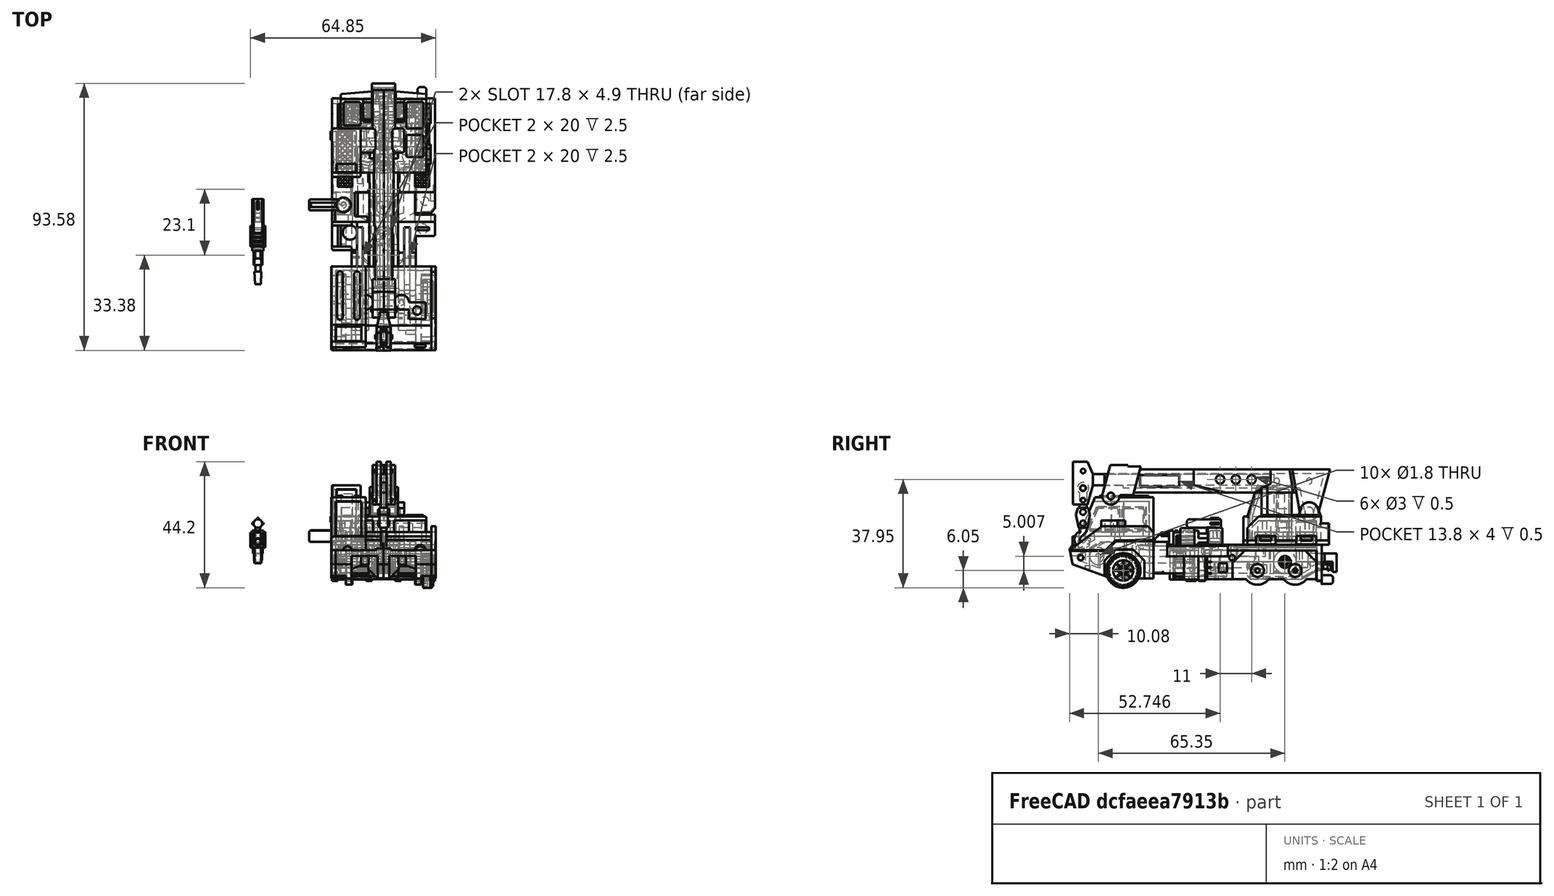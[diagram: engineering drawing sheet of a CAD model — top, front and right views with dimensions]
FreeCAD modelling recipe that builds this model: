
FCSTD DOCUMENT  (FreeCAD 1.0R39109 (Git))
Label: Hook
License: All rights reserved
LicenseURL: https://en.wikipedia.org/wiki/All_rights_reserved
objects: Sketcher::SketchObject×355, PartDesign::Pad×256, PartDesign::Pocket×171, PartDesign::Body×24, PartDesign::SubShapeBinder×17, PartDesign::Fillet×13, PartDesign::Chamfer×6, App::Link×5, Part::Mirroring×4, PartDesign::LinearPattern×2, App::Part×1, Part::Feature×1
note: 2098 computed .brp shape members not serialized (recipe doc carries the construction recipe); baked Part::Feature solids carry a one-line shape summary decoded from their .brp

FEATURE [Sketcher::SketchObject] Sketch
  ArcFitTolerance = 1e-06
  AttachmentSupport = -> [XY_Plane]
  FullyConstrained = true
  MakeInternals = false
  MapMode = 5
  sketch-geometry (4):
    g0: LineSegment StartX=0 StartY=0 StartZ=0 EndX=36 EndY=0 EndZ=0
    g1: LineSegment StartX=36 StartY=0 StartZ=0 EndX=36 EndY=43.2 EndZ=0
    g2: LineSegment StartX=36 StartY=43.2 StartZ=0 EndX=0 EndY=43.2 EndZ=0
    g3: LineSegment StartX=0 StartY=43.2 StartZ=0 EndX=0 EndY=0 EndZ=0
  constraints (11):
    c: Coincident(g0,g1)
    c: Coincident(g1,g2)
    c: Coincident(g2,g3)
    c: Coincident(g3,g0)
    c: Horizontal(g0)
    c: Horizontal(g2)
    c: Vertical(g1)
    c: Vertical(g3)
    c: Coincident(g0,g-1)
    c: DistanceY(g1,g1) = 43.2
    c: DistanceX(g2,g2) = 36
FEATURE [PartDesign::Pad] Pad
  Direction = (0,0,1)
  Length = 2
  Length2 = 10
  Profile = -> Sketch
  ReferenceAxis = -> Sketch [N_Axis]
  Refine = true
  Suppressed = false
  Type = 0
FEATURE [Sketcher::SketchObject] Sketch001
  ArcFitTolerance = 1e-06
  AttachmentSupport = -> [Pad]
  ExternalGeometry = -> [Pad]
  FullyConstrained = true
  MakeInternals = false
  MapMode = 5
  Placement = pos=(0,0,2) rot=(0,0,1;0rad)
  sketch-geometry (18):
    g0: LineSegment StartX=13.9 StartY=43.2 StartZ=0 EndX=13.9 EndY=41.4 EndZ=0
    g1: LineSegment StartX=13.9 StartY=41.4 StartZ=0 EndX=22.1 EndY=41.4 EndZ=0
    g2: LineSegment StartX=22.1 StartY=41.4 StartZ=0 EndX=22.1 EndY=43.2 EndZ=0
    g3: LineSegment StartX=22.1 StartY=43.2 StartZ=0 EndX=13.9 EndY=43.2 EndZ=0
    g4: LineSegment StartX=36 StartY=10.3 StartZ=0 EndX=23.6 EndY=10.3 EndZ=0
    g5: LineSegment StartX=23.6 StartY=10.3 StartZ=0 EndX=23.6 EndY=11.3 EndZ=0
    g6: ArcOfCircle CenterX=23.6 CenterY=12.55 CenterZ=0 NormalX=0 NormalY=0 NormalZ=1 AngleXU=0 Radius=1.25 StartAngle=1.5708 EndAngle=4.71239
    g7: LineSegment StartX=23.6 StartY=13.8 StartZ=0 EndX=23.6 EndY=18 EndZ=0
    g8: ArcOfCircle CenterX=18.1 CenterY=18 CenterZ=0 NormalX=0 NormalY=0 NormalZ=1 AngleXU=0 Radius=5.5 StartAngle=2e-16 EndAngle=3.14159
    g9: LineSegment StartX=12.6 StartY=18 StartZ=0 EndX=12.6 EndY=13.8 EndZ=0
    g10: ArcOfCircle CenterX=12.6 CenterY=12.55 CenterZ=0 NormalX=0 NormalY=0 NormalZ=1 AngleXU=0 Radius=1.25 StartAngle=4.71239 EndAngle=7.85398
    g11: LineSegment StartX=12.6 StartY=11.3 StartZ=0 EndX=12.6 EndY=10.3 EndZ=0
    g12: LineSegment StartX=12.6 StartY=10.3 StartZ=0 EndX=8 EndY=10.3 EndZ=0
    g13: LineSegment StartX=8 StartY=10.3 StartZ=0 EndX=8 EndY=1.8 EndZ=0
    g14: LineSegment StartX=8 StartY=1.8 StartZ=0 EndX=12.4 EndY=1.8 EndZ=0
    g15: LineSegment StartX=12.4 StartY=0 StartZ=0 EndX=36 EndY=0 EndZ=0
    g16: LineSegment StartX=36 StartY=0 StartZ=0 EndX=36 EndY=10.3 EndZ=0
    g17: LineSegment StartX=12.4 StartY=1.8 StartZ=0 EndX=12.4 EndY=0 EndZ=0
  constraints (58):
    c: Coincident(g0,g1)
    c: Coincident(g1,g2)
    c: Coincident(g2,g3)
    c: Coincident(g3,g0)
    c: Vertical(g0)
    c: Vertical(g2)
    c: Horizontal(g1)
    c: Horizontal(g3)
    c: PointOnObject(g0,g-3)
    c: DistanceX(g-3,g-3) = 36
    c: DistanceX(g-3,g0) = 13.9
    c: DistanceX(g2,g-3) = 13.9
    c: DistanceX(g0,g2) = 8.2
    c: DistanceY(g0,g0) = 1.8
    c: PointOnObject(g4,g-4)
    c: Horizontal(g4)
    c: DistanceY(g4,g-4) = 32.9
    c: DistanceX(g4,g4) = 12.4
    c: Coincident(g5,g4)
    c: Vertical(g5)
    c: Coincident(g6,g5)
    c: Coincident(g7,g6)
    c: Vertical(g7)
    c: Coincident(g8,g7)
    c: Coincident(g9,g8)
    c: Vertical(g9)
    c: Coincident(g10,g9)
    c: Coincident(g11,g10)
    c: Vertical(g11)
    c: Coincident(g12,g11)
    c: Horizontal(g12)
    c: Coincident(g13,g12)
    c: Vertical(g13)
    c: Coincident(g14,g13)
    c: Horizontal(g14)
    c: PointOnObject(g15,g-5)
    c: Coincident(g15,g-5)
    c: Coincident(g16,g15)
    c: Coincident(g16,g4)
    c: Diameter(g6) = 2.5
    c: Diameter(g10) = 2.5
    c: Diameter(g8) = 11
    c: DistanceX(g11,g4) = 11
    c: DistanceX(g6,g6) = 0
    c: DistanceX(g5,g6) = 0
    c: DistanceX(g10,g9) = 0
    c: DistanceX(g10,g10) = 0
    c: DistanceX(g-1,g13) = 8
    c: DistanceX(g13,g14) = 4.4
    c: Coincident(g17,g14)
    c: Coincident(g17,g15)
    c: Vertical(g17)
    c: DistanceY(g17,g17) = 1.8
    c: DistanceY(g15,g8) = 18
    c: DistanceY(g5,g5) = 1
    c: DistanceY(g11,g11) = 1
    c: DistanceY(g8,g7) = 0
    c: DistanceY(g12,g-6) = 32.9
FEATURE [PartDesign::Pocket] Pocket
  BaseFeature = -> Pad
  Direction = (0,0,-1)
  Length = 5
  Length2 = 5
  Profile = -> Sketch001
  ReferenceAxis = -> Sketch001 [N_Axis]
  Refine = true
  Suppressed = false
  Type = 0
FEATURE [Sketcher::SketchObject] Sketch002
  ArcFitTolerance = 1e-06
  AttachmentSupport = -> [Pocket]
  ExternalGeometry = -> [Pocket]
  FullyConstrained = true
  MakeInternals = false
  MapMode = 5
  Placement = pos=(0,0,2) rot=(0,0,1;0rad)
  sketch-geometry (8):
    g0: LineSegment StartX=2 StartY=41.2 StartZ=0 EndX=2 EndY=12.3 EndZ=0
    g1: LineSegment StartX=2 StartY=12.3 StartZ=0 EndX=7 EndY=12.3 EndZ=0
    g2: LineSegment StartX=7 StartY=12.3 StartZ=0 EndX=7 EndY=41.2 EndZ=0
    g3: LineSegment StartX=7 StartY=41.2 StartZ=0 EndX=2 EndY=41.2 EndZ=0
    g4: LineSegment StartX=29 StartY=41.2 StartZ=0 EndX=29 EndY=12.3 EndZ=0
    g5: LineSegment StartX=29 StartY=12.3 StartZ=0 EndX=34 EndY=12.3 EndZ=0
    g6: LineSegment StartX=34 StartY=12.3 StartZ=0 EndX=34 EndY=41.2 EndZ=0
    g7: LineSegment StartX=34 StartY=41.2 StartZ=0 EndX=29 EndY=41.2 EndZ=0
  constraints (25):
    c: Coincident(g0,g1)
    c: Coincident(g1,g2)
    c: Coincident(g2,g3)
    c: Coincident(g3,g0)
    c: Vertical(g0)
    c: Vertical(g2)
    c: Horizontal(g1)
    c: Horizontal(g3)
    c: Coincident(g4,g5)
    c: Coincident(g5,g6)
    c: Coincident(g6,g7)
    c: Coincident(g7,g4)
    c: Vertical(g4)
    c: Vertical(g6)
    c: Horizontal(g5)
    c: Horizontal(g7)
    c: DistanceX(g3,g3) = 5
    c: DistanceX(g7,g7) = 5
    c: DistanceX(g-6,g0) = 2
    c: DistanceX(g6,g-4) = 2
    c: DistanceY(g6,g-4) = 2
    c: DistanceY(g0,g-6) = 2
    c: DistanceY(g-3,g5) = 2
    c: DistanceY(g-7,g1) = 2
    c: DistanceY(g0,g0) = 28.9
FEATURE [PartDesign::Pocket] Pocket001
  BaseFeature = -> Pocket
  Direction = (0,0,-1)
  Length = 0.5
  Length2 = 5
  Profile = -> Sketch002
  ReferenceAxis = -> Sketch002 [N_Axis]
  Refine = true
  Suppressed = false
  Type = 0
FEATURE [Sketcher::SketchObject] Sketch003
  ArcFitTolerance = 1e-06
  AttachmentSupport = -> [Pocket001]
  ExternalGeometry = -> [Pocket001]
  FullyConstrained = true
  MakeInternals = false
  MapMode = 5
  Placement = pos=(0,0,1.5) rot=(0,0,1;0rad)
  sketch-geometry (36):
    g0: LineSegment StartX=30.625 StartY=41.2 StartZ=0 EndX=29.875 EndY=40.45 EndZ=0
    g1: LineSegment StartX=29.875 StartY=40.45 StartZ=0 EndX=30.625 EndY=39.7 EndZ=0
    g2: LineSegment StartX=30.625 StartY=39.7 StartZ=0 EndX=31.375 EndY=40.45 EndZ=0
    g3: LineSegment StartX=31.375 StartY=40.45 StartZ=0 EndX=30.625 EndY=41.2 EndZ=0
    g4: LineSegment [constr] StartX=29.875 StartY=40.45 StartZ=0 EndX=31.375 EndY=40.45 EndZ=0
    g5: LineSegment [constr] StartX=30.625 StartY=41.2 StartZ=0 EndX=30.625 EndY=39.7 EndZ=0
    g6: LineSegment StartX=31.625 StartY=40.45 StartZ=0 EndX=32.375 EndY=41.2 EndZ=0
    g7: LineSegment StartX=32.375 StartY=41.2 StartZ=0 EndX=33.125 EndY=40.45 EndZ=0
    g8: LineSegment StartX=33.125 StartY=40.45 StartZ=0 EndX=32.375 EndY=39.7 EndZ=0
    g9: LineSegment StartX=32.375 StartY=39.7 StartZ=0 EndX=31.625 EndY=40.45 EndZ=0
    g10: LineSegment [constr] StartX=32.375 StartY=41.2 StartZ=0 EndX=32.375 EndY=39.7 EndZ=0
    g11: LineSegment [constr] StartX=31.625 StartY=40.45 StartZ=0 EndX=33.125 EndY=40.45 EndZ=0
    g12: LineSegment StartX=29.625 StartY=40.45 StartZ=0 EndX=29 EndY=41.075 EndZ=0
    g13: LineSegment StartX=29 StartY=41.075 StartZ=0 EndX=29 EndY=39.825 EndZ=0
    g14: LineSegment StartX=29 StartY=39.825 StartZ=0 EndX=29.625 EndY=40.45 EndZ=0
    g15: LineSegment StartX=33.375 StartY=40.45 StartZ=0 EndX=34 EndY=41.075 EndZ=0
    g16: LineSegment StartX=34 StartY=41.075 StartZ=0 EndX=34 EndY=39.825 EndZ=0
    g17: LineSegment StartX=34 StartY=39.825 StartZ=0 EndX=33.375 EndY=40.45 EndZ=0
    g18: LineSegment StartX=3.625 StartY=41.2 StartZ=0 EndX=2.875 EndY=40.45 EndZ=0
    g19: LineSegment StartX=2.875 StartY=40.45 StartZ=0 EndX=3.625 EndY=39.7 EndZ=0
    g20: LineSegment StartX=3.625 StartY=39.7 StartZ=0 EndX=4.375 EndY=40.45 EndZ=0
    g21: LineSegment StartX=4.375 StartY=40.45 StartZ=0 EndX=3.625 EndY=41.2 EndZ=0
    g22: LineSegment [constr] StartX=2.875 StartY=40.45 StartZ=0 EndX=4.375 EndY=40.45 EndZ=0
    g23: LineSegment [constr] StartX=3.625 StartY=41.2 StartZ=0 EndX=3.625 EndY=39.7 EndZ=0
    g24: LineSegment StartX=4.625 StartY=40.45 StartZ=0 EndX=5.375 EndY=41.2 EndZ=0
    g25: LineSegment StartX=5.375 StartY=41.2 StartZ=0 EndX=6.125 EndY=40.45 EndZ=0
    g26: LineSegment StartX=6.125 StartY=40.45 StartZ=0 EndX=5.375 EndY=39.7 EndZ=0
    g27: LineSegment StartX=5.375 StartY=39.7 StartZ=0 EndX=4.625 EndY=40.45 EndZ=0
    g28: LineSegment [constr] StartX=5.375 StartY=41.2 StartZ=0 EndX=5.375 EndY=39.7 EndZ=0
    g29: LineSegment [constr] StartX=4.625 StartY=40.45 StartZ=0 EndX=6.125 EndY=40.45 EndZ=0
    g30: LineSegment StartX=2.625 StartY=40.45 StartZ=0 EndX=2 EndY=41.075 EndZ=0
    g31: LineSegment StartX=2 StartY=41.075 StartZ=0 EndX=2 EndY=39.825 EndZ=0
    g32: LineSegment StartX=2 StartY=39.825 StartZ=0 EndX=2.625 EndY=40.45 EndZ=0
    g33: LineSegment StartX=6.375 StartY=40.45 StartZ=0 EndX=7 EndY=41.075 EndZ=0
    g34: LineSegment StartX=7 StartY=41.075 StartZ=0 EndX=7 EndY=39.825 EndZ=0
    g35: LineSegment StartX=7 StartY=39.825 StartZ=0 EndX=6.375 EndY=40.45 EndZ=0
  constraints (101):
    c: DistanceX(g-3,g-3) = 5
    c: Coincident(g2,g1)
    c: Coincident(g3,g2)
    c: Coincident(g3,g0)
    c: Coincident(g4,g0)
    c: Coincident(g4,g2)
    c: Coincident(g5,g0)
    c: Coincident(g5,g1)
    c: Horizontal(g4)
    c: Vertical(g5)
    c: DistanceX(g4,g4) = 1.5
    c: Angle(g3,g2) = 1.5708
    c: Angle(g0,g3) = 1.5708
    c: Angle(g2,g1) = 1.5708
    c: Coincident(g1,g0)
    c: Coincident(g7,g6)
    c: Coincident(g8,g7)
    c: Coincident(g9,g8)
    c: Coincident(g9,g6)
    c: Coincident(g10,g6)
    c: Coincident(g10,g8)
    c: Coincident(g11,g6)
    c: Coincident(g11,g7)
    c: Horizontal(g11)
    c: Vertical(g10)
    c: DistanceX(g11,g11) = 1.5
    c: Angle(g7,g8) = 1.5708
    c: Angle(g6,g7) = 1.5708
    c: Angle(g8,g9) = 1.5708
    c: DistanceX(g2,g6) = 0.25
    c: DistanceY(g2,g6) = 0
    c: Coincident(g13,g12)
    c: Vertical(g13)
    c: Coincident(g14,g13)
    c: Coincident(g14,g12)
    c: DistanceX(g12,g0) = 0.25
    c: DistanceY(g12,g0) = 0
    c: Angle(g12,g14) = 1.5708
    c: Coincident(g16,g15)
    c: Vertical(g16)
    c: Coincident(g17,g16)
    c: Coincident(g17,g15)
    c: DistanceX(g7,g15) = 0.25
    c: DistanceY(g15,g7) = 0
    c: Angle(g17,g15) = 1.5708
    c: Angle(g13,g12) = 0.785398
    c: Angle(g15,g16) = 0.785398
    c: DistanceX(g15,g15) = 0.625
    c: DistanceX(g12,g12) = 0.625
    c: Coincident(g20,g19)
    c: Coincident(g21,g20)
    c: Coincident(g21,g18)
    c: Coincident(g22,g18)
    c: Coincident(g22,g20)
    c: Coincident(g23,g18)
    c: Coincident(g23,g19)
    c: Horizontal(g22)
    c: Vertical(g23)
    c: DistanceX(g22,g22) = 1.5
    c: Angle(g21,g20) = 1.5708
    c: Angle(g18,g21) = 1.5708
    c: Angle(g20,g19) = 1.5708
    c: Coincident(g19,g18)
    c: Coincident(g25,g24)
    c: Coincident(g26,g25)
    c: Coincident(g27,g26)
    c: Coincident(g27,g24)
    c: Coincident(g28,g24)
    c: Coincident(g28,g26)
    c: Coincident(g29,g24)
    c: Coincident(g29,g25)
    c: Horizontal(g29)
    c: Vertical(g28)
    c: DistanceX(g29,g29) = 1.5
    c: Angle(g25,g26) = 1.5708
    c: Angle(g24,g25) = 1.5708
    c: Angle(g26,g27) = 1.5708
    c: DistanceX(g20,g24) = 0.25
    c: DistanceY(g20,g24) = 0
    c: Coincident(g31,g30)
    c: Vertical(g31)
    c: Coincident(g32,g31)
    c: Coincident(g32,g30)
    c: DistanceX(g30,g18) = 0.25
    c: DistanceY(g30,g18) = 0
    c: Angle(g30,g32) = 1.5708
    c: Coincident(g34,g33)
    c: Vertical(g34)
    c: Coincident(g35,g34)
    c: Coincident(g35,g33)
    c: DistanceX(g25,g33) = 0.25
    c: DistanceY(g33,g25) = 0
    c: Angle(g35,g33) = 1.5708
    c: Angle(g31,g30) = 0.785398
    c: Angle(g33,g34) = 0.785398
    c: DistanceX(g33,g33) = 0.625
    c: DistanceX(g30,g30) = 0.625
    c: PointOnObject(g0,g-5)
    c: PointOnObject(g12,g-6)
    c: PointOnObject(g18,g-3)
    c: PointOnObject(g30,g-4)
FEATURE [PartDesign::Pocket] Pocket002
  BaseFeature = -> Pocket001
  Direction = (0,0,-1)
  Length = 0.5
  Length2 = 5
  Profile = -> Sketch003
  ReferenceAxis = -> Sketch003 [N_Axis]
  Refine = true
  Suppressed = false
  Type = 0
FEATURE [PartDesign::LinearPattern] LinearPattern
  BaseFeature = -> Pocket002
  Direction = -> Sketch003 [V_Axis]
  Length = 27.398
  Mode = 1
  Occurrences = 15
  Offset = 1.957
  Originals = -> [Pocket002]
  Refine = true
  Reversed = true
  Suppressed = false
  TransformMode = 0
FEATURE [Sketcher::SketchObject] Sketch004
  ArcFitTolerance = 1e-06
  AttachmentSupport = -> [LinearPattern]
  ExternalGeometry = -> [LinearPattern]
  FullyConstrained = true
  MakeInternals = false
  MapMode = 5
  Placement = pos=(0,0,1.5) rot=(0,0,1;0rad)
  sketch-geometry (36):
    g0: LineSegment StartX=2.125 StartY=41.2 StartZ=0 EndX=3.375 EndY=41.2 EndZ=0
    g1: LineSegment StartX=3.375 StartY=41.2 StartZ=0 EndX=2.75 EndY=40.575 EndZ=0
    g2: LineSegment StartX=2.75 StartY=40.575 StartZ=0 EndX=2.125 EndY=41.2 EndZ=0
    g3: LineSegment StartX=3.875 StartY=41.2 StartZ=0 EndX=5.125 EndY=41.2 EndZ=0
    g4: LineSegment StartX=5.125 StartY=41.2 StartZ=0 EndX=4.5 EndY=40.575 EndZ=0
    g5: LineSegment StartX=4.5 StartY=40.575 StartZ=0 EndX=3.875 EndY=41.2 EndZ=0
    g6: LineSegment StartX=5.625 StartY=41.2 StartZ=0 EndX=6.875 EndY=41.2 EndZ=0
    g7: LineSegment StartX=6.875 StartY=41.2 StartZ=0 EndX=6.25 EndY=40.575 EndZ=0
    g8: LineSegment StartX=6.25 StartY=40.575 StartZ=0 EndX=5.625 EndY=41.2 EndZ=0
    g9: LineSegment StartX=6.877 StartY=12.3 StartZ=0 EndX=5.623 EndY=12.3 EndZ=0
    g10: LineSegment StartX=5.623 StartY=12.3 StartZ=0 EndX=6.25 EndY=12.927 EndZ=0
    g11: LineSegment StartX=6.25 StartY=12.927 StartZ=0 EndX=6.877 EndY=12.3 EndZ=0
    g12: LineSegment StartX=3.873 StartY=12.3 StartZ=0 EndX=5.127 EndY=12.3 EndZ=0
    g13: LineSegment StartX=5.127 StartY=12.3 StartZ=0 EndX=4.5 EndY=12.927 EndZ=0
    g14: LineSegment StartX=4.5 StartY=12.927 StartZ=0 EndX=3.873 EndY=12.3 EndZ=0
    g15: LineSegment StartX=3.377 StartY=12.3 StartZ=0 EndX=2.123 EndY=12.3 EndZ=0
    g16: LineSegment StartX=2.123 StartY=12.3 StartZ=0 EndX=2.75 EndY=12.927 EndZ=0
    g17: LineSegment StartX=2.75 StartY=12.927 StartZ=0 EndX=3.377 EndY=12.3 EndZ=0
    g18: LineSegment StartX=29.125 StartY=41.2 StartZ=0 EndX=30.375 EndY=41.2 EndZ=0
    g19: LineSegment StartX=30.375 StartY=41.2 StartZ=0 EndX=29.75 EndY=40.575 EndZ=0
    g20: LineSegment StartX=29.75 StartY=40.575 StartZ=0 EndX=29.125 EndY=41.2 EndZ=0
    g21: LineSegment StartX=30.875 StartY=41.2 StartZ=0 EndX=32.125 EndY=41.2 EndZ=0
    g22: LineSegment StartX=32.125 StartY=41.2 StartZ=0 EndX=31.5 EndY=40.575 EndZ=0
    g23: LineSegment StartX=31.5 StartY=40.575 StartZ=0 EndX=30.875 EndY=41.2 EndZ=0
    g24: LineSegment StartX=32.625 StartY=41.2 StartZ=0 EndX=33.875 EndY=41.2 EndZ=0
    g25: LineSegment StartX=33.875 StartY=41.2 StartZ=0 EndX=33.25 EndY=40.575 EndZ=0
    g26: LineSegment StartX=33.25 StartY=40.575 StartZ=0 EndX=32.625 EndY=41.2 EndZ=0
    g27: LineSegment StartX=29.123 StartY=12.3 StartZ=0 EndX=30.377 EndY=12.3 EndZ=0
    g28: LineSegment StartX=30.377 StartY=12.3 StartZ=0 EndX=29.75 EndY=12.927 EndZ=0
    g29: LineSegment StartX=29.75 StartY=12.927 StartZ=0 EndX=29.123 EndY=12.3 EndZ=0
    g30: LineSegment StartX=30.873 StartY=12.3 StartZ=0 EndX=32.127 EndY=12.3 EndZ=0
    g31: LineSegment StartX=32.127 StartY=12.3 StartZ=0 EndX=31.5 EndY=12.927 EndZ=0
    g32: LineSegment StartX=31.5 StartY=12.927 StartZ=0 EndX=30.873 EndY=12.3 EndZ=0
    g33: LineSegment StartX=32.623 StartY=12.3 StartZ=0 EndX=33.877 EndY=12.3 EndZ=0
    g34: LineSegment StartX=33.877 StartY=12.3 StartZ=0 EndX=33.25 EndY=12.927 EndZ=0
    g35: LineSegment StartX=33.25 StartY=12.927 StartZ=0 EndX=32.623 EndY=12.3 EndZ=0
  constraints (109):
    c: PointOnObject(g0,g-5)
    c: PointOnObject(g0,g-5)
    c: Coincident(g1,g0)
    c: Coincident(g2,g1)
    c: Coincident(g2,g0)
    c: DistanceX(g-4,g-3) = 0.25
    c: DistanceX(g-4,g1) = 0.125
    c: DistanceY(g-4,g1) = 0.125
    c: Parallel(g1,g-3)
    c: Parallel(g2,g-4)
    c: PointOnObject(g3,g-6)
    c: PointOnObject(g3,g-6)
    c: Coincident(g4,g3)
    c: Coincident(g5,g4)
    c: Coincident(g5,g3)
    c: PointOnObject(g6,g-9)
    c: PointOnObject(g6,g-9)
    c: Coincident(g7,g6)
    c: Coincident(g8,g7)
    c: Coincident(g8,g6)
    c: DistanceX(g-7,g4) = 0.125
    c: DistanceX(g-10,g7) = 0.125
    c: Parallel(g-7,g5)
    c: Parallel(g4,g-8)
    c: Parallel(g-10,g8)
    c: Parallel(g7,g-11)
    c: DistanceY(g-7,g4) = 0.125
    c: DistanceY(g-10,g7) = 0.125
    c: PointOnObject(g9,g-14)
    c: PointOnObject(g9,g-14)
    c: Coincident(g10,g9)
    c: Coincident(g11,g10)
    c: Coincident(g11,g9)
    c: PointOnObject(g12,g-14)
    c: PointOnObject(g12,g-14)
    c: Coincident(g13,g12)
    c: Coincident(g14,g13)
    c: Coincident(g14,g12)
    c: PointOnObject(g15,g-14)
    c: PointOnObject(g15,g-14)
    c: Coincident(g16,g15)
    c: Coincident(g17,g16)
    c: Coincident(g17,g15)
    c: Parallel(g-13,g16)
    c: Parallel(g17,g-12)
    c: Parallel(g-16,g14)
    c: Parallel(g13,g-15)
    c: Parallel(g-17,g10)
    c: Parallel(g11,g-18)
    c: DistanceX(g-17,g10) = 0.125
    c: DistanceX(g-16,g13) = 0.125
    c: DistanceX(g16,g-12) = 0.125
    c: DistanceY(g16,g-13) = 0.125
    c: DistanceY(g13,g-16) = 0.125
    c: DistanceY(g10,g-17) = 0.125
    c: PointOnObject(g18,g-19)
    c: PointOnObject(g18,g-19)
    c: Coincident(g19,g18)
    c: Coincident(g20,g19)
    c: Coincident(g20,g18)
    c: PointOnObject(g21,g-22)
    c: PointOnObject(g21,g-22)
    c: Coincident(g22,g21)
    c: Coincident(g23,g22)
    c: Coincident(g23,g21)
    c: PointOnObject(g24,g-25)
    c: PointOnObject(g24,g-25)
    c: Coincident(g25,g24)
    c: Coincident(g26,g25)
    c: Coincident(g26,g24)
    c: Parallel(g-26,g26)
    c: Parallel(g25,g-27)
    c: Parallel(g22,g-24)
    c: Parallel(g23,g-23)
    c: Parallel(g-21,g19)
    c: Parallel(g20,g-20)
    c: DistanceX(g-20,g19) = 0.125
    c: DistanceX(g-23,g22) = 0.125
    c: DistanceX(g-26,g25) = 0.125
    c: DistanceY(g-26,g25) = 0.125
    c: DistanceY(g-23,g22) = 0.125
    c: DistanceY(g-20,g19) = 0.125
    c: PointOnObject(g27,g-30)
    c: PointOnObject(g27,g-30)
    c: Coincident(g28,g27)
    c: Coincident(g29,g28)
    c: Coincident(g29,g27)
    c: PointOnObject(g30,g-30)
    c: PointOnObject(g30,g-30)
    c: Coincident(g31,g30)
    c: Coincident(g32,g31)
    c: Coincident(g32,g30)
    c: PointOnObject(g33,g-30)
    c: PointOnObject(g33,g-30)
    c: Coincident(g34,g33)
    c: Coincident(g35,g34)
    c: Coincident(g35,g33)
    c: Parallel(g29,g-28)
    c: Parallel(g28,g-29)
    c: Parallel(g32,g-31)
    c: Parallel(g31,g-32)
    c: Parallel(g35,g-33)
    c: Parallel(g34,g-34)
    c: DistanceX(g-28,g28) = 0.125
    c: DistanceX(g-31,g31) = 0.125
    c: DistanceX(g-33,g34) = 0.125
    c: DistanceY(g28,g-28) = 0.125
    c: DistanceY(g31,g-31) = 0.125
    c: DistanceY(g34,g-33) = 0.125
FEATURE [PartDesign::Pocket] Pocket003
  BaseFeature = -> LinearPattern
  Direction = (0,0,-1)
  Length = 0.5
  Length2 = 5
  Profile = -> Sketch004
  ReferenceAxis = -> Sketch004 [N_Axis]
  Refine = true
  Suppressed = false
  Type = 0
FEATURE [Sketcher::SketchObject] Sketch005
  ArcFitTolerance = 1e-06
  AttachmentSupport = -> [Pocket003]
  ExternalGeometry = -> [Pocket003]
  FullyConstrained = true
  MakeInternals = false
  MapMode = 5
  Placement = pos=(0,0,1.5) rot=(0,0,1;0rad)
  sketch-geometry (36):
    g0: LineSegment StartX=2.75 StartY=40.22 StartZ=0 EndX=2 EndY=39.47 EndZ=0
    g1: LineSegment StartX=2 StartY=39.47 StartZ=0 EndX=2.75 EndY=38.72 EndZ=0
    g2: LineSegment StartX=2.75 StartY=38.72 StartZ=0 EndX=3.5 EndY=39.47 EndZ=0
    g3: LineSegment StartX=3.5 StartY=39.47 StartZ=0 EndX=2.75 EndY=40.22 EndZ=0
    g4: LineSegment StartX=4.5 StartY=40.22 StartZ=0 EndX=3.75 EndY=39.47 EndZ=0
    g5: LineSegment StartX=3.75 StartY=39.47 StartZ=0 EndX=4.5 EndY=38.72 EndZ=0
    g6: LineSegment StartX=4.5 StartY=38.72 StartZ=0 EndX=5.25 EndY=39.47 EndZ=0
    g7: LineSegment StartX=5.25 StartY=39.47 StartZ=0 EndX=4.5 EndY=40.22 EndZ=0
    g8: LineSegment StartX=6.25 StartY=40.22 StartZ=0 EndX=5.5 EndY=39.47 EndZ=0
    g9: LineSegment StartX=5.5 StartY=39.47 StartZ=0 EndX=6.25 EndY=38.72 EndZ=0
    g10: LineSegment StartX=6.25 StartY=38.72 StartZ=0 EndX=7 EndY=39.47 EndZ=0
    g11: LineSegment StartX=7 StartY=39.47 StartZ=0 EndX=6.25 EndY=40.22 EndZ=0
    g12: LineSegment [constr] StartX=6.25 StartY=40.22 StartZ=0 EndX=6.25 EndY=38.72 EndZ=0
    g13: LineSegment [constr] StartX=4.5 StartY=40.22 StartZ=0 EndX=4.5 EndY=38.72 EndZ=0
    g14: LineSegment [constr] StartX=2.75 StartY=40.22 StartZ=0 EndX=2.75 EndY=38.72 EndZ=0
    g15: LineSegment [constr] StartX=3.5 StartY=39.47 StartZ=0 EndX=2 EndY=39.47 EndZ=0
    g16: LineSegment [constr] StartX=5.25 StartY=39.47 StartZ=0 EndX=3.75 EndY=39.47 EndZ=0
    g17: LineSegment [constr] StartX=7 StartY=39.47 StartZ=0 EndX=5.5 EndY=39.47 EndZ=0
    g18: LineSegment StartX=29.75 StartY=40.22 StartZ=0 EndX=29 EndY=39.47 EndZ=0
    g19: LineSegment StartX=29 StartY=39.47 StartZ=0 EndX=29.75 EndY=38.72 EndZ=0
    g20: LineSegment StartX=29.75 StartY=38.72 StartZ=0 EndX=30.5 EndY=39.47 EndZ=0
    g21: LineSegment StartX=30.5 StartY=39.47 StartZ=0 EndX=29.75 EndY=40.22 EndZ=0
    g22: LineSegment StartX=31.5 StartY=40.22 StartZ=0 EndX=30.75 EndY=39.47 EndZ=0
    g23: LineSegment StartX=30.75 StartY=39.47 StartZ=0 EndX=31.5 EndY=38.72 EndZ=0
    g24: LineSegment StartX=31.5 StartY=38.72 StartZ=0 EndX=32.25 EndY=39.47 EndZ=0
    g25: LineSegment StartX=32.25 StartY=39.47 StartZ=0 EndX=31.5 EndY=40.22 EndZ=0
    g26: LineSegment StartX=33.25 StartY=40.22 StartZ=0 EndX=32.5 EndY=39.47 EndZ=0
    g27: LineSegment StartX=32.5 StartY=39.47 StartZ=0 EndX=33.25 EndY=38.72 EndZ=0
    g28: LineSegment StartX=33.25 StartY=38.72 StartZ=0 EndX=34 EndY=39.47 EndZ=0
    g29: LineSegment StartX=34 StartY=39.47 StartZ=0 EndX=33.25 EndY=40.22 EndZ=0
    g30: LineSegment [constr] StartX=30.5 StartY=39.47 StartZ=0 EndX=29 EndY=39.47 EndZ=0
    g31: LineSegment [constr] StartX=29.75 StartY=40.22 StartZ=0 EndX=29.75 EndY=38.72 EndZ=0
    g32: LineSegment [constr] StartX=31.5 StartY=40.22 StartZ=0 EndX=31.5 EndY=38.72 EndZ=0
    g33: LineSegment [constr] StartX=32.25 StartY=39.47 StartZ=0 EndX=30.75 EndY=39.47 EndZ=0
    g34: LineSegment [constr] StartX=33.25 StartY=40.22 StartZ=0 EndX=33.25 EndY=38.72 EndZ=0
    g35: LineSegment [constr] StartX=34 StartY=39.47 StartZ=0 EndX=32.5 EndY=39.47 EndZ=0
  constraints (97):
    c: Coincident(g1,g0)
    c: Coincident(g2,g1)
    c: Coincident(g3,g2)
    c: Coincident(g3,g0)
    c: Coincident(g5,g4)
    c: Coincident(g6,g5)
    c: Coincident(g7,g6)
    c: Coincident(g7,g4)
    c: Coincident(g9,g8)
    c: Coincident(g10,g9)
    c: Coincident(g11,g10)
    c: Coincident(g11,g8)
    c: Coincident(g12,g8)
    c: Coincident(g12,g9)
    c: Vertical(g12)
    c: Coincident(g13,g4)
    c: Coincident(g13,g5)
    c: Vertical(g13)
    c: Coincident(g14,g0)
    c: Coincident(g14,g1)
    c: Coincident(g15,g2)
    c: Coincident(g15,g0)
    c: Horizontal(g15)
    c: Coincident(g16,g6)
    c: Coincident(g16,g4)
    c: Horizontal(g16)
    c: Coincident(g17,g10)
    c: Coincident(g17,g8)
    c: Horizontal(g17)
    c: Vertical(g14)
    c: DistanceX(g15,g15) = 1.5
    c: DistanceX(g16,g16) = 1.5
    c: DistanceX(g17,g17) = 1.5
    c: Angle(g3,g2) = 1.5708
    c: Angle(g0,g3) = 1.5708
    c: Angle(g2,g1) = 1.5708
    c: Angle(g7,g6) = 1.5708
    c: Angle(g4,g7) = 1.5708
    c: Angle(g6,g5) = 1.5708
    c: Angle(g11,g10) = 1.5708
    c: Angle(g8,g11) = 1.5708
    c: Angle(g10,g9) = 1.5708
    c: PointOnObject(g10,g-15)
    c: PointOnObject(g0,g-16)
    c: DistanceY(g0,g-3) = 0.23
    c: DistanceY(g4,g-8) = 0.23
    c: DistanceY(g8,g-12) = 0.23
    c: DistanceX(g4,g-18) = 0
    c: DistanceY(g-6,g1) = 0.227
    c: Coincident(g19,g18)
    c: Coincident(g20,g19)
    c: Coincident(g21,g20)
    c: Coincident(g21,g18)
    c: Coincident(g23,g22)
    c: Coincident(g24,g23)
    c: Coincident(g25,g24)
    c: Coincident(g25,g22)
    c: Coincident(g27,g26)
    c: Coincident(g28,g27)
    c: Coincident(g29,g28)
    c: Coincident(g29,g26)
    c: Coincident(g30,g20)
    c: Coincident(g30,g18)
    c: Horizontal(g30)
    c: Coincident(g31,g18)
    c: Coincident(g31,g19)
    c: Coincident(g32,g22)
    c: Coincident(g32,g23)
    c: Vertical(g32)
    c: Coincident(g33,g24)
    c: Coincident(g33,g22)
    c: Horizontal(g33)
    c: Coincident(g34,g26)
    c: Coincident(g34,g27)
    c: Vertical(g34)
    c: Coincident(g35,g28)
    c: Coincident(g35,g26)
    c: Horizontal(g35)
    c: Vertical(g31)
    c: DistanceX(g30,g30) = 1.5
    c: DistanceX(g33,g33) = 1.5
    c: DistanceX(g35,g35) = 1.5
    c: Angle(g29,g28) = 1.5708
    c: Angle(g25,g24) = 1.5708
    c: Angle(g21,g20) = 1.5708
    c: Angle(g18,g21) = 1.5708
    c: Angle(g20,g19) = 1.5708
    c: Angle(g22,g25) = 1.5708
    c: Angle(g24,g23) = 1.5708
    c: Angle(g26,g29) = 1.5708
    c: Angle(g28,g27) = 1.5708
    c: PointOnObject(g18,g-32)
    c: PointOnObject(g28,g-33)
    c: DistanceX(g22,g-35) = 0
    c: DistanceY(g18,g-20) = 0.23
    c: DistanceY(g22,g-25) = 0.23
    c: DistanceY(g26,g-29) = 0.23
FEATURE [PartDesign::Pocket] Pocket004
  BaseFeature = -> Pocket003
  Direction = (0,0,-1)
  Length = 0.5
  Length2 = 5
  Profile = -> Sketch005
  ReferenceAxis = -> Sketch005 [N_Axis]
  Refine = true
  Suppressed = false
  Type = 0
FEATURE [PartDesign::LinearPattern] LinearPattern001
  BaseFeature = -> Pocket004
  Direction = -> Sketch005 [V_Axis]
  Length = 25.441
  Mode = 1
  Occurrences = 14
  Offset = 1.957
  Originals = -> [Pocket004]
  Refine = true
  Reversed = true
  Suppressed = false
  TransformMode = 0
FEATURE [Sketcher::SketchObject] Sketch006
  ArcFitTolerance = 1e-06
  AttachmentSupport = -> [LinearPattern001]
  ExternalGeometry = -> [LinearPattern001]
  FullyConstrained = true
  MakeInternals = false
  MapMode = 5
  Placement = pos=(0,0,2) rot=(0,0,1;0rad)
  sketch-geometry (1):
    g0: Circle CenterX=18.1 CenterY=30.5 CenterZ=0 NormalX=0 NormalY=0 NormalZ=1 AngleXU=0 Radius=5.5
  constraints (3):
    c: DistanceX(g0,g-3) = 0
    c: Diameter(g0) = 11
    c: DistanceY(g0,g-4) = 12.7
FEATURE [PartDesign::Pad] Pad001
  BaseFeature = -> LinearPattern001
  Direction = (0,0,1)
  Length = 3
  Length2 = 10
  Profile = -> Sketch006
  ReferenceAxis = -> Sketch006 [N_Axis]
  Refine = true
  Suppressed = false
  Type = 0
FEATURE [Sketcher::SketchObject] Sketch007
  ArcFitTolerance = 1e-06
  AttachmentSupport = -> [Pad001]
  ExternalGeometry = -> [Pad001]
  FullyConstrained = true
  MakeInternals = false
  MapMode = 5
  Placement = pos=(0,0,5) rot=(0,0,1;0rad)
  sketch-geometry (1):
    g0: Circle CenterX=18.1 CenterY=30.5 CenterZ=0 NormalX=0 NormalY=0 NormalZ=1 AngleXU=0 Radius=2.5
  constraints (2):
    c: Coincident(g0,g-3)
    c: Diameter(g0) = 5
FEATURE [PartDesign::Pocket] Pocket005
  BaseFeature = -> Pad001
  Direction = (0,0,-1)
  Length = 5
  Length2 = 5
  Profile = -> Sketch007
  ReferenceAxis = -> Sketch007 [N_Axis]
  Refine = true
  Suppressed = false
  Type = 0
FEATURE [Sketcher::SketchObject] Sketch008
  ArcFitTolerance = 1e-06
  AttachmentSupport = -> [Pocket005]
  ExternalGeometry = -> [Pocket005]
  FullyConstrained = true
  MakeInternals = false
  MapMode = 5
  Placement = pos=(0,0,0) rot=(1,0,0;3.14159rad)
  sketch-geometry (1):
    g0: Circle CenterX=18.1 CenterY=-30.5 CenterZ=0 NormalX=0 NormalY=0 NormalZ=1 AngleXU=0 Radius=3.45
  constraints (2):
    c: Coincident(g0,g-3)
    c: Diameter(g0) = 6.9
FEATURE [PartDesign::Pocket] Pocket006
  BaseFeature = -> Pocket005
  Direction = (0,0,1)
  Length = 3.1
  Length2 = 5
  Profile = -> Sketch008
  ReferenceAxis = -> Sketch008 [N_Axis]
  Refine = true
  Suppressed = false
  Type = 0
FEATURE [Sketcher::SketchObject] Sketch009
  ArcFitTolerance = 1e-06
  AttachmentSupport = -> [Pocket006]
  ExternalGeometry = -> [Pocket006]
  FullyConstrained = true
  MakeInternals = false
  MapMode = 5
  Placement = pos=(0,0,0) rot=(1,0,0;3.14159rad)
  sketch-geometry (8):
    g0: LineSegment StartX=0 StartY=-43.2 StartZ=0 EndX=13.9 EndY=-43.2 EndZ=0
    g1: LineSegment StartX=13.9 StartY=-43.2 StartZ=0 EndX=13.9 EndY=-41.4 EndZ=0
    g2: LineSegment StartX=13.9 StartY=-41.4 StartZ=0 EndX=0 EndY=-41.4 EndZ=0
    g3: LineSegment StartX=0 StartY=-41.4 StartZ=0 EndX=0 EndY=-43.2 EndZ=0
    g4: LineSegment StartX=36 StartY=-43.2 StartZ=0 EndX=36 EndY=-41.4 EndZ=0
    g5: LineSegment StartX=36 StartY=-41.4 StartZ=0 EndX=22.1 EndY=-41.4 EndZ=0
    g6: LineSegment StartX=22.1 StartY=-41.4 StartZ=0 EndX=22.1 EndY=-43.2 EndZ=0
    g7: LineSegment StartX=22.1 StartY=-43.2 StartZ=0 EndX=36 EndY=-43.2 EndZ=0
  constraints (20):
    c: Coincident(g0,g1)
    c: Coincident(g1,g2)
    c: Coincident(g2,g3)
    c: Coincident(g3,g0)
    c: Horizontal(g0)
    c: Horizontal(g2)
    c: Vertical(g1)
    c: Vertical(g3)
    c: Coincident(g0,g-8)
    c: Coincident(g1,g-6)
    c: Coincident(g4,g5)
    c: Coincident(g5,g6)
    c: Coincident(g6,g7)
    c: Coincident(g7,g4)
    c: Vertical(g4)
    c: Vertical(g6)
    c: Horizontal(g5)
    c: Horizontal(g7)
    c: Coincident(g4,g-4)
    c: Coincident(g5,g-5)
FEATURE [PartDesign::Pad] Pad002
  BaseFeature = -> Pocket006
  Direction = (0,0,-1)
  Length = 10.7
  Length2 = 10
  Profile = -> Sketch009
  ReferenceAxis = -> Sketch009 [N_Axis]
  Refine = true
  Suppressed = false
  Type = 0
FEATURE [Sketcher::SketchObject] Sketch010
  ArcFitTolerance = 1e-06
  AttachmentSupport = -> [Pad002]
  ExternalGeometry = -> [Pad002]
  FullyConstrained = true
  MakeInternals = false
  MapMode = 5
  Placement = pos=(0,0,-10.7) rot=(1,0,0;3.14159rad)
  sketch-geometry (8):
    g0: LineSegment StartX=2 StartY=-41.4 StartZ=0 EndX=2 EndY=-43.2 EndZ=0
    g1: LineSegment StartX=2 StartY=-43.2 StartZ=0 EndX=11.9 EndY=-43.2 EndZ=0
    g2: LineSegment StartX=11.9 StartY=-43.2 StartZ=0 EndX=11.9 EndY=-41.4 EndZ=0
    g3: LineSegment StartX=11.9 StartY=-41.4 StartZ=0 EndX=2 EndY=-41.4 EndZ=0
    g4: LineSegment StartX=24.1 StartY=-41.4 StartZ=0 EndX=24.1 EndY=-43.2 EndZ=0
    g5: LineSegment StartX=24.1 StartY=-43.2 StartZ=0 EndX=34 EndY=-43.2 EndZ=0
    g6: LineSegment StartX=34 StartY=-43.2 StartZ=0 EndX=34 EndY=-41.4 EndZ=0
    g7: LineSegment StartX=34 StartY=-41.4 StartZ=0 EndX=24.1 EndY=-41.4 EndZ=0
  constraints (24):
    c: Coincident(g0,g1)
    c: Coincident(g1,g2)
    c: Coincident(g2,g3)
    c: Coincident(g3,g0)
    c: Vertical(g0)
    c: Vertical(g2)
    c: Horizontal(g1)
    c: Horizontal(g3)
    c: PointOnObject(g0,g-8)
    c: PointOnObject(g1,g-9)
    c: Coincident(g4,g5)
    c: Coincident(g5,g6)
    c: Coincident(g6,g7)
    c: Coincident(g7,g4)
    c: Vertical(g4)
    c: Vertical(g6)
    c: Horizontal(g5)
    c: Horizontal(g7)
    c: PointOnObject(g4,g-3)
    c: PointOnObject(g5,g-5)
    c: DistanceX(g-6,g4) = 2
    c: DistanceX(g6,g-4) = 2
    c: DistanceX(g2,g-8) = 2
    c: DistanceX(g-10,g0) = 2
FEATURE [PartDesign::Pocket] Pocket007
  BaseFeature = -> Pad002
  Direction = (0,0,1)
  Length = 0.5
  Length2 = 5
  Profile = -> Sketch010
  ReferenceAxis = -> Sketch010 [N_Axis]
  Refine = true
  Suppressed = false
  Type = 0
FEATURE [Sketcher::SketchObject] Sketch011
  ArcFitTolerance = 1e-06
  AttachmentSupport = -> [Pocket007]
  ExternalGeometry = -> [Pocket007]
  FullyConstrained = true
  MakeInternals = false
  MapMode = 5
  Placement = pos=(0,43.2,0) rot=(0,0.707107,0.707107;3.14159rad)
  sketch-geometry (1):
    g0: Circle CenterX=-31.45 CenterY=-10.2 CenterZ=0 NormalX=0 NormalY=0 NormalZ=1 AngleXU=0 Radius=1.55
  constraints (3):
    c: PointOnObject(g0,g-3)
    c: Diameter(g0) = 3.1
    c: DistanceX(g-4,g0) = 4.55
FEATURE [PartDesign::Pad] Pad003
  BaseFeature = -> Pocket007
  Direction = (0,1,-2e-16)
  Length = 4
  Length2 = 10
  Profile = -> Sketch011
  ReferenceAxis = -> Sketch011 [N_Axis]
  Refine = true
  Suppressed = false
  Type = 0
FEATURE [PartDesign::Fillet] Fillet
  Base = -> Pad003 [Edge479]
  BaseFeature = -> Pad003
  Radius = 1
  Refine = true
  SupportTransform = false
  Suppressed = false
  UseAllEdges = false
FEATURE [Sketcher::SketchObject] Sketch012
  ArcFitTolerance = 1e-06
  AttachmentSupport = -> [Fillet]
  ExternalGeometry = -> [Fillet]
  FullyConstrained = true
  MakeInternals = false
  MapMode = 5
  Placement = pos=(0,0,0) rot=(1,0,0;3.14159rad)
  sketch-geometry (4):
    g0: LineSegment StartX=11.9 StartY=-41.4 StartZ=0 EndX=24.1 EndY=-41.4 EndZ=0
    g1: LineSegment StartX=24.1 StartY=-41.4 StartZ=0 EndX=24.1 EndY=-39.4 EndZ=0
    g2: LineSegment StartX=24.1 StartY=-39.4 StartZ=0 EndX=11.9 EndY=-39.4 EndZ=0
    g3: LineSegment StartX=11.9 StartY=-39.4 StartZ=0 EndX=11.9 EndY=-41.4 EndZ=0
  constraints (10):
    c: Coincident(g0,g1)
    c: Coincident(g1,g2)
    c: Coincident(g2,g3)
    c: Coincident(g3,g0)
    c: Horizontal(g2)
    c: Vertical(g1)
    c: Vertical(g3)
    c: DistanceY(g1,g1) = 2
    c: Coincident(g0,g-7)
    c: Coincident(g0,g-6)
FEATURE [PartDesign::Pad] Pad004
  BaseFeature = -> Fillet
  Direction = (0,0,-1)
  Length = 1
  Length2 = 10
  Profile = -> Sketch012
  ReferenceAxis = -> Sketch012 [N_Axis]
  Refine = true
  Suppressed = false
  Type = 0
FEATURE [Sketcher::SketchObject] Sketch013
  ArcFitTolerance = 1e-06
  AttachmentSupport = -> [Pad004]
  ExternalGeometry = -> [Pad004]
  FullyConstrained = true
  MakeInternals = false
  MapMode = 5
  Placement = pos=(0,0,0) rot=(1,0,0;3.14159rad)
  sketch-geometry (16):
    g0: LineSegment StartX=9 StartY=-41.4 StartZ=0 EndX=9 EndY=-38.4 EndZ=0
    g1: LineSegment StartX=9 StartY=-38.4 StartZ=0 EndX=13.75 EndY=-38.4 EndZ=0
    g2: ArcOfCircle CenterX=13.75 CenterY=-37.4 CenterZ=0 NormalX=0 NormalY=0 NormalZ=1 AngleXU=0 Radius=1 StartAngle=4.71239 EndAngle=7.85398
    g3: LineSegment StartX=13.75 StartY=-36.4 StartZ=0 EndX=9 EndY=-36.4 EndZ=0
    g4: LineSegment StartX=9 StartY=-36.4 StartZ=0 EndX=9 EndY=-34.4 EndZ=0
    g5: LineSegment StartX=9 StartY=-34.4 StartZ=0 EndX=7 EndY=-34.4 EndZ=0
    g6: LineSegment StartX=7 StartY=-34.4 StartZ=0 EndX=7 EndY=-41.4 EndZ=0
    g7: LineSegment StartX=7 StartY=-41.4 StartZ=0 EndX=9 EndY=-41.4 EndZ=0
    g8: LineSegment StartX=27 StartY=-41.4 StartZ=0 EndX=29 EndY=-41.4 EndZ=0
    g9: LineSegment StartX=29 StartY=-41.4 StartZ=0 EndX=29 EndY=-34.4 EndZ=0
    g10: LineSegment StartX=29 StartY=-34.4 StartZ=0 EndX=27 EndY=-34.4 EndZ=0
    g11: LineSegment StartX=27 StartY=-34.4 StartZ=0 EndX=27 EndY=-36.4 EndZ=0
    g12: LineSegment StartX=27 StartY=-36.4 StartZ=0 EndX=22.25 EndY=-36.4 EndZ=0
    g13: LineSegment StartX=27 StartY=-41.4 StartZ=0 EndX=27 EndY=-38.4 EndZ=0
    g14: LineSegment StartX=27 StartY=-38.4 StartZ=0 EndX=22.25 EndY=-38.4 EndZ=0
    g15: ArcOfCircle CenterX=22.25 CenterY=-37.4 CenterZ=0 NormalX=0 NormalY=0 NormalZ=1 AngleXU=0 Radius=1 StartAngle=1.5708 EndAngle=4.71239
  constraints (51):
    c: PointOnObject(g0,g-4)
    c: Vertical(g0)
    c: Coincident(g1,g0)
    c: Horizontal(g1)
    c: Coincident(g2,g1)
    c: Coincident(g3,g2)
    c: Horizontal(g3)
    c: Coincident(g4,g3)
    c: Vertical(g4)
    c: Coincident(g5,g4)
    c: Horizontal(g5)
    c: Coincident(g6,g5)
    c: PointOnObject(g6,g-4)
    c: Coincident(g7,g6)
    c: Coincident(g7,g0)
    c: Vertical(g6)
    c: PointOnObject(g8,g-3)
    c: Coincident(g9,g8)
    c: Vertical(g9)
    c: Coincident(g10,g9)
    c: Horizontal(g10)
    c: Coincident(g11,g10)
    c: Coincident(g12,g11)
    c: Horizontal(g12)
    c: Coincident(g13,g8)
    c: Vertical(g13)
    c: Coincident(g14,g13)
    c: Horizontal(g14)
    c: Coincident(g15,g14)
    c: Coincident(g15,g12)
    c: Vertical(g11)
    c: DistanceX(g10,g10) = 2
    c: DistanceX(g8,g8) = 2
    c: DistanceX(g5,g5) = 2
    c: DistanceX(g7,g7) = 2
    c: DistanceY(g0,g3) = 2
    c: DistanceY(g13,g11) = 2
    c: DistanceY(g6,g6) = 7
    c: DistanceY(g9,g9) = 7
    c: DistanceX(g-5,g6) = 7
    c: DistanceX(g8,g-6) = 7
    c: DistanceX(g2,g15) = 8.5
    c: DistanceX(g15,g12) = 0
    c: DistanceX(g15,g14) = 0
    c: DistanceX(g2,g2) = 0
    c: DistanceX(g-7,g15) = 0.15
    c: DistanceY(g-9,g0) = 1
    c: DistanceY(g-9,g13) = 1
    c: DistanceX(g2,g1) = 0
    c: DistanceX(g2,g-8) = 0.15
    c: PointOnObject(g8,g-3)
FEATURE [PartDesign::Pad] Pad005
  BaseFeature = -> Pad004
  Direction = (0,0,-1)
  Length = 4
  Length2 = 10
  Profile = -> Sketch013
  ReferenceAxis = -> Sketch013 [N_Axis]
  Refine = true
  Suppressed = false
  Type = 0
FEATURE [Sketcher::SketchObject] Sketch014
  ArcFitTolerance = 1e-06
  AttachmentSupport = -> [Pad005]
  ExternalGeometry = -> [Pad005]
  FullyConstrained = true
  MakeInternals = false
  MapMode = 5
  Placement = pos=(0,0,-4) rot=(1,0,0;3.14159rad)
  sketch-geometry (2):
    g0: Circle CenterX=13.75 CenterY=-37.4 CenterZ=0 NormalX=0 NormalY=0 NormalZ=1 AngleXU=0 Radius=1
    g1: Circle CenterX=22.25 CenterY=-37.4 CenterZ=0 NormalX=0 NormalY=0 NormalZ=1 AngleXU=0 Radius=1
  constraints (4):
    c: Coincident(g0,g-4)
    c: Equal(g0,g-4)
    c: Coincident(g1,g-3)
    c: Equal(g1,g-3)
FEATURE [PartDesign::Pad] Pad006
  BaseFeature = -> Pad005
  Direction = (0,0,-1)
  Length = 2
  Length2 = 10
  Profile = -> Sketch014
  ReferenceAxis = -> Sketch014 [N_Axis]
  Refine = true
  Suppressed = false
  Type = 0
FEATURE [Sketcher::SketchObject] Sketch015
  ArcFitTolerance = 1e-06
  AttachmentSupport = -> [Pad006]
  ExternalGeometry = -> [Pad006]
  FullyConstrained = true
  MakeInternals = false
  MapMode = 5
  Placement = pos=(0,0,0) rot=(1,0,0;3.14159rad)
  sketch-geometry (14):
    g0: LineSegment StartX=29 StartY=-10.3 StartZ=0 EndX=29 EndY=-26.3 EndZ=0
    g1: LineSegment StartX=29 StartY=-26.3 StartZ=0 EndX=27 EndY=-26.3 EndZ=0
    g2: LineSegment StartX=27 StartY=-26.3 StartZ=0 EndX=27 EndY=-13.3 EndZ=0
    g3: LineSegment StartX=27 StartY=-13.3 StartZ=0 EndX=25.5 EndY=-13.3 EndZ=0
    g4: LineSegment StartX=25.5 StartY=-13.3 StartZ=0 EndX=25.5 EndY=-20.0303 EndZ=0
    g5: LineSegment StartX=25.5 StartY=-20.0303 StartZ=0 EndX=24 EndY=-24.8 EndZ=0
    g6: LineSegment StartX=24 StartY=-24.8 StartZ=0 EndX=12 EndY=-24.8 EndZ=0
    g7: LineSegment StartX=12 StartY=-24.8 StartZ=0 EndX=10.5 EndY=-20.0303 EndZ=0
    g8: LineSegment StartX=10.5 StartY=-20.0303 StartZ=0 EndX=10.5 EndY=-13.3 EndZ=0
    g9: LineSegment StartX=10.5 StartY=-13.3 StartZ=0 EndX=9 EndY=-13.3 EndZ=0
    g10: LineSegment StartX=9 StartY=-13.3 StartZ=0 EndX=9 EndY=-26.3 EndZ=0
    g11: LineSegment StartX=9 StartY=-26.3 StartZ=0 EndX=7 EndY=-26.3 EndZ=0
    g12: LineSegment StartX=7 StartY=-26.3 StartZ=0 EndX=7 EndY=-10.3 EndZ=0
    g13: LineSegment StartX=7 StartY=-10.3 StartZ=0 EndX=29 EndY=-10.3 EndZ=0
  constraints (43):
    c: PointOnObject(g0,g-4)
    c: Vertical(g0)
    c: Coincident(g1,g0)
    c: Horizontal(g1)
    c: Coincident(g2,g1)
    c: Vertical(g2)
    c: Coincident(g3,g2)
    c: Horizontal(g3)
    c: Coincident(g4,g3)
    c: Vertical(g4)
    c: Coincident(g5,g4)
    c: Coincident(g6,g5)
    c: Horizontal(g6)
    c: Coincident(g7,g6)
    c: Coincident(g8,g7)
    c: Vertical(g8)
    c: Coincident(g9,g8)
    c: Horizontal(g9)
    c: Coincident(g10,g9)
    c: Vertical(g10)
    c: Coincident(g11,g10)
    c: Horizontal(g11)
    c: Coincident(g12,g11)
    c: Vertical(g12)
    c: Coincident(g13,g12)
    c: Coincident(g13,g0)
    c: Horizontal(g13)
    c: DistanceX(g-8,g0) = 0
    c: DistanceX(g11,g-7) = 0
    c: DistanceX(g11,g11) = 2
    c: DistanceX(g1,g1) = 2
    c: DistanceX(g9,g9) = 1.5
    c: DistanceX(g3,g3) = 1.5
    c: DistanceY(g-7,g11) = 8.1
    c: DistanceY(g-8,g0) = 8.1
    c: DistanceX(g6,g6) = 12
    c: DistanceY(g10,g6) = 1.5
    c: DistanceY(g9,g12) = 3
    c: DistanceY(g2,g0) = 3
    c: DistanceX(g10,g1) = 18
    c: DistanceX(g10,g6) = 3
    c: Distance(g7) = 5
    c: Distance(g5) = 5
FEATURE [PartDesign::Pad] Pad007
  BaseFeature = -> Pad006
  Direction = (0,0,-1)
  Length = 4
  Length2 = 10
  Profile = -> Sketch015
  ReferenceAxis = -> Sketch015 [N_Axis]
  Refine = true
  Suppressed = false
  Type = 0
FEATURE [Sketcher::SketchObject] Sketch016
  ArcFitTolerance = 1e-06
  AttachmentSupport = -> [Pad007]
  ExternalGeometry = -> [Pad007]
  FullyConstrained = true
  MakeInternals = false
  MapMode = 5
  Placement = pos=(0,0,-4) rot=(1,0,0;3.14159rad)
  sketch-geometry (1):
    g0: Circle CenterX=18 CenterY=-20.4 CenterZ=0 NormalX=0 NormalY=0 NormalZ=1 AngleXU=0 Radius=2.4
  constraints (5):
    c: Diameter(g0) = 4.8
    c: DistanceY(g-4,g0) = 4.4
    c: DistanceX(g-4,g-4) = 12
    c: DistanceX(g-4,g-4) = 12
    c: DistanceX(g-4,g0) = 6
FEATURE [PartDesign::Pad] Pad008
  BaseFeature = -> Pad007
  Direction = (0,0,-1)
  Length = 2.5
  Length2 = 10
  Profile = -> Sketch016
  ReferenceAxis = -> Sketch016 [N_Axis]
  Refine = true
  Suppressed = false
  Type = 0
FEATURE [Sketcher::SketchObject] Sketch017
  ArcFitTolerance = 1e-06
  AttachmentSupport = -> [Pad008]
  ExternalGeometry = -> [Pad008]
  FullyConstrained = true
  MakeInternals = false
  MapMode = 5
  Placement = pos=(0,0,-6.5) rot=(1,0,0;3.14159rad)
  sketch-geometry (1):
    g0: Circle CenterX=18 CenterY=-20.4 CenterZ=0 NormalX=0 NormalY=0 NormalZ=1 AngleXU=0 Radius=0.75
  constraints (2):
    c: Coincident(g0,g-3)
    c: Diameter(g0) = 1.5
FEATURE [PartDesign::Pocket] Pocket008
  BaseFeature = -> Pad008
  Direction = (0,0,1)
  Length = 7
  Length2 = 5
  Profile = -> Sketch017
  ReferenceAxis = -> Sketch017 [N_Axis]
  Refine = true
  Suppressed = false
  Type = 0
FEATURE [Sketcher::SketchObject] Sketch018
  ArcFitTolerance = 1e-06
  AttachmentSupport = -> [Pocket008]
  ExternalGeometry = -> [Pocket008]
  FullyConstrained = true
  MakeInternals = false
  MapMode = 5
  Placement = pos=(0,0,0) rot=(1,0,0;3.14159rad)
  sketch-geometry (4):
    g0: LineSegment StartX=0 StartY=0 StartZ=0 EndX=0 EndY=-10.3 EndZ=0
    g1: LineSegment StartX=0 StartY=-10.3 StartZ=0 EndX=9 EndY=-10.3 EndZ=0
    g2: LineSegment StartX=9 StartY=-10.3 StartZ=0 EndX=9 EndY=0 EndZ=0
    g3: LineSegment StartX=9 StartY=0 StartZ=0 EndX=0 EndY=0 EndZ=0
  constraints (11):
    c: Coincident(g0,g1)
    c: Coincident(g1,g2)
    c: Coincident(g2,g3)
    c: Coincident(g3,g0)
    c: Vertical(g0)
    c: Vertical(g2)
    c: Horizontal(g1)
    c: Horizontal(g3)
    c: Coincident(g0,g-1)
    c: PointOnObject(g1,g-4)
    c: DistanceX(g-5,g1) = 1
FEATURE [PartDesign::Pad] Pad009
  BaseFeature = -> Pocket008
  Direction = (0,0,-1)
  Length = 2
  Length2 = 10
  Profile = -> Sketch018
  ReferenceAxis = -> Sketch018 [N_Axis]
  Refine = true
  Suppressed = false
  Type = 0
FEATURE [Sketcher::SketchObject] Sketch019
  ArcFitTolerance = 1e-06
  AttachmentSupport = -> [Pad009]
  ExternalGeometry = -> [Pad009]
  FullyConstrained = true
  MakeInternals = false
  MapMode = 5
  Placement = pos=(0,0,-4) rot=(1,0,0;3.14159rad)
  sketch-geometry (4):
    g0: LineSegment StartX=7 StartY=-10.3 StartZ=0 EndX=29 EndY=-10.3 EndZ=0
    g1: LineSegment StartX=29 StartY=-10.3 StartZ=0 EndX=29 EndY=0 EndZ=0
    g2: LineSegment StartX=29 StartY=0 StartZ=0 EndX=7 EndY=0 EndZ=0
    g3: LineSegment StartX=7 StartY=0 StartZ=0 EndX=7 EndY=-10.3 EndZ=0
  constraints (10):
    c: Coincident(g0,g1)
    c: Coincident(g1,g2)
    c: Coincident(g2,g3)
    c: Coincident(g3,g0)
    c: Horizontal(g2)
    c: Vertical(g1)
    c: Vertical(g3)
    c: Coincident(g0,g-3)
    c: PointOnObject(g1,g-1)
    c: Coincident(g0,g-3)
FEATURE [PartDesign::Pad] Pad010
  BaseFeature = -> Pad009
  Direction = (0,0,-1)
  Length = 2
  Length2 = 10
  Profile = -> Sketch019
  ReferenceAxis = -> Sketch019 [N_Axis]
  Refine = true
  Reversed = true
  Suppressed = false
  Type = 0
FEATURE [PartDesign::Pad] Pad011
  BaseFeature = -> Pad010
  Direction = (0,0,-1)
  Length = 2
  Length2 = 10
  Profile = -> Pad010 [Face53]
  Refine = true
  Suppressed = false
  Type = 0
FEATURE [Sketcher::SketchObject] Sketch020
  ArcFitTolerance = 1e-06
  AttachmentSupport = -> [Pad011]
  ExternalGeometry = -> [Pad011]
  FullyConstrained = true
  MakeInternals = false
  MapMode = 5
  Placement = pos=(0,0,-2) rot=(1,0,0;3.14159rad)
  sketch-geometry (4):
    g0: LineSegment StartX=0 StartY=0 StartZ=0 EndX=0 EndY=-2.5 EndZ=0
    g1: LineSegment StartX=0 StartY=-2.5 StartZ=0 EndX=7 EndY=-2.5 EndZ=0
    g2: LineSegment StartX=7 StartY=-2.5 StartZ=0 EndX=7 EndY=0 EndZ=0
    g3: LineSegment StartX=7 StartY=0 StartZ=0 EndX=0 EndY=0 EndZ=0
  constraints (11):
    c: Coincident(g0,g1)
    c: Coincident(g1,g2)
    c: Coincident(g2,g3)
    c: Coincident(g3,g0)
    c: Vertical(g0)
    c: Vertical(g2)
    c: Horizontal(g1)
    c: Horizontal(g3)
    c: Coincident(g0,g-1)
    c: PointOnObject(g1,g-3)
    c: DistanceY(g0,g0) = 2.5
FEATURE [PartDesign::Pad] Pad012
  BaseFeature = -> Pad011
  Direction = (0,0,-1)
  Length = 8.7
  Length2 = 10
  Profile = -> Sketch020
  ReferenceAxis = -> Sketch020 [N_Axis]
  Refine = true
  Suppressed = false
  Type = 0
FEATURE [Sketcher::SketchObject] Sketch021
  ArcFitTolerance = 1e-06
  AttachmentSupport = -> [Pad012]
  ExternalGeometry = -> [Pad012]
  FullyConstrained = true
  MakeInternals = false
  MapMode = 5
  Placement = pos=(0,0,-10.7) rot=(1,0,0;3.14159rad)
  sketch-geometry (4):
    g0: LineSegment StartX=1.5 StartY=0 StartZ=0 EndX=1.5 EndY=-2.5 EndZ=0
    g1: LineSegment StartX=1.5 StartY=-2.5 StartZ=0 EndX=5.5 EndY=-2.5 EndZ=0
    g2: LineSegment StartX=5.5 StartY=-2.5 StartZ=0 EndX=5.5 EndY=0 EndZ=0
    g3: LineSegment StartX=5.5 StartY=0 StartZ=0 EndX=1.5 EndY=0 EndZ=0
  constraints (12):
    c: Coincident(g0,g1)
    c: Coincident(g1,g2)
    c: Coincident(g2,g3)
    c: Coincident(g3,g0)
    c: Vertical(g0)
    c: Vertical(g2)
    c: Horizontal(g1)
    c: Horizontal(g3)
    c: PointOnObject(g0,g-3)
    c: PointOnObject(g1,g-5)
    c: DistanceX(g2,g-4) = 1.5
    c: DistanceX(g-1,g0) = 1.5
FEATURE [PartDesign::Pocket] Pocket009
  BaseFeature = -> Pad012
  Direction = (0,0,1)
  Length = 0.5
  Length2 = 5
  Profile = -> Sketch021
  ReferenceAxis = -> Sketch021 [N_Axis]
  Refine = true
  Suppressed = false
  Type = 0
FEATURE [Sketcher::SketchObject] Sketch022
  ArcFitTolerance = 1e-06
  AttachmentSupport = -> [Pocket009]
  ExternalGeometry = -> [Pocket009]
  FullyConstrained = true
  MakeInternals = false
  MapMode = 5
  Placement = pos=(0,0,-2) rot=(0,0,1;0rad)
  sketch-geometry (4):
    g0: LineSegment StartX=29 StartY=0 StartZ=0 EndX=36 EndY=0 EndZ=0
    g1: LineSegment StartX=36 StartY=0 StartZ=0 EndX=36 EndY=2.5 EndZ=0
    g2: LineSegment StartX=36 StartY=2.5 StartZ=0 EndX=29 EndY=2.5 EndZ=0
    g3: LineSegment StartX=29 StartY=2.5 StartZ=0 EndX=29 EndY=0 EndZ=0
  constraints (11):
    c: Coincident(g0,g1)
    c: Coincident(g1,g2)
    c: Coincident(g2,g3)
    c: Coincident(g3,g0)
    c: Horizontal(g0)
    c: Horizontal(g2)
    c: Vertical(g1)
    c: Vertical(g3)
    c: DistanceX(g0,g0) = 7
    c: Coincident(g0,g-4)
    c: DistanceY(g1,g1) = 2.5
FEATURE [PartDesign::Pad] Pad013
  BaseFeature = -> Pocket009
  Direction = (0,0,1)
  Length = 8.7
  Length2 = 10
  Profile = -> Sketch022
  ReferenceAxis = -> Sketch022 [N_Axis]
  Refine = true
  Reversed = true
  Suppressed = false
  Type = 0
FEATURE [Sketcher::SketchObject] Sketch023
  ArcFitTolerance = 1e-06
  AttachmentSupport = -> [Pad013]
  ExternalGeometry = -> [Pad013]
  FullyConstrained = true
  MakeInternals = false
  MapMode = 5
  Placement = pos=(0,0,-10.7) rot=(1,0,0;3.14159rad)
  sketch-geometry (4):
    g0: LineSegment StartX=30.5 StartY=0 StartZ=0 EndX=30.5 EndY=-2.5 EndZ=0
    g1: LineSegment StartX=30.5 StartY=-2.5 StartZ=0 EndX=34.5 EndY=-2.5 EndZ=0
    g2: LineSegment StartX=34.5 StartY=-2.5 StartZ=0 EndX=34.5 EndY=0 EndZ=0
    g3: LineSegment StartX=34.5 StartY=0 StartZ=0 EndX=30.5 EndY=0 EndZ=0
  constraints (12):
    c: Coincident(g0,g1)
    c: Coincident(g1,g2)
    c: Coincident(g2,g3)
    c: Coincident(g3,g0)
    c: Vertical(g0)
    c: Vertical(g2)
    c: Horizontal(g1)
    c: Horizontal(g3)
    c: PointOnObject(g0,g-3)
    c: PointOnObject(g1,g-5)
    c: DistanceX(g2,g-4) = 1.5
    c: DistanceX(g-6,g0) = 1.5
FEATURE [PartDesign::Pocket] Pocket010
  BaseFeature = -> Pad013
  Direction = (0,0,1)
  Length = 0.5
  Length2 = 5
  Profile = -> Sketch023
  ReferenceAxis = -> Sketch023 [N_Axis]
  Refine = true
  Suppressed = false
  Type = 0
FEATURE [Sketcher::SketchObject] Sketch024
  ArcFitTolerance = 1e-06
  AttachmentSupport = -> [Pocket010]
  ExternalGeometry = -> [Pocket010]
  FullyConstrained = true
  MakeInternals = false
  MapMode = 5
  Placement = pos=(0,0,-2) rot=(0,0,1;0rad)
  sketch-geometry (1):
    g0: Circle CenterX=18 CenterY=4.95 CenterZ=0 NormalX=0 NormalY=0 NormalZ=1 AngleXU=0 Radius=2.45
  constraints (3):
    c: DistanceX(g0,g-3) = 0
    c: Diameter(g0) = 4.9
    c: DistanceY(g-4,g0) = 4.95
FEATURE [PartDesign::Pocket] Pocket011
  BaseFeature = -> Pocket010
  Direction = (0,0,-1)
  Length = 5
  Length2 = 5
  Profile = -> Sketch024
  ReferenceAxis = -> Sketch024 [N_Axis]
  Refine = true
  Suppressed = false
  Type = 0
FEATURE [Sketcher::SketchObject] Sketch025
  ArcFitTolerance = 1e-06
  AttachmentSupport = -> [Pocket011]
  ExternalGeometry = -> [Pocket011]
  FullyConstrained = true
  MakeInternals = false
  MapMode = 5
  Placement = pos=(0,0,2) rot=(0,0,1;0rad)
  sketch-geometry (4):
    g0: LineSegment StartX=0 StartY=0 StartZ=0 EndX=1 EndY=0 EndZ=0
    g1: LineSegment StartX=1 StartY=0 StartZ=0 EndX=1 EndY=7.9 EndZ=0
    g2: LineSegment StartX=1 StartY=7.9 StartZ=0 EndX=0 EndY=7.9 EndZ=0
    g3: LineSegment StartX=0 StartY=7.9 StartZ=0 EndX=0 EndY=0 EndZ=0
  constraints (11):
    c: Coincident(g0,g1)
    c: Coincident(g1,g2)
    c: Coincident(g2,g3)
    c: Coincident(g3,g0)
    c: Horizontal(g0)
    c: Horizontal(g2)
    c: Vertical(g1)
    c: Vertical(g3)
    c: Coincident(g0,g-1)
    c: DistanceX(g0,g0) = 1
    c: DistanceY(g1,g1) = 7.9
FEATURE [PartDesign::Pad] Pad014
  BaseFeature = -> Pocket011
  Direction = (0,0,1)
  Length = 0.8
  Length2 = 10
  Profile = -> Sketch025
  ReferenceAxis = -> Sketch025 [N_Axis]
  Refine = true
  Suppressed = false
  Type = 0
FEATURE [Sketcher::SketchObject] Sketch026
  ArcFitTolerance = 1e-06
  AttachmentSupport = -> [Pad014]
  ExternalGeometry = -> [Pad014]
  FullyConstrained = true
  MakeInternals = false
  MapMode = 5
  Placement = pos=(0,0,-2) rot=(1,0,0;3.14159rad)
  sketch-geometry (1):
    g0: Circle CenterX=4 CenterY=-5.9 CenterZ=0 NormalX=0 NormalY=0 NormalZ=1 AngleXU=0 Radius=2
  constraints (3):
    c: Diameter(g0) = 4
    c: DistanceY(g-5,g0) = 4.4
    c: DistanceX(g-5,g0) = 4
FEATURE [PartDesign::Pocket] Pocket012
  BaseFeature = -> Pad014
  Direction = (0,0,1)
  Length = 2
  Length2 = 5
  Profile = -> Sketch026
  ReferenceAxis = -> Sketch026 [N_Axis]
  Refine = true
  Suppressed = false
  Type = 0
FEATURE [Sketcher::SketchObject] Sketch027
  ArcFitTolerance = 1e-06
  AttachmentSupport = -> [Pocket012]
  ExternalGeometry = -> [Pocket012]
  FullyConstrained = true
  MakeInternals = false
  MapMode = 5
  Placement = pos=(0,0,0) rot=(1,0,0;3.14159rad)
  sketch-geometry (1):
    g0: Circle CenterX=4 CenterY=-5.9 CenterZ=0 NormalX=0 NormalY=0 NormalZ=1 AngleXU=0 Radius=1
  constraints (2):
    c: Coincident(g0,g-3)
    c: Diameter(g0) = 2
FEATURE [PartDesign::Pocket] Pocket013
  BaseFeature = -> Pocket012
  Direction = (0,0,1)
  Length = 5
  Length2 = 5
  Profile = -> Sketch027
  ReferenceAxis = -> Sketch027 [N_Axis]
  Refine = true
  Suppressed = false
  Type = 0
FEATURE [Sketcher::SketchObject] Sketch028
  ArcFitTolerance = 1e-06
  AttachmentSupport = -> [XY_Plane001]
  FullyConstrained = true
  MakeInternals = false
  MapMode = 5
  sketch-geometry (4):
    g0: LineSegment StartX=0 StartY=0 StartZ=0 EndX=63.3 EndY=0 EndZ=0
    g1: LineSegment StartX=63.3 StartY=0 StartZ=0 EndX=63.3 EndY=4 EndZ=0
    g2: LineSegment StartX=63.3 StartY=4 StartZ=0 EndX=0 EndY=4 EndZ=0
    g3: LineSegment StartX=0 StartY=4 StartZ=0 EndX=0 EndY=0 EndZ=0
  constraints (11):
    c: Coincident(g0,g1)
    c: Coincident(g1,g2)
    c: Coincident(g2,g3)
    c: Coincident(g3,g0)
    c: Horizontal(g0)
    c: Horizontal(g2)
    c: Vertical(g1)
    c: Vertical(g3)
    c: Coincident(g0,g-1)
    c: DistanceX(g2,g2) = 63.3
    c: DistanceY(g1,g1) = 4
FEATURE [PartDesign::Pad] Pad015
  Direction = (0,0,1)
  Length = 2.75
  Length2 = 10
  Profile = -> Sketch028
  ReferenceAxis = -> Sketch028 [N_Axis]
  Refine = true
  Suppressed = false
  Type = 0
FEATURE [Sketcher::SketchObject] Sketch029
  ArcFitTolerance = 1e-06
  AttachmentSupport = -> [Pad015]
  ExternalGeometry = -> [Pad015]
  FullyConstrained = true
  MakeInternals = false
  MapMode = 5
  Placement = pos=(0,0,2.75) rot=(0,0,1;0rad)
  sketch-geometry (4):
    g0: LineSegment StartX=63.3 StartY=4 StartZ=0 EndX=63.3 EndY=5 EndZ=0
    g1: LineSegment StartX=63.3 StartY=5 StartZ=0 EndX=58.3 EndY=5 EndZ=0
    g2: LineSegment StartX=58.3 StartY=5 StartZ=0 EndX=58.3 EndY=4 EndZ=0
    g3: LineSegment StartX=58.3 StartY=4 StartZ=0 EndX=63.3 EndY=4 EndZ=0
  constraints (11):
    c: Coincident(g0,g1)
    c: Coincident(g1,g2)
    c: Coincident(g2,g3)
    c: Coincident(g3,g0)
    c: Vertical(g0)
    c: Vertical(g2)
    c: Horizontal(g1)
    c: Horizontal(g3)
    c: Coincident(g0,g-3)
    c: DistanceX(g1,g1) = 5
    c: DistanceY(g2,g2) = 1
FEATURE [PartDesign::Pad] Pad016
  BaseFeature = -> Pad015
  Direction = (0,0,1)
  Length = 2.75
  Length2 = 10
  Profile = -> Sketch029
  ReferenceAxis = -> Sketch029 [N_Axis]
  Refine = true
  Reversed = true
  Suppressed = false
  Type = 0
FEATURE [Sketcher::SketchObject] Sketch030
  ArcFitTolerance = 1e-06
  AttachmentOffset = pos=(0,0,1.125) rot=(0,0,1;0rad)
  AttachmentSupport = -> [Pad016]
  ExternalGeometry = -> [Pad016]
  FullyConstrained = true
  MakeInternals = false
  MapMode = 5
  Placement = pos=(0,0,3.875) rot=(0,0,1;0rad)
  sketch-geometry (6):
    g0: LineSegment StartX=0 StartY=4 StartZ=0 EndX=-2 EndY=10.7 EndZ=0
    g1: LineSegment StartX=-2 StartY=10.7 StartZ=0 EndX=-7 EndY=10.7 EndZ=0
    g2: LineSegment StartX=-7 StartY=10.7 StartZ=0 EndX=-7 EndY=-4.3 EndZ=0
    g3: LineSegment StartX=-7 StartY=-4.3 StartZ=0 EndX=-2 EndY=-4.3 EndZ=0
    g4: LineSegment StartX=-2 StartY=-4.3 StartZ=0 EndX=0 EndY=0 EndZ=0
    g5: LineSegment StartX=0 StartY=4 StartZ=0 EndX=0 EndY=0 EndZ=0
  constraints (16):
    c: Coincident(g1,g0)
    c: Horizontal(g1)
    c: Coincident(g2,g1)
    c: Vertical(g2)
    c: Coincident(g3,g2)
    c: Horizontal(g3)
    c: Coincident(g4,g3)
    c: Coincident(g4,g-1)
    c: Coincident(g5,g0)
    c: Coincident(g5,g4)
    c: DistanceX(g2,g4) = 7
    c: DistanceY(g2,g2) = 15
    c: DistanceX(g1,g1) = 5
    c: DistanceX(g3,g3) = 5
    c: DistanceY(g3,g4) = 4.3
    c: Coincident(g0,g-3)
FEATURE [PartDesign::Pad] Pad017
  BaseFeature = -> Pad016
  Direction = (0,0,1)
  Length = 5
  Length2 = 10
  Profile = -> Sketch030
  ReferenceAxis = -> Sketch030 [N_Axis]
  Refine = true
  Reversed = true
  Suppressed = false
  Type = 0
FEATURE [Sketcher::SketchObject] Sketch031
  ArcFitTolerance = 1e-06
  AttachmentSupport = -> [Pad017]
  ExternalGeometry = -> [Pad017]
  FullyConstrained = true
  MakeInternals = false
  MapMode = 5
  Placement = pos=(0,0,0) rot=(1,0,0;1.5708rad)
  sketch-geometry (6):
    g0: LineSegment StartX=0 StartY=3.875 StartZ=0 EndX=0 EndY=2.75 EndZ=0
    g1: LineSegment StartX=0 StartY=2.75 StartZ=0 EndX=4 EndY=2.75 EndZ=0
    g2: LineSegment StartX=4 StartY=2.75 StartZ=0 EndX=0 EndY=3.875 EndZ=0
    g3: LineSegment StartX=0 StartY=0 StartZ=0 EndX=0 EndY=-1.125 EndZ=0
    g4: LineSegment StartX=0 StartY=-1.125 StartZ=0 EndX=4 EndY=0 EndZ=0
    g5: LineSegment StartX=4 StartY=0 StartZ=0 EndX=0 EndY=0 EndZ=0
  constraints (14):
    c: Coincident(g0,g-4)
    c: Coincident(g0,g-4)
    c: Coincident(g1,g0)
    c: PointOnObject(g1,g-3)
    c: Coincident(g2,g1)
    c: Coincident(g2,g0)
    c: Coincident(g3,g-1)
    c: Coincident(g3,g-6)
    c: Coincident(g4,g3)
    c: PointOnObject(g4,g-5)
    c: Coincident(g5,g4)
    c: Coincident(g5,g3)
    c: DistanceX(g1,g1) = 4
    c: DistanceX(g5,g5) = 4
FEATURE [PartDesign::Pad] Pad018
  BaseFeature = -> Pad017
  Direction = (0,-1,2e-16)
  Length = 4
  Length2 = 10
  Profile = -> Sketch031
  ReferenceAxis = -> Sketch031 [N_Axis]
  Refine = true
  Reversed = true
  Suppressed = false
  Type = 0
FEATURE [Sketcher::SketchObject] Sketch032
  ArcFitTolerance = 1e-06
  AttachmentSupport = -> [Pad018]
  ExternalGeometry = -> [Pad018]
  FullyConstrained = true
  MakeInternals = false
  MapMode = 5
  Placement = pos=(0,-4.3,0) rot=(1,0,0;1.5708rad)
  sketch-geometry (4):
    g0: LineSegment StartX=-7 StartY=2.375 StartZ=0 EndX=-7 EndY=0.375 EndZ=0
    g1: LineSegment StartX=-7 StartY=0.375 StartZ=0 EndX=0 EndY=0.375 EndZ=0
    g2: LineSegment StartX=0 StartY=0.375 StartZ=0 EndX=0 EndY=2.375 EndZ=0
    g3: LineSegment StartX=0 StartY=2.375 StartZ=0 EndX=-7 EndY=2.375 EndZ=0
  constraints (12):
    c: Coincident(g0,g1)
    c: Coincident(g1,g2)
    c: Coincident(g2,g3)
    c: Coincident(g3,g0)
    c: Vertical(g0)
    c: Vertical(g2)
    c: Horizontal(g1)
    c: Horizontal(g3)
    c: PointOnObject(g0,g-3)
    c: DistanceY(g0,g0) = 2
    c: DistanceY(g0,g-3) = 1.5
    c: PointOnObject(g2,g-2)
FEATURE [PartDesign::Pocket] Pocket014
  BaseFeature = -> Pad018
  Direction = (0,1,-2e-16)
  Length = 15
  Length2 = 5
  Profile = -> Sketch032
  ReferenceAxis = -> Sketch032 [N_Axis]
  Refine = true
  Suppressed = false
  Type = 0
FEATURE [Sketcher::SketchObject] Sketch033
  ArcFitTolerance = 1e-06
  AttachmentSupport = -> [Pocket014]
  ExternalGeometry = -> [Pocket014]
  FullyConstrained = true
  MakeInternals = false
  MapMode = 5
  Placement = pos=(0,0,3.875) rot=(0,0,1;0rad)
  sketch-geometry (2):
    g0: Circle CenterX=-3.5 CenterY=-1 CenterZ=0 NormalX=0 NormalY=0 NormalZ=1 AngleXU=0 Radius=0.8
    g1: Circle CenterX=-3.5 CenterY=9.2 CenterZ=0 NormalX=0 NormalY=0 NormalZ=1 AngleXU=0 Radius=0.8
  constraints (6):
    c: Diameter(g0) = 1.6
    c: Diameter(g1) = 1.6
    c: DistanceX(g1,g0) = 0
    c: DistanceY(g1,g-3) = 1.5
    c: DistanceX(g1,g-3) = 1.5
    c: DistanceY(g0,g-1) = 1
FEATURE [PartDesign::Pad] Pad019
  BaseFeature = -> Pocket014
  Direction = (0,0,1)
  Length = 0.5
  Length2 = 10
  Profile = -> Sketch033
  ReferenceAxis = -> Sketch033 [N_Axis]
  Refine = true
  Suppressed = false
  Type = 0
FEATURE [Sketcher::SketchObject] Sketch034
  ArcFitTolerance = 1e-06
  AttachmentSupport = -> [Pad019]
  ExternalGeometry = -> [Pad019]
  FullyConstrained = true
  MakeInternals = false
  MapMode = 5
  Placement = pos=(0,0,3.875) rot=(0,0,1;0rad)
  sketch-geometry (1):
    g0: Circle CenterX=-3.5 CenterY=5 CenterZ=0 NormalX=0 NormalY=0 NormalZ=1 AngleXU=0 Radius=1
  constraints (4):
    c: Diameter(g0) = 2
    c: DistanceY(g-3,g0) = 1
    c: DistanceX(g-4,g-3) = 7
    c: DistanceX(g0,g-3) = 3.5
FEATURE [PartDesign::Pocket] Pocket015
  BaseFeature = -> Pad019
  Direction = (0,0,-1)
  Length = 5
  Length2 = 5
  Profile = -> Sketch034
  ReferenceAxis = -> Sketch034 [N_Axis]
  Refine = true
  Suppressed = false
  Type = 0
FEATURE [Sketcher::SketchObject] Sketch035
  ArcFitTolerance = 1e-06
  AttachmentSupport = -> [Pocket015]
  ExternalGeometry = -> [Pocket015]
  FullyConstrained = true
  MakeInternals = false
  MapMode = 5
  Placement = pos=(0,0,-1.125) rot=(1,0,0;3.14159rad)
  sketch-geometry (2):
    g0: Circle CenterX=-3.5 CenterY=1 CenterZ=0 NormalX=0 NormalY=0 NormalZ=1 AngleXU=0 Radius=0.8
    g1: Circle CenterX=-3.5 CenterY=-9.2 CenterZ=0 NormalX=0 NormalY=0 NormalZ=1 AngleXU=0 Radius=0.8
  constraints (6):
    c: Diameter(g0) = 1.6
    c: Diameter(g1) = 1.6
    c: DistanceX(g0,g1) = 0
    c: DistanceY(g-1,g0) = 1
    c: DistanceX(g1,g-3) = 1.5
    c: DistanceY(g-3,g1) = 1.5
FEATURE [PartDesign::Pad] Pad020
  BaseFeature = -> Pocket015
  Direction = (0,0,-1)
  Length = 0.5
  Length2 = 10
  Profile = -> Sketch035
  ReferenceAxis = -> Sketch035 [N_Axis]
  Refine = true
  Suppressed = false
  Type = 0
FEATURE [PartDesign::SubShapeBinder] Binder
  BindCopyOnChange = 0
  BindMode = 2
  ClaimChildren = false
  Context = -> Body002 [Binder.]
  Fuse = false
  MakeFace = true
  OffsetFill = false
  OffsetIntersection = false
  OffsetJoinType = 0
  OffsetOpenResult = false
  PartialLoad = false
  Refine = true
  Relative = true
  _Version = 2
FEATURE [Sketcher::SketchObject] Sketch036
  ArcFitTolerance = 1e-06
  AttachmentSupport = -> [Binder]
  ExternalGeometry = -> [Binder]
  FullyConstrained = true
  MakeInternals = false
  MapMode = 5
  Placement = pos=(0,0,2.75) rot=(0,0,1;0rad)
  sketch-geometry (18):
    g0: LineSegment StartX=16.4156 StartY=-2.05 StartZ=0 EndX=83.023 EndY=-2.05 EndZ=0
    g1: LineSegment StartX=83.023 StartY=-2.05 StartZ=0 EndX=78.7784 EndY=13.7912 EndZ=0
    g2: ArcOfCircle CenterX=75.717 CenterY=12.7 CenterZ=0 NormalX=0 NormalY=0 NormalZ=1 AngleXU=0 Radius=3.25 StartAngle=0.3424 EndAngle=2.94413
    g3: LineSegment StartX=72.5302 StartY=13.3376 StartZ=0 EndX=71.2452 EndY=6.05 EndZ=0
    g4: LineSegment StartX=71.2452 StartY=6.05 StartZ=0 EndX=14.2452 EndY=6.05 EndZ=0
    g5: LineSegment StartX=14.2452 StartY=6.05 StartZ=0 EndX=14.004 EndY=6.95 EndZ=0
    g6: LineSegment StartX=14.004 StartY=6.95 StartZ=0 EndX=9.42121 EndY=6.95 EndZ=0
    g7: LineSegment StartX=9.42121 StartY=6.95 StartZ=0 EndX=9.13277 EndY=8.02646 EndZ=0
    g8: ArcOfCircle CenterX=6.23499 CenterY=7.25 CenterZ=0 NormalX=0 NormalY=0 NormalZ=1 AngleXU=0 Radius=3 StartAngle=0.261799 EndAngle=3.40339
    g9: LineSegment StartX=3.33722 StartY=6.47354 StartZ=0 EndX=6.02302 EndY=-3.55 EndZ=0
    g10: LineSegment StartX=16.6835 StartY=-3.05 StartZ=0 EndX=16.4156 EndY=-2.05 EndZ=0
    g11: LineSegment StartX=6.02302 StartY=-3.55 StartZ=0 EndX=12.2347 EndY=-3.55 EndZ=0
    g12: LineSegment StartX=12.2347 StartY=-3.55 StartZ=0 EndX=12.1007 EndY=-3.05 EndZ=0
    g13: LineSegment StartX=12.1007 StartY=-3.05 StartZ=0 EndX=16.6835 EndY=-3.05 EndZ=0
    g14: LineSegment [constr] StartX=14.2452 StartY=6.05 StartZ=0 EndX=16.4156 EndY=-2.05 EndZ=0
    g15: LineSegment [constr] StartX=9.42121 StartY=6.95 StartZ=0 EndX=12.1007 EndY=-3.05 EndZ=0
    g16: LineSegment [constr] StartX=6.23499 StartY=7.25 StartZ=0 EndX=3.33722 EndY=6.47354 EndZ=0
    g17: LineSegment [constr] StartX=6.23499 StartY=7.25 StartZ=0 EndX=9.13277 EndY=8.02646 EndZ=0
  constraints (53):
    c: Horizontal(g0)
    c: Coincident(g1,g0)
    c: Coincident(g2,g1)
    c: Coincident(g3,g2)
    c: Coincident(g4,g3)
    c: Horizontal(g4)
    c: Coincident(g5,g4)
    c: Coincident(g6,g5)
    c: Horizontal(g6)
    c: Coincident(g7,g6)
    c: Coincident(g8,g7)
    c: Coincident(g9,g8)
    c: Coincident(g10,g0)
    c: Coincident(g11,g9)
    c: Horizontal(g11)
    c: Coincident(g12,g11)
    c: Coincident(g13,g12)
    c: Coincident(g13,g10)
    c: Horizontal(g13)
    c: DistanceX(g9,g0) = 77
    c: DistanceY(g0,g4) = 8.1
    c: Diameter(g2) = 6.5
    c: Diameter(g8) = 6
    c: DistanceX(g4,g4) = 57
    c: DistanceY(g0,g2) = 14.75
    c: Angle(g1,g0) = 1.309
    c: Angle(g3,g1) = 0.436332
    c: Distance(g1) = 16.4
    c: Distance(g3) = 7.4
    c: Coincident(g14,g4)
    c: Coincident(g14,g0)
    c: Coincident(g15,g6)
    c: Coincident(g15,g12)
    c: Parallel(g7,g15)
    c: Parallel(g5,g14)
    c: Parallel(g10,g14)
    c: Parallel(g12,g15)
    c: Parallel(g15,g14)
    c: Parallel(g15,g9)
    c: Parallel(g1,g14)
    c: DistanceY(g-3,g-3) = 4
    c: DistanceY(g-3,g4) = 2.05
    c: DistanceY(g12,g5) = 10
    c: DistanceY(g10,g0) = 1
    c: DistanceY(g11,g12) = 0.5
    c: Coincident(g16,g8)
    c: Coincident(g16,g8)
    c: Coincident(g17,g8)
    c: Coincident(g17,g7)
    c: Angle(g16,g17) = 3.14159
    c: Angle(g17,g7) = 1.5708
    c: PointOnObject(g-3,g9)
    c: DistanceY(g9,g8) = 10.8
FEATURE [PartDesign::Pad] Pad021
  Direction = (0,0,1)
  Length = 1.5
  Length2 = 10
  Profile = -> Sketch036
  ReferenceAxis = -> Sketch036 [N_Axis]
  Refine = true
  Suppressed = false
  Type = 0
FEATURE [Sketcher::SketchObject] Sketch037
  ArcFitTolerance = 1e-06
  AttachmentSupport = -> [Pad021]
  ExternalGeometry = -> [Pad021]
  FullyConstrained = true
  MakeInternals = false
  MapMode = 5
  Placement = pos=(0,0,4.25) rot=(0,0,1;0rad)
  sketch-geometry (12):
    g0: LineSegment StartX=14.004 StartY=6.95 StartZ=0 EndX=16.6835 EndY=-3.05 EndZ=0
    g1: LineSegment StartX=16.6835 StartY=-3.05 StartZ=0 EndX=12.1007 EndY=-3.05 EndZ=0
    g2: LineSegment StartX=12.1007 StartY=-3.05 StartZ=0 EndX=12.2347 EndY=-3.55 EndZ=0
    g3: LineSegment StartX=12.2347 StartY=-3.55 StartZ=0 EndX=6.02302 EndY=-3.55 EndZ=0
    g4: LineSegment StartX=6.02302 StartY=-3.55 StartZ=0 EndX=3.33722 EndY=6.47354 EndZ=0
    g5: LineSegment StartX=14.004 StartY=6.95 StartZ=0 EndX=9.42121 EndY=6.95 EndZ=0
    g6: LineSegment StartX=9.42121 StartY=6.95 StartZ=0 EndX=9.13277 EndY=8.02646 EndZ=0
    g7: ArcOfCircle CenterX=6.23499 CenterY=7.25 CenterZ=0 NormalX=0 NormalY=0 NormalZ=1 AngleXU=0 Radius=3 StartAngle=0.261799 EndAngle=3.40339
    g8: LineSegment StartX=72.5302 StartY=13.3376 StartZ=0 EndX=69.8169 EndY=-2.05 EndZ=0
    g9: LineSegment StartX=78.7784 StartY=13.7912 StartZ=0 EndX=83.023 EndY=-2.05 EndZ=0
    g10: LineSegment StartX=83.023 StartY=-2.05 StartZ=0 EndX=69.8169 EndY=-2.05 EndZ=0
    g11: ArcOfCircle CenterX=75.717 CenterY=12.7 CenterZ=0 NormalX=0 NormalY=0 NormalZ=1 AngleXU=0 Radius=3.25 StartAngle=0.342399 EndAngle=2.94414
  constraints (27):
    c: Coincident(g0,g-7)
    c: Coincident(g0,g-10)
    c: Coincident(g1,g0)
    c: Coincident(g1,g-11)
    c: Coincident(g2,g1)
    c: Coincident(g2,g-11)
    c: Coincident(g3,g2)
    c: Coincident(g3,g-5)
    c: Coincident(g4,g3)
    c: Coincident(g4,g-4)
    c: Coincident(g5,g0)
    c: Coincident(g5,g-8)
    c: Coincident(g6,g5)
    c: Coincident(g6,g-8)
    c: Coincident(g7,g4)
    c: Coincident(g7,g6)
    c: Tangent(g7,g-3)
    c: Coincident(g8,g-14)
    c: PointOnObject(g8,g-15)
    c: Coincident(g9,g-14)
    c: Coincident(g9,g-15)
    c: Coincident(g10,g9)
    c: Coincident(g10,g8)
    c: PointOnObject(g-13,g8)
    c: Coincident(g11,g8)
    c: Coincident(g11,g9)
    c: Tangent(g11,g-14)
FEATURE [PartDesign::Pad] Pad022
  BaseFeature = -> Pad021
  Direction = (0,0,1)
  Length = 1
  Length2 = 10
  Profile = -> Sketch037
  ReferenceAxis = -> Sketch037 [N_Axis]
  Refine = true
  Suppressed = false
  Type = 0
FEATURE [PartDesign::Pad] Pad023
  BaseFeature = -> Pad022
  Direction = (0,0,1)
  Length = 1
  Length2 = 10
  Profile = -> Sketch037
  ReferenceAxis = -> Sketch037 [N_Axis]
  Refine = true
  Suppressed = false
  Type = 0
FEATURE [Sketcher::SketchObject] Sketch038
  ArcFitTolerance = 1e-06
  AttachmentSupport = -> [Pad023]
  ExternalGeometry = -> [Pad023]
  FullyConstrained = true
  MakeInternals = false
  MapMode = 5
  Placement = pos=(0,0,4.25) rot=(0,0,1;0rad)
  sketch-geometry (4):
    g0: LineSegment StartX=70.2452 StartY=6.05 StartZ=0 EndX=68.8169 EndY=-2.05 EndZ=0
    g1: LineSegment StartX=69.8169 StartY=-2.05 StartZ=0 EndX=68.8169 EndY=-2.05 EndZ=0
    g2: LineSegment StartX=69.8169 StartY=-2.05 StartZ=0 EndX=71.2452 EndY=6.05 EndZ=0
    g3: LineSegment StartX=70.2452 StartY=6.05 StartZ=0 EndX=71.2452 EndY=6.05 EndZ=0
  constraints (10):
    c: PointOnObject(g0,g-4)
    c: PointOnObject(g0,g-5)
    c: Coincident(g1,g-5)
    c: Coincident(g1,g0)
    c: Coincident(g2,g1)
    c: Coincident(g2,g-4)
    c: Coincident(g3,g0)
    c: Coincident(g3,g2)
    c: DistanceX(g3,g3) = 1
    c: DistanceX(g1,g1) = 1
FEATURE [PartDesign::Pad] Pad024
  BaseFeature = -> Pad023
  Direction = (0,0,1)
  Length = 1
  Length2 = 10
  Profile = -> Sketch038
  ReferenceAxis = -> Sketch038 [N_Axis]
  Refine = true
  Suppressed = false
  Type = 0
FEATURE [PartDesign::Chamfer] Chamfer
  Angle = 45
  Base = -> Pad024 [Edge52]
  BaseFeature = -> Pad024
  ChamferType = 0
  FlipDirection = false
  Refine = true
  Size = 0.99
  Size2 = 1
  SupportTransform = false
  Suppressed = false
  UseAllEdges = false
FEATURE [Sketcher::SketchObject] Sketch039
  ArcFitTolerance = 1e-06
  AttachmentSupport = -> [Chamfer]
  ExternalGeometry = -> [Chamfer,Binder]
  FullyConstrained = true
  MakeInternals = false
  MapMode = 5
  Placement = pos=(0,0,2.75) rot=(1,0,0;3.14159rad)
  sketch-geometry (28):
    g0: LineSegment StartX=71.2452 StartY=-6.05 StartZ=0 EndX=14.2452 EndY=-6.05 EndZ=0
    g1: LineSegment StartX=14.2452 StartY=-6.05 StartZ=0 EndX=14.004 EndY=-6.95 EndZ=0
    g2: LineSegment StartX=14.004 StartY=-6.95 StartZ=0 EndX=9.42121 EndY=-6.95 EndZ=0
    g3: LineSegment StartX=9.42121 StartY=-6.95 StartZ=0 EndX=9.13277 EndY=-8.02646 EndZ=0
    g4: LineSegment StartX=72.5038 StartY=-4.55 StartZ=0 EndX=10.6206 EndY=-4.55 EndZ=0
    g5: LineSegment StartX=81.0134 StartY=0.55 StartZ=0 EndX=5.21917 EndY=0.55 EndZ=0
    g6: LineSegment StartX=72.5038 StartY=-4.55 StartZ=0 EndX=74.0014 EndY=-13.0432 EndZ=0
    g7: ArcOfCircle CenterX=75.717 CenterY=-12.7 CenterZ=0 NormalX=0 NormalY=0 NormalZ=1 AngleXU=0 Radius=1.74961 StartAngle=3.33905 EndAngle=5.75206
    g8: LineSegment StartX=77.2256 StartY=-13.5862 StartZ=0 EndX=81.0134 EndY=0.55 EndZ=0
    g9: LineSegment [constr] StartX=79.9781 StartY=-3.3137 StartZ=0 EndX=81.4781 EndY=-3.71563 EndZ=0
    g10: LineSegment StartX=5.21917 StartY=0.55 StartZ=0 EndX=6.02302 EndY=3.55 EndZ=0
    g11: LineSegment StartX=83.023 StartY=2.05 StartZ=0 EndX=16.4156 EndY=2.05 EndZ=0
    g12: LineSegment StartX=16.4156 StartY=2.05 StartZ=0 EndX=16.6835 EndY=3.05 EndZ=0
    g13: LineSegment StartX=16.6835 StartY=3.05 StartZ=0 EndX=12.1007 EndY=3.05 EndZ=0
    g14: LineSegment StartX=12.1007 StartY=3.05 StartZ=0 EndX=12.2347 EndY=3.55 EndZ=0
    g15: LineSegment StartX=12.2347 StartY=3.55 StartZ=0 EndX=6.02302 EndY=3.55 EndZ=0
    g16: LineSegment StartX=6.02302 StartY=3.55 StartZ=0 EndX=5.21917 EndY=0.55 EndZ=0
    g17: LineSegment [constr] StartX=73.1565 StartY=-8.25155 StartZ=0 EndX=71.6793 EndY=-8.51202 EndZ=0
    g18: LineSegment [constr] StartX=72.5302 StartY=-13.3376 StartZ=0 EndX=74.0014 EndY=-13.0432 EndZ=0
    g19: LineSegment [constr] StartX=74.0014 StartY=-13.0432 StartZ=0 EndX=75.717 EndY=-12.7 EndZ=0
    g20: LineSegment StartX=10.6206 StartY=-4.55 StartZ=0 EndX=10.6206 EndY=-3.55 EndZ=0
    g21: LineSegment StartX=10.6206 StartY=-3.55 StartZ=0 EndX=4.12058 EndY=-3.55 EndZ=0
    g22: LineSegment StartX=4.12058 StartY=-3.55 StartZ=0 EndX=3.33722 EndY=-6.47354 EndZ=0
    g23: ArcOfCircle CenterX=6.23499 CenterY=-7.25 CenterZ=0 NormalX=0 NormalY=0 NormalZ=1 AngleXU=0 Radius=3 StartAngle=2.87979 EndAngle=6.02139
    g24: LineSegment StartX=71.2452 StartY=-6.05 StartZ=0 EndX=72.5302 EndY=-13.3376 EndZ=0
    g25: LineSegment StartX=83.023 StartY=2.05 StartZ=0 EndX=78.7784 EndY=-13.7912 EndZ=0
    g26: ArcOfCircle CenterX=75.717 CenterY=-12.7 CenterZ=0 NormalX=0 NormalY=0 NormalZ=1 AngleXU=0 Radius=3.25 StartAngle=3.33905 EndAngle=5.94078
    g27: LineSegment StartX=6.02302 StartY=3.55 StartZ=0 EndX=5.21917 EndY=0.55 EndZ=0
  constraints (72):
    c: Coincident(g0,g-10)
    c: Coincident(g0,g-9)
    c: Coincident(g1,g0)
    c: Coincident(g1,g-8)
    c: Coincident(g2,g1)
    c: Coincident(g2,g-8)
    c: Coincident(g3,g2)
    c: Coincident(g3,g-7)
    c: Horizontal(g4)
    c: Horizontal(g5)
    c: DistanceY(g5,g-11) = 1.5
    c: DistanceY(g0,g4) = 1.5
    c: Coincident(g6,g4)
    c: Coincident(g7,g6)
    c: Coincident(g8,g7)
    c: Coincident(g5,g8)
    c: Parallel(g-11,g8)
    c: PointOnObject(g9,g8)
    c: PointOnObject(g9,g-11)
    c: Distance(g5,g9) = 4
    c: Angle(g8,g9) = 1.5708
    c: DistanceX(g9,g9) = 1.5
    c: Coincident(g7,g-12)
    c: Parallel(g6,g-10)
    c: PointOnObject(g5,g-6)
    c: Coincident(g10,g5)
    c: Coincident(g10,g-6)
    c: Coincident(g11,g-11)
    c: Coincident(g11,g-3)
    c: Coincident(g12,g11)
    c: Coincident(g12,g-4)
    c: Coincident(g13,g12)
    c: Coincident(g13,g-4)
    c: Coincident(g14,g13)
    c: Coincident(g14,g-5)
    c: Coincident(g15,g14)
    c: Coincident(g15,g10)
    c: Coincident(g16,g10)
    c: Coincident(g16,g5)
    c: Radius(g-12) = 3.25
    c: PointOnObject(g17,g6)
    c: PointOnObject(g17,g-10)
    c: Angle(g17,g6) = 1.5708
    c: Distance(g17,g0) = 2.5
    c: Distance(g17) = 1.5
    c: Coincident(g18,g-12)
    c: Coincident(g18,g6)
    c: Coincident(g19,g6)
    c: Coincident(g19,g7)
    c: Angle(g19,g18) = 3.14159
    c: Coincident(g20,g4)
    c: Vertical(g20)
    c: Coincident(g21,g20)
    c: PointOnObject(g21,g-6)
    c: Horizontal(g21)
    c: Coincident(g22,g21)
    c: Coincident(g22,g-7)
    c: DistanceX(g21,g21) = 6.5
    c: DistanceY(g-13,g-13) = 1
    c: DistanceY(g20,g20) = 1
    c: Coincident(g23,g22)
    c: Coincident(g23,g3)
    c: Tangent(g23,g-7)
    c: Coincident(g24,g0)
    c: Coincident(g24,g18)
    c: Coincident(g25,g11)
    c: Coincident(g25,g-12)
    c: Coincident(g26,g25)
    c: Coincident(g26,g18)
    c: Tangent(g26,g-12)
    c: Coincident(g27,g10)
    c: Coincident(g27,g5)
FEATURE [PartDesign::Pad] Pad025
  BaseFeature = -> Chamfer
  Direction = (0,0,-1)
  Length = 1.425
  Length2 = 10
  Profile = -> Sketch039
  ReferenceAxis = -> Sketch039 [N_Axis]
  Refine = true
  Suppressed = false
  Type = 0
FEATURE [Sketcher::SketchObject] Sketch040
  ArcFitTolerance = 1e-06
  AttachmentSupport = -> [Pad025]
  ExternalGeometry = -> [Pad025]
  FullyConstrained = true
  MakeInternals = false
  MapMode = 5
  Placement = pos=(0,0,5.25) rot=(0,0,1;0rad)
  sketch-geometry (1):
    g0: Circle CenterX=75.717 CenterY=12.7 CenterZ=0 NormalX=0 NormalY=0 NormalZ=1 AngleXU=0 Radius=3.25
  constraints (2):
    c: Coincident(g0,g-3)
    c: Equal(g0,g-3)
FEATURE [PartDesign::Pad] Pad026
  BaseFeature = -> Pad025
  Direction = (0,0,1)
  Length = 0.25
  Length2 = 10
  Profile = -> Sketch040
  ReferenceAxis = -> Sketch040 [N_Axis]
  Refine = true
  Suppressed = false
  Type = 0
FEATURE [Sketcher::SketchObject] Sketch041
  ArcFitTolerance = 1e-06
  AttachmentSupport = -> [Pad026]
  ExternalGeometry = -> [Pad026]
  FullyConstrained = true
  MakeInternals = false
  MapMode = 5
  Placement = pos=(0,0,4.25) rot=(0,0,1;0rad)
  sketch-geometry (5):
    g0: LineSegment StartX=16.4156 StartY=4 StartZ=0 EndX=16.4156 EndY=9e-16 EndZ=0
    g1: LineSegment StartX=16.4156 StartY=9e-16 StartZ=0 EndX=30.2156 EndY=9e-16 EndZ=0
    g2: LineSegment StartX=30.2156 StartY=9e-16 StartZ=0 EndX=30.2156 EndY=4 EndZ=0
    g3: LineSegment StartX=30.2156 StartY=4 StartZ=0 EndX=16.4156 EndY=4 EndZ=0
    g4: LineSegment [constr] StartX=34.4156 StartY=6.05 StartZ=0 EndX=34.4156 EndY=-2.05 EndZ=0
  constraints (17):
    c: Coincident(g0,g1)
    c: Coincident(g1,g2)
    c: Coincident(g2,g3)
    c: Coincident(g3,g0)
    c: Vertical(g0)
    c: Vertical(g2)
    c: Horizontal(g1)
    c: Horizontal(g3)
    c: DistanceX(g3,g3) = 13.8
    c: DistanceY(g0,g0) = 4
    c: PointOnObject(g4,g-3)
    c: PointOnObject(g4,g-4)
    c: Vertical(g4)
    c: DistanceY(g4,g4) = 8.1
    c: DistanceX(g-4,g4) = 18
    c: DistanceY(g2,g4) = 2.05
    c: DistanceX(g-4,g0) = 0
FEATURE [PartDesign::Pocket] Pocket016
  BaseFeature = -> Pad026
  Direction = (0,0,-1)
  Length = 0.5
  Length2 = 5
  Profile = -> Sketch041
  ReferenceAxis = -> Sketch041 [N_Axis]
  Refine = true
  Suppressed = false
  Type = 0
FEATURE [Sketcher::SketchObject] Sketch042
  ArcFitTolerance = 1e-06
  AttachmentSupport = -> [Pocket016]
  ExternalGeometry = -> [Pocket016]
  FullyConstrained = true
  MakeInternals = false
  MapMode = 5
  Placement = pos=(0,0,4.25) rot=(0,0,1;0rad)
  sketch-geometry (6):
    g0: LineSegment StartX=35.2156 StartY=-2.05 StartZ=0 EndX=62.2156 EndY=-2.05 EndZ=0
    g1: LineSegment StartX=62.2156 StartY=-2.05 StartZ=0 EndX=62.2156 EndY=2.95 EndZ=0
    g2: LineSegment StartX=62.2156 StartY=2.95 StartZ=0 EndX=56.7156 EndY=6.05 EndZ=0
    g3: LineSegment StartX=56.7156 StartY=6.05 StartZ=0 EndX=46.7156 EndY=6.05 EndZ=0
    g4: LineSegment StartX=35.2156 StartY=-2.05 StartZ=0 EndX=35.2156 EndY=3.45 EndZ=0
    g5: LineSegment StartX=35.2156 StartY=3.45 StartZ=0 EndX=46.7156 EndY=6.05 EndZ=0
  constraints (18):
    c: PointOnObject(g0,g-4)
    c: PointOnObject(g0,g-4)
    c: Coincident(g1,g0)
    c: Vertical(g1)
    c: Coincident(g2,g1)
    c: PointOnObject(g2,g-3)
    c: Coincident(g3,g2)
    c: Coincident(g4,g0)
    c: Vertical(g4)
    c: Coincident(g5,g4)
    c: Coincident(g5,g3)
    c: DistanceX(g0,g0) = 27
    c: DistanceX(g3,g3) = 10
    c: DistanceY(g4,g4) = 5.5
    c: DistanceY(g1,g1) = 5
    c: DistanceX(g2,g1) = 5.5
    c: PointOnObject(g3,g-3)
    c: DistanceX(g-5,g0) = 5
FEATURE [PartDesign::Pad] Pad027
  BaseFeature = -> Pocket016
  Direction = (0,0,1)
  Length = 0.5
  Length2 = 10
  Profile = -> Sketch042
  ReferenceAxis = -> Sketch042 [N_Axis]
  Refine = true
  Suppressed = false
  Type = 0
FEATURE [Sketcher::SketchObject] Sketch043
  ArcFitTolerance = 1e-06
  AttachmentSupport = -> [Pad027]
  ExternalGeometry = -> [Pad027]
  FullyConstrained = true
  MakeInternals = false
  MapMode = 5
  Placement = pos=(0,0,4.75) rot=(0,0,1;0rad)
  sketch-geometry (3):
    g0: Circle CenterX=55.5156 CenterY=1.45 CenterZ=0 NormalX=0 NormalY=0 NormalZ=1 AngleXU=0 Radius=1.5
    g1: Circle CenterX=50.0156 CenterY=1.45 CenterZ=0 NormalX=0 NormalY=0 NormalZ=1 AngleXU=0 Radius=1.5
    g2: Circle CenterX=44.5156 CenterY=1.45 CenterZ=0 NormalX=0 NormalY=0 NormalZ=1 AngleXU=0 Radius=1.5
  constraints (9):
    c: Diameter(g2) = 3
    c: Diameter(g1) = 3
    c: Diameter(g0) = 3
    c: DistanceX(g1,g0) = 5.5
    c: DistanceX(g2,g1) = 5.5
    c: DistanceY(g0,g1) = 0
    c: DistanceY(g2,g1) = 0
    c: DistanceY(g0,g-3) = 1.5
    c: DistanceX(g0,g-3) = 6.7
FEATURE [PartDesign::Pocket] Pocket017
  BaseFeature = -> Pad027
  Direction = (0,0,-1)
  Length = 0.5
  Length2 = 5
  Profile = -> Sketch043
  ReferenceAxis = -> Sketch043 [N_Axis]
  Refine = true
  Suppressed = false
  Type = 0
FEATURE [Sketcher::SketchObject] Sketch044
  ArcFitTolerance = 1e-06
  AttachmentSupport = -> [Pocket017]
  ExternalGeometry = -> [Pocket017]
  FullyConstrained = true
  MakeInternals = false
  MapMode = 5
  Placement = pos=(0,0,5.25) rot=(0,0,1;0rad)
  sketch-geometry (1):
    g0: Circle CenterX=6.23499 CenterY=7.25 CenterZ=0 NormalX=0 NormalY=0 NormalZ=1 AngleXU=0 Radius=1
  constraints (2):
    c: Coincident(g0,g-3)
    c: Diameter(g0) = 2
FEATURE [PartDesign::Pad] Pad028
  BaseFeature = -> Pocket017
  Direction = (0,0,1)
  Length = 0.5
  Length2 = 10
  Profile = -> Sketch044
  ReferenceAxis = -> Sketch044 [N_Axis]
  Refine = true
  Suppressed = false
  Type = 0
FEATURE [Sketcher::SketchObject] Sketch045
  ArcFitTolerance = 1e-06
  AttachmentSupport = -> [Pad028]
  ExternalGeometry = -> [Pad028]
  FullyConstrained = true
  MakeInternals = false
  MapMode = 5
  Placement = pos=(0,0,5.5) rot=(0,0,1;0rad)
  sketch-geometry (1):
    g0: Circle CenterX=75.717 CenterY=12.7 CenterZ=0 NormalX=0 NormalY=0 NormalZ=1 AngleXU=0 Radius=1.5
  constraints (2):
    c: Coincident(g0,g-3)
    c: Diameter(g0) = 3
FEATURE [PartDesign::Pad] Pad029
  BaseFeature = -> Pad028
  Direction = (0,0,1)
  Length = 1.1
  Length2 = 10
  Profile = -> Sketch045
  ReferenceAxis = -> Sketch045 [N_Axis]
  Refine = true
  Suppressed = false
  Type = 0
FEATURE [Sketcher::SketchObject] Sketch046
  ArcFitTolerance = 1e-06
  AttachmentSupport = -> [Pad029]
  ExternalGeometry = -> [Pad029]
  FullyConstrained = true
  MakeInternals = false
  MapMode = 5
  Placement = pos=(0,0,2.75) rot=(1,0,0;3.14159rad)
  sketch-geometry (2):
    g0: Circle CenterX=64.3134 CenterY=-2 CenterZ=0 NormalX=0 NormalY=0 NormalZ=1 AngleXU=0 Radius=1
    g1: Circle CenterX=75.717 CenterY=-2 CenterZ=0 NormalX=0 NormalY=0 NormalZ=1 AngleXU=0 Radius=1
  constraints (7):
    c: Diameter(g0) = 2
    c: Diameter(g1) = 2
    c: DistanceY(g-4,g-3) = 5.1
    c: DistanceY(g0,g-3) = 2.55
    c: DistanceY(g0,g1) = 0
    c: DistanceX(g1,g-5) = 0
    c: DistanceX(g0,g-3) = 16.7
FEATURE [PartDesign::Pad] Pad030
  BaseFeature = -> Pad029
  Direction = (0,0,-1)
  Length = 2.7
  Length2 = 10
  Profile = -> Sketch046
  ReferenceAxis = -> Sketch046 [N_Axis]
  Refine = true
  Suppressed = false
  Type = 0
FEATURE [Sketcher::SketchObject] Sketch047
  ArcFitTolerance = 1e-06
  AttachmentSupport = -> [Pad030]
  ExternalGeometry = -> [Pad030]
  FullyConstrained = true
  MakeInternals = false
  MapMode = 5
  Placement = pos=(0,0,2.75) rot=(1,0,0;3.14159rad)
  sketch-geometry (1):
    g0: Circle CenterX=75.717 CenterY=-12.7 CenterZ=0 NormalX=0 NormalY=0 NormalZ=1 AngleXU=0 Radius=1.5
  constraints (2):
    c: Coincident(g0,g-3)
    c: Diameter(g0) = 3
FEATURE [PartDesign::Pad] Pad031
  BaseFeature = -> Pad030
  Direction = (0,0,-1)
  Length = 6.5
  Length2 = 10
  Profile = -> Sketch047
  ReferenceAxis = -> Sketch047 [N_Axis]
  Refine = true
  Suppressed = false
  Type = 0
FEATURE [Sketcher::SketchObject] Sketch048
  ArcFitTolerance = 1e-06
  AttachmentSupport = -> [Pad031]
  ExternalGeometry = -> [Pad031]
  FullyConstrained = true
  MakeInternals = false
  MapMode = 5
  Placement = pos=(0,0,2.75) rot=(1,0,0;3.14159rad)
  sketch-geometry (4):
    g0: LineSegment StartX=74.0014 StartY=-13.0432 StartZ=0 EndX=75.717 EndY=-12.7 EndZ=0
    g1: LineSegment StartX=75.717 StartY=-12.7 StartZ=0 EndX=77.4631 EndY=-12.7 EndZ=0
    g2: LineSegment StartX=77.4631 StartY=-12.7 StartZ=0 EndX=77.2256 EndY=-13.5862 EndZ=0
    g3: ArcOfCircle CenterX=75.717 CenterY=-12.7 CenterZ=0 NormalX=0 NormalY=0 NormalZ=1 AngleXU=0 Radius=1.7496 StartAngle=3.33905 EndAngle=5.75207
  constraints (10):
    c: Coincident(g0,g-4)
    c: Coincident(g0,g-4)
    c: Coincident(g1,g0)
    c: PointOnObject(g1,g-5)
    c: Horizontal(g1)
    c: Coincident(g2,g1)
    c: Coincident(g2,g-5)
    c: Coincident(g3,g0)
    c: Coincident(g3,g2)
    c: Tangent(g3,g-4)
FEATURE [PartDesign::Pad] Pad032
  BaseFeature = -> Pad031
  Direction = (0,0,-1)
  Length = 1.425
  Length2 = 10
  Profile = -> Sketch048
  ReferenceAxis = -> Sketch048 [N_Axis]
  Refine = true
  Suppressed = false
  Type = 0
FEATURE [Sketcher::SketchObject] Sketch049
  ArcFitTolerance = 1e-06
  AttachmentSupport = -> [Pad032]
  ExternalGeometry = -> [Pad032]
  FullyConstrained = true
  MakeInternals = false
  MapMode = 5
  Placement = pos=(0,0,1.325) rot=(1,0,0;3.14159rad)
  sketch-geometry (1):
    g0: Circle CenterX=6.23499 CenterY=-7.25 CenterZ=0 NormalX=0 NormalY=0 NormalZ=1 AngleXU=0 Radius=1.15
  constraints (2):
    c: Coincident(g0,g-3)
    c: Diameter(g0) = 2.3
FEATURE [PartDesign::Pad] Pad033
  BaseFeature = -> Pad032
  Direction = (0,0,-1)
  Length = 4.5
  Length2 = 10
  Profile = -> Sketch049
  ReferenceAxis = -> Sketch049 [N_Axis]
  Refine = true
  Suppressed = false
  Type = 0
FEATURE [PartDesign::SubShapeBinder] Binder001
  BindCopyOnChange = 0
  BindMode = 2
  ClaimChildren = false
  Context = -> Body003 [Binder001.]
  Fuse = false
  MakeFace = true
  OffsetFill = false
  OffsetIntersection = false
  OffsetJoinType = 0
  OffsetOpenResult = false
  PartialLoad = false
  Refine = true
  Relative = true
  _Version = 2
FEATURE [Sketcher::SketchObject] Sketch050
  ArcFitTolerance = 1e-06
  AttachmentSupport = -> [Binder001]
  ExternalGeometry = -> [Binder001]
  FullyConstrained = true
  MakeInternals = false
  MapMode = 5
  Placement = pos=(0,0,2.75) rot=(0,0,1;0rad)
  sketch-geometry (18):
    g0: LineSegment StartX=16.4156 StartY=-2.05 StartZ=0 EndX=83.023 EndY=-2.05 EndZ=0
    g1: LineSegment StartX=83.023 StartY=-2.05 StartZ=0 EndX=78.7784 EndY=13.7912 EndZ=0
    g2: ArcOfCircle CenterX=75.717 CenterY=12.7 CenterZ=0 NormalX=0 NormalY=0 NormalZ=1 AngleXU=0 Radius=3.25 StartAngle=0.3424 EndAngle=2.94413
    g3: LineSegment StartX=72.5302 StartY=13.3376 StartZ=0 EndX=71.2452 EndY=6.05 EndZ=0
    g4: LineSegment StartX=71.2452 StartY=6.05 StartZ=0 EndX=14.2452 EndY=6.05 EndZ=0
    g5: LineSegment StartX=14.2452 StartY=6.05 StartZ=0 EndX=14.004 EndY=6.95 EndZ=0
    g6: LineSegment StartX=14.004 StartY=6.95 StartZ=0 EndX=9.42121 EndY=6.95 EndZ=0
    g7: LineSegment StartX=9.42121 StartY=6.95 StartZ=0 EndX=9.13277 EndY=8.02646 EndZ=0
    g8: ArcOfCircle CenterX=6.23499 CenterY=7.25 CenterZ=0 NormalX=0 NormalY=0 NormalZ=1 AngleXU=0 Radius=3 StartAngle=0.261799 EndAngle=3.40339
    g9: LineSegment StartX=3.33722 StartY=6.47354 StartZ=0 EndX=6.02302 EndY=-3.55 EndZ=0
    g10: LineSegment StartX=16.6835 StartY=-3.05 StartZ=0 EndX=16.4156 EndY=-2.05 EndZ=0
    g11: LineSegment StartX=6.02302 StartY=-3.55 StartZ=0 EndX=12.2347 EndY=-3.55 EndZ=0
    g12: LineSegment StartX=12.2347 StartY=-3.55 StartZ=0 EndX=12.1007 EndY=-3.05 EndZ=0
    g13: LineSegment StartX=12.1007 StartY=-3.05 StartZ=0 EndX=16.6835 EndY=-3.05 EndZ=0
    g14: LineSegment [constr] StartX=14.2452 StartY=6.05 StartZ=0 EndX=16.4156 EndY=-2.05 EndZ=0
    g15: LineSegment [constr] StartX=9.42121 StartY=6.95 StartZ=0 EndX=12.1007 EndY=-3.05 EndZ=0
    g16: LineSegment [constr] StartX=6.23499 StartY=7.25 StartZ=0 EndX=3.33722 EndY=6.47354 EndZ=0
    g17: LineSegment [constr] StartX=6.23499 StartY=7.25 StartZ=0 EndX=9.13277 EndY=8.02646 EndZ=0
  constraints (53):
    c: Horizontal(g0)
    c: Coincident(g1,g0)
    c: Coincident(g2,g1)
    c: Coincident(g3,g2)
    c: Coincident(g4,g3)
    c: Horizontal(g4)
    c: Coincident(g5,g4)
    c: Coincident(g6,g5)
    c: Horizontal(g6)
    c: Coincident(g7,g6)
    c: Coincident(g8,g7)
    c: Coincident(g9,g8)
    c: Coincident(g10,g0)
    c: Coincident(g11,g9)
    c: Horizontal(g11)
    c: Coincident(g12,g11)
    c: Coincident(g13,g12)
    c: Coincident(g13,g10)
    c: Horizontal(g13)
    c: DistanceX(g9,g0) = 77
    c: DistanceY(g0,g4) = 8.1
    c: Diameter(g2) = 6.5
    c: Diameter(g8) = 6
    c: DistanceX(g4,g4) = 57
    c: DistanceY(g0,g2) = 14.75
    c: Angle(g1,g0) = 1.309
    c: Angle(g3,g1) = 0.436332
    c: Distance(g1) = 16.4
    c: Distance(g3) = 7.4
    c: Coincident(g14,g4)
    c: Coincident(g14,g0)
    c: Coincident(g15,g6)
    c: Coincident(g15,g12)
    c: Parallel(g7,g15)
    c: Parallel(g5,g14)
    c: Parallel(g10,g14)
    c: Parallel(g12,g15)
    c: Parallel(g15,g14)
    c: Parallel(g15,g9)
    c: Parallel(g1,g14)
    c: DistanceY(g-3,g-3) = 4
    c: DistanceY(g-3,g4) = 2.05
    c: DistanceY(g12,g5) = 10
    c: DistanceY(g10,g0) = 1
    c: DistanceY(g11,g12) = 0.5
    c: Coincident(g16,g8)
    c: Coincident(g16,g8)
    c: Coincident(g17,g8)
    c: Coincident(g17,g7)
    c: Angle(g16,g17) = 3.14159
    c: Angle(g17,g7) = 1.5708
    c: PointOnObject(g-3,g9)
    c: DistanceY(g9,g8) = 10.8
FEATURE [PartDesign::Pad] Pad034
  Direction = (0,0,1)
  Length = 1.5
  Length2 = 10
  Profile = -> Sketch050
  ReferenceAxis = -> Sketch050 [N_Axis]
  Refine = true
  Suppressed = false
  Type = 0
FEATURE [Sketcher::SketchObject] Sketch051
  ArcFitTolerance = 1e-06
  AttachmentSupport = -> [Pad034]
  ExternalGeometry = -> [Pad034]
  FullyConstrained = true
  MakeInternals = false
  MapMode = 5
  Placement = pos=(0,0,4.25) rot=(0,0,1;0rad)
  sketch-geometry (12):
    g0: LineSegment StartX=14.004 StartY=6.95 StartZ=0 EndX=16.6835 EndY=-3.05 EndZ=0
    g1: LineSegment StartX=16.6835 StartY=-3.05 StartZ=0 EndX=12.1007 EndY=-3.05 EndZ=0
    g2: LineSegment StartX=12.1007 StartY=-3.05 StartZ=0 EndX=12.2347 EndY=-3.55 EndZ=0
    g3: LineSegment StartX=12.2347 StartY=-3.55 StartZ=0 EndX=6.02302 EndY=-3.55 EndZ=0
    g4: LineSegment StartX=6.02302 StartY=-3.55 StartZ=0 EndX=3.33722 EndY=6.47354 EndZ=0
    g5: LineSegment StartX=14.004 StartY=6.95 StartZ=0 EndX=9.42121 EndY=6.95 EndZ=0
    g6: LineSegment StartX=9.42121 StartY=6.95 StartZ=0 EndX=9.13277 EndY=8.02646 EndZ=0
    g7: ArcOfCircle CenterX=6.23499 CenterY=7.25 CenterZ=0 NormalX=0 NormalY=0 NormalZ=1 AngleXU=0 Radius=3 StartAngle=0.261799 EndAngle=3.40339
    g8: LineSegment StartX=72.5302 StartY=13.3376 StartZ=0 EndX=69.8169 EndY=-2.05 EndZ=0
    g9: LineSegment StartX=78.7784 StartY=13.7912 StartZ=0 EndX=83.023 EndY=-2.05 EndZ=0
    g10: LineSegment StartX=83.023 StartY=-2.05 StartZ=0 EndX=69.8169 EndY=-2.05 EndZ=0
    g11: ArcOfCircle CenterX=75.717 CenterY=12.7 CenterZ=0 NormalX=0 NormalY=0 NormalZ=1 AngleXU=0 Radius=3.25 StartAngle=0.342399 EndAngle=2.94414
  constraints (27):
    c: Coincident(g0,g-7)
    c: Coincident(g0,g-10)
    c: Coincident(g1,g0)
    c: Coincident(g1,g-11)
    c: Coincident(g2,g1)
    c: Coincident(g2,g-11)
    c: Coincident(g3,g2)
    c: Coincident(g3,g-5)
    c: Coincident(g4,g3)
    c: Coincident(g4,g-4)
    c: Coincident(g5,g0)
    c: Coincident(g5,g-8)
    c: Coincident(g6,g5)
    c: Coincident(g6,g-8)
    c: Coincident(g7,g4)
    c: Coincident(g7,g6)
    c: Tangent(g7,g-3)
    c: Coincident(g8,g-14)
    c: PointOnObject(g8,g-15)
    c: Coincident(g9,g-14)
    c: Coincident(g9,g-15)
    c: Coincident(g10,g9)
    c: Coincident(g10,g8)
    c: PointOnObject(g-13,g8)
    c: Coincident(g11,g8)
    c: Coincident(g11,g9)
    c: Tangent(g11,g-14)
FEATURE [PartDesign::Pad] Pad035
  BaseFeature = -> Pad034
  Direction = (0,0,1)
  Length = 1
  Length2 = 10
  Profile = -> Sketch051
  ReferenceAxis = -> Sketch051 [N_Axis]
  Refine = true
  Suppressed = false
  Type = 0
FEATURE [PartDesign::Pad] Pad036
  BaseFeature = -> Pad035
  Direction = (0,0,1)
  Length = 1
  Length2 = 10
  Profile = -> Sketch051
  ReferenceAxis = -> Sketch051 [N_Axis]
  Refine = true
  Suppressed = false
  Type = 0
FEATURE [Sketcher::SketchObject] Sketch052
  ArcFitTolerance = 1e-06
  AttachmentSupport = -> [Pad036]
  ExternalGeometry = -> [Pad036]
  FullyConstrained = true
  MakeInternals = false
  MapMode = 5
  Placement = pos=(0,0,4.25) rot=(0,0,1;0rad)
  sketch-geometry (4):
    g0: LineSegment StartX=70.2452 StartY=6.05 StartZ=0 EndX=68.8169 EndY=-2.05 EndZ=0
    g1: LineSegment StartX=69.8169 StartY=-2.05 StartZ=0 EndX=68.8169 EndY=-2.05 EndZ=0
    g2: LineSegment StartX=69.8169 StartY=-2.05 StartZ=0 EndX=71.2452 EndY=6.05 EndZ=0
    g3: LineSegment StartX=70.2452 StartY=6.05 StartZ=0 EndX=71.2452 EndY=6.05 EndZ=0
  constraints (10):
    c: PointOnObject(g0,g-4)
    c: PointOnObject(g0,g-5)
    c: Coincident(g1,g-5)
    c: Coincident(g1,g0)
    c: Coincident(g2,g1)
    c: Coincident(g2,g-4)
    c: Coincident(g3,g0)
    c: Coincident(g3,g2)
    c: DistanceX(g3,g3) = 1
    c: DistanceX(g1,g1) = 1
FEATURE [PartDesign::Pad] Pad037
  BaseFeature = -> Pad036
  Direction = (0,0,1)
  Length = 1
  Length2 = 10
  Profile = -> Sketch052
  ReferenceAxis = -> Sketch052 [N_Axis]
  Refine = true
  Suppressed = false
  Type = 0
FEATURE [PartDesign::Chamfer] Chamfer001
  Angle = 45
  Base = -> Pad037 [Edge52]
  BaseFeature = -> Pad037
  ChamferType = 0
  FlipDirection = false
  Refine = true
  Size = 0.99
  Size2 = 1
  SupportTransform = false
  Suppressed = false
  UseAllEdges = false
FEATURE [Sketcher::SketchObject] Sketch053
  ArcFitTolerance = 1e-06
  AttachmentSupport = -> [Chamfer001]
  ExternalGeometry = -> [Chamfer001,Binder001]
  FullyConstrained = true
  MakeInternals = false
  MapMode = 5
  Placement = pos=(0,0,2.75) rot=(1,0,0;3.14159rad)
  sketch-geometry (28):
    g0: LineSegment StartX=71.2452 StartY=-6.05 StartZ=0 EndX=14.2452 EndY=-6.05 EndZ=0
    g1: LineSegment StartX=14.2452 StartY=-6.05 StartZ=0 EndX=14.004 EndY=-6.95 EndZ=0
    g2: LineSegment StartX=14.004 StartY=-6.95 StartZ=0 EndX=9.42121 EndY=-6.95 EndZ=0
    g3: LineSegment StartX=9.42121 StartY=-6.95 StartZ=0 EndX=9.13277 EndY=-8.02646 EndZ=0
    g4: LineSegment StartX=72.5038 StartY=-4.55 StartZ=0 EndX=10.6206 EndY=-4.55 EndZ=0
    g5: LineSegment StartX=81.0134 StartY=0.55 StartZ=0 EndX=5.21917 EndY=0.55 EndZ=0
    g6: LineSegment StartX=72.5038 StartY=-4.55 StartZ=0 EndX=74.0014 EndY=-13.0432 EndZ=0
    g7: ArcOfCircle CenterX=75.717 CenterY=-12.7 CenterZ=0 NormalX=0 NormalY=0 NormalZ=1 AngleXU=0 Radius=1.74961 StartAngle=3.33905 EndAngle=5.75206
    g8: LineSegment StartX=77.2256 StartY=-13.5862 StartZ=0 EndX=81.0134 EndY=0.55 EndZ=0
    g9: LineSegment [constr] StartX=79.9781 StartY=-3.3137 StartZ=0 EndX=81.4781 EndY=-3.71563 EndZ=0
    g10: LineSegment StartX=5.21917 StartY=0.55 StartZ=0 EndX=6.02302 EndY=3.55 EndZ=0
    g11: LineSegment StartX=83.023 StartY=2.05 StartZ=0 EndX=16.4156 EndY=2.05 EndZ=0
    g12: LineSegment StartX=16.4156 StartY=2.05 StartZ=0 EndX=16.6835 EndY=3.05 EndZ=0
    g13: LineSegment StartX=16.6835 StartY=3.05 StartZ=0 EndX=12.1007 EndY=3.05 EndZ=0
    g14: LineSegment StartX=12.1007 StartY=3.05 StartZ=0 EndX=12.2347 EndY=3.55 EndZ=0
    g15: LineSegment StartX=12.2347 StartY=3.55 StartZ=0 EndX=6.02302 EndY=3.55 EndZ=0
    g16: LineSegment StartX=6.02302 StartY=3.55 StartZ=0 EndX=5.21917 EndY=0.55 EndZ=0
    g17: LineSegment [constr] StartX=73.1565 StartY=-8.25155 StartZ=0 EndX=71.6793 EndY=-8.51202 EndZ=0
    g18: LineSegment [constr] StartX=72.5302 StartY=-13.3376 StartZ=0 EndX=74.0014 EndY=-13.0432 EndZ=0
    g19: LineSegment [constr] StartX=74.0014 StartY=-13.0432 StartZ=0 EndX=75.717 EndY=-12.7 EndZ=0
    g20: LineSegment StartX=10.6206 StartY=-4.55 StartZ=0 EndX=10.6206 EndY=-3.55 EndZ=0
    g21: LineSegment StartX=10.6206 StartY=-3.55 StartZ=0 EndX=4.12058 EndY=-3.55 EndZ=0
    g22: LineSegment StartX=4.12058 StartY=-3.55 StartZ=0 EndX=3.33722 EndY=-6.47354 EndZ=0
    g23: ArcOfCircle CenterX=6.23499 CenterY=-7.25 CenterZ=0 NormalX=0 NormalY=0 NormalZ=1 AngleXU=0 Radius=3 StartAngle=2.87979 EndAngle=6.02139
    g24: LineSegment StartX=71.2452 StartY=-6.05 StartZ=0 EndX=72.5302 EndY=-13.3376 EndZ=0
    g25: LineSegment StartX=83.023 StartY=2.05 StartZ=0 EndX=78.7784 EndY=-13.7912 EndZ=0
    g26: ArcOfCircle CenterX=75.717 CenterY=-12.7 CenterZ=0 NormalX=0 NormalY=0 NormalZ=1 AngleXU=0 Radius=3.25 StartAngle=3.33905 EndAngle=5.94078
    g27: LineSegment StartX=6.02302 StartY=3.55 StartZ=0 EndX=5.21917 EndY=0.55 EndZ=0
  constraints (72):
    c: Coincident(g0,g-10)
    c: Coincident(g0,g-9)
    c: Coincident(g1,g0)
    c: Coincident(g1,g-8)
    c: Coincident(g2,g1)
    c: Coincident(g2,g-8)
    c: Coincident(g3,g2)
    c: Coincident(g3,g-7)
    c: Horizontal(g4)
    c: Horizontal(g5)
    c: DistanceY(g5,g-11) = 1.5
    c: DistanceY(g0,g4) = 1.5
    c: Coincident(g6,g4)
    c: Coincident(g7,g6)
    c: Coincident(g8,g7)
    c: Coincident(g5,g8)
    c: Parallel(g-11,g8)
    c: PointOnObject(g9,g8)
    c: PointOnObject(g9,g-11)
    c: Distance(g5,g9) = 4
    c: Angle(g8,g9) = 1.5708
    c: DistanceX(g9,g9) = 1.5
    c: Coincident(g7,g-12)
    c: Parallel(g6,g-10)
    c: PointOnObject(g5,g-6)
    c: Coincident(g10,g5)
    c: Coincident(g10,g-6)
    c: Coincident(g11,g-11)
    c: Coincident(g11,g-3)
    c: Coincident(g12,g11)
    c: Coincident(g12,g-4)
    c: Coincident(g13,g12)
    c: Coincident(g13,g-4)
    c: Coincident(g14,g13)
    c: Coincident(g14,g-5)
    c: Coincident(g15,g14)
    c: Coincident(g15,g10)
    c: Coincident(g16,g10)
    c: Coincident(g16,g5)
    c: Radius(g-12) = 3.25
    c: PointOnObject(g17,g6)
    c: PointOnObject(g17,g-10)
    c: Angle(g17,g6) = 1.5708
    c: Distance(g17,g0) = 2.5
    c: Distance(g17) = 1.5
    c: Coincident(g18,g-12)
    c: Coincident(g18,g6)
    c: Coincident(g19,g6)
    c: Coincident(g19,g7)
    c: Angle(g19,g18) = 3.14159
    c: Coincident(g20,g4)
    c: Vertical(g20)
    c: Coincident(g21,g20)
    c: PointOnObject(g21,g-6)
    c: Horizontal(g21)
    c: Coincident(g22,g21)
    c: Coincident(g22,g-7)
    c: DistanceX(g21,g21) = 6.5
    c: DistanceY(g-13,g-13) = 1
    c: DistanceY(g20,g20) = 1
    c: Coincident(g23,g22)
    c: Coincident(g23,g3)
    c: Tangent(g23,g-7)
    c: Coincident(g24,g0)
    c: Coincident(g24,g18)
    c: Coincident(g25,g11)
    c: Coincident(g25,g-12)
    c: Coincident(g26,g25)
    c: Coincident(g26,g18)
    c: Tangent(g26,g-12)
    c: Coincident(g27,g10)
    c: Coincident(g27,g5)
FEATURE [PartDesign::Pad] Pad038
  BaseFeature = -> Chamfer001
  Direction = (0,0,-1)
  Length = 1.425
  Length2 = 10
  Profile = -> Sketch053
  ReferenceAxis = -> Sketch053 [N_Axis]
  Refine = true
  Suppressed = false
  Type = 0
FEATURE [Sketcher::SketchObject] Sketch054
  ArcFitTolerance = 1e-06
  AttachmentSupport = -> [Pad038]
  ExternalGeometry = -> [Pad038]
  FullyConstrained = true
  MakeInternals = false
  MapMode = 5
  Placement = pos=(0,0,5.25) rot=(0,0,1;0rad)
  sketch-geometry (1):
    g0: Circle CenterX=75.717 CenterY=12.7 CenterZ=0 NormalX=0 NormalY=0 NormalZ=1 AngleXU=0 Radius=3.25
  constraints (2):
    c: Coincident(g0,g-3)
    c: Equal(g0,g-3)
FEATURE [PartDesign::Pad] Pad039
  BaseFeature = -> Pad038
  Direction = (0,0,1)
  Length = 0.25
  Length2 = 10
  Profile = -> Sketch054
  ReferenceAxis = -> Sketch054 [N_Axis]
  Refine = true
  Suppressed = false
  Type = 0
FEATURE [Sketcher::SketchObject] Sketch055
  ArcFitTolerance = 1e-06
  AttachmentSupport = -> [Pad039]
  ExternalGeometry = -> [Pad039]
  FullyConstrained = true
  MakeInternals = false
  MapMode = 5
  Placement = pos=(0,0,4.25) rot=(0,0,1;0rad)
  sketch-geometry (5):
    g0: LineSegment StartX=16.4156 StartY=4 StartZ=0 EndX=16.4156 EndY=9e-16 EndZ=0
    g1: LineSegment StartX=16.4156 StartY=9e-16 StartZ=0 EndX=30.2156 EndY=9e-16 EndZ=0
    g2: LineSegment StartX=30.2156 StartY=9e-16 StartZ=0 EndX=30.2156 EndY=4 EndZ=0
    g3: LineSegment StartX=30.2156 StartY=4 StartZ=0 EndX=16.4156 EndY=4 EndZ=0
    g4: LineSegment [constr] StartX=34.4156 StartY=6.05 StartZ=0 EndX=34.4156 EndY=-2.05 EndZ=0
  constraints (17):
    c: Coincident(g0,g1)
    c: Coincident(g1,g2)
    c: Coincident(g2,g3)
    c: Coincident(g3,g0)
    c: Vertical(g0)
    c: Vertical(g2)
    c: Horizontal(g1)
    c: Horizontal(g3)
    c: DistanceX(g3,g3) = 13.8
    c: DistanceY(g0,g0) = 4
    c: PointOnObject(g4,g-3)
    c: PointOnObject(g4,g-4)
    c: Vertical(g4)
    c: DistanceY(g4,g4) = 8.1
    c: DistanceX(g-4,g4) = 18
    c: DistanceY(g2,g4) = 2.05
    c: DistanceX(g-4,g0) = 0
FEATURE [PartDesign::Pocket] Pocket018
  BaseFeature = -> Pad039
  Direction = (0,0,-1)
  Length = 0.5
  Length2 = 5
  Profile = -> Sketch055
  ReferenceAxis = -> Sketch055 [N_Axis]
  Refine = true
  Suppressed = false
  Type = 0
FEATURE [Sketcher::SketchObject] Sketch056
  ArcFitTolerance = 1e-06
  AttachmentSupport = -> [Pocket018]
  ExternalGeometry = -> [Pocket018]
  FullyConstrained = true
  MakeInternals = false
  MapMode = 5
  Placement = pos=(0,0,4.25) rot=(0,0,1;0rad)
  sketch-geometry (6):
    g0: LineSegment StartX=35.2156 StartY=-2.05 StartZ=0 EndX=62.2156 EndY=-2.05 EndZ=0
    g1: LineSegment StartX=62.2156 StartY=-2.05 StartZ=0 EndX=62.2156 EndY=2.95 EndZ=0
    g2: LineSegment StartX=62.2156 StartY=2.95 StartZ=0 EndX=56.7156 EndY=6.05 EndZ=0
    g3: LineSegment StartX=56.7156 StartY=6.05 StartZ=0 EndX=46.7156 EndY=6.05 EndZ=0
    g4: LineSegment StartX=35.2156 StartY=-2.05 StartZ=0 EndX=35.2156 EndY=3.45 EndZ=0
    g5: LineSegment StartX=35.2156 StartY=3.45 StartZ=0 EndX=46.7156 EndY=6.05 EndZ=0
  constraints (18):
    c: PointOnObject(g0,g-4)
    c: PointOnObject(g0,g-4)
    c: Coincident(g1,g0)
    c: Vertical(g1)
    c: Coincident(g2,g1)
    c: PointOnObject(g2,g-3)
    c: Coincident(g3,g2)
    c: Coincident(g4,g0)
    c: Vertical(g4)
    c: Coincident(g5,g4)
    c: Coincident(g5,g3)
    c: DistanceX(g0,g0) = 27
    c: DistanceX(g3,g3) = 10
    c: DistanceY(g4,g4) = 5.5
    c: DistanceY(g1,g1) = 5
    c: DistanceX(g2,g1) = 5.5
    c: PointOnObject(g3,g-3)
    c: DistanceX(g-5,g0) = 5
FEATURE [PartDesign::Pad] Pad040
  BaseFeature = -> Pocket018
  Direction = (0,0,1)
  Length = 0.5
  Length2 = 10
  Profile = -> Sketch056
  ReferenceAxis = -> Sketch056 [N_Axis]
  Refine = true
  Suppressed = false
  Type = 0
FEATURE [Sketcher::SketchObject] Sketch057
  ArcFitTolerance = 1e-06
  AttachmentSupport = -> [Pad040]
  ExternalGeometry = -> [Pad040]
  FullyConstrained = true
  MakeInternals = false
  MapMode = 5
  Placement = pos=(0,0,4.75) rot=(0,0,1;0rad)
  sketch-geometry (3):
    g0: Circle CenterX=55.5156 CenterY=1.45 CenterZ=0 NormalX=0 NormalY=0 NormalZ=1 AngleXU=0 Radius=1.5
    g1: Circle CenterX=50.0156 CenterY=1.45 CenterZ=0 NormalX=0 NormalY=0 NormalZ=1 AngleXU=0 Radius=1.5
    g2: Circle CenterX=44.5156 CenterY=1.45 CenterZ=0 NormalX=0 NormalY=0 NormalZ=1 AngleXU=0 Radius=1.5
  constraints (9):
    c: Diameter(g2) = 3
    c: Diameter(g1) = 3
    c: Diameter(g0) = 3
    c: DistanceX(g1,g0) = 5.5
    c: DistanceX(g2,g1) = 5.5
    c: DistanceY(g0,g1) = 0
    c: DistanceY(g2,g1) = 0
    c: DistanceY(g0,g-3) = 1.5
    c: DistanceX(g0,g-3) = 6.7
FEATURE [PartDesign::Pocket] Pocket019
  BaseFeature = -> Pad040
  Direction = (0,0,-1)
  Length = 0.5
  Length2 = 5
  Profile = -> Sketch057
  ReferenceAxis = -> Sketch057 [N_Axis]
  Refine = true
  Suppressed = false
  Type = 0
FEATURE [Sketcher::SketchObject] Sketch058
  ArcFitTolerance = 1e-06
  AttachmentSupport = -> [Pocket019]
  ExternalGeometry = -> [Pocket019]
  FullyConstrained = true
  MakeInternals = false
  MapMode = 5
  Placement = pos=(0,0,5.25) rot=(0,0,1;0rad)
  sketch-geometry (1):
    g0: Circle CenterX=6.23499 CenterY=7.25 CenterZ=0 NormalX=0 NormalY=0 NormalZ=1 AngleXU=0 Radius=1
  constraints (2):
    c: Coincident(g0,g-3)
    c: Diameter(g0) = 2
FEATURE [PartDesign::Pad] Pad041
  BaseFeature = -> Pocket019
  Direction = (0,0,1)
  Length = 0.5
  Length2 = 10
  Profile = -> Sketch058
  ReferenceAxis = -> Sketch058 [N_Axis]
  Refine = true
  Suppressed = false
  Type = 0
FEATURE [Sketcher::SketchObject] Sketch059
  ArcFitTolerance = 1e-06
  AttachmentSupport = -> [Pad041]
  ExternalGeometry = -> [Pad041]
  FullyConstrained = true
  MakeInternals = false
  MapMode = 5
  Placement = pos=(0,0,5.5) rot=(0,0,1;0rad)
  sketch-geometry (1):
    g0: Circle CenterX=75.717 CenterY=12.7 CenterZ=0 NormalX=0 NormalY=0 NormalZ=1 AngleXU=0 Radius=1.5
  constraints (2):
    c: Coincident(g0,g-3)
    c: Diameter(g0) = 3
FEATURE [PartDesign::Pad] Pad042
  BaseFeature = -> Pad041
  Direction = (0,0,1)
  Length = 1.1
  Length2 = 10
  Profile = -> Sketch059
  ReferenceAxis = -> Sketch059 [N_Axis]
  Refine = true
  Suppressed = false
  Type = 0
FEATURE [Sketcher::SketchObject] Sketch060
  ArcFitTolerance = 1e-06
  AttachmentSupport = -> [Pad042]
  ExternalGeometry = -> [Pad042]
  FullyConstrained = true
  MakeInternals = false
  MapMode = 5
  Placement = pos=(0,0,2.75) rot=(1,0,0;3.14159rad)
  sketch-geometry (2):
    g0: Circle CenterX=64.3134 CenterY=-2 CenterZ=0 NormalX=0 NormalY=0 NormalZ=1 AngleXU=0 Radius=1
    g1: Circle CenterX=75.717 CenterY=-2 CenterZ=0 NormalX=0 NormalY=0 NormalZ=1 AngleXU=0 Radius=1
  constraints (7):
    c: Diameter(g0) = 2
    c: Diameter(g1) = 2
    c: DistanceY(g-4,g-3) = 5.1
    c: DistanceY(g0,g-3) = 2.55
    c: DistanceY(g0,g1) = 0
    c: DistanceX(g1,g-5) = 0
    c: DistanceX(g0,g-3) = 16.7
FEATURE [PartDesign::Pad] Pad043
  BaseFeature = -> Pad042
  Direction = (0,0,-1)
  Length = 2.7
  Length2 = 10
  Profile = -> Sketch060
  ReferenceAxis = -> Sketch060 [N_Axis]
  Refine = true
  Suppressed = false
  Type = 0
FEATURE [Sketcher::SketchObject] Sketch061
  ArcFitTolerance = 1e-06
  AttachmentSupport = -> [Pad043]
  ExternalGeometry = -> [Pad043]
  FullyConstrained = true
  MakeInternals = false
  MapMode = 5
  Placement = pos=(0,0,2.75) rot=(1,0,0;3.14159rad)
  sketch-geometry (1):
    g0: Circle CenterX=75.717 CenterY=-12.7 CenterZ=0 NormalX=0 NormalY=0 NormalZ=1 AngleXU=0 Radius=1.5
  constraints (2):
    c: Coincident(g0,g-3)
    c: Diameter(g0) = 3
FEATURE [PartDesign::Pad] Pad044
  BaseFeature = -> Pad043
  Direction = (0,0,-1)
  Length = 5.93
  Length2 = 10
  Profile = -> Sketch061
  ReferenceAxis = -> Sketch061 [N_Axis]
  Refine = true
  Suppressed = false
  Type = 0
FEATURE [Sketcher::SketchObject] Sketch062
  ArcFitTolerance = 1e-06
  AttachmentSupport = -> [Pad044]
  ExternalGeometry = -> [Pad044]
  FullyConstrained = true
  MakeInternals = false
  MapMode = 5
  Placement = pos=(0,0,2.75) rot=(1,0,0;3.14159rad)
  sketch-geometry (4):
    g0: LineSegment StartX=74.0014 StartY=-13.0432 StartZ=0 EndX=75.717 EndY=-12.7 EndZ=0
    g1: LineSegment StartX=75.717 StartY=-12.7 StartZ=0 EndX=77.4631 EndY=-12.7 EndZ=0
    g2: LineSegment StartX=77.4631 StartY=-12.7 StartZ=0 EndX=77.2256 EndY=-13.5862 EndZ=0
    g3: ArcOfCircle CenterX=75.717 CenterY=-12.7 CenterZ=0 NormalX=0 NormalY=0 NormalZ=1 AngleXU=0 Radius=1.7496 StartAngle=3.33905 EndAngle=5.75207
  constraints (10):
    c: Coincident(g0,g-4)
    c: Coincident(g0,g-4)
    c: Coincident(g1,g0)
    c: PointOnObject(g1,g-5)
    c: Horizontal(g1)
    c: Coincident(g2,g1)
    c: Coincident(g2,g-5)
    c: Coincident(g3,g0)
    c: Coincident(g3,g2)
    c: Tangent(g3,g-4)
FEATURE [PartDesign::Pad] Pad045
  BaseFeature = -> Pad044
  Direction = (0,0,-1)
  Length = 1.425
  Length2 = 10
  Profile = -> Sketch062
  ReferenceAxis = -> Sketch062 [N_Axis]
  Refine = true
  Suppressed = false
  Type = 0
FEATURE [Sketcher::SketchObject] Sketch063
  ArcFitTolerance = 1e-06
  AttachmentSupport = -> [Pad045]
  ExternalGeometry = -> [Pad045]
  FullyConstrained = true
  MakeInternals = false
  MapMode = 5
  Placement = pos=(0,0,1.325) rot=(1,0,0;3.14159rad)
  sketch-geometry (1):
    g0: Circle CenterX=6.23499 CenterY=-7.25 CenterZ=0 NormalX=0 NormalY=0 NormalZ=1 AngleXU=0 Radius=1.15
  constraints (2):
    c: Coincident(g0,g-3)
    c: Diameter(g0) = 2.3
FEATURE [PartDesign::Pad] Pad046
  BaseFeature = -> Pad045
  Direction = (0,0,-1)
  Length = 4.5
  Length2 = 10
  Profile = -> Sketch063
  ReferenceAxis = -> Sketch063 [N_Axis]
  Refine = true
  Suppressed = false
  Type = 0
FEATURE [PartDesign::Pocket] Pocket020
  BaseFeature = -> Pad046
  Direction = (0,0,1)
  Length = 10
  Length2 = 5
  Profile = -> Pad046 [Face28,Face47]
  Refine = true
  Suppressed = false
  Type = 0
FEATURE [PartDesign::Pocket] Pocket021
  BaseFeature = -> Pocket020
  Direction = (0,0,1)
  Length = 2.7
  Length2 = 5
  Profile = -> Pocket020 [Face33,Face32]
  Refine = true
  Suppressed = false
  Type = 0
FEATURE [Sketcher::SketchObject] Sketch064
  ArcFitTolerance = 1e-06
  AttachmentSupport = -> [Pocket021]
  ExternalGeometry = -> [Pocket021]
  FullyConstrained = true
  MakeInternals = false
  MapMode = 5
  Placement = pos=(0,0,1.325) rot=(1,0,0;3.14159rad)
  sketch-geometry (2):
    g0: Circle CenterX=75.717 CenterY=-12.7 CenterZ=0 NormalX=0 NormalY=0 NormalZ=1 AngleXU=0 Radius=1.55
    g1: Circle CenterX=6.23499 CenterY=-7.25 CenterZ=0 NormalX=0 NormalY=0 NormalZ=1 AngleXU=0 Radius=1.2
  constraints (6):
    c: Diameter(g-3) = 3
    c: Coincident(g0,g-3)
    c: Diameter(g0) = 3.1
    c: Coincident(g1,g-4)
    c: Diameter(g-4) = 2.3
    c: Diameter(g1) = 2.4
FEATURE [PartDesign::Pocket] Pocket022
  BaseFeature = -> Pocket021
  Direction = (0,0,1)
  Length = 10
  Length2 = 5
  Profile = -> Sketch064
  ReferenceAxis = -> Sketch064 [N_Axis]
  Refine = true
  Suppressed = false
  Type = 0
FEATURE [Sketcher::SketchObject] Sketch065
  ArcFitTolerance = 1e-06
  AttachmentSupport = -> [XY_Plane004]
  FullyConstrained = true
  MakeInternals = false
  MapMode = 5
  sketch-geometry (4):
    g0: ArcOfCircle CenterX=0 CenterY=0 CenterZ=0 NormalX=0 NormalY=0 NormalZ=1 AngleXU=0 Radius=2 StartAngle=5.38752 EndAngle=10.3204
    g1: LineSegment StartX=-1.25 StartY=-1.56125 StartZ=0 EndX=-1.25 EndY=-6.86125 EndZ=0
    g2: LineSegment StartX=-1.25 StartY=-6.86125 StartZ=0 EndX=1.25 EndY=-6.86125 EndZ=0
    g3: LineSegment StartX=1.25 StartY=-1.56125 StartZ=0 EndX=1.25 EndY=-6.86125 EndZ=0
  constraints (12):
    c: Coincident(g1,g0)
    c: Vertical(g1)
    c: Coincident(g2,g1)
    c: Horizontal(g2)
    c: Coincident(g3,g0)
    c: Coincident(g3,g2)
    c: Vertical(g3)
    c: Coincident(g0,g-1)
    c: Diameter(g0) = 4
    c: DistanceX(g2,g2) = 2.5
    c: DistanceY(g0,g0) = 0
    c: DistanceY(g3,g3) = 5.3
FEATURE [PartDesign::Pad] Pad047
  Direction = (0,0,1)
  Length = 2
  Length2 = 10
  Profile = -> Sketch065
  ReferenceAxis = -> Sketch065 [N_Axis]
  Refine = true
  Suppressed = false
  Type = 0
FEATURE [Sketcher::SketchObject] Sketch066
  ArcFitTolerance = 1e-06
  AttachmentSupport = -> [Pad047]
  FullyConstrained = true
  MakeInternals = false
  MapMode = 5
  Placement = pos=(0,0,2) rot=(0,0,1;0rad)
  sketch-geometry (1):
    g0: Circle CenterX=0 CenterY=0 CenterZ=0 NormalX=0 NormalY=0 NormalZ=1 AngleXU=0 Radius=0.95
  constraints (2):
    c: Coincident(g0,g-1)
    c: Diameter(g0) = 1.9
FEATURE [PartDesign::Pad] Pad048
  BaseFeature = -> Pad047
  Direction = (0,0,1)
  Length = 0.3
  Length2 = 10
  Profile = -> Sketch066
  ReferenceAxis = -> Sketch066 [N_Axis]
  Refine = true
  Suppressed = false
  Type = 0
FEATURE [Sketcher::SketchObject] Sketch067
  ArcFitTolerance = 1e-06
  AttachmentSupport = -> [Pad048]
  FullyConstrained = true
  MakeInternals = false
  MapMode = 5
  Placement = pos=(0,0,0) rot=(1,0,0;3.14159rad)
  sketch-geometry (1):
    g0: Circle CenterX=0 CenterY=0 CenterZ=0 NormalX=0 NormalY=0 NormalZ=1 AngleXU=0 Radius=0.95
  constraints (2):
    c: Coincident(g0,g-1)
    c: Diameter(g0) = 1.9
FEATURE [PartDesign::Pad] Pad049
  BaseFeature = -> Pad048
  Direction = (0,0,-1)
  Length = 0.3
  Length2 = 10
  Profile = -> Sketch067
  ReferenceAxis = -> Sketch067 [N_Axis]
  Refine = true
  Suppressed = false
  Type = 0
FEATURE [Sketcher::SketchObject] Sketch068
  ArcFitTolerance = 1e-06
  AttachmentOffset = pos=(0,0,0.5) rot=(0,0,1;0rad)
  AttachmentSupport = -> [Pad049]
  ExternalGeometry = -> [Pad049]
  FullyConstrained = true
  MakeInternals = false
  MapMode = 5
  Placement = pos=(0,0,-0.5) rot=(1,0,0;3.14159rad)
  sketch-geometry (6):
    g0: LineSegment StartX=-1.75 StartY=6.86125 StartZ=0 EndX=1.75 EndY=6.86125 EndZ=0
    g1: LineSegment StartX=1.75 StartY=6.86125 StartZ=0 EndX=2.5 EndY=9.2461 EndZ=0
    g2: LineSegment StartX=2.5 StartY=9.2461 StartZ=0 EndX=1.5 EndY=13.8612 EndZ=0
    g3: LineSegment StartX=-1.75 StartY=6.86125 StartZ=0 EndX=-2.5 EndY=9.2461 EndZ=0
    g4: LineSegment StartX=-2.5 StartY=9.2461 StartZ=0 EndX=-1.5 EndY=13.8612 EndZ=0
    g5: LineSegment StartX=-1.5 StartY=13.8612 StartZ=0 EndX=1.5 EndY=13.8612 EndZ=0
  constraints (19):
    c: Coincident(g1,g0)
    c: Coincident(g2,g1)
    c: Coincident(g3,g0)
    c: Coincident(g4,g3)
    c: Coincident(g5,g4)
    c: Coincident(g5,g2)
    c: Horizontal(g5)
    c: PointOnObject(g-3,g0)
    c: Horizontal(g0)
    c: DistanceX(g3,g1) = 5
    c: DistanceY(g3,g1) = 0
    c: DistanceX(g0,g-3) = 0.5
    c: DistanceX(g-3,g0) = 0.5
    c: DistanceX(g5,g5) = 3
    c: DistanceX(g-3,g-3) = 2.5
    c: DistanceX(g3,g-3) = 1.25
    c: DistanceY(g0,g4) = 7
    c: DistanceX(g-3,g2) = 0.25
    c: Distance(g1) = 2.5
FEATURE [PartDesign::Pad] Pad050
  BaseFeature = -> Pad049
  Direction = (0,0,-1)
  Length = 3
  Length2 = 10
  Profile = -> Sketch068
  ReferenceAxis = -> Sketch068 [N_Axis]
  Refine = true
  Reversed = true
  Suppressed = false
  Type = 0
FEATURE [Sketcher::SketchObject] Sketch069
  ArcFitTolerance = 1e-06
  AttachmentSupport = -> [Pad050]
  ExternalGeometry = -> [Pad050]
  FullyConstrained = true
  MakeInternals = false
  MapMode = 5
  Placement = pos=(0,0,-0.5) rot=(1,0,0;3.14159rad)
  sketch-geometry (2):
    g0: Circle CenterX=0 CenterY=8.36125 CenterZ=0 NormalX=0 NormalY=0 NormalZ=1 AngleXU=0 Radius=1
    g1: Circle CenterX=0 CenterY=12.3612 CenterZ=0 NormalX=0 NormalY=0 NormalZ=1 AngleXU=0 Radius=1
  constraints (6):
    c: PointOnObject(g0,g-2)
    c: PointOnObject(g1,g-2)
    c: Diameter(g1) = 2
    c: Diameter(g0) = 2
    c: DistanceY(g1,g-3) = 1.5
    c: DistanceY(g-5,g0) = 1.5
FEATURE [PartDesign::Pad] Pad051
  BaseFeature = -> Pad050
  Direction = (0,0,-1)
  Length = 0.5
  Length2 = 10
  Profile = -> Sketch069
  ReferenceAxis = -> Sketch069 [N_Axis]
  Refine = true
  Suppressed = false
  Type = 0
FEATURE [Sketcher::SketchObject] Sketch070
  ArcFitTolerance = 1e-06
  AttachmentSupport = -> [Pad051]
  ExternalGeometry = -> [Pad051]
  FullyConstrained = true
  MakeInternals = false
  MapMode = 5
  Placement = pos=(0,0,2.5) rot=(0,0,1;0rad)
  sketch-geometry (2):
    g0: Circle CenterX=0 CenterY=-12.3612 CenterZ=0 NormalX=0 NormalY=0 NormalZ=1 AngleXU=0 Radius=1
    g1: Circle CenterX=0 CenterY=-8.36125 CenterZ=0 NormalX=0 NormalY=0 NormalZ=1 AngleXU=0 Radius=1
  constraints (6):
    c: PointOnObject(g0,g-2)
    c: PointOnObject(g1,g-2)
    c: Diameter(g1) = 2
    c: Diameter(g0) = 2
    c: DistanceY(g-4,g0) = 1.5
    c: DistanceY(g1,g-3) = 1.5
FEATURE [PartDesign::Pad] Pad052
  BaseFeature = -> Pad051
  Direction = (0,0,1)
  Length = 0.5
  Length2 = 10
  Profile = -> Sketch070
  ReferenceAxis = -> Sketch070 [N_Axis]
  Refine = true
  Suppressed = false
  Type = 0
FEATURE [Sketcher::SketchObject] Sketch071
  ArcFitTolerance = 1e-06
  AttachmentOffset = pos=(0,0,-0.5) rot=(0,0,1;0rad)
  AttachmentSupport = -> [Pad052]
  ExternalGeometry = -> [Pad052]
  FullyConstrained = true
  MakeInternals = false
  MapMode = 5
  Placement = pos=(0,0,0) rot=(1,0,0;3.14159rad)
  sketch-geometry (18):
    g0: LineSegment StartX=-1.25 StartY=13.8612 StartZ=0 EndX=1.25 EndY=13.8612 EndZ=0
    g1: LineSegment StartX=1.25 StartY=13.8612 StartZ=0 EndX=1.25 EndY=15.1612 EndZ=0
    g2: LineSegment StartX=-1.25 StartY=13.8612 StartZ=0 EndX=-1.25 EndY=15.1612 EndZ=0
    g3: LineSegment StartX=-0.775 StartY=18.7362 StartZ=0 EndX=-1.83566 EndY=17.6756 EndZ=0
    g4: ArcOfCircle CenterX=-2.18921 CenterY=18.0291 CenterZ=0 NormalX=0 NormalY=0 NormalZ=1 AngleXU=0 Radius=0.5 StartAngle=2.35619 EndAngle=5.49779
    g5: LineSegment StartX=1.25 StartY=15.1612 StartZ=0 EndX=1.39304 EndY=15.3043 EndZ=0
    g6: LineSegment StartX=-1.25 StartY=15.1612 StartZ=0 EndX=0.775 EndY=17.1862 EndZ=0
    g7: ArcOfCircle CenterX=0 CenterY=17.9612 CenterZ=0 NormalX=0 NormalY=0 NormalZ=1 AngleXU=0 Radius=1.09602 StartAngle=5.49779 EndAngle=8.63938
    g8: ArcOfCircle CenterX=0 CenterY=17.9612 CenterZ=0 NormalX=0 NormalY=0 NormalZ=1 AngleXU=0 Radius=3 StartAngle=5.19529 EndAngle=8.75521
    g9: LineSegment [constr] StartX=0 StartY=20.9612 StartZ=0 EndX=4 EndY=20.9612 EndZ=0
    g10: LineSegment [constr] StartX=4 StartY=20.9612 StartZ=0 EndX=4 EndY=13.8612 EndZ=0
    g11: LineSegment [constr] StartX=1.5 StartY=13.8612 StartZ=0 EndX=4 EndY=13.8612 EndZ=0
    g12: LineSegment [constr] StartX=0.775 StartY=17.1862 StartZ=0 EndX=0 EndY=17.9612 EndZ=0
    g13: LineSegment [constr] StartX=0 StartY=17.9612 StartZ=0 EndX=-0.775 EndY=18.7362 EndZ=0
    g14: LineSegment StartX=-2.35226 StartY=18.5732 StartZ=0 EndX=-2.54277 EndY=18.3827 EndZ=0
    g15: LineSegment [constr] StartX=-1.83566 StartY=17.6756 StartZ=0 EndX=-2.18921 EndY=18.0291 EndZ=0
    g16: LineSegment [constr] StartX=-2.18921 StartY=18.0291 StartZ=0 EndX=-2.54277 EndY=18.3827 EndZ=0
    g17: LineSegment StartX=-2.35226 StartY=19.8232 StartZ=0 EndX=-2.35226 EndY=18.5732 EndZ=0
  constraints (52):
    c: PointOnObject(g0,g-3)
    c: PointOnObject(g0,g-3)
    c: Coincident(g1,g0)
    c: Vertical(g1)
    c: Coincident(g2,g0)
    c: Coincident(g4,g3)
    c: Coincident(g5,g1)
    c: Coincident(g6,g2)
    c: Coincident(g7,g3)
    c: Coincident(g7,g6)
    c: Coincident(g8,g5)
    c: DistanceX(g0,g0) = 2.5
    c: DistanceX(g-3,g0) = 0.25
    c: Vertical(g2)
    c: Parallel(g5,g6)
    c: Angle(g1,g5) = 2.35619
    c: DistanceY(g2,g1) = 0
    c: PointOnObject(g8,g-2)
    c: Coincident(g7,g8)
    c: PointOnObject(g9,g8)
    c: Horizontal(g9)
    c: Coincident(g10,g9)
    c: Vertical(g10)
    c: Coincident(g11,g-3)
    c: Coincident(g11,g10)
    c: DistanceY(g10,g10) = 7.1
    c: Horizontal(g11)
    c: DistanceX(g9,g9) = 4
    c: PointOnObject(g9,g-2)
    c: Radius(g8) = 3
    c: Diameter(g4) = 1
    c: DistanceY(g1,g1) = 1.3
    c: Coincident(g12,g6)
    c: Coincident(g12,g7)
    c: Coincident(g13,g7)
    c: Coincident(g13,g3)
    c: Angle(g13,g12) = 3.14159
    c: Angle(g12,g6) = 1.5708
    c: Coincident(g14,g4)
    c: Parallel(g3,g14)
    c: Angle(g3,g13) = 1.5708
    c: Coincident(g15,g3)
    c: Coincident(g15,g4)
    c: Coincident(g16,g4)
    c: Coincident(g16,g4)
    c: Angle(g16,g15) = 3.14159
    c: Angle(g3,g15) = 1.5708
    c: Vertical(g17)
    c: Coincident(g14,g17)
    c: Coincident(g8,g17)
    c: DistanceY(g17,g17) = 1.25
    c: Distance(g3) = 1.5
FEATURE [PartDesign::Pad] Pad053
  BaseFeature = -> Pad052
  Direction = (0,0,-1)
  Length = 2
  Length2 = 10
  Profile = -> Sketch071
  ReferenceAxis = -> Sketch071 [N_Axis]
  Refine = true
  Reversed = true
  Suppressed = false
  Type = 0
FEATURE [PartDesign::Fillet] Fillet001
  Base = -> Pad053 [Edge66,Edge69,Edge57,Edge59,Edge68,Edge58,Edge54,Edge55,Edge67,Edge56,Edge74,Edge64,Edge70,Edge60]
  BaseFeature = -> Pad053
  Radius = 0.5
  Refine = true
  SupportTransform = false
  Suppressed = false
  UseAllEdges = false
FEATURE [PartDesign::Body] Body004  label="Hook"
  AllowCompound = false
  Group = -> [Sketch065,Pad047,Sketch066,Pad048,Sketch067,Pad049,Sketch068,Pad050,Sketch069,Pad051,Sketch070,Pad052,Sketch071,Pad053,Fillet001]
  Origin = -> Origin004
  Placement = pos=(19.06,-40.35,21.85) rot=(0.57735,-0.57735,-0.57735;2.0944rad)
  Tip = -> Fillet001
FEATURE [PartDesign::Pocket] Pocket023
  BaseFeature = -> Pad020
  Direction = (0,-1,0)
  Length = 0.1
  Length2 = 5
  Profile = -> Pad020 [Face25]
  Refine = true
  Suppressed = false
  Type = 0
FEATURE [PartDesign::Pocket] Pocket024
  BaseFeature = -> Pad033
  Direction = (0,0,1)
  Length = 0.05
  Length2 = 5
  Profile = -> Pad033 [Face2]
  Refine = true
  Suppressed = false
  Type = 0
FEATURE [PartDesign::Pocket] Pocket025
  BaseFeature = -> Pocket024
  Direction = (0,1,0)
  Length = 0.1
  Length2 = 5
  Profile = -> Pocket024 [Face58]
  Refine = true
  Suppressed = false
  Type = 0
FEATURE [PartDesign::Pocket] Pocket026
  BaseFeature = -> Pocket022
  Direction = (0,0,1)
  Length = 0.05
  Length2 = 5
  Profile = -> Pocket022 [Face2]
  Refine = true
  Suppressed = false
  Type = 0
FEATURE [PartDesign::Pocket] Pocket027
  BaseFeature = -> Pocket026
  Direction = (0,1,0)
  Length = 0.1
  Length2 = 5
  Profile = -> Pocket026 [Face50]
  Refine = true
  Suppressed = false
  Type = 0
FEATURE [Sketcher::SketchObject] Sketch072
  ArcFitTolerance = 1e-06
  AttachmentSupport = -> [XY_Plane005]
  FullyConstrained = true
  MakeInternals = false
  MapMode = 5
  sketch-geometry (1):
    g0: Circle CenterX=0 CenterY=0 CenterZ=0 NormalX=0 NormalY=0 NormalZ=1 AngleXU=0 Radius=2.55
  constraints (2):
    c: Coincident(g0,g-1)
    c: Diameter(g0) = 5.1
FEATURE [PartDesign::Pad] Pad054
  Direction = (0,0,1)
  Length = 6
  Length2 = 10
  Profile = -> Sketch072
  ReferenceAxis = -> Sketch072 [N_Axis]
  Refine = true
  Suppressed = false
  Type = 0
FEATURE [Sketcher::SketchObject] Sketch073
  ArcFitTolerance = 1e-06
  AttachmentOffset = pos=(0,0,-1.05) rot=(0,0,1;0rad)
  AttachmentSupport = -> [Pad054]
  ExternalGeometry = -> [Pad054]
  FullyConstrained = false
  MakeInternals = false
  MapMode = 5
  Placement = pos=(0,0,1.05) rot=(1,0,0;3.14159rad)
  sketch-geometry (5):
    g0: LineSegment StartX=1.64317 StartY=1.95 StartZ=0 EndX=12.041 EndY=1.95 EndZ=0
    g1: LineSegment StartX=12.041 StartY=1.95 StartZ=0 EndX=12.041 EndY=-1.95 EndZ=0
    g2: LineSegment StartX=12.041 StartY=-1.95 StartZ=0 EndX=1.64317 EndY=-1.95 EndZ=0
    g3: ArcOfCircle CenterX=-0.0255644 CenterY=0 CenterZ=0 NormalX=0 NormalY=0 NormalZ=1 AngleXU=0 Radius=2.56655 StartAngle=5.42022 EndAngle=7.14615
    g4: LineSegment [constr] StartX=2.54098 StartY=0 StartZ=0 EndX=12.041 EndY=0 EndZ=0
  constraints (15):
    c: PointOnObject(g0,g-3)
    c: Horizontal(g0)
    c: Coincident(g1,g0)
    c: Vertical(g1)
    c: Coincident(g2,g1)
    c: PointOnObject(g2,g-3)
    c: Horizontal(g2)
    c: Coincident(g3,g0)
    c: Coincident(g3,g2)
    c: DistanceY(g3,g0) = 1.95
    c: DistanceY(g1,g1) = 3.9
    c: PointOnObject(g4,g3)
    c: Symmetric(g1,g1,g4)
    c: Horizontal(g4)
    c: DistanceX(g4,g4) = 9.5
FEATURE [PartDesign::Pad] Pad055
  BaseFeature = -> Pad054
  Direction = (0,0,-1)
  Length = 3.9
  Length2 = 10
  Profile = -> Sketch073
  ReferenceAxis = -> Sketch073 [N_Axis]
  Refine = true
  Reversed = true
  Suppressed = false
  Type = 0
FEATURE [PartDesign::Fillet] Fillet002
  Base = -> Pad055 [Edge16,Edge18,Edge12,Edge14,Edge17,Edge11,Edge15,Edge13,Edge7]
  BaseFeature = -> Pad055
  Radius = 0.5
  Refine = true
  SupportTransform = false
  Suppressed = false
  UseAllEdges = false
FEATURE [Sketcher::SketchObject] Sketch074
  ArcFitTolerance = 1e-06
  AttachmentSupport = -> [Fillet002]
  FullyConstrained = true
  MakeInternals = false
  MapMode = 5
  Placement = pos=(0,0,0) rot=(1,0,0;3.14159rad)
  sketch-geometry (1):
    g0: Circle CenterX=0 CenterY=0 CenterZ=0 NormalX=0 NormalY=0 NormalZ=1 AngleXU=0 Radius=0.75
  constraints (2):
    c: Coincident(g0,g-1)
    c: Diameter(g0) = 1.5
FEATURE [PartDesign::Pocket] Pocket028
  BaseFeature = -> Fillet002
  Direction = (0,0,1)
  Length = 5
  Length2 = 5
  Profile = -> Sketch074
  ReferenceAxis = -> Sketch074 [N_Axis]
  Refine = true
  Suppressed = false
  Type = 0
FEATURE [Sketcher::SketchObject] Sketch075
  ArcFitTolerance = 1e-06
  AttachmentSupport = -> [Pocket028]
  ExternalGeometry = -> [Pocket028]
  FullyConstrained = true
  MakeInternals = false
  MapMode = 5
  Placement = pos=(0,0,4.95) rot=(0,0,1;0rad)
  sketch-geometry (4):
    g0: LineSegment StartX=11.541 StartY=0.75 StartZ=0 EndX=3.04098 EndY=0.75 EndZ=0
    g1: LineSegment StartX=3.04098 StartY=0.75 StartZ=0 EndX=3.04098 EndY=-0.75 EndZ=0
    g2: LineSegment StartX=3.04098 StartY=-0.75 StartZ=0 EndX=11.541 EndY=-0.75 EndZ=0
    g3: LineSegment StartX=11.541 StartY=-0.75 StartZ=0 EndX=11.541 EndY=0.75 EndZ=0
  constraints (12):
    c: Coincident(g0,g1)
    c: Coincident(g1,g2)
    c: Coincident(g2,g3)
    c: Coincident(g3,g0)
    c: Horizontal(g0)
    c: Horizontal(g2)
    c: Vertical(g1)
    c: Vertical(g3)
    c: PointOnObject(g0,g-3)
    c: DistanceX(g0,g0) = 8.5
    c: DistanceY(g1,g1) = 1.5
    c: DistanceY(g-4,g0) = 0.75
FEATURE [PartDesign::Pad] Pad056
  BaseFeature = -> Pocket028
  Direction = (0,0,1)
  Length = 0.1
  Length2 = 10
  Profile = -> Sketch075
  ReferenceAxis = -> Sketch075 [N_Axis]
  Refine = true
  Suppressed = false
  Type = 0
FEATURE [Sketcher::SketchObject] Sketch076
  ArcFitTolerance = 1e-06
  AttachmentSupport = -> [Pad056]
  ExternalGeometry = -> [Pad056]
  FullyConstrained = true
  MakeInternals = false
  MapMode = 5
  Placement = pos=(0,-0.75,0) rot=(1,0,0;1.5708rad)
  sketch-geometry (3):
    g0: LineSegment StartX=11.541 StartY=5.05 StartZ=0 EndX=11.541 EndY=4.95 EndZ=0
    g1: LineSegment StartX=11.541 StartY=5.05 StartZ=0 EndX=11.441 EndY=5.05 EndZ=0
    g2: LineSegment StartX=11.541 StartY=4.95 StartZ=0 EndX=11.441 EndY=5.05 EndZ=0
  constraints (7):
    c: Coincident(g0,g-4)
    c: Coincident(g0,g-3)
    c: Coincident(g1,g0)
    c: PointOnObject(g1,g-4)
    c: Coincident(g2,g0)
    c: Coincident(g2,g1)
    c: Angle(g0,g2) = 0.785398
FEATURE [PartDesign::Pocket] Pocket029
  BaseFeature = -> Pad056
  Direction = (0,1,-2e-16)
  Length = 5
  Length2 = 5
  Profile = -> Sketch076
  ReferenceAxis = -> Sketch076 [N_Axis]
  Refine = true
  Suppressed = false
  Type = 0
FEATURE [PartDesign::Body] Body005  label="Arm_Link"
  AllowCompound = false
  Group = -> [Sketch072,Pad054,Sketch073,Pad055,Fillet002,Sketch074,Pocket028,Sketch075,Pad056,Sketch076,Pocket029]
  Origin = -> Origin005
  Placement = pos=(4,5.9,2) rot=(0,0,1;3.14159rad)
  Tip = -> Pocket029
FEATURE [Sketcher::SketchObject] Sketch077
  ArcFitTolerance = 1e-06
  AttachmentSupport = -> [XY_Plane006]
  FullyConstrained = true
  MakeInternals = false
  MapMode = 5
  sketch-geometry (4):
    g0: ArcOfCircle CenterX=0 CenterY=0 CenterZ=0 NormalX=0 NormalY=0 NormalZ=1 AngleXU=0 Radius=5 StartAngle=1.5708 EndAngle=4.71239
    g1: ArcOfCircle CenterX=36 CenterY=2.24e-14 CenterZ=0 NormalX=0 NormalY=0 NormalZ=1 AngleXU=0 Radius=5 StartAngle=4.71239 EndAngle=7.85398
    g2: LineSegment StartX=-2.872e-13 StartY=5 StartZ=0 EndX=36 EndY=5 EndZ=0
    g3: LineSegment StartX=-9e-16 StartY=-5 StartZ=0 EndX=36 EndY=-5 EndZ=0
  constraints (9):
    c: Tangent(g0,g2) = 1.5708
    c: Tangent(g0,g3) = -1.5708
    c: Tangent(g1,g2) = 1.5708
    c: Tangent(g1,g3) = -1.5708
    c: Equal(g0,g1)
    c: Horizontal(g3)
    c: Coincident(g0,g-1)
    c: Diameter(g0) = 10
    c: DistanceX(g0,g1) = 36
FEATURE [PartDesign::Pad] Pad057
  Direction = (0,0,1)
  Length = 3.7
  Length2 = 10
  Profile = -> Sketch077
  ReferenceAxis = -> Sketch077 [N_Axis]
  Refine = true
  Suppressed = false
  Type = 0
FEATURE [Sketcher::SketchObject] Sketch078
  ArcFitTolerance = 1e-06
  AttachmentSupport = -> [Pad057]
  ExternalGeometry = -> [Pad057]
  FullyConstrained = true
  MakeInternals = false
  MapMode = 5
  Placement = pos=(0,0,3.7) rot=(0,0,1;0rad)
  sketch-geometry (8):
    g0: ArcOfCircle CenterX=0 CenterY=0 CenterZ=0 NormalX=0 NormalY=0 NormalZ=1 AngleXU=0 Radius=3.45 StartAngle=1.5708 EndAngle=4.71239
    g1: ArcOfCircle CenterX=12.9 CenterY=0 CenterZ=0 NormalX=0 NormalY=0 NormalZ=1 AngleXU=0 Radius=3.45 StartAngle=4.71239 EndAngle=7.85398
    g2: LineSegment StartX=-6e-16 StartY=3.45 StartZ=0 EndX=12.9 EndY=3.45 EndZ=0
    g3: LineSegment StartX=-6e-16 StartY=-3.45 StartZ=0 EndX=12.9 EndY=-3.45 EndZ=0
    g4: ArcOfCircle CenterX=36 CenterY=2.24e-14 CenterZ=0 NormalX=0 NormalY=0 NormalZ=1 AngleXU=0 Radius=3.45 StartAngle=4.71239 EndAngle=7.85398
    g5: ArcOfCircle CenterX=23.1 CenterY=2.28e-14 CenterZ=0 NormalX=0 NormalY=0 NormalZ=1 AngleXU=0 Radius=3.45 StartAngle=1.5708 EndAngle=4.71239
    g6: LineSegment StartX=36 StartY=-3.45 StartZ=0 EndX=23.1 EndY=-3.45 EndZ=0
    g7: LineSegment StartX=36 StartY=3.45 StartZ=0 EndX=23.1 EndY=3.45 EndZ=0
  constraints (18):
    c: Tangent(g0,g2) = 1.5708
    c: Tangent(g0,g3) = -1.5708
    c: Tangent(g1,g2) = 1.5708
    c: Tangent(g1,g3) = -1.5708
    c: Equal(g0,g1)
    c: Horizontal(g3)
    c: Coincident(g0,g-1)
    c: Tangent(g4,g6) = 1.5708
    c: Tangent(g4,g7) = -1.5708
    c: Tangent(g5,g6) = 1.5708
    c: Tangent(g5,g7) = -1.5708
    c: Equal(g4,g5)
    c: Horizontal(g7)
    c: Diameter(g0) = 6.9
    c: Diameter(g5) = 6.9
    c: DistanceX(g0,g1) = 12.9
    c: DistanceX(g5,g4) = 12.9
    c: Coincident(g4,g-3)
FEATURE [PartDesign::Pocket] Pocket030
  BaseFeature = -> Pad057
  Direction = (0,0,-1)
  Length = 1.5
  Length2 = 5
  Profile = -> Sketch078
  ReferenceAxis = -> Sketch078 [N_Axis]
  Refine = true
  Suppressed = false
  Type = 0
FEATURE [Sketcher::SketchObject] Sketch079
  ArcFitTolerance = 1e-06
  AttachmentSupport = -> [Pocket030]
  ExternalGeometry = -> [Pocket030]
  FullyConstrained = true
  MakeInternals = false
  MapMode = 5
  Placement = pos=(0,0,2.2) rot=(0,0,1;0rad)
  sketch-geometry (8):
    g0: ArcOfCircle CenterX=0 CenterY=0 CenterZ=0 NormalX=0 NormalY=0 NormalZ=1 AngleXU=0 Radius=2.45 StartAngle=1.5708 EndAngle=4.71239
    g1: ArcOfCircle CenterX=12.9 CenterY=0 CenterZ=0 NormalX=0 NormalY=0 NormalZ=1 AngleXU=0 Radius=2.45 StartAngle=4.71239 EndAngle=7.85398
    g2: LineSegment StartX=-2.16e-14 StartY=2.45 StartZ=0 EndX=12.9 EndY=2.45 EndZ=0
    g3: LineSegment StartX=-2.22e-14 StartY=-2.45 StartZ=0 EndX=12.9 EndY=-2.45 EndZ=0
    g4: ArcOfCircle CenterX=36 CenterY=2.24e-14 CenterZ=0 NormalX=0 NormalY=0 NormalZ=1 AngleXU=0 Radius=2.45 StartAngle=4.71239 EndAngle=7.85398
    g5: ArcOfCircle CenterX=23.1 CenterY=2.28e-14 CenterZ=0 NormalX=0 NormalY=0 NormalZ=1 AngleXU=0 Radius=2.45 StartAngle=1.5708 EndAngle=4.71239
    g6: LineSegment StartX=36 StartY=-2.45 StartZ=0 EndX=23.1 EndY=-2.45 EndZ=0
    g7: LineSegment StartX=36 StartY=2.45 StartZ=0 EndX=23.1 EndY=2.45 EndZ=0
  constraints (16):
    c: Tangent(g0,g2) = 1.5708
    c: Tangent(g0,g3) = -1.5708
    c: Tangent(g1,g2) = 1.5708
    c: Tangent(g1,g3) = -1.5708
    c: Equal(g0,g1)
    c: Coincident(g0,g-1)
    c: Tangent(g4,g6) = 1.5708
    c: Tangent(g4,g7) = -1.5708
    c: Tangent(g5,g6) = 1.5708
    c: Tangent(g5,g7) = -1.5708
    c: Equal(g4,g5)
    c: Coincident(g4,g-3)
    c: Diameter(g1) = 4.9
    c: Diameter(g5) = 4.9
    c: Coincident(g1,g-4)
    c: Coincident(g5,g-5)
FEATURE [PartDesign::Pocket] Pocket031
  BaseFeature = -> Pocket030
  Direction = (0,0,-1)
  Length = 5
  Length2 = 5
  Profile = -> Sketch079
  ReferenceAxis = -> Sketch079 [N_Axis]
  Refine = true
  Suppressed = false
  Type = 0
FEATURE [PartDesign::Body] Body006  label="Waist_Link"
  AllowCompound = false
  Group = -> [Sketch077,Pad057,Sketch078,Pocket030,Sketch079,Pocket031]
  Origin = -> Origin006
  Placement = pos=(18,-18.15,-2) rot=(0,0,-1;4.71239rad)
  Tip = -> Pocket031
FEATURE [PartDesign::SubShapeBinder] Binder002
  BindCopyOnChange = 0
  BindMode = 2
  ClaimChildren = false
  Context = -> Body007 [Binder002.]
  Fuse = false
  MakeFace = true
  OffsetFill = false
  OffsetIntersection = false
  OffsetJoinType = 0
  OffsetOpenResult = false
  PartialLoad = false
  Refine = true
  Relative = true
  _Version = 2
FEATURE [Sketcher::SketchObject] Sketch080
  ArcFitTolerance = 1e-06
  AttachmentSupport = -> [Binder002]
  ExternalGeometry = -> [Binder002]
  FullyConstrained = true
  MakeInternals = false
  MapMode = 5
  Placement = pos=(0,0,5) rot=(0,0,1;0rad)
  sketch-geometry (2):
    g0: Circle CenterX=18.1 CenterY=30.5 CenterZ=0 NormalX=0 NormalY=0 NormalZ=1 AngleXU=0 Radius=5.55
    g1: Circle CenterX=18.1 CenterY=30.5 CenterZ=0 NormalX=0 NormalY=0 NormalZ=1 AngleXU=0 Radius=7
  constraints (6):
    c: Coincident(g0,g-4)
    c: Diameter(g-3) = 11
    c: Diameter(g-4) = 5
    c: Diameter(g0) = 11.1
    c: Coincident(g1,g0)
    c: Diameter(g1) = 14
FEATURE [PartDesign::Pad] Pad058
  Direction = (0,0,1)
  Length = 3
  Length2 = 10
  Profile = -> Sketch080
  ReferenceAxis = -> Sketch080 [N_Axis]
  Refine = true
  Reversed = true
  Suppressed = false
  Type = 0
FEATURE [Sketcher::SketchObject] Sketch081
  ArcFitTolerance = 1e-06
  AttachmentSupport = -> [Pad058]
  ExternalGeometry = -> [Pad058]
  FullyConstrained = true
  MakeInternals = false
  MapMode = 5
  Placement = pos=(0,0,5) rot=(0,0,1;0rad)
  sketch-geometry (1):
    g0: Circle CenterX=18.1 CenterY=30.5 CenterZ=0 NormalX=0 NormalY=0 NormalZ=1 AngleXU=0 Radius=7
  constraints (2):
    c: Coincident(g0,g-3)
    c: Equal(g0,g-3)
FEATURE [PartDesign::Pad] Pad059
  BaseFeature = -> Pad058
  Direction = (0,0,1)
  Length = 1.5
  Length2 = 10
  Profile = -> Sketch081
  ReferenceAxis = -> Sketch081 [N_Axis]
  Refine = true
  Suppressed = false
  Type = 0
FEATURE [Sketcher::SketchObject] Sketch082
  ArcFitTolerance = 1e-06
  AttachmentSupport = -> [Pad059]
  ExternalGeometry = -> [Pad059]
  FullyConstrained = true
  MakeInternals = false
  MapMode = 5
  Placement = pos=(0,0,6.5) rot=(0,0,1;0rad)
  sketch-geometry (1):
    g0: Circle CenterX=18.1 CenterY=30.5 CenterZ=0 NormalX=0 NormalY=0 NormalZ=1 AngleXU=0 Radius=2.25
  constraints (2):
    c: Coincident(g0,g-3)
    c: Diameter(g0) = 4.5
FEATURE [PartDesign::Pad] Pad060
  BaseFeature = -> Pad059
  Direction = (0,0,1)
  Length = 1.5
  Length2 = 10
  Profile = -> Sketch082
  ReferenceAxis = -> Sketch082 [N_Axis]
  Refine = true
  Suppressed = false
  Type = 0
FEATURE [Sketcher::SketchObject] Sketch083
  ArcFitTolerance = 1e-06
  AttachmentSupport = -> [Pad060]
  ExternalGeometry = -> [Pad060]
  FullyConstrained = true
  MakeInternals = false
  MapMode = 5
  Placement = pos=(0,0,8) rot=(0,0,1;0rad)
  sketch-geometry (1):
    g0: Circle CenterX=18.1 CenterY=30.5 CenterZ=0 NormalX=0 NormalY=0 NormalZ=1 AngleXU=0 Radius=0.75
  constraints (2):
    c: Coincident(g0,g-3)
    c: Diameter(g0) = 1.5
FEATURE [PartDesign::Pocket] Pocket032
  BaseFeature = -> Pad060
  Direction = (0,0,-1)
  Length = 5
  Length2 = 5
  Profile = -> Sketch083
  ReferenceAxis = -> Sketch083 [N_Axis]
  Refine = true
  Suppressed = false
  Type = 0
FEATURE [Sketcher::SketchObject] Sketch084
  ArcFitTolerance = 1e-06
  AttachmentSupport = -> [Pocket032]
  ExternalGeometry = -> [Pocket032]
  FullyConstrained = true
  MakeInternals = false
  MapMode = 5
  Placement = pos=(0,0,5) rot=(1,0,0;3.14159rad)
  sketch-geometry (1):
    g0: Circle CenterX=18.1 CenterY=-30.5 CenterZ=0 NormalX=0 NormalY=0 NormalZ=1 AngleXU=0 Radius=2.35
  constraints (2):
    c: Coincident(g0,g-4)
    c: Diameter(g0) = 4.7
FEATURE [PartDesign::Pad] Pad061
  BaseFeature = -> Pocket032
  Direction = (0,0,-1)
  Length = 3
  Length2 = 10
  Profile = -> Sketch084
  ReferenceAxis = -> Sketch084 [N_Axis]
  Refine = true
  Suppressed = false
  Type = 0
FEATURE [Sketcher::SketchObject] Sketch085
  ArcFitTolerance = 1e-06
  AttachmentSupport = -> [Pad061]
  ExternalGeometry = -> [Pad061]
  FullyConstrained = true
  MakeInternals = false
  MapMode = 5
  Placement = pos=(0,0,2) rot=(1,0,0;3.14159rad)
  sketch-geometry (1):
    g0: Circle CenterX=18.1 CenterY=-30.5 CenterZ=0 NormalX=0 NormalY=0 NormalZ=1 AngleXU=0 Radius=0.75
  constraints (2):
    c: Coincident(g0,g-3)
    c: Diameter(g0) = 1.5
FEATURE [PartDesign::Pocket] Pocket033
  BaseFeature = -> Pad061
  Direction = (0,0,1)
  Length = 5
  Length2 = 5
  Profile = -> Sketch085
  ReferenceAxis = -> Sketch085 [N_Axis]
  Refine = true
  Suppressed = false
  Type = 0
FEATURE [Sketcher::SketchObject] Sketch086
  ArcFitTolerance = 1e-06
  AttachmentSupport = -> [Pocket033]
  ExternalGeometry = -> [Pocket033]
  FullyConstrained = true
  MakeInternals = false
  MapMode = 5
  Placement = pos=(0,0,2) rot=(1,0,0;3.14159rad)
  sketch-geometry (9):
    g0: LineSegment StartX=33 StartY=-17.25 StartZ=0 EndX=10 EndY=-17.25 EndZ=0
    g1: LineSegment StartX=10 StartY=-17.25 StartZ=0 EndX=10 EndY=-15.75 EndZ=0
    g2: LineSegment StartX=10 StartY=-15.75 StartZ=0 EndX=0 EndY=-15.75 EndZ=0
    g3: LineSegment StartX=0 StartY=-15.75 StartZ=0 EndX=0 EndY=-32.75 EndZ=0
    g4: LineSegment StartX=0 StartY=-32.75 StartZ=0 EndX=3 EndY=-32.75 EndZ=0
    g5: LineSegment StartX=3 StartY=-32.75 StartZ=0 EndX=3 EndY=-45.75 EndZ=0
    g6: LineSegment StartX=3 StartY=-45.75 StartZ=0 EndX=33 EndY=-45.75 EndZ=0
    g7: LineSegment StartX=33 StartY=-45.75 StartZ=0 EndX=33 EndY=-17.25 EndZ=0
    g8: LineSegment [constr] StartX=18.1 StartY=-30.5 StartZ=0 EndX=18.1 EndY=-23.5 EndZ=0
  constraints (27):
    c: Horizontal(g0)
    c: Coincident(g1,g0)
    c: Vertical(g1)
    c: PointOnObject(g2,g-2)
    c: Horizontal(g2)
    c: Coincident(g3,g2)
    c: PointOnObject(g3,g-2)
    c: Coincident(g4,g3)
    c: Horizontal(g4)
    c: Coincident(g5,g4)
    c: Vertical(g5)
    c: Coincident(g6,g5)
    c: Horizontal(g6)
    c: Coincident(g7,g6)
    c: Coincident(g7,g0)
    c: Vertical(g7)
    c: DistanceX(g2,g2) = 10
    c: DistanceY(g3,g3) = 17
    c: Coincident(g2,g1)
    c: DistanceY(g1,g1) = 1.5
    c: DistanceY(g5,g5) = 13
    c: DistanceX(g4,g4) = 3
    c: DistanceX(g6,g6) = 30
    c: Coincident(g8,g-3)
    c: PointOnObject(g8,g-3)
    c: Vertical(g8)
    c: DistanceY(g8,g0) = 6.25
FEATURE [PartDesign::Pad] Pad062
  BaseFeature = -> Pocket033
  Direction = (0,0,-1)
  Length = 1.5
  Length2 = 10
  Profile = -> Sketch086
  ReferenceAxis = -> Sketch086 [N_Axis]
  Refine = true
  Reversed = true
  Suppressed = false
  Type = 0
FEATURE [Sketcher::SketchObject] Sketch087
  ArcFitTolerance = 1e-06
  AttachmentSupport = -> [Pad062]
  ExternalGeometry = -> [Pad062]
  FullyConstrained = true
  MakeInternals = false
  MapMode = 5
  Placement = pos=(0,0,3.5) rot=(0,0,1;0rad)
  sketch-geometry (4):
    g0: LineSegment StartX=14.6 StartY=45.75 StartZ=0 EndX=14.6 EndY=42.95 EndZ=0
    g1: LineSegment StartX=14.6 StartY=42.95 StartZ=0 EndX=21.6 EndY=42.95 EndZ=0
    g2: LineSegment StartX=21.6 StartY=42.95 StartZ=0 EndX=21.6 EndY=45.75 EndZ=0
    g3: LineSegment StartX=21.6 StartY=45.75 StartZ=0 EndX=14.6 EndY=45.75 EndZ=0
  constraints (12):
    c: Coincident(g0,g1)
    c: Coincident(g1,g2)
    c: Coincident(g2,g3)
    c: Coincident(g3,g0)
    c: Vertical(g0)
    c: Vertical(g2)
    c: Horizontal(g1)
    c: Horizontal(g3)
    c: PointOnObject(g0,g-3)
    c: DistanceX(g3,g3) = 7
    c: DistanceY(g2,g2) = 2.8
    c: DistanceX(g0,g-4) = 3.5
FEATURE [PartDesign::Pad] Pad063
  BaseFeature = -> Pad062
  Direction = (0,0,1)
  Length = 6
  Length2 = 10
  Profile = -> Sketch087
  ReferenceAxis = -> Sketch087 [N_Axis]
  Refine = true
  Suppressed = false
  Type = 0
FEATURE [Sketcher::SketchObject] Sketch088
  ArcFitTolerance = 1e-06
  AttachmentSupport = -> [Pad063]
  ExternalGeometry = -> [Pad063]
  FullyConstrained = true
  MakeInternals = false
  MapMode = 5
  Placement = pos=(0,0,3.5) rot=(0,0,1;0rad)
  sketch-geometry (2):
    g0: Circle CenterX=18.1 CenterY=38.9 CenterZ=0 NormalX=0 NormalY=0 NormalZ=1 AngleXU=0 Radius=1.55
    g1: Circle CenterX=4.95 CenterY=29.4 CenterZ=0 NormalX=0 NormalY=0 NormalZ=1 AngleXU=0 Radius=1.55
  constraints (6):
    c: Diameter(g0) = 3.1
    c: Diameter(g1) = 3.1
    c: DistanceX(g0,g-4) = 0
    c: DistanceY(g0,g-5) = 4.05
    c: DistanceX(g-6,g1) = 4.95
    c: DistanceY(g-7,g1) = 13.65
FEATURE [PartDesign::Pad] Pad064
  BaseFeature = -> Pad063
  Direction = (0,0,1)
  Length = 6.9
  Length2 = 10
  Profile = -> Sketch088
  ReferenceAxis = -> Sketch088 [N_Axis]
  Refine = true
  Suppressed = false
  Type = 0
FEATURE [Sketcher::SketchObject] Sketch089
  ArcFitTolerance = 1e-06
  AttachmentSupport = -> [Pad064]
  ExternalGeometry = -> [Pad064]
  FullyConstrained = true
  MakeInternals = false
  MapMode = 5
  Placement = pos=(0,0,3.5) rot=(0,0,1;0rad)
  sketch-geometry (8):
    g0: LineSegment StartX=31.5 StartY=39.75 StartZ=0 EndX=31.5 EndY=35.95 EndZ=0
    g1: LineSegment StartX=31.5 StartY=35.95 StartZ=0 EndX=34.5 EndY=35.95 EndZ=0
    g2: LineSegment StartX=34.5 StartY=35.95 StartZ=0 EndX=34.5 EndY=39.75 EndZ=0
    g3: LineSegment StartX=34.5 StartY=39.75 StartZ=0 EndX=31.5 EndY=39.75 EndZ=0
    g4: LineSegment StartX=31.5 StartY=25.55 StartZ=0 EndX=31.5 EndY=21.75 EndZ=0
    g5: LineSegment StartX=31.5 StartY=21.75 StartZ=0 EndX=34.5 EndY=21.75 EndZ=0
    g6: LineSegment StartX=34.5 StartY=21.75 StartZ=0 EndX=34.5 EndY=25.55 EndZ=0
    g7: LineSegment StartX=34.5 StartY=25.55 StartZ=0 EndX=31.5 EndY=25.55 EndZ=0
  constraints (25):
    c: Coincident(g0,g1)
    c: Coincident(g1,g2)
    c: Coincident(g2,g3)
    c: Coincident(g3,g0)
    c: Vertical(g0)
    c: Vertical(g2)
    c: Horizontal(g1)
    c: Horizontal(g3)
    c: Coincident(g4,g5)
    c: Coincident(g5,g6)
    c: Coincident(g6,g7)
    c: Coincident(g7,g4)
    c: Vertical(g4)
    c: Vertical(g6)
    c: Horizontal(g5)
    c: Horizontal(g7)
    c: DistanceY(g6,g6) = 3.8
    c: DistanceY(g2,g2) = 3.8
    c: DistanceX(g3,g3) = 3
    c: DistanceX(g7,g7) = 3
    c: DistanceX(g-5,g6) = 1.5
    c: DistanceX(g-4,g2) = 1.5
    c: DistanceY(g2,g-4) = 6
    c: DistanceY(g4,g0) = 10.4
    c: DistanceY(g-5,g5) = 4.5
FEATURE [PartDesign::Pad] Pad065
  BaseFeature = -> Pad064
  Direction = (0,0,1)
  Length = 1.5
  Length2 = 10
  Profile = -> Sketch089
  ReferenceAxis = -> Sketch089 [N_Axis]
  Refine = true
  Suppressed = false
  Type = 0
FEATURE [PartDesign::Pocket] Pocket034
  BaseFeature = -> Pad065
  Direction = (0,0,-1)
  Length = 8
  Length2 = 5
  Profile = -> Pad065 [Edge86]
  Refine = true
  Suppressed = false
  Type = 0
FEATURE [Sketcher::SketchObject] Sketch090
  ArcFitTolerance = 1e-06
  AttachmentSupport = -> [Pocket034]
  ExternalGeometry = -> [Pocket034]
  FullyConstrained = true
  MakeInternals = false
  MapMode = 5
  Placement = pos=(0,0,2) rot=(1,0,0;3.14159rad)
  sketch-geometry (1):
    g0: Circle CenterX=18.1 CenterY=-30.5 CenterZ=0 NormalX=0 NormalY=0 NormalZ=1 AngleXU=0 Radius=5.55
  constraints (2):
    c: Coincident(g0,g-3)
    c: Diameter(g0) = 11.1
FEATURE [PartDesign::Pocket] Pocket035
  BaseFeature = -> Pocket034
  Direction = (0,0,1)
  Length = 1.5
  Length2 = 5
  Profile = -> Sketch090
  ReferenceAxis = -> Sketch090 [N_Axis]
  Refine = true
  Suppressed = false
  Type = 0
FEATURE [PartDesign::Pad] Pad066
  BaseFeature = -> Pocket035
  Direction = (0,0,-1)
  Length = 1
  Length2 = 10
  Profile = -> Pocket035 [Face3]
  Refine = true
  Suppressed = false
  Type = 0
FEATURE [Sketcher::SketchObject] Sketch091
  ArcFitTolerance = 1e-06
  AttachmentSupport = -> [Pad066]
  ExternalGeometry = -> [Pad066]
  FullyConstrained = true
  MakeInternals = false
  MapMode = 5
  Placement = pos=(0,0,3.5) rot=(0,0,1;0rad)
  sketch-geometry (2):
    g0: Circle CenterX=12.5 CenterY=23.2 CenterZ=0 NormalX=0 NormalY=0 NormalZ=1 AngleXU=0 Radius=3.45
    g1: Circle CenterX=8.65 CenterY=38 CenterZ=0 NormalX=0 NormalY=0 NormalZ=1 AngleXU=0 Radius=3.45
  constraints (6):
    c: Diameter(g1) = 6.9
    c: Diameter(g0) = 6.9
    c: DistanceY(g1,g-4) = 7.75
    c: DistanceX(g-4,g1) = 5.65
    c: DistanceY(g-7,g0) = 7.45
    c: DistanceX(g-7,g0) = 12.5
FEATURE [PartDesign::Pad] Pad067
  BaseFeature = -> Pad066
  Direction = (0,0,1)
  Length = 3
  Length2 = 10
  Profile = -> Sketch091
  ReferenceAxis = -> Sketch091 [N_Axis]
  Refine = true
  Suppressed = false
  Type = 0
FEATURE [Sketcher::SketchObject] Sketch092
  ArcFitTolerance = 1e-06
  AttachmentSupport = -> [Pad067]
  ExternalGeometry = -> [Pad067]
  FullyConstrained = true
  MakeInternals = false
  MapMode = 5
  Placement = pos=(0,0,6.5) rot=(0,0,1;0rad)
  sketch-geometry (2):
    g0: Circle CenterX=8.65 CenterY=38 CenterZ=0 NormalX=0 NormalY=0 NormalZ=1 AngleXU=0 Radius=0.75
    g1: Circle CenterX=12.5 CenterY=23.2 CenterZ=0 NormalX=0 NormalY=0 NormalZ=1 AngleXU=0 Radius=0.75
  constraints (4):
    c: Coincident(g0,g-3)
    c: Coincident(g1,g-4)
    c: Radius(g0) = 0.75
    c: Radius(g1) = 0.75
FEATURE [PartDesign::Pocket] Pocket036
  BaseFeature = -> Pad067
  Direction = (0,0,-1)
  Length = 5
  Length2 = 5
  Profile = -> Sketch092
  ReferenceAxis = -> Sketch092 [N_Axis]
  Refine = true
  Suppressed = false
  Type = 0
FEATURE [Sketcher::SketchObject] Sketch093
  ArcFitTolerance = 1e-06
  AttachmentSupport = -> [Pocket036]
  ExternalGeometry = -> [Pocket036]
  FullyConstrained = true
  MakeInternals = false
  MapMode = 5
  Placement = pos=(0,0,6.5) rot=(0,0,1;0rad)
  sketch-geometry (2):
    g0: Circle CenterX=8.65 CenterY=38 CenterZ=0 NormalX=0 NormalY=0 NormalZ=1 AngleXU=0 Radius=2.4
    g1: Circle CenterX=12.5 CenterY=23.2 CenterZ=0 NormalX=0 NormalY=0 NormalZ=1 AngleXU=0 Radius=2.4
  constraints (4):
    c: Coincident(g0,g-3)
    c: Coincident(g1,g-4)
    c: Diameter(g0) = 4.8
    c: Diameter(g1) = 4.8
FEATURE [PartDesign::Pocket] Pocket037
  BaseFeature = -> Pocket036
  Direction = (0,0,-1)
  Length = 1
  Length2 = 5
  Profile = -> Sketch093
  ReferenceAxis = -> Sketch093 [N_Axis]
  Refine = true
  Suppressed = false
  Type = 0
FEATURE [Sketcher::SketchObject] Sketch094
  ArcFitTolerance = 1e-06
  AttachmentSupport = -> [Pocket037]
  ExternalGeometry = -> [Pocket037]
  FullyConstrained = false
  MakeInternals = false
  MapMode = 5
  Placement = pos=(0,0,2) rot=(1,0,0;3.14159rad)
  sketch-geometry (2):
    g0: Circle CenterX=12.5 CenterY=-23.2 CenterZ=0 NormalX=0 NormalY=0 NormalZ=1 AngleXU=0 Radius=2.15
    g1: Circle CenterX=8.65 CenterY=-38 CenterZ=0 NormalX=0 NormalY=0 NormalZ=1 AngleXU=0 Radius=2.15
  constraints (3):
    c: Diameter(g1) = 4.3
    c: Diameter(g0) = 4.3
    c: Coincident(g0,g-4)
FEATURE [PartDesign::Pocket] Pocket038
  BaseFeature = -> Pocket037
  Direction = (0,0,1)
  Length = 2
  Length2 = 5
  Profile = -> Sketch094
  ReferenceAxis = -> Sketch094 [N_Axis]
  Refine = true
  Suppressed = false
  Type = 0
FEATURE [Sketcher::SketchObject] Sketch095
  ArcFitTolerance = 1e-06
  AttachmentSupport = -> [Pocket013]
  ExternalGeometry = -> [Pocket013]
  FullyConstrained = true
  MakeInternals = false
  MapMode = 5
  Placement = pos=(0,0,2) rot=(0,0,1;0rad)
  sketch-geometry (4):
    g0: LineSegment StartX=13.15 StartY=13.8 StartZ=0 EndX=13.15 EndY=11.3 EndZ=0
    g1: LineSegment StartX=13.15 StartY=11.3 StartZ=0 EndX=23.05 EndY=11.3 EndZ=0
    g2: LineSegment StartX=23.05 StartY=11.3 StartZ=0 EndX=23.05 EndY=13.8 EndZ=0
    g3: LineSegment StartX=23.05 StartY=13.8 StartZ=0 EndX=13.15 EndY=13.8 EndZ=0
  constraints (13):
    c: Coincident(g0,g1)
    c: Coincident(g1,g2)
    c: Coincident(g2,g3)
    c: Coincident(g3,g0)
    c: Vertical(g0)
    c: Vertical(g2)
    c: Horizontal(g1)
    c: Horizontal(g3)
    c: DistanceY(g1,g-6) = 0
    c: DistanceY(g-6,g2) = 0
    c: DistanceX(g3,g3) = 9.9
    c: DistanceX(g-5,g0) = 0.55
    c: DistanceX(g2,g-6) = 0.55
FEATURE [PartDesign::Pocket] Pocket039
  BaseFeature = -> Pocket013
  Direction = (0,0,-1)
  Length = 2
  Length2 = 5
  Profile = -> Sketch095
  ReferenceAxis = -> Sketch095 [N_Axis]
  Refine = true
  Suppressed = false
  Type = 0
FEATURE [PartDesign::Pocket] Pocket040
  BaseFeature = -> Pocket039
  Direction = (0,0,-1)
  Length = 2
  Length2 = 5
  Profile = -> Pocket039 [Face1059]
  Refine = true
  Suppressed = false
  Type = 0
FEATURE [PartDesign::Body] Body  label="Rear_Torso"
  AllowCompound = false
  Group = -> [Sketch,Pad,Sketch001,Pocket,Sketch002,Pocket001,Sketch003,Pocket002,LinearPattern,Sketch004,Pocket003,Sketch005,Pocket004,LinearPattern001,Sketch006,Pad001,Sketch007,Pocket005,Sketch008,Pocket006,Sketch009,Pad002,Sketch010,Pocket007,Sketch011,Pad003,Fillet,Sketch012,Pad004,Sketch013,Pad005,Sketch014,Pad006,Sketch015,Pad007,Sketch016,Pad008,Sketch017,Pocket008,Sketch018,Pad009,Sketch019,Pad010,+20 more]
  Origin = -> Origin
  Tip = -> Pocket040
FEATURE [Sketcher::SketchObject] Sketch096
  ArcFitTolerance = 1e-06
  AttachmentSupport = -> [Pocket038]
  ExternalGeometry = -> [Pocket038]
  FullyConstrained = true
  MakeInternals = false
  MapMode = 5
  Placement = pos=(0,0,3.5) rot=(0,0,1;0rad)
  sketch-geometry (6):
    g0: LineSegment StartX=14.6 StartY=45.75 StartZ=0 EndX=3 EndY=45.75 EndZ=0
    g1: LineSegment StartX=3 StartY=45.75 StartZ=0 EndX=3 EndY=44.75 EndZ=0
    g2: LineSegment StartX=3 StartY=44.75 StartZ=0 EndX=14.6 EndY=45.75 EndZ=0
    g3: LineSegment StartX=21.6 StartY=45.75 StartZ=0 EndX=33 EndY=45.75 EndZ=0
    g4: LineSegment StartX=33 StartY=45.75 StartZ=0 EndX=33 EndY=44.75 EndZ=0
    g5: LineSegment StartX=33 StartY=44.75 StartZ=0 EndX=21.6 EndY=45.75 EndZ=0
  constraints (14):
    c: Coincident(g0,g-3)
    c: Coincident(g0,g-4)
    c: Coincident(g1,g0)
    c: PointOnObject(g1,g-4)
    c: Coincident(g2,g1)
    c: Coincident(g2,g0)
    c: Coincident(g3,g-5)
    c: Coincident(g3,g-6)
    c: Coincident(g4,g3)
    c: PointOnObject(g4,g-6)
    c: Coincident(g5,g4)
    c: Coincident(g5,g3)
    c: DistanceY(g4,g4) = 1
    c: DistanceY(g1,g1) = 1
FEATURE [PartDesign::Pocket] Pocket041
  BaseFeature = -> Pocket038
  Direction = (0,0,-1)
  Length = 5
  Length2 = 5
  Profile = -> Sketch096
  ReferenceAxis = -> Sketch096 [N_Axis]
  Refine = true
  Suppressed = false
  Type = 0
FEATURE [PartDesign::SubShapeBinder] Binder003
  BindCopyOnChange = 0
  BindMode = 2
  ClaimChildren = false
  Context = -> Body008 [Binder003.]
  Fuse = false
  MakeFace = true
  OffsetFill = false
  OffsetIntersection = false
  OffsetJoinType = 0
  OffsetOpenResult = false
  PartialLoad = false
  Refine = true
  Relative = true
  _Version = 2
FEATURE [Sketcher::SketchObject] Sketch097
  ArcFitTolerance = 1e-06
  AttachmentSupport = -> [Binder003]
  ExternalGeometry = -> [Binder003]
  FullyConstrained = true
  MakeInternals = false
  MapMode = 5
  Placement = pos=(0,0,3.5) rot=(0,0,1;0rad)
  sketch-geometry (4):
    g0: LineSegment StartX=33 StartY=17.25 StartZ=0 EndX=10 EndY=17.25 EndZ=0
    g1: LineSegment StartX=33 StartY=18.75 StartZ=0 EndX=10 EndY=18.75 EndZ=0
    g2: LineSegment StartX=10 StartY=17.25 StartZ=0 EndX=10 EndY=18.75 EndZ=0
    g3: LineSegment StartX=33 StartY=17.25 StartZ=0 EndX=33 EndY=18.75 EndZ=0
  constraints (10):
    c: Horizontal(g1)
    c: DistanceY(g-16,g1) = 1.5
    c: Coincident(g2,g0)
    c: Coincident(g2,g1)
    c: Vertical(g2)
    c: Coincident(g3,g0)
    c: PointOnObject(g3,g-15)
    c: Coincident(g1,g3)
    c: Coincident(g0,g-16)
    c: Coincident(g0,g-17)
FEATURE [PartDesign::Pad] Pad068
  Direction = (0,0,1)
  Length = 4.5
  Length2 = 10
  Profile = -> Sketch097
  ReferenceAxis = -> Sketch097 [N_Axis]
  Refine = true
  Suppressed = false
  Type = 0
FEATURE [PartDesign::Pad] Pad069
  BaseFeature = -> Pad068
  Direction = (0,0,1)
  Length = 4.5
  Length2 = 10
  Profile = -> Sketch097
  ReferenceAxis = -> Sketch097 [N_Axis]
  Refine = true
  Suppressed = false
  Type = 0
FEATURE [Sketcher::SketchObject] Sketch098
  ArcFitTolerance = 1e-06
  AttachmentSupport = -> [Pad069]
  ExternalGeometry = -> [Pad069]
  FullyConstrained = true
  MakeInternals = false
  MapMode = 5
  Placement = pos=(33,0,0) rot=(0.57735,0.57735,0.57735;2.0944rad)
  sketch-geometry (4):
    g0: LineSegment StartX=17.25 StartY=8 StartZ=0 EndX=21.15 EndY=11.9 EndZ=0
    g1: LineSegment StartX=18.75 StartY=8 StartZ=0 EndX=22.65 EndY=11.9 EndZ=0
    g2: LineSegment StartX=22.65 StartY=11.9 StartZ=0 EndX=21.15 EndY=11.9 EndZ=0
    g3: LineSegment StartX=18.75 StartY=8 StartZ=0 EndX=17.25 EndY=8 EndZ=0
  constraints (10):
    c: Coincident(g0,g-3)
    c: Coincident(g1,g-3)
    c: Coincident(g2,g1)
    c: Coincident(g2,g0)
    c: Horizontal(g2)
    c: Angle(g-4,g1) = 2.35619
    c: Parallel(g0,g1)
    c: DistanceY(g-4,g1) = 8.4
    c: Coincident(g3,g1)
    c: Coincident(g3,g0)
FEATURE [PartDesign::Pad] Pad070
  BaseFeature = -> Pad069
  Direction = (1,0,0)
  Length = 23
  Length2 = 10
  Profile = -> Sketch098
  ReferenceAxis = -> Sketch098 [N_Axis]
  Refine = true
  Reversed = true
  Suppressed = false
  Type = 0
FEATURE [Sketcher::SketchObject] Sketch099
  ArcFitTolerance = 1e-06
  AttachmentSupport = -> [Pad070]
  ExternalGeometry = -> [Pad070,Binder003]
  FullyConstrained = true
  MakeInternals = false
  MapMode = 5
  Placement = pos=(0,0,11.9) rot=(0,0,1;0rad)
  sketch-geometry (10):
    g0: LineSegment StartX=33 StartY=21.15 StartZ=0 EndX=33 EndY=42.95 EndZ=0
    g1: LineSegment StartX=33 StartY=42.95 StartZ=0 EndX=22.28 EndY=42.95 EndZ=0
    g2: LineSegment StartX=22.28 StartY=42.95 StartZ=0 EndX=22.28 EndY=35.05 EndZ=0
    g3: LineSegment StartX=22.28 StartY=35.05 StartZ=0 EndX=13.93 EndY=35.05 EndZ=0
    g4: LineSegment StartX=13.93 StartY=35.05 StartZ=0 EndX=13.93 EndY=42.95 EndZ=0
    g5: LineSegment StartX=13.93 StartY=42.95 StartZ=0 EndX=3 EndY=42.95 EndZ=0
    g6: LineSegment StartX=3 StartY=42.95 StartZ=0 EndX=3 EndY=32.75 EndZ=0
    g7: LineSegment StartX=3 StartY=32.75 StartZ=0 EndX=10 EndY=32.75 EndZ=0
    g8: LineSegment StartX=10 StartY=32.75 StartZ=0 EndX=10 EndY=21.15 EndZ=0
    g9: LineSegment StartX=10 StartY=21.15 StartZ=0 EndX=33 EndY=21.15 EndZ=0
  constraints (27):
    c: Coincident(g0,g-3)
    c: Vertical(g0)
    c: Coincident(g1,g0)
    c: Horizontal(g1)
    c: Coincident(g2,g1)
    c: Vertical(g2)
    c: Coincident(g3,g2)
    c: Horizontal(g3)
    c: Coincident(g4,g3)
    c: Coincident(g5,g4)
    c: Horizontal(g5)
    c: PointOnObject(g5,g-4)
    c: Coincident(g6,g5)
    c: Coincident(g6,g-4)
    c: Coincident(g7,g6)
    c: Horizontal(g7)
    c: Coincident(g8,g7)
    c: Coincident(g8,g-3)
    c: Vertical(g8)
    c: Coincident(g9,g8)
    c: Coincident(g9,g0)
    c: Vertical(g4)
    c: DistanceY(g4,g-8) = 0
    c: DistanceY(g1,g-8) = 0
    c: DistanceY(g4,g4) = 7.9
    c: DistanceX(g5,g5) = 10.93
    c: DistanceX(g1,g1) = 10.72
FEATURE [PartDesign::Pad] Pad071
  BaseFeature = -> Pad070
  Direction = (0,0,1)
  Length = 1.5
  Length2 = 10
  Profile = -> Sketch099
  ReferenceAxis = -> Sketch099 [N_Axis]
  Refine = true
  Reversed = true
  Suppressed = false
  Type = 0
FEATURE [Sketcher::SketchObject] Sketch100
  ArcFitTolerance = 1e-06
  AttachmentSupport = -> [Pad071]
  ExternalGeometry = -> [Pad071]
  FullyConstrained = true
  MakeInternals = false
  MapMode = 5
  Placement = pos=(33,0,0) rot=(0.57735,0.57735,0.57735;2.0944rad)
  sketch-geometry (4):
    g0: LineSegment StartX=43.05 StartY=10.4 StartZ=0 EndX=41.45 EndY=10.4 EndZ=0
    g1: LineSegment StartX=41.45 StartY=10.4 StartZ=0 EndX=41.45 EndY=8 EndZ=0
    g2: LineSegment StartX=41.45 StartY=8 StartZ=0 EndX=43.05 EndY=8 EndZ=0
    g3: LineSegment StartX=43.05 StartY=8 StartZ=0 EndX=43.05 EndY=10.4 EndZ=0
  constraints (12):
    c: Coincident(g0,g1)
    c: Coincident(g1,g2)
    c: Coincident(g2,g3)
    c: Coincident(g3,g0)
    c: Horizontal(g0)
    c: Horizontal(g2)
    c: Vertical(g1)
    c: Vertical(g3)
    c: DistanceY(g1,g1) = 2.4
    c: DistanceX(g2,g2) = 1.6
    c: PointOnObject(g-3,g0)
    c: DistanceX(g-3,g0) = 0.1
FEATURE [PartDesign::Pad] Pad072
  BaseFeature = -> Pad071
  Direction = (1,0,0)
  Length = 10.72
  Length2 = 10
  Profile = -> Sketch100
  ReferenceAxis = -> Sketch100 [N_Axis]
  Refine = true
  Reversed = true
  Suppressed = false
  Type = 0
FEATURE [Sketcher::SketchObject] Sketch101
  ArcFitTolerance = 1e-06
  AttachmentSupport = -> [Pad072]
  ExternalGeometry = -> [Pad072]
  FullyConstrained = true
  MakeInternals = false
  MapMode = 5
  Placement = pos=(3,0,0) rot=(0.57735,-0.57735,-0.57735;2.0944rad)
  sketch-geometry (4):
    g0: LineSegment StartX=-43.05 StartY=10.4 StartZ=0 EndX=-43.05 EndY=8 EndZ=0
    g1: LineSegment StartX=-43.05 StartY=8 StartZ=0 EndX=-41.45 EndY=8 EndZ=0
    g2: LineSegment StartX=-41.45 StartY=8 StartZ=0 EndX=-41.45 EndY=10.4 EndZ=0
    g3: LineSegment StartX=-41.45 StartY=10.4 StartZ=0 EndX=-43.05 EndY=10.4 EndZ=0
  constraints (10):
    c: Coincident(g0,g1)
    c: Coincident(g1,g2)
    c: Coincident(g2,g3)
    c: Coincident(g3,g0)
    c: Vertical(g0)
    c: Vertical(g2)
    c: Horizontal(g1)
    c: Horizontal(g3)
    c: Coincident(g0,g-3)
    c: Coincident(g1,g-5)
FEATURE [PartDesign::Pad] Pad073
  BaseFeature = -> Pad072
  Direction = (-1,0,0)
  Length = 10.93
  Length2 = 10
  Profile = -> Sketch101
  ReferenceAxis = -> Sketch101 [N_Axis]
  Refine = true
  Reversed = true
  Suppressed = false
  Type = 0
FEATURE [Sketcher::SketchObject] Sketch102
  ArcFitTolerance = 1e-06
  AttachmentSupport = -> [Pad073]
  ExternalGeometry = -> [Pad073]
  FullyConstrained = true
  MakeInternals = false
  MapMode = 5
  Placement = pos=(0,0,10.4) rot=(0,0,1;0rad)
  sketch-geometry (8):
    g0: LineSegment StartX=13.93 StartY=43.05 StartZ=0 EndX=13.93 EndY=45.692 EndZ=0
    g1: LineSegment StartX=3 StartY=43.05 StartZ=0 EndX=3 EndY=44.75 EndZ=0
    g2: LineSegment StartX=3 StartY=44.75 StartZ=0 EndX=13.93 EndY=45.692 EndZ=0
    g3: LineSegment StartX=22.28 StartY=43.05 StartZ=0 EndX=22.28 EndY=45.691 EndZ=0
    g4: LineSegment StartX=22.28 StartY=45.691 StartZ=0 EndX=33 EndY=44.75 EndZ=0
    g5: LineSegment StartX=33 StartY=43.05 StartZ=0 EndX=33 EndY=44.75 EndZ=0
    g6: LineSegment StartX=3 StartY=43.05 StartZ=0 EndX=13.93 EndY=43.05 EndZ=0
    g7: LineSegment StartX=22.28 StartY=43.05 StartZ=0 EndX=33 EndY=43.05 EndZ=0
  constraints (20):
    c: Coincident(g0,g-3)
    c: Vertical(g0)
    c: Coincident(g1,g-3)
    c: Vertical(g1)
    c: Coincident(g2,g1)
    c: Coincident(g2,g0)
    c: Coincident(g3,g-4)
    c: Vertical(g3)
    c: Coincident(g4,g3)
    c: Coincident(g5,g-4)
    c: Coincident(g5,g4)
    c: Vertical(g5)
    c: DistanceY(g1,g1) = 1.7
    c: DistanceY(g0,g0) = 2.642
    c: Coincident(g6,g1)
    c: Coincident(g6,g0)
    c: Coincident(g7,g3)
    c: Coincident(g7,g5)
    c: DistanceY(g5,g5) = 1.7
    c: DistanceY(g3,g3) = 2.641
FEATURE [PartDesign::Pad] Pad074
  BaseFeature = -> Pad073
  Direction = (0,0,1)
  Length = 6.9
  Length2 = 10
  Profile = -> Sketch102
  ReferenceAxis = -> Sketch102 [N_Axis]
  Refine = true
  Reversed = true
  Suppressed = false
  Type = 0
FEATURE [PartDesign::Pocket] Pocket042
  BaseFeature = -> Pad074
  Direction = (0,0,-1)
  Length = 0.9
  Length2 = 5
  Profile = -> Pad074 [Face25,Face24]
  Refine = true
  Suppressed = false
  Type = 0
FEATURE [Sketcher::SketchObject] Sketch103
  ArcFitTolerance = 1e-06
  AttachmentSupport = -> [Pocket042]
  ExternalGeometry = -> [Pocket042]
  FullyConstrained = true
  MakeInternals = false
  MapMode = 5
  Placement = pos=(33,0,0) rot=(0.57735,0.57735,0.57735;2.0944rad)
  sketch-geometry (15):
    g0: LineSegment StartX=18.75 StartY=3.5 StartZ=0 EndX=18.75 EndY=8 EndZ=0
    g1: LineSegment StartX=18.75 StartY=8 StartZ=0 EndX=21.15 EndY=10.4 EndZ=0
    g2: LineSegment StartX=21.15 StartY=10.4 StartZ=0 EndX=41.45 EndY=10.4 EndZ=0
    g3: LineSegment StartX=41.45 StartY=10.4 StartZ=0 EndX=41.45 EndY=8 EndZ=0
    g4: LineSegment StartX=41.45 StartY=8 StartZ=0 EndX=43.05 EndY=8 EndZ=0
    g5: LineSegment StartX=43.05 StartY=8 StartZ=0 EndX=43.05 EndY=3.5 EndZ=0
    g6: LineSegment StartX=43.05 StartY=3.5 StartZ=0 EndX=39.8 EndY=3.5 EndZ=0
    g7: LineSegment StartX=39.8 StartY=3.5 StartZ=0 EndX=39.8 EndY=5.1 EndZ=0
    g8: LineSegment StartX=39.8 StartY=5.1 StartZ=0 EndX=35.9 EndY=5.1 EndZ=0
    g9: LineSegment StartX=35.9 StartY=5.1 StartZ=0 EndX=35.9 EndY=3.5 EndZ=0
    g10: LineSegment StartX=35.9 StartY=3.5 StartZ=0 EndX=25.6 EndY=3.5 EndZ=0
    g11: LineSegment StartX=25.6 StartY=3.5 StartZ=0 EndX=25.6 EndY=5.1 EndZ=0
    g12: LineSegment StartX=25.6 StartY=5.1 StartZ=0 EndX=21.7 EndY=5.1 EndZ=0
    g13: LineSegment StartX=21.7 StartY=5.1 StartZ=0 EndX=21.7 EndY=3.5 EndZ=0
    g14: LineSegment StartX=21.7 StartY=3.5 StartZ=0 EndX=18.75 EndY=3.5 EndZ=0
  constraints (38):
    c: Coincident(g0,g-3)
    c: Coincident(g0,g-4)
    c: Coincident(g1,g0)
    c: Coincident(g1,g-5)
    c: Coincident(g2,g1)
    c: Coincident(g2,g-6)
    c: Coincident(g3,g2)
    c: Coincident(g3,g-7)
    c: Coincident(g4,g3)
    c: Coincident(g4,g-8)
    c: Coincident(g5,g4)
    c: Coincident(g5,g-8)
    c: Coincident(g6,g5)
    c: Horizontal(g6)
    c: Coincident(g7,g6)
    c: Vertical(g7)
    c: Coincident(g8,g7)
    c: Horizontal(g8)
    c: Coincident(g9,g8)
    c: Vertical(g9)
    c: Coincident(g10,g9)
    c: Horizontal(g10)
    c: Coincident(g11,g10)
    c: Vertical(g11)
    c: Coincident(g12,g11)
    c: Horizontal(g12)
    c: Coincident(g13,g12)
    c: Vertical(g13)
    c: Coincident(g14,g13)
    c: Coincident(g14,g0)
    c: Horizontal(g14)
    c: DistanceX(g6,g6) = 3.25
    c: DistanceX(g8,g8) = 3.9
    c: DistanceX(g12,g12) = 3.9
    c: DistanceY(g9,g9) = 1.6
    c: DistanceY(g11,g11) = 1.6
    c: DistanceX(g14,g14) = 2.95
    c: DistanceY(g13,g13) = 1.6
FEATURE [PartDesign::Pad] Pad075
  BaseFeature = -> Pocket042
  Direction = (1,0,0)
  Length = 1.5
  Length2 = 10
  Profile = -> Sketch103
  ReferenceAxis = -> Sketch103 [N_Axis]
  Refine = true
  Reversed = true
  Suppressed = false
  Type = 0
FEATURE [Sketcher::SketchObject] Sketch104
  ArcFitTolerance = 1e-06
  AttachmentSupport = -> [Pocket041]
  ExternalGeometry = -> [Pocket041]
  FullyConstrained = true
  MakeInternals = false
  MapMode = 5
  Placement = pos=(0,0,5.5) rot=(0,0,1;0rad)
  sketch-geometry (2):
    g0: Circle CenterX=8.65 CenterY=38 CenterZ=0 NormalX=0 NormalY=0 NormalZ=1 AngleXU=0 Radius=1
    g1: Circle CenterX=12.5 CenterY=23.2 CenterZ=0 NormalX=0 NormalY=0 NormalZ=1 AngleXU=0 Radius=1
  constraints (4):
    c: Coincident(g0,g-3)
    c: Coincident(g1,g-4)
    c: Radius(g1) = 1
    c: Radius(g0) = 1
FEATURE [PartDesign::Pocket] Pocket043
  BaseFeature = -> Pocket041
  Direction = (0,0,-1)
  Length = 5
  Length2 = 5
  Profile = -> Sketch104
  ReferenceAxis = -> Sketch104 [N_Axis]
  Refine = true
  Suppressed = false
  Type = 0
FEATURE [Sketcher::SketchObject] Sketch105
  ArcFitTolerance = 1e-06
  AttachmentSupport = -> [Pocket043]
  ExternalGeometry = -> [Pocket043]
  FullyConstrained = true
  MakeInternals = false
  MapMode = 5
  Placement = pos=(0,0,3.5) rot=(0,0,1;0rad)
  sketch-geometry (8):
    g0: LineSegment StartX=14.6 StartY=45.75 StartZ=0 EndX=14.6 EndY=42.95 EndZ=0
    g1: LineSegment StartX=14.6 StartY=42.95 StartZ=0 EndX=14.1 EndY=42.95 EndZ=0
    g2: LineSegment StartX=14.1 StartY=42.95 StartZ=0 EndX=14.1 EndY=45.7069 EndZ=0
    g3: LineSegment StartX=14.1 StartY=45.7069 StartZ=0 EndX=14.6 EndY=45.75 EndZ=0
    g4: LineSegment StartX=21.6 StartY=45.75 StartZ=0 EndX=22.1 EndY=45.7061 EndZ=0
    g5: LineSegment StartX=22.1 StartY=45.7061 StartZ=0 EndX=22.1 EndY=42.95 EndZ=0
    g6: LineSegment StartX=22.1 StartY=42.95 StartZ=0 EndX=21.6 EndY=42.95 EndZ=0
    g7: LineSegment StartX=21.6 StartY=45.75 StartZ=0 EndX=21.6 EndY=42.95 EndZ=0
  constraints (20):
    c: Coincident(g0,g-6)
    c: Coincident(g0,g-6)
    c: Coincident(g1,g0)
    c: Horizontal(g1)
    c: Coincident(g2,g1)
    c: PointOnObject(g2,g-5)
    c: Vertical(g2)
    c: Coincident(g3,g2)
    c: Coincident(g3,g0)
    c: Coincident(g4,g-4)
    c: PointOnObject(g4,g-3)
    c: Coincident(g5,g4)
    c: Vertical(g5)
    c: Coincident(g6,g5)
    c: Coincident(g6,g-4)
    c: Horizontal(g6)
    c: DistanceX(g1,g1) = 0.5
    c: DistanceX(g6,g6) = 0.5
    c: Coincident(g7,g4)
    c: Coincident(g7,g6)
FEATURE [PartDesign::Pad] Pad076
  BaseFeature = -> Pocket043
  Direction = (0,0,1)
  Length = 6
  Length2 = 10
  Profile = -> Sketch105
  ReferenceAxis = -> Sketch105 [N_Axis]
  Refine = true
  Suppressed = false
  Type = 0
FEATURE [Sketcher::SketchObject] Sketch106
  ArcFitTolerance = 1e-06
  AttachmentSupport = -> [Pad075]
  ExternalGeometry = -> [Pad075]
  FullyConstrained = true
  MakeInternals = false
  MapMode = 5
  Placement = pos=(0,0,10.4) rot=(1,0,0;3.14159rad)
  sketch-geometry (2):
    g0: Circle CenterX=12.5 CenterY=-23.2 CenterZ=0 NormalX=0 NormalY=0 NormalZ=1 AngleXU=0 Radius=2.3
    g1: Circle CenterX=8.65 CenterY=-38 CenterZ=0 NormalX=0 NormalY=0 NormalZ=1 AngleXU=0 Radius=2.3
  constraints (6):
    c: Radius(g0) = 2.3
    c: Radius(g1) = 2.3
    c: DistanceX(g-4,g0) = 2.5
    c: DistanceY(g0,g-4) = 2.05
    c: DistanceX(g-3,g1) = 5.65
    c: DistanceY(g1,g-3) = 5.25
FEATURE [PartDesign::Pad] Pad077
  BaseFeature = -> Pad075
  Direction = (0,0,-1)
  Length = 4.9
  Length2 = 10
  Profile = -> Sketch106
  ReferenceAxis = -> Sketch106 [N_Axis]
  Refine = true
  Suppressed = false
  Type = 0
FEATURE [Sketcher::SketchObject] Sketch107
  ArcFitTolerance = 1e-06
  AttachmentSupport = -> [Pad077]
  ExternalGeometry = -> [Pad077]
  FullyConstrained = true
  MakeInternals = false
  MapMode = 5
  Placement = pos=(0,0,5.5) rot=(1,0,0;3.14159rad)
  sketch-geometry (2):
    g0: Circle CenterX=8.65 CenterY=-38 CenterZ=0 NormalX=0 NormalY=0 NormalZ=1 AngleXU=0 Radius=0.75
    g1: Circle CenterX=12.5 CenterY=-23.2 CenterZ=0 NormalX=0 NormalY=0 NormalZ=1 AngleXU=0 Radius=0.75
  constraints (4):
    c: Coincident(g0,g-4)
    c: Coincident(g1,g-3)
    c: Radius(g1) = 0.75
    c: Radius(g0) = 0.75
FEATURE [PartDesign::Pocket] Pocket044
  BaseFeature = -> Pad077
  Direction = (0,0,1)
  Length = 4.9
  Length2 = 5
  Profile = -> Sketch107
  ReferenceAxis = -> Sketch107 [N_Axis]
  Refine = true
  Suppressed = false
  Type = 0
FEATURE [Sketcher::SketchObject] Sketch108
  ArcFitTolerance = 1e-06
  AttachmentSupport = -> [Pocket044]
  ExternalGeometry = -> [Pocket044]
  FullyConstrained = true
  MakeInternals = false
  MapMode = 5
  Placement = pos=(33,0,-2.28e-14) rot=(0.57735,0.57735,0.57735;2.0944rad)
  sketch-geometry (16):
    g0: LineSegment StartX=21.7 StartY=5.1 StartZ=0 EndX=21.7 EndY=3.4 EndZ=0
    g1: LineSegment StartX=21.7 StartY=3.4 StartZ=0 EndX=25.6 EndY=3.4 EndZ=0
    g2: LineSegment StartX=25.6 StartY=3.4 StartZ=0 EndX=25.6 EndY=5.1 EndZ=0
    g3: LineSegment StartX=25.6 StartY=5.1 StartZ=0 EndX=27.1 EndY=5.1 EndZ=0
    g4: LineSegment StartX=27.1 StartY=5.1 StartZ=0 EndX=27.1 EndY=2.1 EndZ=0
    g5: LineSegment StartX=27.1 StartY=2.1 StartZ=0 EndX=20.2 EndY=2.1 EndZ=0
    g6: LineSegment StartX=20.2 StartY=2.1 StartZ=0 EndX=20.2 EndY=5.1 EndZ=0
    g7: LineSegment StartX=21.7 StartY=5.1 StartZ=0 EndX=20.2 EndY=5.1 EndZ=0
    g8: LineSegment StartX=35.9 StartY=5.1 StartZ=0 EndX=35.9 EndY=3.4 EndZ=0
    g9: LineSegment StartX=35.9 StartY=3.4 StartZ=0 EndX=39.8 EndY=3.4 EndZ=0
    g10: LineSegment StartX=39.8 StartY=3.4 StartZ=0 EndX=39.8 EndY=5.1 EndZ=0
    g11: LineSegment StartX=39.8 StartY=5.1 StartZ=0 EndX=41.3 EndY=5.1 EndZ=0
    g12: LineSegment StartX=41.3 StartY=5.1 StartZ=0 EndX=41.3 EndY=2.1 EndZ=0
    g13: LineSegment StartX=41.3 StartY=2.1 StartZ=0 EndX=34.4 EndY=2.1 EndZ=0
    g14: LineSegment StartX=34.4 StartY=2.1 StartZ=0 EndX=34.4 EndY=5.1 EndZ=0
    g15: LineSegment StartX=35.9 StartY=5.1 StartZ=0 EndX=34.4 EndY=5.1 EndZ=0
  constraints (44):
    c: Coincident(g0,g-8)
    c: Vertical(g0)
    c: Coincident(g1,g0)
    c: Horizontal(g1)
    c: Coincident(g2,g1)
    c: Coincident(g2,g-7)
    c: Vertical(g2)
    c: Coincident(g3,g2)
    c: Horizontal(g3)
    c: Coincident(g4,g3)
    c: Vertical(g4)
    c: Coincident(g5,g4)
    c: Horizontal(g5)
    c: Coincident(g6,g5)
    c: Vertical(g6)
    c: Coincident(g7,g0)
    c: Coincident(g7,g6)
    c: Horizontal(g7)
    c: DistanceX(g7,g7) = 1.5
    c: DistanceX(g3,g3) = 1.5
    c: DistanceY(g0,g0) = 1.7
    c: DistanceY(g6,g6) = 3
    c: Coincident(g8,g-5)
    c: Vertical(g8)
    c: Coincident(g9,g8)
    c: Horizontal(g9)
    c: Coincident(g10,g9)
    c: Coincident(g10,g-4)
    c: Vertical(g10)
    c: Coincident(g11,g10)
    c: Horizontal(g11)
    c: Coincident(g12,g11)
    c: Vertical(g12)
    c: Coincident(g13,g12)
    c: Horizontal(g13)
    c: Coincident(g14,g13)
    c: Vertical(g14)
    c: Coincident(g15,g8)
    c: Coincident(g15,g14)
    c: Horizontal(g15)
    c: DistanceX(g15,g15) = 1.5
    c: DistanceX(g11,g11) = 1.5
    c: DistanceY(g14,g14) = 3
    c: DistanceY(g8,g8) = 1.7
FEATURE [PartDesign::Pad] Pad078
  BaseFeature = -> Pocket044
  Direction = (1,0,0)
  Length = 1.5
  Length2 = 10
  Profile = -> Sketch108
  ReferenceAxis = -> Sketch108 [N_Axis]
  Refine = true
  Suppressed = false
  Type = 0
FEATURE [Sketcher::SketchObject] Sketch109
  ArcFitTolerance = 1e-06
  AttachmentSupport = -> [Pad078]
  ExternalGeometry = -> [Pad078]
  FullyConstrained = true
  MakeInternals = false
  MapMode = 5
  Placement = pos=(3,0,0) rot=(0.57735,-0.57735,-0.57735;2.0944rad)
  sketch-geometry (6):
    g0: LineSegment StartX=-43.05 StartY=3.5 StartZ=0 EndX=-43.05 EndY=8 EndZ=0
    g1: LineSegment StartX=-43.05 StartY=8 StartZ=0 EndX=-41.45 EndY=8 EndZ=0
    g2: LineSegment StartX=-41.45 StartY=8 StartZ=0 EndX=-41.45 EndY=10.4 EndZ=0
    g3: LineSegment StartX=-41.45 StartY=10.4 StartZ=0 EndX=-32.75 EndY=10.4 EndZ=0
    g4: LineSegment StartX=-32.75 StartY=10.4 StartZ=0 EndX=-32.75 EndY=3.5 EndZ=0
    g5: LineSegment StartX=-43.05 StartY=3.5 StartZ=0 EndX=-32.75 EndY=3.5 EndZ=0
  constraints (13):
    c: Coincident(g0,g-6)
    c: Coincident(g0,g-6)
    c: Coincident(g1,g0)
    c: Coincident(g1,g-5)
    c: Coincident(g2,g1)
    c: Coincident(g2,g-4)
    c: Coincident(g3,g2)
    c: Coincident(g3,g-3)
    c: Coincident(g4,g3)
    c: Vertical(g4)
    c: Coincident(g5,g0)
    c: Coincident(g5,g4)
    c: Horizontal(g5)
FEATURE [PartDesign::Pad] Pad079
  BaseFeature = -> Pad078
  Direction = (-1,0,0)
  Length = 1.5
  Length2 = 10
  Profile = -> Sketch109
  ReferenceAxis = -> Sketch109 [N_Axis]
  Refine = true
  Reversed = true
  Suppressed = false
  Type = 0
FEATURE [PartDesign::Fillet] Fillet003
  Base = -> Pad076 [Edge47,Edge45,Edge42,Edge38,Edge32,Edge49]
  BaseFeature = -> Pad076
  Radius = 0.5
  Refine = true
  SupportTransform = false
  Suppressed = false
  UseAllEdges = false
FEATURE [PartDesign::Pocket] Pocket045
  BaseFeature = -> Fillet003
  Direction = (0,0,1)
  Length = 0.6
  Length2 = 5
  Profile = -> Fillet003 [Face54]
  Refine = true
  Suppressed = false
  Type = 0
FEATURE [Sketcher::SketchObject] Sketch110
  ArcFitTolerance = 1e-06
  AttachmentOffset = pos=(0,0,-8.4) rot=(0,0,1;0rad)
  AttachmentSupport = -> [Pad079]
  ExternalGeometry = -> [Pad079]
  FullyConstrained = true
  MakeInternals = false
  MapMode = 5
  Placement = pos=(0,0,3.5) rot=(0,0,1;0rad)
  sketch-geometry (10):
    g0: LineSegment StartX=4.5 StartY=32.75 StartZ=0 EndX=4.5 EndY=31.25 EndZ=0
    g1: LineSegment StartX=4.5 StartY=31.25 StartZ=0 EndX=1.5 EndY=31.25 EndZ=0
    g2: LineSegment StartX=1.5 StartY=31.25 StartZ=0 EndX=1.5 EndY=17.25 EndZ=0
    g3: LineSegment StartX=1.5 StartY=17.25 StartZ=0 EndX=8.5 EndY=17.25 EndZ=0
    g4: LineSegment StartX=8.5 StartY=17.25 StartZ=0 EndX=8.5 EndY=18.75 EndZ=0
    g5: LineSegment StartX=8.5 StartY=18.75 StartZ=0 EndX=10 EndY=18.75 EndZ=0
    g6: LineSegment StartX=10 StartY=18.75 StartZ=0 EndX=10 EndY=15.75 EndZ=0
    g7: LineSegment StartX=10 StartY=15.75 StartZ=0 EndX=0 EndY=15.75 EndZ=0
    g8: LineSegment StartX=0 StartY=15.75 StartZ=0 EndX=0 EndY=32.75 EndZ=0
    g9: LineSegment StartX=0 StartY=32.75 StartZ=0 EndX=4.5 EndY=32.75 EndZ=0
  constraints (29):
    c: PointOnObject(g0,g-3)
    c: Vertical(g0)
    c: Coincident(g1,g0)
    c: Horizontal(g1)
    c: Coincident(g2,g1)
    c: Vertical(g2)
    c: Coincident(g3,g2)
    c: Horizontal(g3)
    c: Coincident(g4,g3)
    c: Vertical(g4)
    c: Coincident(g5,g4)
    c: Horizontal(g5)
    c: Coincident(g6,g5)
    c: Vertical(g6)
    c: Coincident(g7,g6)
    c: PointOnObject(g7,g-2)
    c: Horizontal(g7)
    c: Coincident(g8,g7)
    c: PointOnObject(g8,g-2)
    c: Coincident(g9,g8)
    c: Coincident(g9,g0)
    c: Horizontal(g9)
    c: DistanceX(g-3,g0) = 1.5
    c: DistanceY(g1,g8) = 1.5
    c: DistanceX(g8,g1) = 1.5
    c: DistanceX(g3,g6) = 1.5
    c: Coincident(g5,g-5)
    c: DistanceY(g7,g2) = 1.5
    c: DistanceY(g6,g-4) = 1.5
FEATURE [PartDesign::Pad] Pad080
  BaseFeature = -> Pad079
  Direction = (0,0,1)
  Length = 8.4
  Length2 = 10
  Profile = -> Sketch110
  ReferenceAxis = -> Sketch110 [N_Axis]
  Refine = true
  Suppressed = false
  Type = 0
FEATURE [PartDesign::Pad] Pad081
  BaseFeature = -> Pad080
  Direction = (-1,0,0)
  Length = 1.5
  Length2 = 10
  Profile = -> Pad080 [Face24]
  Refine = true
  Suppressed = false
  Type = 0
FEATURE [Sketcher::SketchObject] Sketch111
  ArcFitTolerance = 1e-06
  AttachmentSupport = -> [Pad081]
  ExternalGeometry = -> [Pad081]
  FullyConstrained = true
  MakeInternals = false
  MapMode = 5
  Placement = pos=(10,0,0) rot=(0.57735,0.57735,0.57735;2.0944rad)
  sketch-geometry (3):
    g0: LineSegment StartX=18.75 StartY=11.9 StartZ=0 EndX=18.75 EndY=9.5 EndZ=0
    g1: LineSegment StartX=18.75 StartY=9.5 StartZ=0 EndX=21.15 EndY=11.9 EndZ=0
    g2: LineSegment StartX=21.15 StartY=11.9 StartZ=0 EndX=18.75 EndY=11.9 EndZ=0
  constraints (6):
    c: Coincident(g0,g-3)
    c: Coincident(g0,g-4)
    c: Coincident(g1,g0)
    c: Coincident(g1,g-4)
    c: Coincident(g2,g1)
    c: Coincident(g2,g0)
FEATURE [PartDesign::Pad] Pad082
  BaseFeature = -> Pad081
  Direction = (1,0,0)
  Length = 1.5
  Length2 = 10
  Profile = -> Sketch111
  ReferenceAxis = -> Sketch111 [N_Axis]
  Refine = true
  Reversed = true
  Suppressed = false
  Type = 0
FEATURE [PartDesign::Pad] Pad083
  BaseFeature = -> Pad082
  Direction = (0,-1,0)
  Length = 1.5
  Length2 = 10
  Profile = -> Pad082 [Face38]
  Refine = true
  Suppressed = false
  Type = 0
FEATURE [Sketcher::SketchObject] Sketch112
  ArcFitTolerance = 1e-06
  AttachmentSupport = -> [Pad083]
  ExternalGeometry = -> [Pad083]
  FullyConstrained = true
  MakeInternals = false
  MapMode = 5
  Placement = pos=(10,0,0) rot=(0.57735,0.57735,0.57735;2.0944rad)
  sketch-geometry (4):
    g0: LineSegment StartX=17.25 StartY=11.9 StartZ=0 EndX=20.75 EndY=22.9 EndZ=0
    g1: LineSegment StartX=20.75 StartY=22.9 StartZ=0 EndX=32.75 EndY=22.9 EndZ=0
    g2: LineSegment StartX=17.25 StartY=11.9 StartZ=0 EndX=32.75 EndY=11.9 EndZ=0
    g3: LineSegment StartX=32.75 StartY=11.9 StartZ=0 EndX=32.75 EndY=22.9 EndZ=0
  constraints (11):
    c: PointOnObject(g0,g-3)
    c: Coincident(g1,g0)
    c: Horizontal(g1)
    c: DistanceY(g-5,g1) = 11
    c: DistanceX(g-4,g0) = 1.5
    c: DistanceX(g1,g1) = 12
    c: Coincident(g2,g0)
    c: Coincident(g2,g-6)
    c: Coincident(g3,g2)
    c: Coincident(g3,g1)
    c: Vertical(g3)
FEATURE [PartDesign::Pad] Pad084
  BaseFeature = -> Pad083
  Direction = (1,0,0)
  Length = 1.5
  Length2 = 10
  Profile = -> Sketch112
  ReferenceAxis = -> Sketch112 [N_Axis]
  Refine = true
  Reversed = true
  Suppressed = false
  Type = 0
FEATURE [Sketcher::SketchObject] Sketch113
  ArcFitTolerance = 1e-06
  AttachmentSupport = -> [Pad084]
  ExternalGeometry = -> [Pad084]
  FullyConstrained = true
  MakeInternals = false
  MapMode = 5
  Placement = pos=(8.5,0,0) rot=(0.57735,-0.57735,-0.57735;2.0944rad)
  sketch-geometry (4):
    g0: LineSegment StartX=-32.75 StartY=22.9 StartZ=0 EndX=-32.75 EndY=11.9 EndZ=0
    g1: LineSegment StartX=-32.75 StartY=11.9 StartZ=0 EndX=-31.25 EndY=11.9 EndZ=0
    g2: LineSegment StartX=-31.25 StartY=11.9 StartZ=0 EndX=-31.25 EndY=22.9 EndZ=0
    g3: LineSegment StartX=-31.25 StartY=22.9 StartZ=0 EndX=-32.75 EndY=22.9 EndZ=0
  constraints (10):
    c: Coincident(g0,g1)
    c: Coincident(g1,g2)
    c: Coincident(g2,g3)
    c: Coincident(g3,g0)
    c: Vertical(g2)
    c: Horizontal(g1)
    c: Horizontal(g3)
    c: Coincident(g0,g-4)
    c: DistanceX(g1,g1) = 1.5
    c: Coincident(g0,g-4)
FEATURE [PartDesign::Pad] Pad085
  BaseFeature = -> Pad084
  Direction = (-1,0,0)
  Length = 8.5
  Length2 = 10
  Profile = -> Sketch113
  ReferenceAxis = -> Sketch113 [N_Axis]
  Refine = true
  Suppressed = false
  Type = 0
FEATURE [Sketcher::SketchObject] Sketch114
  ArcFitTolerance = 1e-06
  AttachmentSupport = -> [Pad085]
  ExternalGeometry = -> [Pad085]
  FullyConstrained = true
  MakeInternals = false
  MapMode = 5
  Placement = pos=(8.5,0,0) rot=(0.57735,-0.57735,-0.57735;2.0944rad)
  sketch-geometry (4):
    g0: LineSegment StartX=-31.25 StartY=22.9 StartZ=0 EndX=-20.75 EndY=22.9 EndZ=0
    g1: LineSegment StartX=-20.75 StartY=22.9 StartZ=0 EndX=-20.2727 EndY=21.4 EndZ=0
    g2: LineSegment StartX=-20.2727 StartY=21.4 StartZ=0 EndX=-31.25 EndY=21.4 EndZ=0
    g3: LineSegment StartX=-31.25 StartY=21.4 StartZ=0 EndX=-31.25 EndY=22.9 EndZ=0
  constraints (10):
    c: Coincident(g0,g-4)
    c: Coincident(g1,g0)
    c: PointOnObject(g1,g-4)
    c: Coincident(g2,g1)
    c: PointOnObject(g2,g-5)
    c: Horizontal(g2)
    c: Coincident(g3,g2)
    c: Coincident(g3,g0)
    c: Coincident(g0,g-5)
    c: DistanceY(g3,g3) = 1.5
FEATURE [PartDesign::Pad] Pad086
  BaseFeature = -> Pad085
  Direction = (-1,0,0)
  Length = 8.5
  Length2 = 10
  Profile = -> Sketch114
  ReferenceAxis = -> Sketch114 [N_Axis]
  Refine = true
  Suppressed = false
  Type = 0
FEATURE [Sketcher::SketchObject] Sketch115
  ArcFitTolerance = 1e-06
  AttachmentSupport = -> [Pad086]
  ExternalGeometry = -> [Pad086]
  FullyConstrained = true
  MakeInternals = false
  MapMode = 5
  Placement = pos=(1.3e-15,0,0) rot=(0.57735,-0.57735,-0.57735;2.0944rad)
  sketch-geometry (4):
    g0: LineSegment StartX=-20.2727 StartY=21.4 StartZ=0 EndX=-17.25 EndY=11.9 EndZ=0
    g1: LineSegment StartX=-17.25 StartY=11.9 StartZ=0 EndX=-31.25 EndY=11.9 EndZ=0
    g2: LineSegment StartX=-20.2727 StartY=21.4 StartZ=0 EndX=-31.25 EndY=21.4 EndZ=0
    g3: LineSegment StartX=-31.25 StartY=21.4 StartZ=0 EndX=-31.25 EndY=11.9 EndZ=0
  constraints (8):
    c: Coincident(g0,g-6)
    c: Coincident(g0,g-6)
    c: Coincident(g1,g0)
    c: Coincident(g1,g-5)
    c: Coincident(g2,g0)
    c: Coincident(g2,g-4)
    c: Coincident(g3,g2)
    c: Coincident(g3,g1)
FEATURE [PartDesign::Pad] Pad087
  BaseFeature = -> Pad086
  Direction = (-1,0,0)
  Length = 1.5
  Length2 = 10
  Profile = -> Sketch115
  ReferenceAxis = -> Sketch115 [N_Axis]
  Refine = true
  Reversed = true
  Suppressed = false
  Type = 0
FEATURE [Sketcher::SketchObject] Sketch116
  ArcFitTolerance = 1e-06
  AttachmentSupport = -> [Pad087]
  ExternalGeometry = -> [Pad087]
  FullyConstrained = true
  MakeInternals = false
  MapMode = 5
  Placement = pos=(9e-16,0,0) rot=(0.57735,-0.57735,-0.57735;2.0944rad)
  sketch-geometry (9):
    g0: LineSegment StartX=-31.25 StartY=21.4 StartZ=0 EndX=-31.25 EndY=14.7 EndZ=0
    g1: LineSegment StartX=-31.25 StartY=14.7 StartZ=0 EndX=-28.05 EndY=14.7 EndZ=0
    g2: LineSegment StartX=-28.05 StartY=14.7 StartZ=0 EndX=-28.05 EndY=21.4 EndZ=0
    g3: LineSegment StartX=-28.05 StartY=21.4 StartZ=0 EndX=-31.25 EndY=21.4 EndZ=0
    g4: LineSegment StartX=-26.55 StartY=21.4 StartZ=0 EndX=-26.55 EndY=11.9 EndZ=0
    g5: LineSegment StartX=-26.55 StartY=11.9 StartZ=0 EndX=-18.8241 EndY=11.9 EndZ=0
    g6: LineSegment StartX=-18.8241 StartY=11.9 StartZ=0 EndX=-21.8468 EndY=21.4 EndZ=0
    g7: LineSegment StartX=-21.8468 StartY=21.4 StartZ=0 EndX=-26.55 EndY=21.4 EndZ=0
    g8: LineSegment [constr] StartX=-19.5372 StartY=19.0883 StartZ=0 EndX=-20.9666 EndY=18.6335 EndZ=0
  constraints (28):
    c: Coincident(g0,g1)
    c: Coincident(g1,g2)
    c: Coincident(g2,g3)
    c: Coincident(g3,g0)
    c: Vertical(g0)
    c: Vertical(g2)
    c: Horizontal(g1)
    c: Horizontal(g3)
    c: Vertical(g4)
    c: Coincident(g5,g4)
    c: Horizontal(g5)
    c: Coincident(g6,g5)
    c: Coincident(g7,g6)
    c: Coincident(g7,g4)
    c: Horizontal(g7)
    c: DistanceY(g6,g-4) = 1.5
    c: DistanceY(g0,g-5) = 1.5
    c: Parallel(g6,g-4)
    c: DistanceY(g-6,g5) = 0
    c: DistanceX(g-5,g0) = 1.5
    c: DistanceX(g2,g4) = 1.5
    c: PointOnObject(g8,g-4)
    c: PointOnObject(g8,g6)
    c: Angle(g8,g-4) = 1.5708
    c: Distance(g8) = 1.5
    c: Distance(g-4,g8) = 4
    c: DistanceX(g3,g3) = 3.2
    c: DistanceY(g2,g2) = 6.7
FEATURE [PartDesign::Pocket] Pocket046
  BaseFeature = -> Pad087
  Direction = (1,0,0)
  Length = 2
  Length2 = 5
  Profile = -> Sketch116
  ReferenceAxis = -> Sketch116 [N_Axis]
  Refine = true
  Suppressed = false
  Type = 0
FEATURE [Sketcher::SketchObject] Sketch117
  ArcFitTolerance = 1e-06
  AttachmentSupport = -> [Pocket046]
  ExternalGeometry = -> [Pocket046]
  FullyConstrained = true
  MakeInternals = false
  MapMode = 5
  Placement = pos=(22.28,0,0) rot=(0.57735,-0.57735,-0.57735;2.0944rad)
  sketch-geometry (6):
    g0: ArcOfCircle CenterX=-38.86 CenterY=13.65 CenterZ=0 NormalX=0 NormalY=0 NormalZ=1 AngleXU=0 Radius=3.25 StartAngle=0.394791 EndAngle=2.7468
    g1: LineSegment [constr] StartX=-38.86 StartY=16.9 StartZ=0 EndX=-42.95 EndY=16.9 EndZ=0
    g2: LineSegment [constr] StartX=-42.95 StartY=16.9 StartZ=0 EndX=-42.95 EndY=11.9 EndZ=0
    g3: LineSegment StartX=-41.86 StartY=14.9 StartZ=0 EndX=-42.95 EndY=11.9 EndZ=0
    g4: LineSegment StartX=-35.86 StartY=14.9 StartZ=0 EndX=-35.05 EndY=11.9 EndZ=0
    g5: LineSegment StartX=-35.05 StartY=11.9 StartZ=0 EndX=-42.95 EndY=11.9 EndZ=0
  constraints (17):
    c: Tangent(g1,g0) = -1.5708
    c: Horizontal(g1)
    c: Coincident(g2,g1)
    c: Vertical(g2)
    c: Coincident(g3,g0)
    c: Coincident(g3,g-3)
    c: Coincident(g4,g0)
    c: Coincident(g4,g-3)
    c: Coincident(g2,g3)
    c: Radius(g0) = 3.25
    c: Coincident(g5,g4)
    c: Coincident(g5,g2)
    c: DistanceY(g2,g2) = 5
    c: DistanceX(g2,g4) = 7.9
    c: DistanceX(g1,g1) = 4.09
    c: DistanceY(g0,g0) = 0
    c: DistanceY(g4,g0) = 3
FEATURE [PartDesign::Pad] Pad088
  BaseFeature = -> Pocket046
  Direction = (-1,0,0)
  Length = 3
  Length2 = 10
  Profile = -> Sketch117
  ReferenceAxis = -> Sketch117 [N_Axis]
  Refine = true
  Reversed = true
  Suppressed = false
  Type = 0
FEATURE [PartDesign::Pad] Pad089
  BaseFeature = -> Pad088
  Direction = (-1,0,0)
  Length = 11.35
  Length2 = 10
  Profile = -> Sketch117
  ReferenceAxis = -> Sketch117 [N_Axis]
  Refine = true
  Suppressed = false
  Type = 0
FEATURE [Sketcher::SketchObject] Sketch118
  ArcFitTolerance = 1e-06
  AttachmentSupport = -> [Pad089]
  ExternalGeometry = -> [Pad089]
  FullyConstrained = true
  MakeInternals = false
  MapMode = 5
  Placement = pos=(0,42.95,0) rot=(0,0.707107,0.707107;3.14159rad)
  sketch-geometry (4):
    g0: LineSegment StartX=-22.28 StartY=11.9 StartZ=0 EndX=-13.93 EndY=11.9 EndZ=0
    g1: LineSegment StartX=-13.93 StartY=11.9 StartZ=0 EndX=-13.93 EndY=16.9 EndZ=0
    g2: LineSegment StartX=-13.93 StartY=16.9 StartZ=0 EndX=-22.28 EndY=16.9 EndZ=0
    g3: LineSegment StartX=-22.28 StartY=16.9 StartZ=0 EndX=-22.28 EndY=11.9 EndZ=0
  constraints (10):
    c: Coincident(g0,g1)
    c: Coincident(g1,g2)
    c: Coincident(g2,g3)
    c: Coincident(g3,g0)
    c: Horizontal(g2)
    c: Vertical(g1)
    c: Vertical(g3)
    c: Coincident(g0,g-3)
    c: Coincident(g0,g-4)
    c: DistanceY(g3,g3) = 5
FEATURE [PartDesign::Pocket] Pocket047
  BaseFeature = -> Pad089
  Direction = (0,-1,2e-16)
  Length = 9
  Length2 = 5
  Profile = -> Sketch118
  ReferenceAxis = -> Sketch118 [N_Axis]
  Refine = true
  Suppressed = false
  Type = 0
FEATURE [Sketcher::SketchObject] Sketch119
  ArcFitTolerance = 1e-06
  AttachmentSupport = -> [Pocket047]
  ExternalGeometry = -> [Pocket047]
  FullyConstrained = false
  MakeInternals = false
  MapMode = 5
  Placement = pos=(22.28,0,0) rot=(0.57735,-0.57735,-0.57735;2.0944rad)
  sketch-geometry (4):
    g0: ArcOfCircle CenterX=-38.86 CenterY=13.65 CenterZ=0 NormalX=0 NormalY=0 NormalZ=1 AngleXU=0 Radius=1.6 StartAngle=0.0596113 EndAngle=3.16938
    g1: LineSegment StartX=-40.4594 StartY=13.6056 StartZ=0 EndX=-40.4594 EndY=10.4 EndZ=0
    g2: LineSegment StartX=-40.4594 StartY=10.4 StartZ=0 EndX=-37.2628 EndY=10.4 EndZ=0
    g3: LineSegment StartX=-37.2628 StartY=10.4 StartZ=0 EndX=-37.2628 EndY=13.7453 EndZ=0
  constraints (10):
    c: Coincident(g0,g-4)
    c: Coincident(g1,g0)
    c: PointOnObject(g1,g-6)
    c: Coincident(g2,g1)
    c: PointOnObject(g2,g-6)
    c: Coincident(g3,g2)
    c: Coincident(g3,g0)
    c: Vertical(g3)
    c: Vertical(g1)
    c: Radius(g0) = 1.6
FEATURE [PartDesign::Pocket] Pocket048
  BaseFeature = -> Pocket047
  Direction = (1,0,0)
  Length = 1.5
  Length2 = 5
  Profile = -> Sketch119
  ReferenceAxis = -> Sketch119 [N_Axis]
  Refine = true
  Suppressed = false
  Type = 0
FEATURE [PartDesign::Pocket] Pocket049
  BaseFeature = -> Pocket048
  Direction = (1,0,0)
  Length = 9.85
  Length2 = 5
  Profile = -> Sketch119
  ReferenceAxis = -> Sketch119 [N_Axis]
  Refine = true
  Reversed = true
  Suppressed = false
  Type = 0
FEATURE [Sketcher::SketchObject] Sketch120
  ArcFitTolerance = 1e-06
  AttachmentSupport = -> [Pocket049]
  ExternalGeometry = -> [Pocket049]
  FullyConstrained = true
  MakeInternals = false
  MapMode = 5
  Placement = pos=(13.93,0,0) rot=(0.57735,0.57735,0.57735;2.0944rad)
  sketch-geometry (12):
    g0: ArcOfCircle CenterX=38.86 CenterY=13.65 CenterZ=0 NormalX=0 NormalY=0 NormalZ=1 AngleXU=0 Radius=3.25 StartAngle=0.394791 EndAngle=2.7468
    g1: LineSegment StartX=35.05 StartY=11.9 StartZ=0 EndX=35.05 EndY=10.4 EndZ=0
    g2: LineSegment StartX=35.05 StartY=10.4 StartZ=0 EndX=37.2628 EndY=10.4 EndZ=0
    g3: LineSegment StartX=37.2628 StartY=10.4 StartZ=0 EndX=37.2628 EndY=13.7453 EndZ=0
    g4: LineSegment StartX=40.4594 StartY=13.6056 StartZ=0 EndX=40.4594 EndY=10.4 EndZ=0
    g5: LineSegment StartX=40.4594 StartY=10.4 StartZ=0 EndX=41.45 EndY=10.4 EndZ=0
    g6: LineSegment StartX=41.45 StartY=10.4 StartZ=0 EndX=41.45 EndY=8 EndZ=0
    g7: ArcOfCircle CenterX=38.86 CenterY=13.65 CenterZ=0 NormalX=0 NormalY=0 NormalZ=1 AngleXU=0 Radius=1.6 StartAngle=6.2554 EndAngle=9.36517
    g8: LineSegment StartX=35.05 StartY=11.9 StartZ=0 EndX=35.86 EndY=14.9 EndZ=0
    g9: LineSegment StartX=41.86 StartY=14.9 StartZ=0 EndX=42.95 EndY=11.9 EndZ=0
    g10: LineSegment StartX=42.95 StartY=11.9 StartZ=0 EndX=42.95 EndY=8 EndZ=0
    g11: LineSegment StartX=42.95 StartY=8 StartZ=0 EndX=41.45 EndY=8 EndZ=0
  constraints (26):
    c: Coincident(g1,g-12)
    c: Coincident(g2,g1)
    c: Coincident(g2,g-12)
    c: Coincident(g3,g2)
    c: Coincident(g4,g-3)
    c: Coincident(g4,g-8)
    c: Coincident(g5,g4)
    c: Coincident(g5,g-9)
    c: Coincident(g6,g5)
    c: Coincident(g6,g-9)
    c: Coincident(g3,g-11)
    c: Coincident(g7,g3)
    c: Coincident(g7,g4)
    c: Coincident(g7,g0)
    c: Coincident(g8,g1)
    c: Coincident(g8,g0)
    c: Coincident(g1,g-7)
    c: Coincident(g0,g-7)
    c: Coincident(g9,g-10)
    c: Coincident(g0,g-5)
    c: Coincident(g9,g0)
    c: Coincident(g10,g9)
    c: PointOnObject(g10,g-13)
    c: Vertical(g10)
    c: Coincident(g11,g10)
    c: Coincident(g11,g6)
FEATURE [PartDesign::Pad] Pad090
  BaseFeature = -> Pocket049
  Direction = (1,0,0)
  Length = 0.05
  Length2 = 10
  Profile = -> Sketch120
  ReferenceAxis = -> Sketch120 [N_Axis]
  Refine = true
  Suppressed = false
  Type = 0
FEATURE [Sketcher::SketchObject] Sketch121
  ArcFitTolerance = 1e-06
  AttachmentSupport = -> [Pad090]
  ExternalGeometry = -> [Pad090]
  FullyConstrained = true
  MakeInternals = false
  MapMode = 5
  Placement = pos=(22.28,0,0) rot=(0.57735,-0.57735,-0.57735;2.0944rad)
  sketch-geometry (12):
    g0: ArcOfCircle CenterX=-38.86 CenterY=13.65 CenterZ=0 NormalX=0 NormalY=0 NormalZ=1 AngleXU=0 Radius=1.6 StartAngle=0.0596113 EndAngle=3.16938
    g1: ArcOfCircle CenterX=-38.86 CenterY=13.65 CenterZ=0 NormalX=0 NormalY=0 NormalZ=1 AngleXU=0 Radius=3.25 StartAngle=0.394791 EndAngle=2.7468
    g2: LineSegment StartX=-41.86 StartY=14.9 StartZ=0 EndX=-42.95 EndY=11.9 EndZ=0
    g3: LineSegment StartX=-42.95 StartY=11.9 StartZ=0 EndX=-42.95 EndY=8 EndZ=0
    g4: LineSegment StartX=-42.95 StartY=8 StartZ=0 EndX=-41.45 EndY=8 EndZ=0
    g5: LineSegment StartX=-41.45 StartY=8 StartZ=0 EndX=-41.45 EndY=10.4 EndZ=0
    g6: LineSegment StartX=-41.45 StartY=10.4 StartZ=0 EndX=-40.4594 EndY=10.4 EndZ=0
    g7: LineSegment StartX=-40.4594 StartY=10.4 StartZ=0 EndX=-40.4594 EndY=13.6056 EndZ=0
    g8: LineSegment StartX=-37.2628 StartY=13.7453 StartZ=0 EndX=-37.2628 EndY=10.4 EndZ=0
    g9: LineSegment StartX=-37.2628 StartY=10.4 StartZ=0 EndX=-35.05 EndY=10.4 EndZ=0
    g10: LineSegment StartX=-35.05 StartY=10.4 StartZ=0 EndX=-35.05 EndY=11.9 EndZ=0
    g11: LineSegment StartX=-35.05 StartY=11.9 StartZ=0 EndX=-35.86 EndY=14.9 EndZ=0
  constraints (24):
    c: Tangent(g0,g-5) = -1.5708
    c: Coincident(g0,g-6)
    c: Tangent(g1,g-4) = -1.5708
    c: Coincident(g1,g-8)
    c: Coincident(g2,g-8)
    c: Coincident(g2,g-9)
    c: Coincident(g3,g2)
    c: Coincident(g3,g-10)
    c: Coincident(g4,g3)
    c: Coincident(g4,g-10)
    c: Coincident(g5,g4)
    c: Coincident(g5,g-12)
    c: Coincident(g6,g5)
    c: Coincident(g6,g-12)
    c: Coincident(g7,g6)
    c: Coincident(g7,g0)
    c: Coincident(g8,g0)
    c: Coincident(g8,g-7)
    c: Coincident(g9,g8)
    c: Coincident(g9,g-7)
    c: Coincident(g10,g9)
    c: Coincident(g10,g-3)
    c: Coincident(g11,g10)
    c: Coincident(g11,g1)
FEATURE [PartDesign::Pad] Pad091
  BaseFeature = -> Pad090
  Direction = (-1,0,0)
  Length = 0.05
  Length2 = 10
  Profile = -> Sketch121
  ReferenceAxis = -> Sketch121 [N_Axis]
  Refine = true
  Suppressed = false
  Type = 0
FEATURE [Sketcher::SketchObject] Sketch122
  ArcFitTolerance = 1e-06
  AttachmentSupport = -> [Pad091]
  ExternalGeometry = -> [Pad091]
  FullyConstrained = true
  MakeInternals = false
  MapMode = 5
  Placement = pos=(0,0,11.9) rot=(0,0,1;0rad)
  sketch-geometry (4):
    g0: LineSegment StartX=13.13 StartY=24.15 StartZ=0 EndX=13.13 EndY=22.15 EndZ=0
    g1: LineSegment StartX=13.13 StartY=22.15 StartZ=0 EndX=23.08 EndY=22.15 EndZ=0
    g2: LineSegment StartX=23.08 StartY=22.15 StartZ=0 EndX=23.08 EndY=24.15 EndZ=0
    g3: LineSegment StartX=23.08 StartY=24.15 StartZ=0 EndX=13.13 EndY=24.15 EndZ=0
  constraints (13):
    c: Coincident(g0,g1)
    c: Coincident(g1,g2)
    c: Coincident(g2,g3)
    c: Coincident(g3,g0)
    c: Vertical(g0)
    c: Vertical(g2)
    c: Horizontal(g1)
    c: Horizontal(g3)
    c: DistanceY(g-3,g1) = 1
    c: DistanceY(g2,g2) = 2
    c: DistanceX(g0,g2) = 9.95
    c: DistanceX(g-5,g0) = 2.2
    c: DistanceX(g2,g-4) = 2.2
FEATURE [PartDesign::Pad] Pad092
  BaseFeature = -> Pad091
  Direction = (0,0,1)
  Length = 8.3
  Length2 = 10
  Profile = -> Sketch122
  ReferenceAxis = -> Sketch122 [N_Axis]
  Refine = true
  Suppressed = false
  Type = 0
FEATURE [Sketcher::SketchObject] Sketch123
  ArcFitTolerance = 1e-06
  AttachmentSupport = -> [Pad092]
  ExternalGeometry = -> [Pad092]
  FullyConstrained = true
  MakeInternals = false
  MapMode = 5
  Placement = pos=(0,0,20.2) rot=(0,0,1;0rad)
  sketch-geometry (8):
    g0: LineSegment StartX=13.13 StartY=24.15 StartZ=0 EndX=13.13 EndY=22.15 EndZ=0
    g1: LineSegment StartX=13.13 StartY=22.15 StartZ=0 EndX=14.63 EndY=22.15 EndZ=0
    g2: LineSegment StartX=14.63 StartY=22.15 StartZ=0 EndX=14.63 EndY=24.15 EndZ=0
    g3: LineSegment StartX=14.63 StartY=24.15 StartZ=0 EndX=13.13 EndY=24.15 EndZ=0
    g4: LineSegment StartX=23.08 StartY=24.15 StartZ=0 EndX=21.58 EndY=24.15 EndZ=0
    g5: LineSegment StartX=21.58 StartY=24.15 StartZ=0 EndX=21.58 EndY=22.15 EndZ=0
    g6: LineSegment StartX=21.58 StartY=22.15 StartZ=0 EndX=23.08 EndY=22.15 EndZ=0
    g7: LineSegment StartX=23.08 StartY=22.15 StartZ=0 EndX=23.08 EndY=24.15 EndZ=0
  constraints (22):
    c: Coincident(g0,g1)
    c: Coincident(g1,g2)
    c: Coincident(g2,g3)
    c: Coincident(g3,g0)
    c: Vertical(g0)
    c: Vertical(g2)
    c: Horizontal(g1)
    c: Horizontal(g3)
    c: Coincident(g0,g-6)
    c: PointOnObject(g1,g-5)
    c: Coincident(g4,g5)
    c: Coincident(g5,g6)
    c: Coincident(g6,g7)
    c: Coincident(g7,g4)
    c: Horizontal(g4)
    c: Horizontal(g6)
    c: Vertical(g5)
    c: Vertical(g7)
    c: Coincident(g4,g-4)
    c: PointOnObject(g5,g-5)
    c: DistanceX(g4,g4) = 1.5
    c: DistanceX(g3,g3) = 1.5
FEATURE [PartDesign::Pad] Pad093
  BaseFeature = -> Pad092
  Direction = (0,0,1)
  Length = 2
  Length2 = 10
  Profile = -> Sketch123
  ReferenceAxis = -> Sketch123 [N_Axis]
  Refine = true
  Suppressed = false
  Type = 0
FEATURE [Sketcher::SketchObject] Sketch124
  ArcFitTolerance = 1e-06
  AttachmentSupport = -> [Pad093]
  ExternalGeometry = -> [Pad093]
  FullyConstrained = true
  MakeInternals = false
  MapMode = 5
  Placement = pos=(9e-16,0,0) rot=(0.57735,-0.57735,-0.57735;2.0944rad)
  sketch-geometry (11):
    g0: LineSegment StartX=-27.35 StartY=22.2 StartZ=0 EndX=-21.3014 EndY=22.2 EndZ=0
    g1: LineSegment StartX=-21.3014 StartY=22.2 StartZ=0 EndX=-18.0241 EndY=11.9 EndZ=0
    g2: LineSegment StartX=-18.0241 StartY=11.9 StartZ=0 EndX=-18.0241 EndY=4.5 EndZ=0
    g3: LineSegment StartX=-18.0241 StartY=4.5 StartZ=0 EndX=-27.35 EndY=4.5 EndZ=0
    g4: LineSegment StartX=-27.35 StartY=4.5 StartZ=0 EndX=-27.35 EndY=22.2 EndZ=0
    g5: LineSegment StartX=-21.1551 StartY=22.4 StartZ=0 EndX=-27.55 EndY=22.4 EndZ=0
    g6: LineSegment StartX=-27.55 StartY=22.4 StartZ=0 EndX=-27.55 EndY=4.3 EndZ=0
    g7: LineSegment StartX=-27.55 StartY=4.3 StartZ=0 EndX=-17.8241 EndY=4.3 EndZ=0
    g8: LineSegment StartX=-17.8241 StartY=4.3 StartZ=0 EndX=-17.8241 EndY=11.9311 EndZ=0
    g9: LineSegment StartX=-17.8241 StartY=11.9311 StartZ=0 EndX=-21.1551 EndY=22.4 EndZ=0
    g10: LineSegment [constr] StartX=-20.3918 StartY=19.3412 StartZ=0 EndX=-20.2012 EndY=19.4019 EndZ=0
  constraints (34):
    c: Horizontal(g0)
    c: Coincident(g1,g0)
    c: Coincident(g2,g1)
    c: Vertical(g2)
    c: Coincident(g3,g2)
    c: Horizontal(g3)
    c: Coincident(g4,g3)
    c: Coincident(g4,g0)
    c: Vertical(g4)
    c: Horizontal(g5)
    c: Coincident(g6,g5)
    c: Vertical(g6)
    c: Coincident(g7,g6)
    c: Horizontal(g7)
    c: Coincident(g8,g7)
    c: Vertical(g8)
    c: Coincident(g9,g8)
    c: Coincident(g9,g5)
    c: DistanceX(g5,g0) = 0.2
    c: DistanceX(g2,g7) = 0.2
    c: DistanceY(g7,g2) = 0.2
    c: Parallel(g1,g9)
    c: PointOnObject(g10,g1)
    c: PointOnObject(g10,g9)
    c: Angle(g1,g10) = 1.5708
    c: Distance(g0,g10) = 3
    c: DistanceY(g0,g5) = 0.2
    c: DistanceX(g0,g-4) = 0.8
    c: DistanceY(g-10,g0) = 0.8
    c: DistanceX(g-10,g1) = 0.8
    c: DistanceY(g-12,g7) = 0.8
    c: Distance(g10) = 0.2
    c: DistanceY(g-10,g1) = 0
    c: Parallel(g1,g-10)
FEATURE [PartDesign::Pocket] Pocket050
  BaseFeature = -> Pad093
  Direction = (1,0,0)
  Length = 0.5
  Length2 = 5
  Profile = -> Sketch124
  ReferenceAxis = -> Sketch124 [N_Axis]
  Refine = true
  Suppressed = false
  Type = 0
FEATURE [Sketcher::SketchObject] Sketch125
  ArcFitTolerance = 1e-06
  AttachmentSupport = -> [Pocket050]
  ExternalGeometry = -> [Pocket050]
  FullyConstrained = true
  MakeInternals = false
  MapMode = 5
  Placement = pos=(9e-16,0,0) rot=(0.57735,-0.57735,-0.57735;2.0944rad)
  sketch-geometry (12):
    g0: LineSegment StartX=-31.65 StartY=11.4 StartZ=0 EndX=-31.65 EndY=10.4 EndZ=0
    g1: LineSegment StartX=-31.15 StartY=9.9 StartZ=0 EndX=-29.15 EndY=9.9 EndZ=0
    g2: LineSegment StartX=-28.65 StartY=10.4 StartZ=0 EndX=-28.65 EndY=11.4 EndZ=0
    g3: LineSegment StartX=-29.15 StartY=11.9 StartZ=0 EndX=-31.15 EndY=11.9 EndZ=0
    g4: ArcOfCircle CenterX=-31.15 CenterY=11.4 CenterZ=0 NormalX=0 NormalY=0 NormalZ=1 AngleXU=0 Radius=0.5 StartAngle=1.5708 EndAngle=3.14159
    g5: GeomPoint [constr] X=-31.65 Y=11.9 Z=0
    g6: ArcOfCircle CenterX=-29.15 CenterY=11.4 CenterZ=0 NormalX=0 NormalY=0 NormalZ=1 AngleXU=0 Radius=0.5 StartAngle=1e-15 EndAngle=1.5708
    g7: GeomPoint [constr] X=-28.65 Y=11.9 Z=0
    g8: ArcOfCircle CenterX=-29.15 CenterY=10.4 CenterZ=0 NormalX=0 NormalY=0 NormalZ=1 AngleXU=0 Radius=0.5 StartAngle=4.71239 EndAngle=6.28319
    g9: GeomPoint [constr] X=-28.65 Y=9.9 Z=0
    g10: ArcOfCircle CenterX=-31.15 CenterY=10.4 CenterZ=0 NormalX=0 NormalY=0 NormalZ=1 AngleXU=0 Radius=0.5 StartAngle=3.14159 EndAngle=4.71239
    g11: GeomPoint [constr] X=-31.65 Y=9.9 Z=0
  constraints (29):
    c: Vertical(g0)
    c: Vertical(g2)
    c: Horizontal(g1)
    c: Horizontal(g3)
    c: PointOnObject(g5,g0)
    c: PointOnObject(g5,g3)
    c: Tangent(g0,g4) = -1.5708
    c: Tangent(g3,g4) = -1.5708
    c: PointOnObject(g7,g2)
    c: PointOnObject(g7,g3)
    c: Tangent(g2,g6) = -1.5708
    c: Tangent(g3,g6) = -1.5708
    c: PointOnObject(g9,g1)
    c: PointOnObject(g9,g2)
    c: Tangent(g1,g8) = -1.5708
    c: Tangent(g2,g8) = -1.5708
    c: PointOnObject(g11,g0)
    c: PointOnObject(g11,g1)
    c: Tangent(g0,g10) = -1.5708
    c: Tangent(g1,g10) = -1.5708
    c: Radius(g4) = 0.5
    c: Radius(g6) = 0.5
    c: Radius(g8) = 0.5
    c: Radius(g10) = 0.5
    c: DistanceX(g0,g2) = 3
    c: DistanceY(g3,g-3) = 0
    c: DistanceY(g1,g3) = 2
    c: DistanceX(g-4,g-5) = 5.2
    c: DistanceX(g2,g-5) = 1.1
FEATURE [PartDesign::Pad] Pad094
  BaseFeature = -> Pocket050
  Direction = (-1,0,0)
  Length = 0.5
  Length2 = 10
  Profile = -> Sketch125
  ReferenceAxis = -> Sketch125 [N_Axis]
  Refine = true
  Suppressed = false
  Type = 0
FEATURE [PartDesign::Pocket] Pocket051
  BaseFeature = -> Pad094
  Direction = (0,1,0)
  Length = 0.5
  Length2 = 5
  Profile = -> Pad094 [Face71]
  Refine = true
  Suppressed = false
  Type = 0
FEATURE [Sketcher::SketchObject] Sketch126
  ArcFitTolerance = 1e-06
  AttachmentSupport = -> [Pocket051]
  ExternalGeometry = -> [Pocket051]
  FullyConstrained = true
  MakeInternals = false
  MapMode = 5
  Placement = pos=(3,0,0) rot=(0.57735,-0.57735,-0.57735;2.0944rad)
  sketch-geometry (12):
    g0: LineSegment StartX=-41.25 StartY=9.5 StartZ=0 EndX=-41.25 EndY=5.5 EndZ=0
    g1: LineSegment StartX=-40.75 StartY=5 StartZ=0 EndX=-34.75 EndY=5 EndZ=0
    g2: LineSegment StartX=-34.25 StartY=5.5 StartZ=0 EndX=-34.25 EndY=9.5 EndZ=0
    g3: LineSegment StartX=-34.75 StartY=10 StartZ=0 EndX=-40.75 EndY=10 EndZ=0
    g4: ArcOfCircle CenterX=-34.75 CenterY=5.5 CenterZ=0 NormalX=0 NormalY=0 NormalZ=1 AngleXU=0 Radius=0.5 StartAngle=4.71239 EndAngle=6.28319
    g5: GeomPoint [constr] X=-34.25 Y=5 Z=0
    g6: ArcOfCircle CenterX=-34.75 CenterY=9.5 CenterZ=0 NormalX=0 NormalY=0 NormalZ=1 AngleXU=0 Radius=0.5 StartAngle=0 EndAngle=1.5708
    g7: GeomPoint [constr] X=-34.25 Y=10 Z=0
    g8: ArcOfCircle CenterX=-40.75 CenterY=9.5 CenterZ=0 NormalX=0 NormalY=0 NormalZ=1 AngleXU=0 Radius=0.5 StartAngle=1.5708 EndAngle=3.14159
    g9: GeomPoint [constr] X=-41.25 Y=10 Z=0
    g10: ArcOfCircle CenterX=-40.75 CenterY=5.5 CenterZ=0 NormalX=0 NormalY=0 NormalZ=1 AngleXU=0 Radius=0.5 StartAngle=3.14159 EndAngle=4.71239
    g11: GeomPoint [constr] X=-41.25 Y=5 Z=0
  constraints (28):
    c: Vertical(g0)
    c: Vertical(g2)
    c: Horizontal(g1)
    c: Horizontal(g3)
    c: PointOnObject(g5,g1)
    c: PointOnObject(g5,g2)
    c: Tangent(g1,g4) = -1.5708
    c: Tangent(g2,g4) = -1.5708
    c: PointOnObject(g7,g2)
    c: PointOnObject(g7,g3)
    c: Tangent(g2,g6) = -1.5708
    c: Tangent(g3,g6) = -1.5708
    c: PointOnObject(g9,g0)
    c: PointOnObject(g9,g3)
    c: Tangent(g0,g8) = -1.5708
    c: Tangent(g3,g8) = -1.5708
    c: PointOnObject(g11,g0)
    c: PointOnObject(g11,g1)
    c: Tangent(g0,g10) = -1.5708
    c: Tangent(g1,g10) = -1.5708
    c: Radius(g10) = 0.5
    c: Radius(g8) = 0.5
    c: Radius(g6) = 0.5
    c: Radius(g4) = 0.5
    c: DistanceY(g1,g3) = 5
    c: DistanceX(g0,g2) = 7
    c: DistanceY(g-3,g1) = 1.5
    c: DistanceX(g-3,g0) = 3.5
FEATURE [PartDesign::Pad] Pad095
  BaseFeature = -> Pocket051
  Direction = (-1,0,0)
  Length = 0.5
  Length2 = 10
  Profile = -> Sketch126
  ReferenceAxis = -> Sketch126 [N_Axis]
  Refine = true
  Suppressed = false
  Type = 0
FEATURE [Sketcher::SketchObject] Sketch127
  ArcFitTolerance = 1e-06
  AttachmentSupport = -> [Pad095]
  ExternalGeometry = -> [Pad095]
  FullyConstrained = false
  MakeInternals = false
  MapMode = 5
  Placement = pos=(0,0,11.9) rot=(0,0,1;0rad)
  sketch-geometry (8):
    g0: LineSegment StartX=10 StartY=32.75 StartZ=0 EndX=10 EndY=24.15 EndZ=0
    g1: LineSegment StartX=10 StartY=24.15 StartZ=0 EndX=24.3151 EndY=24.15 EndZ=0
    g2: LineSegment StartX=25.28 StartY=25.1149 StartZ=0 EndX=25.28 EndY=31.6983 EndZ=0
    g3: LineSegment StartX=24.2283 StartY=32.75 StartZ=0 EndX=10 EndY=32.75 EndZ=0
    g4: ArcOfCircle CenterX=24.2283 CenterY=31.6983 CenterZ=0 NormalX=0 NormalY=0 NormalZ=1 AngleXU=0 Radius=1.05174 StartAngle=-1.8e-15 EndAngle=1.5708
    g5: GeomPoint [constr] X=25.28 Y=32.75 Z=0
    g6: ArcOfCircle CenterX=24.3151 CenterY=25.1149 CenterZ=0 NormalX=0 NormalY=0 NormalZ=1 AngleXU=0 Radius=0.964906 StartAngle=4.71239 EndAngle=6.28319
    g7: GeomPoint [constr] X=25.28 Y=24.15 Z=0
  constraints (18):
    c: Coincident(g0,g1)
    c: Coincident(g3,g0)
    c: Vertical(g0)
    c: Vertical(g2)
    c: Horizontal(g1)
    c: Horizontal(g3)
    c: DistanceX(g-11,g5) = 0
    c: PointOnObject(g5,g2)
    c: PointOnObject(g5,g3)
    c: Tangent(g2,g4) = -1.5708
    c: Tangent(g3,g4) = -1.5708
    c: PointOnObject(g7,g1)
    c: PointOnObject(g7,g2)
    c: Tangent(g1,g6) = -1.5708
    c: Tangent(g2,g6) = -1.5708
    c: PointOnObject(g0,g-10)
    c: PointOnObject(g0,g-9)
    c: PointOnObject(g3,g-8)
FEATURE [PartDesign::Pad] Pad096
  BaseFeature = -> Pad095
  Direction = (0,0,1)
  Length = 0.5
  Length2 = 10
  Profile = -> Sketch127
  ReferenceAxis = -> Sketch127 [N_Axis]
  Refine = true
  Suppressed = false
  Type = 0
FEATURE [Sketcher::SketchObject] Sketch128
  ArcFitTolerance = 1e-06
  AttachmentSupport = -> [Pad096]
  ExternalGeometry = -> [Pad096]
  FullyConstrained = true
  MakeInternals = false
  MapMode = 5
  Placement = pos=(0,0,11.9) rot=(0,0,1;0rad)
  sketch-geometry (36):
    g0: LineSegment StartX=4 StartY=41.45 StartZ=0 EndX=4 EndY=34.25 EndZ=0
    g1: LineSegment StartX=4.5 StartY=33.75 StartZ=0 EndX=9.43 EndY=33.75 EndZ=0
    g2: LineSegment StartX=9.93 StartY=34.25 StartZ=0 EndX=9.93 EndY=41.45 EndZ=0
    g3: LineSegment StartX=9.43 StartY=41.95 StartZ=0 EndX=4.5 EndY=41.95 EndZ=0
    g4: LineSegment StartX=25.98 StartY=41.45 StartZ=0 EndX=25.98 EndY=33.25 EndZ=0
    g5: LineSegment StartX=26.48 StartY=32.75 StartZ=0 EndX=31.5 EndY=32.75 EndZ=0
    g6: LineSegment StartX=32 StartY=33.25 StartZ=0 EndX=32 EndY=41.45 EndZ=0
    g7: LineSegment StartX=31.5 StartY=41.95 StartZ=0 EndX=26.48 EndY=41.95 EndZ=0
    g8: LineSegment StartX=25.98 StartY=29.95 StartZ=0 EndX=25.98 EndY=23.15 EndZ=0
    g9: LineSegment StartX=26.48 StartY=22.65 StartZ=0 EndX=31.5 EndY=22.65 EndZ=0
    g10: LineSegment StartX=32 StartY=23.15 StartZ=0 EndX=32 EndY=29.95 EndZ=0
    g11: LineSegment StartX=31.5 StartY=30.45 StartZ=0 EndX=26.48 EndY=30.45 EndZ=0
    g12: ArcOfCircle CenterX=9.43 CenterY=41.45 CenterZ=0 NormalX=0 NormalY=0 NormalZ=1 AngleXU=0 Radius=0.5 StartAngle=-6.2e-15 EndAngle=1.5708
    g13: GeomPoint [constr] X=9.93 Y=41.95 Z=0
    g14: ArcOfCircle CenterX=4.5 CenterY=41.45 CenterZ=0 NormalX=0 NormalY=0 NormalZ=1 AngleXU=0 Radius=0.5 StartAngle=1.5708 EndAngle=3.14159
    g15: GeomPoint [constr] X=4 Y=41.95 Z=0
    g16: ArcOfCircle CenterX=4.5 CenterY=34.25 CenterZ=0 NormalX=0 NormalY=0 NormalZ=1 AngleXU=0 Radius=0.5 StartAngle=3.14159 EndAngle=4.71239
    g17: GeomPoint [constr] X=4 Y=33.75 Z=0
    g18: ArcOfCircle CenterX=9.43 CenterY=34.25 CenterZ=0 NormalX=0 NormalY=0 NormalZ=1 AngleXU=0 Radius=0.5 StartAngle=4.71239 EndAngle=6.28319
    g19: GeomPoint [constr] X=9.93 Y=33.75 Z=0
    g20: ArcOfCircle CenterX=26.48 CenterY=33.25 CenterZ=0 NormalX=0 NormalY=0 NormalZ=1 AngleXU=0 Radius=0.5 StartAngle=3.14159 EndAngle=4.71239
    g21: GeomPoint [constr] X=25.98 Y=32.75 Z=0
    g22: ArcOfCircle CenterX=31.5 CenterY=33.25 CenterZ=0 NormalX=0 NormalY=0 NormalZ=1 AngleXU=0 Radius=0.5 StartAngle=4.71239 EndAngle=6.28319
    g23: GeomPoint [constr] X=32 Y=32.75 Z=0
    g24: ArcOfCircle CenterX=31.5 CenterY=41.45 CenterZ=0 NormalX=0 NormalY=0 NormalZ=1 AngleXU=0 Radius=0.5 StartAngle=5.4e-15 EndAngle=1.5708
    g25: GeomPoint [constr] X=32 Y=41.95 Z=0
    g26: ArcOfCircle CenterX=26.48 CenterY=41.45 CenterZ=0 NormalX=0 NormalY=0 NormalZ=1 AngleXU=0 Radius=0.5 StartAngle=1.5708 EndAngle=3.14159
    g27: GeomPoint [constr] X=25.98 Y=41.95 Z=0
    g28: ArcOfCircle CenterX=26.48 CenterY=29.95 CenterZ=0 NormalX=0 NormalY=0 NormalZ=1 AngleXU=0 Radius=0.5 StartAngle=1.5708 EndAngle=3.14159
    g29: GeomPoint [constr] X=25.98 Y=30.45 Z=0
    g30: ArcOfCircle CenterX=31.5 CenterY=29.95 CenterZ=0 NormalX=0 NormalY=0 NormalZ=1 AngleXU=0 Radius=0.5 StartAngle=-2.7e-15 EndAngle=1.5708
    g31: GeomPoint [constr] X=32 Y=30.45 Z=0
    g32: ArcOfCircle CenterX=31.5 CenterY=23.15 CenterZ=0 NormalX=0 NormalY=0 NormalZ=1 AngleXU=0 Radius=0.5 StartAngle=4.71239 EndAngle=6.28319
    g33: GeomPoint [constr] X=32 Y=22.65 Z=0
    g34: ArcOfCircle CenterX=26.48 CenterY=23.15 CenterZ=0 NormalX=0 NormalY=0 NormalZ=1 AngleXU=0 Radius=0.5 StartAngle=3.14159 EndAngle=4.71239
    g35: GeomPoint [constr] X=25.98 Y=22.65 Z=0
  constraints (84):
    c: Vertical(g0)
    c: Vertical(g2)
    c: Horizontal(g1)
    c: Horizontal(g3)
    c: Vertical(g4)
    c: Vertical(g6)
    c: Horizontal(g5)
    c: Horizontal(g7)
    c: Vertical(g8)
    c: Vertical(g10)
    c: Horizontal(g9)
    c: Horizontal(g11)
    c: PointOnObject(g13,g2)
    c: PointOnObject(g13,g3)
    c: Tangent(g2,g12) = -1.5708
    c: Tangent(g3,g12) = -1.5708
    c: PointOnObject(g15,g0)
    c: PointOnObject(g15,g3)
    c: Tangent(g0,g14) = -1.5708
    c: Tangent(g3,g14) = -1.5708
    c: PointOnObject(g17,g0)
    c: PointOnObject(g17,g1)
    c: Tangent(g0,g16) = -1.5708
    c: Tangent(g1,g16) = -1.5708
    c: PointOnObject(g19,g1)
    c: PointOnObject(g19,g2)
    c: Tangent(g1,g18) = -1.5708
    c: Tangent(g2,g18) = -1.5708
    c: PointOnObject(g21,g4)
    c: PointOnObject(g21,g5)
    c: Tangent(g4,g20) = -1.5708
    c: Tangent(g5,g20) = -1.5708
    c: PointOnObject(g23,g5)
    c: PointOnObject(g23,g6)
    c: Tangent(g5,g22) = -1.5708
    c: Tangent(g6,g22) = -1.5708
    c: PointOnObject(g25,g6)
    c: PointOnObject(g25,g7)
    c: Tangent(g6,g24) = -1.5708
    c: Tangent(g7,g24) = -1.5708
    c: PointOnObject(g27,g4)
    c: PointOnObject(g27,g7)
    c: Tangent(g4,g26) = -1.5708
    c: Tangent(g7,g26) = -1.5708
    c: PointOnObject(g29,g8)
    c: PointOnObject(g29,g11)
    c: Tangent(g8,g28) = -1.5708
    c: Tangent(g11,g28) = -1.5708
    c: PointOnObject(g31,g10)
    c: PointOnObject(g31,g11)
    c: Tangent(g10,g30) = -1.5708
    c: Tangent(g11,g30) = -1.5708
    c: PointOnObject(g33,g9)
    c: PointOnObject(g33,g10)
    c: Tangent(g9,g32) = -1.5708
    c: Tangent(g10,g32) = -1.5708
    c: PointOnObject(g35,g8)
    c: PointOnObject(g35,g9)
    c: Tangent(g8,g34) = -1.5708
    c: Tangent(g9,g34) = -1.5708
    c: Radius(g28) = 0.5
    c: Radius(g30) = 0.5
    c: Radius(g22) = 0.5
    c: Radius(g20) = 0.5
    c: Radius(g34) = 0.5
    c: Radius(g32) = 0.5
    c: Radius(g26) = 0.5
    c: Radius(g24) = 0.5
    c: Radius(g12) = 0.5
    c: Radius(g14) = 0.5
    c: Radius(g18) = 0.5
    c: Radius(g16) = 0.5
    c: DistanceY(g3,g-5) = 1
    c: DistanceY(g-5,g1) = 1
    c: DistanceX(g-5,g0) = 1
    c: DistanceX(g2,g-3) = 1
    c: DistanceX(g-7,g4) = 0.7
    c: DistanceX(g6,g-6) = 1
    c: DistanceY(g-10,g9) = 1.5
    c: DistanceX(g-8,g8) = 0.7
    c: DistanceX(g10,g-10) = 1
    c: DistanceY(g7,g-9) = 1
    c: DistanceY(g-11,g5) = 0
    c: DistanceY(g11,g5) = 2.3
FEATURE [PartDesign::Pad] Pad097
  BaseFeature = -> Pad096
  Direction = (0,0,1)
  Length = 0.5
  Length2 = 10
  Profile = -> Sketch128
  ReferenceAxis = -> Sketch128 [N_Axis]
  Refine = true
  Suppressed = false
  Type = 0
FEATURE [PartDesign::Fillet] Fillet004
  Base = -> Pad097 [Edge267,Edge221,Edge162,Edge163,Edge164,Edge125,Edge54,Edge124,Edge209,Edge208,Edge167,Edge311,Edge57,Edge133,Edge127,Edge50,Edge49,Edge126,Edge48,Edge123,Edge56,Edge210,Edge212,Edge278,Edge166,Edge165,Edge268,Edge211]
  BaseFeature = -> Pad097
  Radius = 0.5
  Refine = true
  SupportTransform = false
  Suppressed = false
  UseAllEdges = false
FEATURE [PartDesign::Fillet] Fillet005
  Base = -> Fillet004 [Edge114,Edge381,Edge379,Edge380,Edge378,Edge392,Edge394,Edge393,Edge388]
  BaseFeature = -> Fillet004
  Radius = 0.2
  Refine = true
  SupportTransform = false
  Suppressed = false
  UseAllEdges = false
FEATURE [PartDesign::Body] Body008  label="Rear_Cab"
  AllowCompound = false
  Group = -> [Binder003,Sketch097,Pad068,Pad069,Sketch098,Pad070,Sketch099,Pad071,Sketch100,Pad072,Sketch101,Pad073,Sketch102,Pad074,Pocket042,Sketch103,Pad075,Sketch106,Pad077,Sketch107,Pocket044,Sketch108,Pad078,Sketch109,Pad079,Sketch110,Pad080,Pad081,Sketch111,Pad082,Pad083,Sketch112,Pad084,Sketch113,Pad085,Sketch114,Pad086,Sketch115,Pad087,Sketch116,Pocket046,Sketch117,Pad088,Pad089,Sketch118,Pocket047,+24 more]
  Origin = -> Origin008
  Tip = -> Fillet005
FEATURE [PartDesign::SubShapeBinder] Binder004
  BindCopyOnChange = 0
  BindMode = 2
  ClaimChildren = false
  Context = -> Body009 [Binder004.]
  Fuse = false
  MakeFace = true
  OffsetFill = false
  OffsetIntersection = false
  OffsetJoinType = 0
  OffsetOpenResult = false
  PartialLoad = false
  Refine = true
  Relative = true
  _Version = 2
FEATURE [Sketcher::SketchObject] Sketch129
  ArcFitTolerance = 1e-06
  AttachmentSupport = -> [Binder004]
  ExternalGeometry = -> [Binder004]
  FullyConstrained = true
  MakeInternals = false
  MapMode = 5
  Placement = pos=(8.5,0,0) rot=(0.57735,-0.57735,-0.57735;2.0944rad)
  sketch-geometry (6):
    g0: LineSegment StartX=-31.7 StartY=21.35 StartZ=0 EndX=-20.3093 EndY=21.35 EndZ=0
    g1: LineSegment StartX=-31.7 StartY=21.35 StartZ=0 EndX=-31.7 EndY=10.45 EndZ=0
    g2: LineSegment StartX=-17.3 StartY=10.45 StartZ=0 EndX=-31.7 EndY=10.45 EndZ=0
    g3: LineSegment StartX=-20.3093 StartY=21.35 StartZ=0 EndX=-17.3 EndY=11.8922 EndZ=0
    g4: LineSegment StartX=-17.3 StartY=11.8922 StartZ=0 EndX=-17.3 EndY=10.45 EndZ=0
    g5: LineSegment [constr] StartX=-19.6663 StartY=19.4941 StartZ=0 EndX=-19.714 EndY=19.479 EndZ=0
  constraints (19):
    c: Horizontal(g0)
    c: Coincident(g1,g0)
    c: Vertical(g1)
    c: Coincident(g2,g1)
    c: Horizontal(g2)
    c: Coincident(g3,g0)
    c: Coincident(g4,g3)
    c: Coincident(g4,g2)
    c: DistanceX(g-5,g1) = 0.05
    c: DistanceX(g3,g-7) = 0.05
    c: DistanceY(g-5,g1) = 0.05
    c: DistanceY(g0,g-4) = 0.05
    c: Vertical(g4)
    c: Parallel(g-6,g3)
    c: PointOnObject(g5,g-6)
    c: PointOnObject(g5,g3)
    c: Angle(g5,g-6) = 1.5708
    c: Distance(g5) = 0.05
    c: Distance(g5,g-6) = 2
FEATURE [PartDesign::Pad] Pad098
  Direction = (-1,0,0)
  Length = 1.5
  Length2 = 10
  Profile = -> Sketch129
  ReferenceAxis = -> Sketch129 [N_Axis]
  Refine = true
  Suppressed = false
  Type = 0
FEATURE [Sketcher::SketchObject] Sketch130
  ArcFitTolerance = 1e-06
  AttachmentSupport = -> [Pad098]
  ExternalGeometry = -> [Pad098]
  FullyConstrained = true
  MakeInternals = false
  MapMode = 5
  Placement = pos=(7,0,0) rot=(0.57735,-0.57735,-0.57735;2.0944rad)
  sketch-geometry (11):
    g0: LineSegment StartX=-31.7 StartY=21.35 StartZ=0 EndX=-20.3093 EndY=21.35 EndZ=0
    g1: LineSegment StartX=-20.3093 StartY=21.35 StartZ=0 EndX=-17.3 EndY=11.8922 EndZ=0
    g2: LineSegment StartX=-17.3 StartY=11.8922 StartZ=0 EndX=-17.3 EndY=10.45 EndZ=0
    g3: LineSegment StartX=-17.3 StartY=10.45 StartZ=0 EndX=-18.8 EndY=10.45 EndZ=0
    g4: LineSegment StartX=-18.8 StartY=10.45 StartZ=0 EndX=-18.8 EndY=11.6594 EndZ=0
    g5: LineSegment StartX=-18.8 StartY=11.6594 StartZ=0 EndX=-21.4061 EndY=19.85 EndZ=0
    g6: LineSegment StartX=-21.4061 StartY=19.85 StartZ=0 EndX=-30.2 EndY=19.85 EndZ=0
    g7: LineSegment StartX=-30.2 StartY=19.85 StartZ=0 EndX=-30.2 EndY=10.45 EndZ=0
    g8: LineSegment StartX=-30.2 StartY=10.45 StartZ=0 EndX=-31.7 EndY=10.45 EndZ=0
    g9: LineSegment StartX=-31.7 StartY=21.35 StartZ=0 EndX=-31.7 EndY=10.45 EndZ=0
    g10: LineSegment [constr] StartX=-19.0671 StartY=17.446 StartZ=0 EndX=-20.4965 EndY=16.9912 EndZ=0
  constraints (29):
    c: Coincident(g0,g-6)
    c: Coincident(g0,g-5)
    c: Coincident(g1,g0)
    c: Coincident(g1,g-3)
    c: Coincident(g2,g1)
    c: Coincident(g2,g-7)
    c: Coincident(g3,g2)
    c: PointOnObject(g3,g-7)
    c: Coincident(g4,g3)
    c: Vertical(g4)
    c: Coincident(g5,g4)
    c: Coincident(g6,g5)
    c: Horizontal(g6)
    c: Coincident(g7,g6)
    c: PointOnObject(g7,g-7)
    c: Vertical(g7)
    c: Coincident(g8,g7)
    c: Coincident(g8,g-7)
    c: DistanceX(g8,g8) = 1.5
    c: DistanceX(g3,g3) = 1.5
    c: DistanceY(g6,g0) = 1.5
    c: Coincident(g9,g0)
    c: Coincident(g9,g8)
    c: Parallel(g1,g5)
    c: PointOnObject(g10,g1)
    c: PointOnObject(g10,g5)
    c: Angle(g10,g1) = 1.5708
    c: Distance(g10) = 1.5
    c: Distance(g10,g5) = 3
FEATURE [PartDesign::Pad] Pad099
  BaseFeature = -> Pad098
  Direction = (-1,0,0)
  Length = 5.4
  Length2 = 10
  Profile = -> Sketch130
  ReferenceAxis = -> Sketch130 [N_Axis]
  Refine = true
  Suppressed = false
  Type = 0
FEATURE [Sketcher::SketchObject] Sketch131
  ArcFitTolerance = 1e-06
  AttachmentSupport = -> [Pad099]
  ExternalGeometry = -> [Pad099]
  FullyConstrained = true
  MakeInternals = false
  MapMode = 5
  Placement = pos=(1.6,0,0) rot=(0.57735,-0.57735,-0.57735;2.0944rad)
  sketch-geometry (5):
    g0: LineSegment StartX=-30.2 StartY=19.85 StartZ=0 EndX=-30.2 EndY=10.45 EndZ=0
    g1: LineSegment StartX=-30.2 StartY=19.85 StartZ=0 EndX=-21.4061 EndY=19.85 EndZ=0
    g2: LineSegment StartX=-21.4061 StartY=19.85 StartZ=0 EndX=-18.8 EndY=11.6594 EndZ=0
    g3: LineSegment StartX=-18.8 StartY=11.6594 StartZ=0 EndX=-18.8 EndY=10.45 EndZ=0
    g4: LineSegment StartX=-18.8 StartY=10.45 StartZ=0 EndX=-30.2 EndY=10.45 EndZ=0
  constraints (10):
    c: Coincident(g0,g-7)
    c: Coincident(g0,g-7)
    c: Coincident(g1,g0)
    c: Coincident(g1,g-4)
    c: Coincident(g2,g1)
    c: Coincident(g2,g-6)
    c: Coincident(g3,g2)
    c: Coincident(g3,g-6)
    c: Coincident(g4,g3)
    c: Coincident(g4,g0)
FEATURE [PartDesign::Pad] Pad100
  BaseFeature = -> Pad099
  Direction = (-1,0,0)
  Length = 1.5
  Length2 = 10
  Profile = -> Sketch131
  ReferenceAxis = -> Sketch131 [N_Axis]
  Refine = true
  Reversed = true
  Suppressed = false
  Type = 0
FEATURE [Sketcher::SketchObject] Sketch132
  ArcFitTolerance = 1e-06
  AttachmentSupport = -> [Pocket045]
  ExternalGeometry = -> [Pocket045]
  FullyConstrained = true
  MakeInternals = false
  MapMode = 5
  Placement = pos=(0,45.75,0) rot=(0,0.707107,0.707107;3.14159rad)
  sketch-geometry (3):
    g0: LineSegment StartX=-14.1 StartY=9.5 StartZ=0 EndX=-15.6 EndY=9.5 EndZ=0
    g1: LineSegment StartX=-15.6 StartY=9.5 StartZ=0 EndX=-14.1 EndY=8 EndZ=0
    g2: LineSegment StartX=-14.1 StartY=8 StartZ=0 EndX=-14.1 EndY=9.5 EndZ=0
  constraints (8):
    c: Coincident(g0,g-5)
    c: PointOnObject(g0,g-3)
    c: Coincident(g1,g0)
    c: PointOnObject(g1,g-5)
    c: Coincident(g2,g1)
    c: Coincident(g2,g0)
    c: DistanceX(g0,g0) = 1.5
    c: Angle(g1,g0) = 0.785398
FEATURE [PartDesign::Pocket] Pocket052
  BaseFeature = -> Pocket045
  Direction = (0,-1,2e-16)
  Length = 5
  Length2 = 5
  Profile = -> Sketch132
  ReferenceAxis = -> Sketch132 [N_Axis]
  Refine = true
  Suppressed = false
  Type = 0
FEATURE [PartDesign::Body] Body007  label="Swivel_Base"
  AllowCompound = false
  Group = -> [Binder002,Sketch080,Pad058,Sketch081,Pad059,Sketch082,Pad060,Sketch083,Pocket032,Sketch084,Pad061,Sketch085,Pocket033,Sketch086,Pad062,Sketch087,Pad063,Sketch088,Pad064,Sketch089,Pad065,Pocket034,Sketch090,Pocket035,Pad066,Sketch091,Pad067,Sketch092,Pocket036,Sketch093,Pocket037,Sketch094,Pocket038,Sketch096,Pocket041,Sketch104,Pocket043,Sketch105,Pad076,Fillet003,Pocket045,Sketch132,Pocket052]
  Origin = -> Origin007
  Tip = -> Pocket052
FEATURE [PartDesign::SubShapeBinder] Binder005
  BindCopyOnChange = 0
  BindMode = 2
  ClaimChildren = false
  Context = -> Body010 [Binder005.]
  Fuse = false
  MakeFace = true
  OffsetFill = false
  OffsetIntersection = false
  OffsetJoinType = 0
  OffsetOpenResult = false
  PartialLoad = false
  Refine = true
  Relative = true
  _Version = 2
FEATURE [Sketcher::SketchObject] Sketch133
  ArcFitTolerance = 1e-06
  AttachmentSupport = -> [Binder005]
  ExternalGeometry = -> [Binder005]
  FullyConstrained = true
  MakeInternals = false
  MapMode = 5
  Placement = pos=(0,0,-4) rot=(1,0,0;3.14159rad)
  sketch-geometry (22):
    g0: LineSegment StartX=7.05 StartY=0 StartZ=0 EndX=28.95 EndY=0 EndZ=0
    g1: LineSegment StartX=28.95 StartY=0 StartZ=0 EndX=28.95 EndY=-10 EndZ=0
    g2: LineSegment StartX=28.95 StartY=-10 StartZ=0 EndX=27 EndY=-10 EndZ=0
    g3: LineSegment StartX=27 StartY=-10 StartZ=0 EndX=27.4 EndY=-17.2 EndZ=0
    g4: LineSegment StartX=27.4 StartY=-17.2 StartZ=0 EndX=29 EndY=-17.2 EndZ=0
    g5: LineSegment StartX=29 StartY=-17.2 StartZ=0 EndX=29 EndY=-26.3 EndZ=0
    g6: LineSegment StartX=29 StartY=-26.3 StartZ=0 EndX=27 EndY=-26.3 EndZ=0
    g7: LineSegment StartX=27 StartY=-26.3 StartZ=0 EndX=27 EndY=-19.2 EndZ=0
    g8: LineSegment StartX=27 StartY=-19.2 StartZ=0 EndX=25 EndY=-19.2 EndZ=0
    g9: LineSegment StartX=25 StartY=-19.2 StartZ=0 EndX=25 EndY=-3 EndZ=0
    g10: LineSegment StartX=25 StartY=-3 StartZ=0 EndX=21.127 EndY=-2 EndZ=0
    g11: LineSegment StartX=21.127 StartY=-2 StartZ=0 EndX=14.873 EndY=-2 EndZ=0
    g12: LineSegment StartX=14.873 StartY=-2 StartZ=0 EndX=11 EndY=-3 EndZ=0
    g13: LineSegment StartX=11 StartY=-3 StartZ=0 EndX=11 EndY=-19.2 EndZ=0
    g14: LineSegment StartX=11 StartY=-19.2 StartZ=0 EndX=9 EndY=-19.2 EndZ=0
    g15: LineSegment StartX=9 StartY=-19.2 StartZ=0 EndX=9 EndY=-26.3 EndZ=0
    g16: LineSegment StartX=9 StartY=-26.3 StartZ=0 EndX=7 EndY=-26.3 EndZ=0
    g17: LineSegment StartX=7 StartY=-26.3 StartZ=0 EndX=7 EndY=-17.2 EndZ=0
    g18: LineSegment StartX=7 StartY=-17.2 StartZ=0 EndX=8.6 EndY=-17.2 EndZ=0
    g19: LineSegment StartX=8.6 StartY=-17.2 StartZ=0 EndX=9 EndY=-10 EndZ=0
    g20: LineSegment StartX=9 StartY=-10 StartZ=0 EndX=7.05 EndY=-10 EndZ=0
    g21: LineSegment StartX=7.05 StartY=-10 StartZ=0 EndX=7.05 EndY=0 EndZ=0
  constraints (62):
    c: PointOnObject(g0,g-5)
    c: PointOnObject(g0,g-5)
    c: Coincident(g1,g0)
    c: Vertical(g1)
    c: Coincident(g2,g1)
    c: Coincident(g3,g2)
    c: Coincident(g4,g3)
    c: Coincident(g5,g4)
    c: Coincident(g6,g5)
    c: Coincident(g7,g6)
    c: Vertical(g7)
    c: Coincident(g8,g7)
    c: Horizontal(g8)
    c: Coincident(g9,g8)
    c: Vertical(g9)
    c: Coincident(g10,g9)
    c: Coincident(g11,g10)
    c: Horizontal(g11)
    c: Coincident(g12,g11)
    c: Coincident(g13,g12)
    c: Coincident(g14,g13)
    c: Horizontal(g14)
    c: Coincident(g15,g14)
    c: Vertical(g15)
    c: Coincident(g16,g15)
    c: Coincident(g17,g16)
    c: Coincident(g18,g17)
    c: Horizontal(g18)
    c: Coincident(g19,g18)
    c: Coincident(g20,g19)
    c: Horizontal(g20)
    c: Coincident(g21,g20)
    c: Coincident(g21,g0)
    c: Vertical(g21)
    c: DistanceX(g-7,g0) = 0.05
    c: DistanceX(g0,g-5) = 0.05
    c: DistanceY(g11,g-7) = 2
    c: DistanceX(g9,g0) = 3.95
    c: DistanceX(g0,g12) = 3.95
    c: DistanceX(g20,g20) = 1.95
    c: DistanceX(g2,g2) = 1.95
    c: DistanceY(g12,g11) = 1
    c: DistanceY(g9,g10) = 1
    c: Distance(g12) = 4
    c: Distance(g10) = 4
    c: DistanceX(g18,g18) = 1.6
    c: PointOnObject(g17,g-6)
    c: PointOnObject(g4,g-3)
    c: Horizontal(g4)
    c: DistanceX(g4,g4) = 1.6
    c: DistanceY(g3,g2) = 7.2
    c: Horizontal(g2)
    c: DistanceY(g18,g19) = 7.2
    c: DistanceY(g21,g21) = 10
    c: DistanceY(g1,g1) = 10
    c: Coincident(g16,g-9)
    c: Coincident(g15,g-9)
    c: Coincident(g5,g-3)
    c: Coincident(g6,g-10)
    c: Vertical(g13)
    c: DistanceY(g13,g18) = 2
    c: DistanceY(g8,g3) = 2
FEATURE [PartDesign::Pad] Pad101
  Direction = (0,0,-1)
  Length = 2
  Length2 = 10
  Profile = -> Sketch133
  ReferenceAxis = -> Sketch133 [N_Axis]
  Refine = true
  Suppressed = false
  Type = 0
FEATURE [Sketcher::SketchObject] Sketch134
  ArcFitTolerance = 1e-06
  AttachmentSupport = -> [Pad101]
  ExternalGeometry = -> [Pad101]
  FullyConstrained = true
  MakeInternals = false
  MapMode = 5
  Placement = pos=(0,0,-6) rot=(1,0,0;3.14159rad)
  sketch-geometry (12):
    g0: LineSegment StartX=7.05 StartY=0 StartZ=0 EndX=28.95 EndY=0 EndZ=0
    g1: LineSegment StartX=28.95 StartY=0 StartZ=0 EndX=28.95 EndY=-10 EndZ=0
    g2: LineSegment StartX=28.95 StartY=-10 StartZ=0 EndX=27 EndY=-10 EndZ=0
    g3: LineSegment StartX=27 StartY=-10 StartZ=0 EndX=27.4 EndY=-17.2 EndZ=0
    g4: LineSegment StartX=27.4 StartY=-17.2 StartZ=0 EndX=29 EndY=-17.2 EndZ=0
    g5: LineSegment StartX=29 StartY=-17.2 StartZ=0 EndX=29 EndY=-19.2 EndZ=0
    g6: LineSegment StartX=29 StartY=-19.2 StartZ=0 EndX=7 EndY=-19.2 EndZ=0
    g7: LineSegment StartX=7 StartY=-19.2 StartZ=0 EndX=7 EndY=-17.2 EndZ=0
    g8: LineSegment StartX=7 StartY=-17.2 StartZ=0 EndX=8.6 EndY=-17.2 EndZ=0
    g9: LineSegment StartX=8.6 StartY=-17.2 StartZ=0 EndX=9 EndY=-10 EndZ=0
    g10: LineSegment StartX=9 StartY=-10 StartZ=0 EndX=7.05 EndY=-10 EndZ=0
    g11: LineSegment StartX=7.05 StartY=-10 StartZ=0 EndX=7.05 EndY=0 EndZ=0
  constraints (26):
    c: Coincident(g0,g-5)
    c: Coincident(g0,g-4)
    c: Coincident(g1,g0)
    c: Coincident(g1,g-3)
    c: Coincident(g2,g1)
    c: Coincident(g2,g-14)
    c: Coincident(g3,g2)
    c: Coincident(g3,g-14)
    c: Coincident(g4,g3)
    c: Coincident(g4,g-16)
    c: Coincident(g5,g4)
    c: PointOnObject(g5,g-16)
    c: Coincident(g6,g5)
    c: PointOnObject(g6,g-12)
    c: Horizontal(g6)
    c: PointOnObject(g-11,g6)
    c: Coincident(g7,g6)
    c: Coincident(g7,g-12)
    c: Coincident(g8,g7)
    c: Coincident(g8,g-7)
    c: Coincident(g9,g8)
    c: Coincident(g9,g-7)
    c: Coincident(g10,g9)
    c: Coincident(g10,g-6)
    c: Coincident(g11,g10)
    c: Coincident(g11,g0)
FEATURE [PartDesign::Pad] Pad102
  BaseFeature = -> Pad101
  Direction = (0,0,-1)
  Length = 2
  Length2 = 10
  Profile = -> Sketch134
  ReferenceAxis = -> Sketch134 [N_Axis]
  Refine = true
  Suppressed = false
  Type = 0
FEATURE [Sketcher::SketchObject] Sketch135
  ArcFitTolerance = 1e-06
  AttachmentSupport = -> [Pad102]
  ExternalGeometry = -> [Pad102]
  FullyConstrained = true
  MakeInternals = false
  MapMode = 5
  Placement = pos=(0,0,-8) rot=(1,0,0;3.14159rad)
  sketch-geometry (4):
    g0: LineSegment StartX=7 StartY=-19.2 StartZ=0 EndX=29 EndY=-19.2 EndZ=0
    g1: LineSegment StartX=29 StartY=-19.2 StartZ=0 EndX=29 EndY=-36.4 EndZ=0
    g2: LineSegment StartX=29 StartY=-36.4 StartZ=0 EndX=7 EndY=-36.4 EndZ=0
    g3: LineSegment StartX=7 StartY=-36.4 StartZ=0 EndX=7 EndY=-19.2 EndZ=0
  constraints (10):
    c: Coincident(g0,g-3)
    c: Coincident(g0,g-3)
    c: Coincident(g1,g0)
    c: Vertical(g1)
    c: Coincident(g2,g1)
    c: Horizontal(g2)
    c: Coincident(g3,g2)
    c: Coincident(g3,g0)
    c: Vertical(g3)
    c: DistanceY(g3,g3) = 17.2
FEATURE [PartDesign::Pad] Pad103
  BaseFeature = -> Pad102
  Direction = (0,0,-1)
  Length = 2
  Length2 = 10
  Profile = -> Pad102 [Face13,Face15]
  Refine = true
  Suppressed = false
  Type = 0
FEATURE [PartDesign::Pad] Pad104
  BaseFeature = -> Pad103
  Direction = (0,0,-1)
  Length = 2
  Length2 = 10
  Profile = -> Sketch135
  ReferenceAxis = -> Sketch135 [N_Axis]
  Refine = true
  Suppressed = false
  Type = 0
FEATURE [Sketcher::SketchObject] Sketch136
  ArcFitTolerance = 1e-06
  AttachmentSupport = -> [Pad104]
  ExternalGeometry = -> [Pad104]
  FullyConstrained = true
  MakeInternals = false
  MapMode = 5
  Placement = pos=(7,0,0) rot=(0.57735,-0.57735,-0.57735;2.0944rad)
  sketch-geometry (7):
    g0: LineSegment StartX=-36.4 StartY=-10 StartZ=0 EndX=-41.35 EndY=-7.14212 EndZ=0
    g1: LineSegment StartX=-41.35 StartY=-7.14212 StartZ=0 EndX=-41.35 EndY=-4 EndZ=0
    g2: LineSegment StartX=-41.35 StartY=-4 StartZ=0 EndX=-34.4 EndY=-4 EndZ=0
    g3: LineSegment StartX=-36.4 StartY=-8 StartZ=0 EndX=-36.4 EndY=-10 EndZ=0
    g4: LineSegment [constr] StartX=-36.4 StartY=-10 StartZ=0 EndX=-41.35 EndY=-10 EndZ=0
    g5: LineSegment StartX=-36.4 StartY=-8 StartZ=0 EndX=-34.4 EndY=-8 EndZ=0
    g6: LineSegment StartX=-34.4 StartY=-8 StartZ=0 EndX=-34.4 EndY=-4 EndZ=0
  constraints (19):
    c: Coincident(g0,g-4)
    c: Coincident(g1,g0)
    c: Vertical(g1)
    c: Coincident(g2,g1)
    c: Horizontal(g2)
    c: Coincident(g3,g0)
    c: Angle(g3,g0) = 1.0472
    c: Coincident(g4,g0)
    c: Horizontal(g4)
    c: DistanceX(g4,g4) = 4.95
    c: DistanceX(g4,g0) = 0
    c: Coincident(g5,g3)
    c: PointOnObject(g5,g-3)
    c: Coincident(g6,g5)
    c: Vertical(g6)
    c: Coincident(g2,g6)
    c: DistanceY(g6,g6) = 4
    c: DistanceX(g2,g2) = 6.95
    c: Coincident(g3,g-4)
FEATURE [PartDesign::Pad] Pad105
  BaseFeature = -> Pad104
  Direction = (-1,0,0)
  Length = 22
  Length2 = 10
  Profile = -> Sketch136
  ReferenceAxis = -> Sketch136 [N_Axis]
  Refine = true
  Reversed = true
  Suppressed = false
  Type = 0
FEATURE [Sketcher::SketchObject] Sketch137
  ArcFitTolerance = 1e-06
  AttachmentSupport = -> [Pad105]
  ExternalGeometry = -> [Pad105]
  FullyConstrained = true
  MakeInternals = false
  MapMode = 5
  Placement = pos=(0,0,-8) rot=(1,0,0;3.14159rad)
  sketch-geometry (4):
    g0: LineSegment StartX=23.25 StartY=-10 StartZ=0 EndX=23.25 EndY=8 EndZ=0
    g1: LineSegment StartX=23.25 StartY=8 StartZ=0 EndX=12.75 EndY=8 EndZ=0
    g2: LineSegment StartX=12.75 StartY=8 StartZ=0 EndX=12.75 EndY=-10 EndZ=0
    g3: LineSegment StartX=12.75 StartY=-10 StartZ=0 EndX=23.25 EndY=-10 EndZ=0
  constraints (13):
    c: Coincident(g0,g1)
    c: Coincident(g1,g2)
    c: Coincident(g2,g3)
    c: Coincident(g3,g0)
    c: Vertical(g0)
    c: Vertical(g2)
    c: Horizontal(g1)
    c: Horizontal(g3)
    c: DistanceX(g1,g1) = 10.5
    c: DistanceX(g-4,g-3) = 21.9
    c: DistanceX(g-4,g1) = 5.7
    c: DistanceY(g-5,g2) = 0
    c: DistanceY(g0,g0) = 18
FEATURE [PartDesign::Pad] Pad106
  BaseFeature = -> Pad105
  Direction = (0,0,-1)
  Length = 2
  Length2 = 10
  Profile = -> Sketch137
  ReferenceAxis = -> Sketch137 [N_Axis]
  Refine = true
  Suppressed = false
  Type = 0
FEATURE [Sketcher::SketchObject] Sketch138
  ArcFitTolerance = 1e-06
  AttachmentSupport = -> [Pad106]
  ExternalGeometry = -> [Pad106]
  FullyConstrained = true
  MakeInternals = false
  MapMode = 5
  Placement = pos=(0,0,-8) rot=(1,0,0;3.14159rad)
  sketch-geometry (8):
    g0: LineSegment StartX=28.95 StartY=0 StartZ=0 EndX=23.25 EndY=0 EndZ=0
    g1: LineSegment StartX=23.25 StartY=0 StartZ=0 EndX=23.25 EndY=-10 EndZ=0
    g2: LineSegment StartX=23.25 StartY=-10 StartZ=0 EndX=28.95 EndY=-10 EndZ=0
    g3: LineSegment StartX=28.95 StartY=-10 StartZ=0 EndX=28.95 EndY=0 EndZ=0
    g4: LineSegment StartX=7.05 StartY=0 StartZ=0 EndX=7.05 EndY=-10 EndZ=0
    g5: LineSegment StartX=7.05 StartY=-10 StartZ=0 EndX=12.75 EndY=-10 EndZ=0
    g6: LineSegment StartX=12.75 StartY=-10 StartZ=0 EndX=12.75 EndY=0 EndZ=0
    g7: LineSegment StartX=12.75 StartY=0 StartZ=0 EndX=7.05 EndY=0 EndZ=0
  constraints (20):
    c: Coincident(g0,g1)
    c: Coincident(g1,g2)
    c: Coincident(g2,g3)
    c: Coincident(g3,g0)
    c: Horizontal(g0)
    c: Horizontal(g2)
    c: Vertical(g1)
    c: Vertical(g3)
    c: Coincident(g0,g-9)
    c: Coincident(g1,g-10)
    c: Coincident(g4,g5)
    c: Coincident(g5,g6)
    c: Coincident(g6,g7)
    c: Coincident(g7,g4)
    c: Vertical(g4)
    c: Vertical(g6)
    c: Horizontal(g5)
    c: Horizontal(g7)
    c: Coincident(g4,g-5)
    c: Coincident(g5,g-3)
FEATURE [PartDesign::Pad] Pad107
  BaseFeature = -> Pad106
  Direction = (0,0,-1)
  Length = 1
  Length2 = 10
  Profile = -> Sketch138
  ReferenceAxis = -> Sketch138 [N_Axis]
  Refine = true
  Suppressed = false
  Type = 0
FEATURE [Sketcher::SketchObject] Sketch139
  ArcFitTolerance = 1e-06
  AttachmentSupport = -> [Pad107]
  ExternalGeometry = -> [Pad107]
  FullyConstrained = true
  MakeInternals = false
  MapMode = 5
  Placement = pos=(0,0,-10) rot=(1,0,0;3.14159rad)
  sketch-geometry (4):
    g0: LineSegment StartX=13.9 StartY=-36.4 StartZ=0 EndX=13.9 EndY=-41.35 EndZ=0
    g1: LineSegment StartX=13.9 StartY=-41.35 StartZ=0 EndX=22.1 EndY=-41.35 EndZ=0
    g2: LineSegment StartX=22.1 StartY=-41.35 StartZ=0 EndX=22.1 EndY=-36.4 EndZ=0
    g3: LineSegment StartX=22.1 StartY=-36.4 StartZ=0 EndX=13.9 EndY=-36.4 EndZ=0
  constraints (12):
    c: Coincident(g0,g1)
    c: Coincident(g1,g2)
    c: Coincident(g2,g3)
    c: Coincident(g3,g0)
    c: Vertical(g0)
    c: Vertical(g2)
    c: Horizontal(g1)
    c: Horizontal(g3)
    c: DistanceX(g3,g3) = 8.2
    c: PointOnObject(g0,g-3)
    c: PointOnObject(g0,g-4)
    c: DistanceX(g1,g-4) = 6.9
FEATURE [PartDesign::Pocket] Pocket053
  BaseFeature = -> Pad107
  Direction = (0,0,1)
  Length = 6
  Length2 = 5
  Profile = -> Sketch139
  ReferenceAxis = -> Sketch139 [N_Axis]
  Refine = true
  Suppressed = false
  Type = 0
FEATURE [Sketcher::SketchObject] Sketch140
  ArcFitTolerance = 1e-06
  AttachmentSupport = -> [Pocket053]
  ExternalGeometry = -> [Pocket053]
  FullyConstrained = true
  MakeInternals = false
  MapMode = 5
  Placement = pos=(0,0,-4) rot=(0,0,1;0rad)
  sketch-geometry (4):
    g0: LineSegment StartX=13.9 StartY=36.4 StartZ=0 EndX=13.9 EndY=34.4 EndZ=0
    g1: LineSegment StartX=13.9 StartY=34.4 StartZ=0 EndX=22.1 EndY=34.4 EndZ=0
    g2: LineSegment StartX=22.1 StartY=34.4 StartZ=0 EndX=22.1 EndY=36.4 EndZ=0
    g3: LineSegment StartX=22.1 StartY=36.4 StartZ=0 EndX=13.9 EndY=36.4 EndZ=0
  constraints (10):
    c: Coincident(g0,g1)
    c: Coincident(g1,g2)
    c: Coincident(g2,g3)
    c: Coincident(g3,g0)
    c: Vertical(g0)
    c: Vertical(g2)
    c: Horizontal(g1)
    c: Coincident(g0,g-3)
    c: PointOnObject(g1,g-4)
    c: Coincident(g2,g-3)
FEATURE [PartDesign::Pocket] Pocket054
  BaseFeature = -> Pocket053
  Direction = (0,0,-1)
  Length = 4
  Length2 = 5
  Profile = -> Sketch140
  ReferenceAxis = -> Sketch140 [N_Axis]
  Refine = true
  Suppressed = false
  Type = 0
FEATURE [Sketcher::SketchObject] Sketch141
  ArcFitTolerance = 1e-06
  AttachmentSupport = -> [Pocket054]
  ExternalGeometry = -> [Pocket054]
  FullyConstrained = true
  MakeInternals = false
  MapMode = 5
  Placement = pos=(22.1,0,0) rot=(0.57735,-0.57735,-0.57735;2.0944rad)
  sketch-geometry (5):
    g0: LineSegment StartX=-34.4 StartY=-4 StartZ=0 EndX=-39.35 EndY=-4 EndZ=0
    g1: LineSegment StartX=-34.4 StartY=-4 StartZ=0 EndX=-34.4 EndY=-8 EndZ=0
    g2: LineSegment StartX=-34.4 StartY=-8 StartZ=0 EndX=-36.4 EndY=-8 EndZ=0
    g3: LineSegment StartX=-36.4 StartY=-8 StartZ=0 EndX=-39.35 EndY=-6.29682 EndZ=0
    g4: LineSegment StartX=-39.35 StartY=-6.29682 StartZ=0 EndX=-39.35 EndY=-4 EndZ=0
  constraints (13):
    c: Coincident(g0,g-4)
    c: PointOnObject(g0,g-3)
    c: PointOnObject(g1,g0)
    c: Coincident(g1,g-5)
    c: Vertical(g1)
    c: Coincident(g2,g1)
    c: Coincident(g2,g-5)
    c: Coincident(g3,g2)
    c: Coincident(g4,g3)
    c: Coincident(g4,g0)
    c: Parallel(g3,g-6)
    c: Vertical(g4)
    c: DistanceX(g-3,g0) = 2
FEATURE [PartDesign::Pocket] Pocket055
  BaseFeature = -> Pocket054
  Direction = (1,0,0)
  Length = 4.9
  Length2 = 5
  Profile = -> Sketch141
  ReferenceAxis = -> Sketch141 [N_Axis]
  Refine = true
  Suppressed = false
  Type = 0
FEATURE [Sketcher::SketchObject] Sketch142
  ArcFitTolerance = 1e-06
  AttachmentSupport = -> [Pocket055]
  ExternalGeometry = -> [Pocket055]
  FullyConstrained = true
  MakeInternals = false
  MapMode = 5
  Placement = pos=(13.9,0,0) rot=(0.57735,0.57735,0.57735;2.0944rad)
  sketch-geometry (5):
    g0: LineSegment StartX=36.4 StartY=-8 StartZ=0 EndX=34.4 EndY=-8 EndZ=0
    g1: LineSegment StartX=34.4 StartY=-8 StartZ=0 EndX=34.4 EndY=-4 EndZ=0
    g2: LineSegment StartX=34.4 StartY=-4 StartZ=0 EndX=39.35 EndY=-4 EndZ=0
    g3: LineSegment StartX=36.4 StartY=-8 StartZ=0 EndX=39.35 EndY=-6.29682 EndZ=0
    g4: LineSegment StartX=39.35 StartY=-6.29682 StartZ=0 EndX=39.35 EndY=-4 EndZ=0
  constraints (12):
    c: Coincident(g0,g-5)
    c: Coincident(g0,g-5)
    c: Coincident(g1,g0)
    c: Coincident(g1,g-4)
    c: Coincident(g2,g1)
    c: PointOnObject(g2,g-4)
    c: Coincident(g3,g0)
    c: Coincident(g4,g3)
    c: Coincident(g4,g2)
    c: Vertical(g4)
    c: Parallel(g-6,g3)
    c: DistanceX(g2,g-4) = 2
FEATURE [PartDesign::Pocket] Pocket056
  BaseFeature = -> Pocket055
  Direction = (-1,0,0)
  Length = 4.9
  Length2 = 5
  Profile = -> Sketch142
  ReferenceAxis = -> Sketch142 [N_Axis]
  Refine = true
  Suppressed = false
  Type = 0
FEATURE [PartDesign::Pad] Pad108
  BaseFeature = -> Pocket056
  Direction = (0,0,1)
  Length = 2
  Length2 = 10
  Profile = -> Pocket056 [Face4]
  Refine = true
  Suppressed = false
  Type = 0
FEATURE [Sketcher::SketchObject] Sketch143
  ArcFitTolerance = 1e-06
  AttachmentSupport = -> [Pad108]
  ExternalGeometry = -> [Pad108]
  FullyConstrained = true
  MakeInternals = false
  MapMode = 5
  Placement = pos=(12.75,0,0) rot=(0.57735,-0.57735,-0.57735;2.0944rad)
  sketch-geometry (4):
    g0: LineSegment StartX=6 StartY=-6 StartZ=0 EndX=4 EndY=-8 EndZ=0
    g1: LineSegment StartX=4 StartY=-8 StartZ=0 EndX=0 EndY=-8 EndZ=0
    g2: LineSegment StartX=0 StartY=-8 StartZ=0 EndX=0 EndY=-6 EndZ=0
    g3: LineSegment StartX=0 StartY=-6 StartZ=0 EndX=6 EndY=-6 EndZ=0
  constraints (11):
    c: PointOnObject(g0,g-4)
    c: Coincident(g1,g0)
    c: PointOnObject(g1,g-5)
    c: Horizontal(g1)
    c: Coincident(g2,g1)
    c: Coincident(g2,g-4)
    c: Coincident(g3,g2)
    c: DistanceX(g0,g-4) = 2
    c: DistanceY(g2,g2) = 2
    c: Angle(g3,g0) = 0.785398
    c: Coincident(g3,g0)
FEATURE [PartDesign::Pocket] Pocket057
  BaseFeature = -> Pad108
  Direction = (1,0,0)
  Length = 8.5
  Length2 = 5
  Profile = -> Sketch143
  ReferenceAxis = -> Sketch143 [N_Axis]
  Refine = true
  Suppressed = false
  Type = 0
FEATURE [Sketcher::SketchObject] Sketch144
  ArcFitTolerance = 1e-06
  AttachmentSupport = -> [Pocket057]
  ExternalGeometry = -> [Pocket057]
  FullyConstrained = true
  MakeInternals = false
  MapMode = 5
  Placement = pos=(12.75,0,0) rot=(0.57735,-0.57735,-0.57735;2.0944rad)
  sketch-geometry (4):
    g0: LineSegment StartX=6 StartY=-6 StartZ=0 EndX=4 EndY=-8 EndZ=0
    g1: LineSegment StartX=0 StartY=-6 StartZ=0 EndX=6 EndY=-6 EndZ=0
    g2: LineSegment StartX=4 StartY=-8 StartZ=0 EndX=0 EndY=-8 EndZ=0
    g3: LineSegment StartX=0 StartY=-8 StartZ=0 EndX=0 EndY=-6 EndZ=0
  constraints (8):
    c: Coincident(g0,g-3)
    c: Coincident(g0,g-4)
    c: Coincident(g2,g0)
    c: Coincident(g2,g-6)
    c: Coincident(g3,g2)
    c: Coincident(g3,g1)
    c: Coincident(g1,g-6)
    c: Coincident(g1,g0)
FEATURE [PartDesign::Pad] Pad109
  BaseFeature = -> Pocket057
  Direction = (-1,0,0)
  Length = 2
  Length2 = 10
  Profile = -> Sketch144
  ReferenceAxis = -> Sketch144 [N_Axis]
  Refine = true
  Reversed = true
  Suppressed = false
  Type = 0
FEATURE [Sketcher::SketchObject] Sketch145
  ArcFitTolerance = 1e-06
  AttachmentSupport = -> [Pad109]
  ExternalGeometry = -> [Pad109]
  FullyConstrained = true
  MakeInternals = false
  MapMode = 5
  Placement = pos=(0,0,-8) rot=(0,0,1;0rad)
  sketch-geometry (16):
    g0: LineSegment StartX=7 StartY=34.4 StartZ=0 EndX=7 EndY=32.4 EndZ=0
    g1: LineSegment StartX=7 StartY=32.4 StartZ=0 EndX=16.5 EndY=32.4 EndZ=0
    g2: LineSegment StartX=16.5 StartY=32.4 StartZ=0 EndX=16.5 EndY=34.4 EndZ=0
    g3: LineSegment StartX=16.5 StartY=34.4 StartZ=0 EndX=7 EndY=34.4 EndZ=0
    g4: LineSegment StartX=29 StartY=34.4 StartZ=0 EndX=19.5 EndY=34.4 EndZ=0
    g5: LineSegment StartX=19.5 StartY=34.4 StartZ=0 EndX=19.5 EndY=32.4 EndZ=0
    g6: LineSegment StartX=19.5 StartY=32.4 StartZ=0 EndX=29 EndY=32.4 EndZ=0
    g7: LineSegment StartX=29 StartY=32.4 StartZ=0 EndX=29 EndY=34.4 EndZ=0
    g8: LineSegment StartX=7 StartY=26.3 StartZ=0 EndX=16.5 EndY=26.3 EndZ=0
    g9: LineSegment StartX=16.5 StartY=26.3 StartZ=0 EndX=16.5 EndY=28.3 EndZ=0
    g10: LineSegment StartX=16.5 StartY=28.3 StartZ=0 EndX=7 EndY=28.3 EndZ=0
    g11: LineSegment StartX=7 StartY=28.3 StartZ=0 EndX=7 EndY=26.3 EndZ=0
    g12: LineSegment StartX=29 StartY=26.3 StartZ=0 EndX=29 EndY=28.3 EndZ=0
    g13: LineSegment StartX=29 StartY=28.3 StartZ=0 EndX=19.5 EndY=28.3 EndZ=0
    g14: LineSegment StartX=19.5 StartY=28.3 StartZ=0 EndX=19.5 EndY=26.3 EndZ=0
    g15: LineSegment StartX=19.5 StartY=26.3 StartZ=0 EndX=29 EndY=26.3 EndZ=0
  constraints (44):
    c: Coincident(g0,g1)
    c: Coincident(g1,g2)
    c: Coincident(g2,g3)
    c: Coincident(g3,g0)
    c: Vertical(g0)
    c: Vertical(g2)
    c: Horizontal(g1)
    c: Horizontal(g3)
    c: Coincident(g0,g-5)
    c: Coincident(g4,g5)
    c: Coincident(g5,g6)
    c: Coincident(g6,g7)
    c: Coincident(g7,g4)
    c: Horizontal(g4)
    c: Horizontal(g6)
    c: Vertical(g5)
    c: Vertical(g7)
    c: Coincident(g4,g-4)
    c: Coincident(g8,g9)
    c: Coincident(g9,g10)
    c: Coincident(g10,g11)
    c: Coincident(g11,g8)
    c: Horizontal(g8)
    c: Horizontal(g10)
    c: Vertical(g9)
    c: Vertical(g11)
    c: Coincident(g8,g-6)
    c: Coincident(g12,g13)
    c: Coincident(g13,g14)
    c: Coincident(g14,g15)
    c: Coincident(g15,g12)
    c: Vertical(g12)
    c: Vertical(g14)
    c: Horizontal(g13)
    c: Horizontal(g15)
    c: Coincident(g12,g-3)
    c: DistanceX(g1,g1) = 9.5
    c: DistanceX(g10,g10) = 9.5
    c: DistanceX(g13,g13) = 9.5
    c: DistanceX(g6,g6) = 9.5
    c: DistanceY(g5,g5) = 2
    c: DistanceY(g2,g2) = 2
    c: DistanceY(g9,g9) = 2
    c: DistanceY(g14,g14) = 2
FEATURE [PartDesign::Pad] Pad110
  BaseFeature = -> Pad109
  Direction = (0,0,1)
  Length = 0.7
  Length2 = 10
  Profile = -> Sketch145
  ReferenceAxis = -> Sketch145 [N_Axis]
  Refine = true
  Suppressed = false
  Type = 0
FEATURE [Sketcher::SketchObject] Sketch146
  ArcFitTolerance = 1e-06
  AttachmentSupport = -> [Pad110]
  ExternalGeometry = -> [Pad110]
  FullyConstrained = true
  MakeInternals = false
  MapMode = 5
  Placement = pos=(0,0,-8) rot=(0,0,1;0rad)
  sketch-geometry (1):
    g0: Circle CenterX=18 CenterY=20.4 CenterZ=0 NormalX=0 NormalY=0 NormalZ=1 AngleXU=0 Radius=3.5
  constraints (4):
    c: DistanceX(g-3,g-3) = 14
    c: DistanceX(g0,g-3) = 7
    c: Diameter(g0) = 7
    c: DistanceY(g0,g-6) = 16
FEATURE [PartDesign::Pad] Pad111
  BaseFeature = -> Pad110
  Direction = (0,0,1)
  Length = 3
  Length2 = 10
  Profile = -> Sketch146
  ReferenceAxis = -> Sketch146 [N_Axis]
  Refine = true
  Suppressed = false
  Type = 0
FEATURE [Sketcher::SketchObject] Sketch147
  ArcFitTolerance = 1e-06
  AttachmentSupport = -> [Pad111]
  ExternalGeometry = -> [Pad111]
  FullyConstrained = true
  MakeInternals = false
  MapMode = 5
  Placement = pos=(0,0,-5) rot=(0,0,1;0rad)
  sketch-geometry (1):
    g0: Circle CenterX=18 CenterY=20.4 CenterZ=0 NormalX=0 NormalY=0 NormalZ=1 AngleXU=0 Radius=2.5
  constraints (2):
    c: Coincident(g0,g-3)
    c: Radius(g0) = 2.5
FEATURE [PartDesign::Pocket] Pocket058
  BaseFeature = -> Pad111
  Direction = (0,0,-1)
  Length = 1.5
  Length2 = 5
  Profile = -> Sketch147
  ReferenceAxis = -> Sketch147 [N_Axis]
  Refine = true
  Suppressed = false
  Type = 0
FEATURE [Sketcher::SketchObject] Sketch148
  ArcFitTolerance = 1e-06
  AttachmentSupport = -> [Pocket058]
  ExternalGeometry = -> [Pocket058]
  FullyConstrained = true
  MakeInternals = false
  MapMode = 5
  Placement = pos=(0,0,-6.5) rot=(0,0,1;0rad)
  sketch-geometry (1):
    g0: Circle CenterX=18 CenterY=20.4 CenterZ=0 NormalX=0 NormalY=0 NormalZ=1 AngleXU=0 Radius=1
  constraints (2):
    c: Coincident(g0,g-3)
    c: Diameter(g0) = 2
FEATURE [PartDesign::Pocket] Pocket059
  BaseFeature = -> Pocket058
  Direction = (0,0,-1)
  Length = 5
  Length2 = 5
  Profile = -> Sketch148
  ReferenceAxis = -> Sketch148 [N_Axis]
  Refine = true
  Suppressed = false
  Type = 0
FEATURE [Sketcher::SketchObject] Sketch149
  ArcFitTolerance = 1e-06
  AttachmentSupport = -> [Pocket059]
  ExternalGeometry = -> [Pocket059]
  FullyConstrained = true
  MakeInternals = false
  MapMode = 5
  Placement = pos=(0,0,-8) rot=(0,0,1;0rad)
  sketch-geometry (8):
    g0: LineSegment StartX=27 StartY=20.2 StartZ=0 EndX=27 EndY=19.2 EndZ=0
    g1: LineSegment StartX=27 StartY=19.2 StartZ=0 EndX=21.2879 EndY=19.2 EndZ=0
    g2: LineSegment StartX=27 StartY=20.2 StartZ=0 EndX=21.4943 EndY=20.2 EndZ=0
    g3: ArcOfCircle CenterX=18 CenterY=20.4 CenterZ=0 NormalX=0 NormalY=0 NormalZ=1 AngleXU=0 Radius=3.49996 StartAngle=5.93323 EndAngle=6.22601
    g4: LineSegment StartX=9 StartY=19.2 StartZ=0 EndX=9 EndY=20.2 EndZ=0
    g5: LineSegment StartX=9 StartY=19.2 StartZ=0 EndX=14.7121 EndY=19.2 EndZ=0
    g6: LineSegment StartX=9 StartY=20.2 StartZ=0 EndX=14.5057 EndY=20.2 EndZ=0
    g7: ArcOfCircle CenterX=18 CenterY=20.4 CenterZ=0 NormalX=0 NormalY=0 NormalZ=1 AngleXU=0 Radius=3.49997 StartAngle=3.19877 EndAngle=3.49155
  constraints (22):
    c: PointOnObject(g0,g-8)
    c: Coincident(g0,g-8)
    c: Coincident(g1,g0)
    c: Coincident(g1,g-7)
    c: PointOnObject(g2,g-6)
    c: Coincident(g2,g0)
    c: DistanceY(g0,g0) = 1
    c: Horizontal(g2)
    c: Coincident(g3,g1)
    c: Coincident(g3,g2)
    c: Tangent(g3,g-6)
    c: Coincident(g4,g-5)
    c: PointOnObject(g4,g-5)
    c: Coincident(g5,g4)
    c: Coincident(g5,g-4)
    c: DistanceY(g4,g4) = 1
    c: Coincident(g6,g4)
    c: PointOnObject(g6,g-3)
    c: Horizontal(g6)
    c: Coincident(g7,g5)
    c: Coincident(g7,g6)
    c: Tangent(g7,g-3)
FEATURE [PartDesign::Pad] Pad112
  BaseFeature = -> Pocket059
  Direction = (0,0,1)
  Length = 2
  Length2 = 10
  Profile = -> Sketch149
  ReferenceAxis = -> Sketch149 [N_Axis]
  Refine = true
  Suppressed = false
  Type = 0
FEATURE [Sketcher::SketchObject] Sketch150
  ArcFitTolerance = 1e-06
  AttachmentSupport = -> [Pad112]
  ExternalGeometry = -> [Pad112]
  FullyConstrained = true
  MakeInternals = false
  MapMode = 5
  Placement = pos=(0,0,-6) rot=(0,0,1;0rad)
  sketch-geometry (1):
    g0: Circle CenterX=18 CenterY=4.95 CenterZ=0 NormalX=0 NormalY=0 NormalZ=1 AngleXU=0 Radius=2.4
  constraints (4):
    c: DistanceX(g-7,g-5) = 14
    c: DistanceX(g-7,g0) = 7
    c: Diameter(g0) = 4.8
    c: DistanceY(g-6,g0) = 2.95
FEATURE [PartDesign::Pad] Pad113
  BaseFeature = -> Pad112
  Direction = (0,0,1)
  Length = 4
  Length2 = 10
  Profile = -> Sketch150
  ReferenceAxis = -> Sketch150 [N_Axis]
  Refine = true
  Suppressed = false
  Type = 0
FEATURE [Sketcher::SketchObject] Sketch151
  ArcFitTolerance = 1e-06
  AttachmentSupport = -> [Pad113]
  ExternalGeometry = -> [Pad113]
  FullyConstrained = true
  MakeInternals = false
  MapMode = 5
  Placement = pos=(0,0,-2) rot=(0,0,1;0rad)
  sketch-geometry (1):
    g0: Circle CenterX=18 CenterY=4.95 CenterZ=0 NormalX=0 NormalY=0 NormalZ=1 AngleXU=0 Radius=0.75
  constraints (2):
    c: Coincident(g0,g-3)
    c: Radius(g0) = 0.75
FEATURE [PartDesign::Pocket] Pocket060
  BaseFeature = -> Pad113
  Direction = (0,0,-1)
  Length = 5
  Length2 = 5
  Profile = -> Sketch151
  ReferenceAxis = -> Sketch151 [N_Axis]
  Refine = true
  Suppressed = false
  Type = 0
FEATURE [Sketcher::SketchObject] Sketch152
  ArcFitTolerance = 1e-06
  AttachmentSupport = -> [Pocket060]
  ExternalGeometry = -> [Pocket060]
  FullyConstrained = true
  MakeInternals = false
  MapMode = 5
  Placement = pos=(0,0,-8) rot=(1,0,0;3.14159rad)
  sketch-geometry (4):
    g0: LineSegment StartX=7 StartY=-17.2 StartZ=0 EndX=7 EndY=-19.2 EndZ=0
    g1: LineSegment StartX=7 StartY=-19.2 StartZ=0 EndX=29 EndY=-19.2 EndZ=0
    g2: LineSegment StartX=29 StartY=-19.2 StartZ=0 EndX=29 EndY=-17.2 EndZ=0
    g3: LineSegment StartX=29 StartY=-17.2 StartZ=0 EndX=7 EndY=-17.2 EndZ=0
  constraints (10):
    c: Coincident(g0,g1)
    c: Coincident(g1,g2)
    c: Coincident(g2,g3)
    c: Coincident(g3,g0)
    c: Vertical(g0)
    c: Vertical(g2)
    c: Horizontal(g1)
    c: Horizontal(g3)
    c: Coincident(g0,g-4)
    c: Coincident(g1,g-3)
FEATURE [PartDesign::Pad] Pad114
  BaseFeature = -> Pocket060
  Direction = (0,0,-1)
  Length = 2
  Length2 = 10
  Profile = -> Sketch152
  ReferenceAxis = -> Sketch152 [N_Axis]
  Refine = true
  Suppressed = false
  Type = 0
FEATURE [Sketcher::SketchObject] Sketch153
  ArcFitTolerance = 1e-06
  AttachmentSupport = -> [Pad114]
  ExternalGeometry = -> [Pad114]
  FullyConstrained = true
  MakeInternals = false
  MapMode = 5
  Placement = pos=(0,0,-10) rot=(1,0,0;3.14159rad)
  sketch-geometry (1):
    g0: Circle CenterX=18 CenterY=-20.4 CenterZ=0 NormalX=0 NormalY=0 NormalZ=1 AngleXU=0 Radius=2.25
  constraints (2):
    c: Coincident(g0,g-3)
    c: Diameter(g0) = 4.5
FEATURE [PartDesign::Pocket] Pocket061
  BaseFeature = -> Pad114
  Direction = (0,0,1)
  Length = 2.3
  Length2 = 5
  Profile = -> Sketch153
  ReferenceAxis = -> Sketch153 [N_Axis]
  Refine = true
  Suppressed = false
  Type = 0
FEATURE [Sketcher::SketchObject] Sketch154
  ArcFitTolerance = 1e-06
  AttachmentSupport = -> [Pocket061]
  ExternalGeometry = -> [Pocket061]
  FullyConstrained = true
  MakeInternals = false
  MapMode = 5
  Placement = pos=(0,0,-10) rot=(1,0,0;3.14159rad)
  sketch-geometry (4):
    g0: LineSegment StartX=8.5 StartY=-23.4 StartZ=0 EndX=8.5 EndY=-34.4 EndZ=0
    g1: LineSegment StartX=8.5 StartY=-34.4 StartZ=0 EndX=27.5 EndY=-34.4 EndZ=0
    g2: LineSegment StartX=27.5 StartY=-34.4 StartZ=0 EndX=27.5 EndY=-23.4 EndZ=0
    g3: LineSegment StartX=27.5 StartY=-23.4 StartZ=0 EndX=8.5 EndY=-23.4 EndZ=0
  constraints (12):
    c: Coincident(g0,g1)
    c: Coincident(g1,g2)
    c: Coincident(g2,g3)
    c: Coincident(g3,g0)
    c: Vertical(g0)
    c: Vertical(g2)
    c: Horizontal(g1)
    c: Horizontal(g3)
    c: DistanceY(g-5,g1) = 2
    c: DistanceX(g-4,g0) = 1.5
    c: DistanceX(g1,g-3) = 1.5
    c: DistanceY(g0,g0) = 11
FEATURE [PartDesign::Pocket] Pocket062
  BaseFeature = -> Pocket061
  Direction = (0,0,1)
  Length = 0.5
  Length2 = 5
  Profile = -> Sketch154
  ReferenceAxis = -> Sketch154 [N_Axis]
  Refine = true
  Suppressed = false
  Type = 0
FEATURE [Sketcher::SketchObject] Sketch155
  ArcFitTolerance = 1e-06
  AttachmentSupport = -> [Pocket062]
  ExternalGeometry = -> [Pocket062]
  FullyConstrained = true
  MakeInternals = false
  MapMode = 5
  Placement = pos=(0,13.4301,-23.2617) rot=(1,0,0;3.66519rad)
  sketch-geometry (8):
    g0: LineSegment StartX=7.5 StartY=-27.0233 StartZ=0 EndX=7.5 EndY=-31.7391 EndZ=0
    g1: LineSegment StartX=7.5 StartY=-31.7391 StartZ=0 EndX=13.4 EndY=-31.7391 EndZ=0
    g2: LineSegment StartX=13.4 StartY=-31.7391 StartZ=0 EndX=13.4 EndY=-27.0233 EndZ=0
    g3: LineSegment StartX=13.4 StartY=-27.0233 StartZ=0 EndX=7.5 EndY=-27.0233 EndZ=0
    g4: LineSegment StartX=22.6 StartY=-27.0233 StartZ=0 EndX=22.6 EndY=-31.7391 EndZ=0
    g5: LineSegment StartX=22.6 StartY=-31.7391 StartZ=0 EndX=28.5 EndY=-31.7391 EndZ=0
    g6: LineSegment StartX=28.5 StartY=-31.7391 StartZ=0 EndX=28.5 EndY=-27.0233 EndZ=0
    g7: LineSegment StartX=28.5 StartY=-27.0233 StartZ=0 EndX=22.6 EndY=-27.0233 EndZ=0
  constraints (24):
    c: Coincident(g0,g1)
    c: Coincident(g1,g2)
    c: Coincident(g2,g3)
    c: Coincident(g3,g0)
    c: Vertical(g0)
    c: Vertical(g2)
    c: Horizontal(g1)
    c: Horizontal(g3)
    c: Coincident(g4,g5)
    c: Coincident(g5,g6)
    c: Coincident(g6,g7)
    c: Coincident(g7,g4)
    c: Vertical(g4)
    c: Vertical(g6)
    c: Horizontal(g5)
    c: Horizontal(g7)
    c: DistanceX(g-4,g0) = 0.5
    c: DistanceX(g2,g-3) = 0.5
    c: DistanceX(g-5,g4) = 0.5
    c: DistanceX(g6,g-6) = 0.5
    c: DistanceY(g2,g-3) = 0.5
    c: DistanceY(g-3,g1) = 0.5
    c: DistanceY(g-5,g4) = 0.5
    c: DistanceY(g6,g-6) = 0.5
FEATURE [PartDesign::Pocket] Pocket063
  BaseFeature = -> Pocket062
  Direction = (0,-0.5,0.866025)
  Length = 0.5
  Length2 = 5
  Profile = -> Sketch155
  ReferenceAxis = -> Sketch155 [N_Axis]
  Refine = true
  Suppressed = false
  Type = 0
FEATURE [Sketcher::SketchObject] Sketch156
  ArcFitTolerance = 1e-06
  AttachmentSupport = -> [Pocket063]
  ExternalGeometry = -> [Pocket063]
  FullyConstrained = true
  MakeInternals = false
  MapMode = 5
  Placement = pos=(0,13.1801,-22.8286) rot=(1,0,0;3.66519rad)
  sketch-geometry (24):
    g0: LineSegment StartX=8 StartY=-27.5233 StartZ=0 EndX=8 EndY=-28.5233 EndZ=0
    g1: LineSegment StartX=8 StartY=-28.5233 StartZ=0 EndX=12.9 EndY=-28.5233 EndZ=0
    g2: LineSegment StartX=12.9 StartY=-28.5233 StartZ=0 EndX=12.9 EndY=-27.5233 EndZ=0
    g3: LineSegment StartX=12.9 StartY=-27.5233 StartZ=0 EndX=8 EndY=-27.5233 EndZ=0
    g4: LineSegment StartX=8 StartY=-28.8733 StartZ=0 EndX=8 EndY=-29.8733 EndZ=0
    g5: LineSegment StartX=8 StartY=-29.8733 StartZ=0 EndX=12.9 EndY=-29.8733 EndZ=0
    g6: LineSegment StartX=12.9 StartY=-29.8733 StartZ=0 EndX=12.9 EndY=-28.8733 EndZ=0
    g7: LineSegment StartX=12.9 StartY=-28.8733 StartZ=0 EndX=8 EndY=-28.8733 EndZ=0
    g8: LineSegment StartX=8 StartY=-30.2391 StartZ=0 EndX=8 EndY=-31.2391 EndZ=0
    g9: LineSegment StartX=8 StartY=-31.2391 StartZ=0 EndX=12.9 EndY=-31.2391 EndZ=0
    g10: LineSegment StartX=12.9 StartY=-31.2391 StartZ=0 EndX=12.9 EndY=-30.2391 EndZ=0
    g11: LineSegment StartX=12.9 StartY=-30.2391 StartZ=0 EndX=8 EndY=-30.2391 EndZ=0
    g12: LineSegment StartX=23.1 StartY=-27.5233 StartZ=0 EndX=23.1 EndY=-28.5233 EndZ=0
    g13: LineSegment StartX=23.1 StartY=-28.5233 StartZ=0 EndX=28 EndY=-28.5233 EndZ=0
    g14: LineSegment StartX=28 StartY=-28.5233 StartZ=0 EndX=28 EndY=-27.5233 EndZ=0
    g15: LineSegment StartX=28 StartY=-27.5233 StartZ=0 EndX=23.1 EndY=-27.5233 EndZ=0
    g16: LineSegment StartX=23.1 StartY=-28.8733 StartZ=0 EndX=23.1 EndY=-29.8733 EndZ=0
    g17: LineSegment StartX=23.1 StartY=-29.8733 StartZ=0 EndX=28 EndY=-29.8733 EndZ=0
    g18: LineSegment StartX=28 StartY=-29.8733 StartZ=0 EndX=28 EndY=-28.8733 EndZ=0
    g19: LineSegment StartX=28 StartY=-28.8733 StartZ=0 EndX=23.1 EndY=-28.8733 EndZ=0
    g20: LineSegment StartX=23.1 StartY=-30.2391 StartZ=0 EndX=23.1 EndY=-31.2391 EndZ=0
    g21: LineSegment StartX=23.1 StartY=-31.2391 StartZ=0 EndX=28 EndY=-31.2391 EndZ=0
    g22: LineSegment StartX=28 StartY=-31.2391 StartZ=0 EndX=28 EndY=-30.2391 EndZ=0
    g23: LineSegment StartX=28 StartY=-30.2391 StartZ=0 EndX=23.1 EndY=-30.2391 EndZ=0
  constraints (73):
    c: Coincident(g0,g1)
    c: Coincident(g1,g2)
    c: Coincident(g2,g3)
    c: Coincident(g3,g0)
    c: Vertical(g0)
    c: Vertical(g2)
    c: Horizontal(g1)
    c: Horizontal(g3)
    c: Coincident(g4,g5)
    c: Coincident(g5,g6)
    c: Coincident(g6,g7)
    c: Coincident(g7,g4)
    c: Vertical(g4)
    c: Vertical(g6)
    c: Horizontal(g5)
    c: Horizontal(g7)
    c: Coincident(g8,g9)
    c: Coincident(g9,g10)
    c: Coincident(g10,g11)
    c: Coincident(g11,g8)
    c: Vertical(g8)
    c: Vertical(g10)
    c: Horizontal(g9)
    c: Horizontal(g11)
    c: DistanceY(g-3,g-3) = 4.71577
    c: DistanceY(g2,g2) = 1
    c: DistanceY(g6,g6) = 1
    c: DistanceY(g10,g10) = 1
    c: DistanceX(g2,g-4) = 0.5
    c: DistanceX(g6,g-6) = 0.5
    c: DistanceX(g9,g-6) = 0.5
    c: DistanceX(g-6,g8) = 0.5
    c: DistanceX(g-6,g4) = 0.5
    c: DistanceX(g-5,g0) = 0.5
    c: DistanceY(g0,g-5) = 0.5
    c: DistanceY(g-6,g8) = 0.5
    c: DistanceY(g4,g0) = 0.35
    c: Coincident(g12,g13)
    c: Coincident(g13,g14)
    c: Coincident(g14,g15)
    c: Coincident(g15,g12)
    c: Vertical(g12)
    c: Vertical(g14)
    c: Horizontal(g13)
    c: Horizontal(g15)
    c: Coincident(g16,g17)
    c: Coincident(g17,g18)
    c: Coincident(g18,g19)
    c: Coincident(g19,g16)
    c: Vertical(g16)
    c: Vertical(g18)
    c: Horizontal(g17)
    c: Horizontal(g19)
    c: Coincident(g20,g21)
    c: Coincident(g21,g22)
    c: Coincident(g22,g23)
    c: Coincident(g23,g20)
    c: Vertical(g20)
    c: Vertical(g22)
    c: Horizontal(g21)
    c: Horizontal(g23)
    c: DistanceX(g14,g-9) = 0.5
    c: DistanceX(g18,g-9) = 0.5
    c: DistanceX(g21,g-10) = 0.5
    c: DistanceX(g-10,g20) = 0.5
    c: DistanceX(g-10,g16) = 0.5
    c: DistanceX(g-8,g12) = 0.5
    c: DistanceY(g14,g14) = 1
    c: DistanceY(g18,g18) = 1
    c: DistanceY(g22,g22) = 1
    c: DistanceY(g14,g-9) = 0.5
    c: DistanceY(g-10,g21) = 0.5
    c: DistanceY(g18,g13) = 0.35
FEATURE [PartDesign::Pad] Pad115
  BaseFeature = -> Pocket063
  Direction = (0,0.5,-0.866025)
  Length = 0.5
  Length2 = 10
  Profile = -> Sketch156
  ReferenceAxis = -> Sketch156 [N_Axis]
  Refine = true
  Suppressed = false
  Type = 0
FEATURE [Sketcher::SketchObject] Sketch157
  ArcFitTolerance = 1e-06
  AttachmentSupport = -> [Pad115]
  ExternalGeometry = -> [Pad115]
  FullyConstrained = true
  MakeInternals = false
  MapMode = 5
  Placement = pos=(0,0,-10) rot=(1,0,0;3.14159rad)
  sketch-geometry (4):
    g0: LineSegment StartX=14.75 StartY=3.3 StartZ=0 EndX=14.75 EndY=-7 EndZ=0
    g1: LineSegment StartX=14.75 StartY=-7 StartZ=0 EndX=21.25 EndY=-7 EndZ=0
    g2: LineSegment StartX=21.25 StartY=-7 StartZ=0 EndX=21.25 EndY=3.3 EndZ=0
    g3: LineSegment StartX=21.25 StartY=3.3 StartZ=0 EndX=14.75 EndY=3.3 EndZ=0
  constraints (12):
    c: Coincident(g0,g1)
    c: Coincident(g1,g2)
    c: Coincident(g2,g3)
    c: Coincident(g3,g0)
    c: Vertical(g0)
    c: Vertical(g2)
    c: Horizontal(g1)
    c: Horizontal(g3)
    c: DistanceX(g-6,g0) = 2
    c: DistanceX(g1,g-6) = 2
    c: DistanceY(g-6,g1) = 3
    c: DistanceY(g2,g2) = 10.3
FEATURE [PartDesign::Pocket] Pocket064
  BaseFeature = -> Pad115
  Direction = (0,0,1)
  Length = 1
  Length2 = 5
  Profile = -> Sketch157
  ReferenceAxis = -> Sketch157 [N_Axis]
  Refine = true
  Suppressed = false
  Type = 0
FEATURE [Sketcher::SketchObject] Sketch158
  ArcFitTolerance = 1e-06
  AttachmentSupport = -> [Pocket064]
  ExternalGeometry = -> [Pocket064]
  FullyConstrained = true
  MakeInternals = false
  MapMode = 5
  Placement = pos=(0,0,-9) rot=(1,0,0;3.14159rad)
  sketch-geometry (6):
    g0: LineSegment StartX=12.75 StartY=0 StartZ=0 EndX=7.05 EndY=-3.2909 EndZ=0
    g1: LineSegment StartX=7.05 StartY=-3.2909 StartZ=0 EndX=7.05 EndY=0 EndZ=0
    g2: LineSegment StartX=7.05 StartY=0 StartZ=0 EndX=12.75 EndY=0 EndZ=0
    g3: LineSegment StartX=23.25 StartY=0 StartZ=0 EndX=28.95 EndY=0 EndZ=0
    g4: LineSegment StartX=28.95 StartY=0 StartZ=0 EndX=28.95 EndY=-3.2909 EndZ=0
    g5: LineSegment StartX=28.95 StartY=-3.2909 StartZ=0 EndX=23.25 EndY=0 EndZ=0
  constraints (14):
    c: Coincident(g0,g-5)
    c: PointOnObject(g0,g-6)
    c: Coincident(g1,g0)
    c: Coincident(g1,g-6)
    c: Coincident(g2,g1)
    c: Coincident(g2,g0)
    c: Coincident(g3,g-3)
    c: Coincident(g3,g-4)
    c: Coincident(g4,g3)
    c: PointOnObject(g4,g-4)
    c: Coincident(g5,g4)
    c: Coincident(g5,g3)
    c: Angle(g2,g0) = 0.523599
    c: Angle(g5,g3) = 0.523599
FEATURE [PartDesign::Pocket] Pocket065
  BaseFeature = -> Pocket064
  Direction = (0,0,1)
  Length = 2
  Length2 = 5
  Profile = -> Sketch158
  ReferenceAxis = -> Sketch158 [N_Axis]
  Refine = true
  Suppressed = false
  Type = 0
FEATURE [Sketcher::SketchObject] Sketch159
  ArcFitTolerance = 1e-06
  AttachmentSupport = -> [Pocket065]
  ExternalGeometry = -> [Pocket065]
  FullyConstrained = true
  MakeInternals = false
  MapMode = 5
  Placement = pos=(0,10,0) rot=(0,0.707107,0.707107;3.14159rad)
  sketch-geometry (6):
    g0: LineSegment StartX=-12.75 StartY=-9 StartZ=0 EndX=-7.05 EndY=-9 EndZ=0
    g1: LineSegment StartX=-7.05 StartY=-9 StartZ=0 EndX=-7.05 EndY=-8 EndZ=0
    g2: LineSegment StartX=-7.05 StartY=-8 StartZ=0 EndX=-12.75 EndY=-9 EndZ=0
    g3: LineSegment StartX=-23.25 StartY=-9 StartZ=0 EndX=-28.95 EndY=-9 EndZ=0
    g4: LineSegment StartX=-28.95 StartY=-9 StartZ=0 EndX=-28.95 EndY=-8 EndZ=0
    g5: LineSegment StartX=-28.95 StartY=-8 StartZ=0 EndX=-23.25 EndY=-9 EndZ=0
  constraints (14):
    c: Coincident(g0,g-4)
    c: Coincident(g0,g-4)
    c: Coincident(g1,g0)
    c: PointOnObject(g1,g-3)
    c: Coincident(g2,g1)
    c: Coincident(g2,g0)
    c: DistanceY(g1,g1) = 1
    c: Coincident(g3,g-5)
    c: Coincident(g3,g-6)
    c: Coincident(g4,g3)
    c: PointOnObject(g4,g-6)
    c: Coincident(g5,g4)
    c: Coincident(g5,g3)
    c: DistanceY(g4,g4) = 1
FEATURE [PartDesign::Pocket] Pocket066
  BaseFeature = -> Pocket065
  Direction = (0,-1,2e-16)
  Length = 10
  Length2 = 5
  Profile = -> Sketch159
  ReferenceAxis = -> Sketch159 [N_Axis]
  Refine = true
  Suppressed = false
  Type = 0
FEATURE [Sketcher::SketchObject] Sketch160
  ArcFitTolerance = 1e-06
  AttachmentSupport = -> [Pocket066]
  ExternalGeometry = -> [Pocket066]
  FullyConstrained = true
  MakeInternals = false
  MapMode = 5
  Placement = pos=(12.75,0,0) rot=(0.57735,-0.57735,-0.57735;2.0944rad)
  sketch-geometry (3):
    g0: LineSegment StartX=8 StartY=-10 StartZ=0 EndX=8 EndY=-9 EndZ=0
    g1: LineSegment StartX=8 StartY=-9 StartZ=0 EndX=4.26795 EndY=-10 EndZ=0
    g2: LineSegment StartX=4.26795 StartY=-10 StartZ=0 EndX=8 EndY=-10 EndZ=0
  constraints (8):
    c: Coincident(g0,g-4)
    c: PointOnObject(g0,g-3)
    c: Coincident(g1,g0)
    c: PointOnObject(g1,g-4)
    c: Coincident(g2,g1)
    c: Coincident(g2,g0)
    c: DistanceY(g0,g0) = 1
    c: Angle(g2,g1) = 0.261799
FEATURE [PartDesign::Pocket] Pocket067
  BaseFeature = -> Pocket066
  Direction = (1,0,0)
  Length = 12
  Length2 = 5
  Profile = -> Sketch160
  ReferenceAxis = -> Sketch160 [N_Axis]
  Refine = true
  Suppressed = false
  Type = 0
FEATURE [Sketcher::SketchObject] Sketch161
  ArcFitTolerance = 1e-06
  AttachmentSupport = -> [Pocket067]
  ExternalGeometry = -> [Pocket067]
  FullyConstrained = true
  MakeInternals = false
  MapMode = 5
  Placement = pos=(12.75,0,0) rot=(0.57735,-0.57735,-0.57735;2.0944rad)
  sketch-geometry (3):
    g0: LineSegment StartX=-10 StartY=-9 StartZ=0 EndX=-10 EndY=-10 EndZ=0
    g1: LineSegment StartX=-10 StartY=-10 StartZ=0 EndX=-9 EndY=-10 EndZ=0
    g2: LineSegment StartX=-9 StartY=-10 StartZ=0 EndX=-10 EndY=-9 EndZ=0
  constraints (7):
    c: Coincident(g0,g-4)
    c: Coincident(g0,g-5)
    c: Coincident(g1,g0)
    c: PointOnObject(g1,g-5)
    c: Coincident(g2,g1)
    c: Coincident(g2,g0)
    c: Angle(g2,g1) = 0.785398
FEATURE [PartDesign::Pocket] Pocket068
  BaseFeature = -> Pocket067
  Direction = (1,0,0)
  Length = 11
  Length2 = 5
  Profile = -> Sketch161
  ReferenceAxis = -> Sketch161 [N_Axis]
  Refine = true
  Suppressed = false
  Type = 0
FEATURE [Sketcher::SketchObject] Sketch162
  ArcFitTolerance = 1e-06
  AttachmentSupport = -> [Pocket068]
  ExternalGeometry = -> [Pocket068]
  FullyConstrained = true
  MakeInternals = false
  MapMode = 5
  Placement = pos=(0,-8,0) rot=(1,0,0;1.5708rad)
  sketch-geometry (6):
    g0: LineSegment StartX=12.75 StartY=-10 StartZ=0 EndX=13.75 EndY=-10 EndZ=0
    g1: LineSegment StartX=13.75 StartY=-10 StartZ=0 EndX=12.75 EndY=-9 EndZ=0
    g2: LineSegment StartX=12.75 StartY=-9 StartZ=0 EndX=12.75 EndY=-10 EndZ=0
    g3: LineSegment StartX=23.25 StartY=-9 StartZ=0 EndX=23.25 EndY=-10 EndZ=0
    g4: LineSegment StartX=23.25 StartY=-9 StartZ=0 EndX=22.25 EndY=-10 EndZ=0
    g5: LineSegment StartX=23.25 StartY=-10 StartZ=0 EndX=22.25 EndY=-10 EndZ=0
  constraints (14):
    c: Coincident(g0,g-4)
    c: PointOnObject(g0,g-4)
    c: Coincident(g1,g0)
    c: Coincident(g1,g-5)
    c: Coincident(g2,g1)
    c: Coincident(g2,g0)
    c: Coincident(g3,g-6)
    c: Coincident(g3,g-6)
    c: Coincident(g4,g3)
    c: PointOnObject(g4,g-4)
    c: Coincident(g5,g3)
    c: Coincident(g5,g4)
    c: Angle(g4,g3) = 0.785398
    c: Angle(g2,g1) = 0.785398
FEATURE [PartDesign::Pocket] Pocket069
  BaseFeature = -> Pocket068
  Direction = (0,1,-2e-16)
  Length = 18
  Length2 = 5
  Profile = -> Sketch162
  ReferenceAxis = -> Sketch162 [N_Axis]
  Refine = true
  Suppressed = false
  Type = 0
FEATURE [Sketcher::SketchObject] Sketch163
  ArcFitTolerance = 1e-06
  AttachmentSupport = -> [Pocket069]
  ExternalGeometry = -> [Pocket069]
  FullyConstrained = true
  MakeInternals = false
  MapMode = 5
  Placement = pos=(7,0,0) rot=(0.57735,-0.57735,-0.57735;2.0944rad)
  sketch-geometry (3):
    g0: LineSegment StartX=-17.2 StartY=-10 StartZ=0 EndX=-17.2 EndY=-9 EndZ=0
    g1: LineSegment StartX=-17.2 StartY=-9 StartZ=0 EndX=-18.2 EndY=-10 EndZ=0
    g2: LineSegment StartX=-18.2 StartY=-10 StartZ=0 EndX=-17.2 EndY=-10 EndZ=0
  constraints (8):
    c: Coincident(g0,g-4)
    c: PointOnObject(g0,g-3)
    c: Coincident(g1,g0)
    c: PointOnObject(g1,g-4)
    c: Coincident(g2,g1)
    c: Coincident(g2,g0)
    c: DistanceY(g0,g0) = 1
    c: DistanceX(g2,g2) = 1
FEATURE [PartDesign::Pocket] Pocket070
  BaseFeature = -> Pocket069
  Direction = (1,0,0)
  Length = 22
  Length2 = 5
  Profile = -> Sketch163
  ReferenceAxis = -> Sketch163 [N_Axis]
  Refine = true
  Suppressed = false
  Type = 0
FEATURE [Sketcher::SketchObject] Sketch164
  ArcFitTolerance = 1e-06
  AttachmentSupport = -> [Pocket070]
  ExternalGeometry = -> [Pocket070]
  FullyConstrained = true
  MakeInternals = false
  MapMode = 5
  Placement = pos=(0,17.2,0) rot=(1,0,0;1.5708rad)
  sketch-geometry (6):
    g0: LineSegment StartX=7 StartY=-9 StartZ=0 EndX=8 EndY=-10 EndZ=0
    g1: LineSegment StartX=8 StartY=-10 StartZ=0 EndX=7 EndY=-10 EndZ=0
    g2: LineSegment StartX=7 StartY=-10 StartZ=0 EndX=7 EndY=-9 EndZ=0
    g3: LineSegment StartX=29 StartY=-9 StartZ=0 EndX=29 EndY=-10 EndZ=0
    g4: LineSegment StartX=29 StartY=-10 StartZ=0 EndX=28 EndY=-10 EndZ=0
    g5: LineSegment StartX=28 StartY=-10 StartZ=0 EndX=29 EndY=-9 EndZ=0
  constraints (14):
    c: Coincident(g0,g-3)
    c: PointOnObject(g0,g-4)
    c: Coincident(g1,g0)
    c: Coincident(g1,g-4)
    c: Coincident(g2,g1)
    c: Coincident(g2,g0)
    c: DistanceX(g1,g1) = 1
    c: Coincident(g3,g-5)
    c: Coincident(g3,g-6)
    c: Coincident(g4,g3)
    c: PointOnObject(g4,g-6)
    c: Coincident(g5,g4)
    c: Coincident(g5,g3)
    c: DistanceX(g4,g4) = 1
FEATURE [PartDesign::Pocket] Pocket071
  BaseFeature = -> Pocket070
  Direction = (0,1,-2e-16)
  Length = 22
  Length2 = 5
  Profile = -> Sketch164
  ReferenceAxis = -> Sketch164 [N_Axis]
  Refine = true
  Suppressed = false
  Type = 0
FEATURE [PartDesign::Fillet] Fillet006
  Base = -> Pocket071 [Edge27,Edge11,Edge77,Edge96,Edge140,Edge2,Edge20,Edge71,Edge94,Edge107,Edge190,Edge229]
  BaseFeature = -> Pocket071
  Radius = 0.5
  Refine = true
  SupportTransform = false
  Suppressed = false
  UseAllEdges = false
FEATURE [PartDesign::Body] Body010  label="Front_Torso"
  AllowCompound = false
  Group = -> [Binder005,Sketch133,Pad101,Sketch134,Pad102,Sketch135,Pad103,Pad104,Sketch136,Pad105,Sketch137,Pad106,Sketch138,Pad107,Sketch139,Pocket053,Sketch140,Pocket054,Sketch141,Pocket055,Sketch142,Pocket056,Pad108,Sketch143,Pocket057,Sketch144,Pad109,Sketch145,Pad110,Sketch146,Pad111,Sketch147,Pocket058,Sketch148,Pocket059,Sketch149,Pad112,Sketch150,Pad113,Sketch151,Pocket060,Sketch152,Pad114,Sketch153,+24 more]
  Origin = -> Origin010
  Tip = -> Fillet006
FEATURE [PartDesign::SubShapeBinder] Binder006
  BindCopyOnChange = 0
  BindMode = 2
  ClaimChildren = false
  Context = -> Body011 [Binder006.]
  Fuse = false
  MakeFace = true
  OffsetFill = false
  OffsetIntersection = false
  OffsetJoinType = 0
  OffsetOpenResult = false
  PartialLoad = false
  Refine = true
  Relative = true
  _Version = 2
FEATURE [Sketcher::SketchObject] Sketch165
  ArcFitTolerance = 1e-06
  AttachmentSupport = -> [Binder006]
  ExternalGeometry = -> [Binder006]
  FullyConstrained = true
  MakeInternals = false
  MapMode = 5
  Placement = pos=(0,0,0) rot=(1,0,0;3.14159rad)
  sketch-geometry (4):
    g0: LineSegment StartX=7 StartY=-41.35 StartZ=0 EndX=7 EndY=-10.35 EndZ=0
    g1: LineSegment StartX=7 StartY=-10.35 StartZ=0 EndX=5 EndY=-10.35 EndZ=0
    g2: LineSegment StartX=5 StartY=-10.35 StartZ=0 EndX=5 EndY=-41.35 EndZ=0
    g3: LineSegment StartX=7 StartY=-41.35 StartZ=0 EndX=5 EndY=-41.35 EndZ=0
  constraints (12):
    c: PointOnObject(g0,g-3)
    c: PointOnObject(g0,g-5)
    c: Coincident(g1,g0)
    c: Horizontal(g1)
    c: Coincident(g2,g1)
    c: Vertical(g2)
    c: Coincident(g3,g0)
    c: Coincident(g3,g2)
    c: Horizontal(g3)
    c: DistanceY(g-4,g0) = 0.05
    c: DistanceY(g0,g-6) = 0.05
    c: DistanceX(g1,g1) = 2
FEATURE [PartDesign::Pad] Pad116
  Direction = (0,0,-1)
  Length = 10
  Length2 = 10
  Profile = -> Sketch165
  ReferenceAxis = -> Sketch165 [N_Axis]
  Refine = true
  Suppressed = false
  Type = 0
FEATURE [Sketcher::SketchObject] Sketch166
  ArcFitTolerance = 1e-06
  AttachmentSupport = -> [Pad116]
  ExternalGeometry = -> [Pad116]
  FullyConstrained = true
  MakeInternals = false
  MapMode = 5
  Placement = pos=(7,-4e-16,0) rot=(0.57735,0.57735,0.57735;2.0944rad)
  sketch-geometry (4):
    g0: LineSegment StartX=10.35 StartY=-2 StartZ=0 EndX=3.05 EndY=-2 EndZ=0
    g1: LineSegment StartX=3.05 StartY=-2 StartZ=0 EndX=3.05 EndY=-10 EndZ=0
    g2: LineSegment StartX=3.05 StartY=-10 StartZ=0 EndX=10.35 EndY=-10 EndZ=0
    g3: LineSegment StartX=10.35 StartY=-10 StartZ=0 EndX=10.35 EndY=-2 EndZ=0
  constraints (11):
    c: Coincident(g0,g1)
    c: Coincident(g1,g2)
    c: Coincident(g2,g3)
    c: Coincident(g3,g0)
    c: Horizontal(g0)
    c: Horizontal(g2)
    c: Vertical(g1)
    c: Vertical(g3)
    c: DistanceX(g0,g0) = 7.3
    c: Coincident(g2,g-3)
    c: DistanceY(g1,g1) = 8
FEATURE [PartDesign::Pad] Pad117
  BaseFeature = -> Pad116
  Direction = (1,0,0)
  Length = 7
  Length2 = 10
  Profile = -> Sketch166
  ReferenceAxis = -> Sketch166 [N_Axis]
  Refine = true
  Reversed = true
  Suppressed = false
  Type = 0
FEATURE [PartDesign::Pocket] Pocket072
  BaseFeature = -> Pad117
  Direction = (0,-1,0)
  Length = 0.05
  Length2 = 5
  Profile = -> Pad117 [Face7]
  Refine = true
  Suppressed = false
  Type = 0
FEATURE [Sketcher::SketchObject] Sketch167
  ArcFitTolerance = 1e-06
  AttachmentSupport = -> [Pocket072]
  ExternalGeometry = -> [Pocket072]
  FullyConstrained = true
  MakeInternals = false
  MapMode = 5
  Placement = pos=(5,0,0) rot=(0.57735,-0.57735,-0.57735;2.0944rad)
  sketch-geometry (7):
    g0: ArcOfCircle CenterX=-33.95 CenterY=-7 CenterZ=0 NormalX=0 NormalY=0 NormalZ=1 AngleXU=0 Radius=5 StartAngle=3.78509 EndAngle=5.63968
    g1: ArcOfCircle CenterX=-20.75 CenterY=-7 CenterZ=0 NormalX=0 NormalY=0 NormalZ=1 AngleXU=0 Radius=5 StartAngle=3.78509 EndAngle=5.63968
    g2: LineSegment [constr] StartX=-10.3 StartY=-12 StartZ=0 EndX=-41.35 EndY=-12 EndZ=0
    g3: LineSegment [constr] StartX=-10.3 StartY=-12 StartZ=0 EndX=-10.3 EndY=-10 EndZ=0
    g4: LineSegment [constr] StartX=-41.35 StartY=-10 StartZ=0 EndX=-41.35 EndY=-12 EndZ=0
    g5: LineSegment StartX=-24.75 StartY=-10 StartZ=0 EndX=-16.75 EndY=-10 EndZ=0
    g6: LineSegment StartX=-37.95 StartY=-10 StartZ=0 EndX=-29.95 EndY=-10 EndZ=0
  constraints (22):
    c: PointOnObject(g0,g-3)
    c: PointOnObject(g1,g-3)
    c: PointOnObject(g1,g-3)
    c: Radius(g0) = 5
    c: Radius(g1) = 5
    c: Horizontal(g2)
    c: Tangent(g2,g0)
    c: Coincident(g3,g2)
    c: Coincident(g3,g-4)
    c: Vertical(g3)
    c: DistanceY(g3,g3) = 2
    c: Tangent(g1,g2)
    c: Coincident(g4,g-3)
    c: Coincident(g4,g2)
    c: Vertical(g4)
    c: PointOnObject(g0,g-3)
    c: DistanceX(g4,g0) = 3.4
    c: DistanceX(g0,g1) = 5.2
    c: Coincident(g5,g1)
    c: Coincident(g5,g1)
    c: Coincident(g6,g0)
    c: Coincident(g6,g0)
FEATURE [PartDesign::Pad] Pad118
  BaseFeature = -> Pocket072
  Direction = (-1,0,0)
  Length = 2
  Length2 = 10
  Profile = -> Sketch167
  ReferenceAxis = -> Sketch167 [N_Axis]
  Refine = true
  Reversed = true
  Suppressed = false
  Type = 0
FEATURE [Sketcher::SketchObject] Sketch168
  ArcFitTolerance = 1e-06
  AttachmentSupport = -> [Pad118]
  ExternalGeometry = -> [Pad118]
  FullyConstrained = true
  MakeInternals = false
  MapMode = 5
  Placement = pos=(5,0,0) rot=(0.57735,-0.57735,-0.57735;2.0944rad)
  sketch-geometry (6):
    g0: LineSegment StartX=-10.3 StartY=-10 StartZ=0 EndX=-12.05 EndY=-10 EndZ=0
    g1: LineSegment StartX=-12.05 StartY=-10 StartZ=0 EndX=-12.05 EndY=0 EndZ=0
    g2: LineSegment StartX=-12.05 StartY=0 StartZ=0 EndX=-10.35 EndY=0 EndZ=0
    g3: LineSegment StartX=-10.35 StartY=0 StartZ=0 EndX=-10.35 EndY=-2 EndZ=0
    g4: LineSegment StartX=-10.35 StartY=-2 StartZ=0 EndX=-10.3 EndY=-2 EndZ=0
    g5: LineSegment StartX=-10.3 StartY=-2 StartZ=0 EndX=-10.3 EndY=-10 EndZ=0
  constraints (14):
    c: Coincident(g0,g-5)
    c: PointOnObject(g0,g-5)
    c: DistanceX(g0,g0) = 1.75
    c: Coincident(g1,g0)
    c: PointOnObject(g1,g-6)
    c: Vertical(g1)
    c: Coincident(g2,g1)
    c: Coincident(g2,g-6)
    c: Coincident(g3,g2)
    c: Coincident(g3,g-4)
    c: Coincident(g4,g3)
    c: Coincident(g4,g-3)
    c: Coincident(g5,g4)
    c: Coincident(g5,g0)
FEATURE [PartDesign::Pad] Pad119
  BaseFeature = -> Pad118
  Direction = (-1,0,0)
  Length = 5
  Length2 = 10
  Profile = -> Sketch168
  ReferenceAxis = -> Sketch168 [N_Axis]
  Refine = true
  Suppressed = false
  Type = 0
FEATURE [Sketcher::SketchObject] Sketch169
  ArcFitTolerance = 1e-06
  AttachmentSupport = -> [Pad119]
  ExternalGeometry = -> [Pad119]
  FullyConstrained = true
  MakeInternals = false
  MapMode = 5
  Placement = pos=(5,0,0) rot=(0.57735,-0.57735,-0.57735;2.0944rad)
  sketch-geometry (3):
    g0: LineSegment StartX=-12.05 StartY=0 StartZ=0 EndX=-16.35 EndY=0 EndZ=0
    g1: LineSegment StartX=-16.35 StartY=0 StartZ=0 EndX=-12.05 EndY=-4.3 EndZ=0
    g2: LineSegment StartX=-12.05 StartY=-4.3 StartZ=0 EndX=-12.05 EndY=0 EndZ=0
  constraints (9):
    c: PointOnObject(g0,g-3)
    c: PointOnObject(g0,g-3)
    c: Coincident(g1,g0)
    c: PointOnObject(g1,g-4)
    c: Coincident(g2,g1)
    c: Coincident(g2,g0)
    c: Vertical(g2)
    c: DistanceX(g0,g0) = 4.3
    c: Angle(g1,g0) = 0.785398
FEATURE [PartDesign::Pad] Pad120
  BaseFeature = -> Pad119
  Direction = (-1,0,0)
  Length = 5
  Length2 = 10
  Profile = -> Sketch169
  ReferenceAxis = -> Sketch169 [N_Axis]
  Refine = true
  Suppressed = false
  Type = 0
FEATURE [Sketcher::SketchObject] Sketch170
  ArcFitTolerance = 1e-06
  AttachmentSupport = -> [Pad120]
  ExternalGeometry = -> [Pad120]
  FullyConstrained = true
  MakeInternals = false
  MapMode = 5
  Placement = pos=(5,0,0) rot=(0.57735,-0.57735,-0.57735;2.0944rad)
  sketch-geometry (3):
    g0: LineSegment StartX=-41.35 StartY=0 StartZ=0 EndX=-37.35 EndY=0 EndZ=0
    g1: LineSegment StartX=-37.35 StartY=0 StartZ=0 EndX=-41.35 EndY=-4 EndZ=0
    g2: LineSegment StartX=-41.35 StartY=-4 StartZ=0 EndX=-41.35 EndY=0 EndZ=0
  constraints (8):
    c: Coincident(g0,g-4)
    c: PointOnObject(g0,g-3)
    c: Coincident(g1,g0)
    c: Coincident(g2,g1)
    c: Coincident(g2,g0)
    c: Vertical(g2)
    c: DistanceY(g2,g2) = 4
    c: DistanceX(g0,g0) = 4
FEATURE [PartDesign::Pad] Pad121
  BaseFeature = -> Pad120
  Direction = (-1,0,0)
  Length = 5
  Length2 = 10
  Profile = -> Sketch170
  ReferenceAxis = -> Sketch170 [N_Axis]
  Refine = true
  Suppressed = false
  Type = 0
FEATURE [Sketcher::SketchObject] Sketch171
  ArcFitTolerance = 1e-06
  AttachmentSupport = -> [Pad121]
  ExternalGeometry = -> [Pad121]
  FullyConstrained = true
  MakeInternals = false
  MapMode = 5
  Placement = pos=(7,0,0) rot=(0.57735,0.57735,0.57735;2.0944rad)
  sketch-geometry (1):
    g0: Circle CenterX=30.35 CenterY=-4 CenterZ=0 NormalX=0 NormalY=0 NormalZ=1 AngleXU=0 Radius=4
  constraints (3):
    c: Diameter(g0) = 8
    c: Tangent(g0,g-3)
    c: DistanceX(g0,g-3) = 11
FEATURE [PartDesign::Pad] Pad122
  BaseFeature = -> Pad121
  Direction = (1,0,0)
  Length = 5
  Length2 = 10
  Profile = -> Sketch171
  ReferenceAxis = -> Sketch171 [N_Axis]
  Refine = true
  Suppressed = false
  Type = 0
FEATURE [Sketcher::SketchObject] Sketch172
  ArcFitTolerance = 1e-06
  AttachmentSupport = -> [Pad122]
  ExternalGeometry = -> [Pad122]
  FullyConstrained = true
  MakeInternals = false
  MapMode = 5
  Placement = pos=(5,0,0) rot=(0.57735,-0.57735,-0.57735;2.0944rad)
  sketch-geometry (1):
    g0: Circle CenterX=-30.35 CenterY=-4 CenterZ=0 NormalX=0 NormalY=0 NormalZ=1 AngleXU=0 Radius=2.1
  constraints (2):
    c: Coincident(g0,g-3)
    c: Diameter(g0) = 4.2
FEATURE [PartDesign::Pocket] Pocket073
  BaseFeature = -> Pad122
  Direction = (1,0,0)
  Length = 5
  Length2 = 5
  Profile = -> Sketch172
  ReferenceAxis = -> Sketch172 [N_Axis]
  Refine = true
  Suppressed = false
  Type = 0
FEATURE [Sketcher::SketchObject] Sketch173
  ArcFitTolerance = 1e-06
  AttachmentSupport = -> [Pocket073]
  ExternalGeometry = -> [Pocket073]
  FullyConstrained = true
  MakeInternals = false
  MapMode = 5
  Placement = pos=(12,0,0) rot=(0.57735,0.57735,0.57735;2.0944rad)
  sketch-geometry (1):
    g0: Circle CenterX=30.35 CenterY=-4 CenterZ=0 NormalX=0 NormalY=0 NormalZ=1 AngleXU=0 Radius=1.4
  constraints (2):
    c: Coincident(g0,g-3)
    c: Diameter(g0) = 2.8
FEATURE [PartDesign::Pocket] Pocket074
  BaseFeature = -> Pocket073
  Direction = (-1,0,0)
  Length = 5
  Length2 = 5
  Profile = -> Sketch173
  ReferenceAxis = -> Sketch173 [N_Axis]
  Refine = true
  Suppressed = false
  Type = 0
FEATURE [Sketcher::SketchObject] Sketch174
  ArcFitTolerance = 1e-06
  AttachmentSupport = -> [Pocket074]
  ExternalGeometry = -> [Pocket074]
  FullyConstrained = true
  MakeInternals = false
  MapMode = 5
  Placement = pos=(5,0,0) rot=(0.57735,-0.57735,-0.57735;2.0944rad)
  sketch-geometry (2):
    g0: Circle CenterX=-33.95 CenterY=-7 CenterZ=0 NormalX=0 NormalY=0 NormalZ=1 AngleXU=0 Radius=0.75
    g1: Circle CenterX=-20.75 CenterY=-7 CenterZ=0 NormalX=0 NormalY=0 NormalZ=1 AngleXU=0 Radius=0.75
  constraints (4):
    c: Coincident(g0,g-4)
    c: Coincident(g1,g-3)
    c: Radius(g0) = 0.75
    c: Radius(g1) = 0.75
FEATURE [PartDesign::Pocket] Pocket075
  BaseFeature = -> Pocket074
  Direction = (1,0,0)
  Length = 8
  Length2 = 5
  Profile = -> Sketch174
  ReferenceAxis = -> Sketch174 [N_Axis]
  Refine = true
  Suppressed = false
  Type = 0
FEATURE [Sketcher::SketchObject] Sketch175
  ArcFitTolerance = 1e-06
  AttachmentSupport = -> [Pocket075]
  ExternalGeometry = -> [Pocket075]
  FullyConstrained = true
  MakeInternals = false
  MapMode = 5
  Placement = pos=(0,0,-10) rot=(1,0,0;3.14159rad)
  sketch-geometry (1):
    g0: Circle CenterX=3.55 CenterY=-7.2 CenterZ=0 NormalX=0 NormalY=0 NormalZ=1 AngleXU=0 Radius=1.45
  constraints (3):
    c: Radius(g0) = 1.45
    c: DistanceX(g0,g-4) = 3.45
    c: DistanceY(g0,g-4) = 4.15
FEATURE [PartDesign::Pocket] Pocket076
  BaseFeature = -> Pocket075
  Direction = (0,0,1)
  Length = 6
  Length2 = 5
  Profile = -> Sketch175
  ReferenceAxis = -> Sketch175 [N_Axis]
  Refine = true
  Suppressed = false
  Type = 0
FEATURE [Sketcher::SketchObject] Sketch176
  ArcFitTolerance = 1e-06
  AttachmentSupport = -> [Pocket076]
  ExternalGeometry = -> [Pocket076]
  FullyConstrained = true
  MakeInternals = false
  MapMode = 5
  Placement = pos=(0,0,-10) rot=(1,0,0;3.14159rad)
  sketch-geometry (3):
    g0: LineSegment StartX=9e-16 StartY=-3.05 StartZ=0 EndX=1.5 EndY=-3.05 EndZ=0
    g1: LineSegment StartX=1.5 StartY=-3.05 StartZ=0 EndX=9e-16 EndY=-4.55 EndZ=0
    g2: LineSegment StartX=9e-16 StartY=-4.55 StartZ=0 EndX=9e-16 EndY=-3.05 EndZ=0
  constraints (8):
    c: Coincident(g0,g-4)
    c: PointOnObject(g0,g-3)
    c: Coincident(g1,g0)
    c: PointOnObject(g1,g-4)
    c: Coincident(g2,g1)
    c: Coincident(g2,g0)
    c: DistanceX(g0,g0) = 1.5
    c: DistanceY(g2,g2) = 1.5
FEATURE [PartDesign::Pocket] Pocket077
  BaseFeature = -> Pocket076
  Direction = (0,0,1)
  Length = 8
  Length2 = 5
  Profile = -> Sketch176
  ReferenceAxis = -> Sketch176 [N_Axis]
  Refine = true
  Suppressed = false
  Type = 0
FEATURE [Sketcher::SketchObject] Sketch177
  ArcFitTolerance = 1e-06
  AttachmentSupport = -> [Pocket077]
  ExternalGeometry = -> [Pocket077]
  FullyConstrained = true
  MakeInternals = false
  MapMode = 5
  Placement = pos=(7e-16,0,0) rot=(0.57735,-0.57735,-0.57735;2.0944rad)
  sketch-geometry (4):
    g0: LineSegment StartX=-7.15 StartY=-4.4 StartZ=0 EndX=-10.15 EndY=-4.4 EndZ=0
    g1: LineSegment StartX=-10.15 StartY=-4.4 StartZ=0 EndX=-10.15 EndY=-7.6 EndZ=0
    g2: LineSegment StartX=-10.15 StartY=-7.6 StartZ=0 EndX=-7.15 EndY=-7.6 EndZ=0
    g3: LineSegment StartX=-7.15 StartY=-7.6 StartZ=0 EndX=-7.15 EndY=-4.4 EndZ=0
  constraints (12):
    c: Coincident(g0,g1)
    c: Coincident(g1,g2)
    c: Coincident(g2,g3)
    c: Coincident(g3,g0)
    c: Horizontal(g0)
    c: Horizontal(g2)
    c: Vertical(g1)
    c: Vertical(g3)
    c: DistanceX(g0,g0) = 3
    c: DistanceY(g1,g1) = 3.2
    c: DistanceY(g-3,g2) = 2.4
    c: DistanceX(g-4,g1) = 1.9
FEATURE [PartDesign::Pocket] Pocket078
  BaseFeature = -> Pocket077
  Direction = (1,0,0)
  Length = 1.5
  Length2 = 5
  Profile = -> Sketch177
  ReferenceAxis = -> Sketch177 [N_Axis]
  Refine = true
  Suppressed = false
  Type = 0
FEATURE [Sketcher::SketchObject] Sketch178
  ArcFitTolerance = 1e-06
  AttachmentSupport = -> [Pocket078]
  ExternalGeometry = -> [Pocket078]
  FullyConstrained = true
  MakeInternals = false
  MapMode = 5
  Placement = pos=(2.275,2.275,0) rot=(0.862856,-0.357407,-0.357407;1.71777rad)
  sketch-geometry (12):
    g0: LineSegment StartX=-3.21734 StartY=-3.9 StartZ=0 EndX=-3.21734 EndY=-4.1 EndZ=0
    g1: LineSegment StartX=-3.21734 StartY=-4.1 StartZ=0 EndX=-1.09602 EndY=-4.1 EndZ=0
    g2: LineSegment StartX=-1.09602 StartY=-4.1 StartZ=0 EndX=-1.09602 EndY=-3.9 EndZ=0
    g3: LineSegment StartX=-1.09602 StartY=-3.9 StartZ=0 EndX=-3.21734 EndY=-3.9 EndZ=0
    g4: LineSegment StartX=-3.21734 StartY=-5.9 StartZ=0 EndX=-3.21734 EndY=-6.1 EndZ=0
    g5: LineSegment StartX=-3.21734 StartY=-6.1 StartZ=0 EndX=-1.09602 EndY=-6.1 EndZ=0
    g6: LineSegment StartX=-1.09602 StartY=-6.1 StartZ=0 EndX=-1.09602 EndY=-5.9 EndZ=0
    g7: LineSegment StartX=-1.09602 StartY=-5.9 StartZ=0 EndX=-3.21734 EndY=-5.9 EndZ=0
    g8: LineSegment StartX=-3.21734 StartY=-7.9 StartZ=0 EndX=-3.21734 EndY=-8.1 EndZ=0
    g9: LineSegment StartX=-3.21734 StartY=-8.1 StartZ=0 EndX=-1.09602 EndY=-8.1 EndZ=0
    g10: LineSegment StartX=-1.09602 StartY=-8.1 StartZ=0 EndX=-1.09602 EndY=-7.9 EndZ=0
    g11: LineSegment StartX=-1.09602 StartY=-7.9 StartZ=0 EndX=-3.21734 EndY=-7.9 EndZ=0
  constraints (36):
    c: Coincident(g0,g1)
    c: Coincident(g1,g2)
    c: Coincident(g2,g3)
    c: Coincident(g3,g0)
    c: Vertical(g0)
    c: Vertical(g2)
    c: Horizontal(g1)
    c: Horizontal(g3)
    c: PointOnObject(g0,g-5)
    c: PointOnObject(g1,g-3)
    c: Coincident(g4,g5)
    c: Coincident(g5,g6)
    c: Coincident(g6,g7)
    c: Coincident(g7,g4)
    c: Vertical(g4)
    c: Vertical(g6)
    c: Horizontal(g5)
    c: Horizontal(g7)
    c: PointOnObject(g4,g-5)
    c: Coincident(g8,g9)
    c: Coincident(g9,g10)
    c: Coincident(g10,g11)
    c: Coincident(g11,g8)
    c: Vertical(g8)
    c: Vertical(g10)
    c: Horizontal(g9)
    c: Horizontal(g11)
    c: PointOnObject(g8,g-5)
    c: PointOnObject(g9,g-3)
    c: DistanceY(g6,g6) = 0.2
    c: DistanceY(g10,g10) = 0.2
    c: DistanceY(g2,g2) = 0.2
    c: DistanceY(g6,g-4) = 3.9
    c: PointOnObject(g6,g-3)
    c: DistanceY(g6,g1) = 1.8
    c: DistanceY(g10,g5) = 1.8
FEATURE [PartDesign::Pocket] Pocket079
  BaseFeature = -> Pocket078
  Direction = (0.707107,0.707107,0)
  Length = 0.5
  Length2 = 5
  Profile = -> Sketch178
  ReferenceAxis = -> Sketch178 [N_Axis]
  Refine = true
  Suppressed = false
  Type = 0
FEATURE [Sketcher::SketchObject] Sketch179
  ArcFitTolerance = 1e-06
  AttachmentSupport = -> [Pocket079]
  ExternalGeometry = -> [Pocket079]
  FullyConstrained = true
  MakeInternals = false
  MapMode = 5
  Placement = pos=(0,3.05,0) rot=(1,0,0;1.5708rad)
  sketch-geometry (12):
    g0: LineSegment StartX=1.5 StartY=-3.9 StartZ=0 EndX=1.5 EndY=-4.1 EndZ=0
    g1: LineSegment StartX=1.5 StartY=-4.1 StartZ=0 EndX=7 EndY=-4.1 EndZ=0
    g2: LineSegment StartX=7 StartY=-4.1 StartZ=0 EndX=7 EndY=-3.9 EndZ=0
    g3: LineSegment StartX=7 StartY=-3.9 StartZ=0 EndX=1.5 EndY=-3.9 EndZ=0
    g4: LineSegment StartX=1.5 StartY=-5.9 StartZ=0 EndX=1.5 EndY=-6.1 EndZ=0
    g5: LineSegment StartX=1.5 StartY=-6.1 StartZ=0 EndX=7 EndY=-6.1 EndZ=0
    g6: LineSegment StartX=7 StartY=-6.1 StartZ=0 EndX=7 EndY=-5.9 EndZ=0
    g7: LineSegment StartX=7 StartY=-5.9 StartZ=0 EndX=1.5 EndY=-5.9 EndZ=0
    g8: LineSegment StartX=1.5 StartY=-7.9 StartZ=0 EndX=1.5 EndY=-8.1 EndZ=0
    g9: LineSegment StartX=1.5 StartY=-8.1 StartZ=0 EndX=7 EndY=-8.1 EndZ=0
    g10: LineSegment StartX=7 StartY=-8.1 StartZ=0 EndX=7 EndY=-7.9 EndZ=0
    g11: LineSegment StartX=7 StartY=-7.9 StartZ=0 EndX=1.5 EndY=-7.9 EndZ=0
  constraints (30):
    c: Coincident(g0,g1)
    c: Coincident(g1,g2)
    c: Coincident(g2,g3)
    c: Coincident(g3,g0)
    c: Vertical(g2)
    c: Horizontal(g1)
    c: Horizontal(g3)
    c: Coincident(g0,g-5)
    c: PointOnObject(g1,g-3)
    c: Coincident(g4,g5)
    c: Coincident(g5,g6)
    c: Coincident(g6,g7)
    c: Coincident(g7,g4)
    c: Vertical(g6)
    c: Horizontal(g5)
    c: Horizontal(g7)
    c: Coincident(g4,g-6)
    c: PointOnObject(g5,g-3)
    c: Coincident(g8,g9)
    c: Coincident(g9,g10)
    c: Coincident(g10,g11)
    c: Coincident(g11,g8)
    c: Vertical(g10)
    c: Horizontal(g9)
    c: Horizontal(g11)
    c: Coincident(g8,g-7)
    c: PointOnObject(g9,g-3)
    c: Coincident(g8,g-7)
    c: Coincident(g4,g-6)
    c: Coincident(g0,g-5)
FEATURE [PartDesign::Pocket] Pocket080
  BaseFeature = -> Pocket079
  Direction = (0,1,-2e-16)
  Length = 0.5
  Length2 = 5
  Profile = -> Sketch179
  ReferenceAxis = -> Sketch179 [N_Axis]
  Refine = true
  Suppressed = false
  Type = 0
FEATURE [Sketcher::SketchObject] Sketch180
  ArcFitTolerance = 1e-06
  AttachmentSupport = -> [Pocket080]
  ExternalGeometry = -> [Pocket080]
  FullyConstrained = true
  MakeInternals = false
  MapMode = 5
  Placement = pos=(7,0,0) rot=(0.57735,0.57735,0.57735;2.0944rad)
  sketch-geometry (12):
    g0: LineSegment StartX=3.05 StartY=-3.9 StartZ=0 EndX=3.05 EndY=-4.1 EndZ=0
    g1: LineSegment StartX=3.05 StartY=-4.1 StartZ=0 EndX=7.65 EndY=-4.1 EndZ=0
    g2: LineSegment StartX=7.65 StartY=-4.1 StartZ=0 EndX=7.65 EndY=-3.9 EndZ=0
    g3: LineSegment StartX=7.65 StartY=-3.9 StartZ=0 EndX=3.05 EndY=-3.9 EndZ=0
    g4: LineSegment StartX=3.05 StartY=-5.9 StartZ=0 EndX=3.05 EndY=-6.1 EndZ=0
    g5: LineSegment StartX=3.05 StartY=-6.1 StartZ=0 EndX=7.65 EndY=-6.1 EndZ=0
    g6: LineSegment StartX=7.65 StartY=-6.1 StartZ=0 EndX=7.65 EndY=-5.9 EndZ=0
    g7: LineSegment StartX=7.65 StartY=-5.9 StartZ=0 EndX=3.05 EndY=-5.9 EndZ=0
    g8: LineSegment StartX=7.65 StartY=-6.1 StartZ=0 EndX=7.85 EndY=-6.1 EndZ=0
    g9: LineSegment StartX=7.85 StartY=-6.1 StartZ=0 EndX=7.85 EndY=-2 EndZ=0
    g10: LineSegment StartX=7.85 StartY=-2 StartZ=0 EndX=7.65 EndY=-2 EndZ=0
    g11: LineSegment StartX=7.65 StartY=-2 StartZ=0 EndX=7.65 EndY=-6.1 EndZ=0
  constraints (31):
    c: Coincident(g0,g1)
    c: Coincident(g1,g2)
    c: Coincident(g2,g3)
    c: Coincident(g3,g0)
    c: Vertical(g2)
    c: Horizontal(g1)
    c: Horizontal(g3)
    c: Coincident(g0,g-4)
    c: Coincident(g4,g5)
    c: Coincident(g5,g6)
    c: Coincident(g6,g7)
    c: Coincident(g7,g4)
    c: Vertical(g6)
    c: Horizontal(g5)
    c: Horizontal(g7)
    c: Coincident(g4,g-7)
    c: Coincident(g0,g-7)
    c: Coincident(g4,g-8)
    c: DistanceX(g3,g3) = 4.6
    c: DistanceX(g7,g7) = 4.6
    c: Coincident(g8,g9)
    c: Coincident(g9,g10)
    c: Coincident(g10,g11)
    c: Coincident(g11,g8)
    c: Horizontal(g8)
    c: Horizontal(g10)
    c: Vertical(g9)
    c: Vertical(g11)
    c: Coincident(g8,g5)
    c: PointOnObject(g9,g-3)
    c: DistanceX(g8,g8) = 0.2
FEATURE [PartDesign::Pocket] Pocket081
  BaseFeature = -> Pocket080
  Direction = (-1,0,0)
  Length = 0.5
  Length2 = 5
  Profile = -> Sketch180
  ReferenceAxis = -> Sketch180 [N_Axis]
  Refine = true
  Suppressed = false
  Type = 0
FEATURE [Sketcher::SketchObject] Sketch181
  ArcFitTolerance = 1e-06
  AttachmentSupport = -> [Pocket081]
  ExternalGeometry = -> [Pocket081]
  FullyConstrained = true
  MakeInternals = false
  MapMode = 5
  Placement = pos=(7,0,0) rot=(0.57735,0.57735,0.57735;2.0944rad)
  sketch-geometry (12):
    g0: LineSegment StartX=7.85 StartY=-6.1 StartZ=0 EndX=7.95 EndY=-6.1 EndZ=0
    g1: LineSegment StartX=7.95 StartY=-6.1 StartZ=0 EndX=7.95 EndY=-5.9 EndZ=0
    g2: LineSegment StartX=7.95 StartY=-5.9 StartZ=0 EndX=7.85 EndY=-5.9 EndZ=0
    g3: LineSegment StartX=7.85 StartY=-5.9 StartZ=0 EndX=7.85 EndY=-6.1 EndZ=0
    g4: LineSegment StartX=6.25 StartY=-6.1 StartZ=0 EndX=6.05 EndY=-6.1 EndZ=0
    g5: LineSegment StartX=6.05 StartY=-6.1 StartZ=0 EndX=6.05 EndY=-10 EndZ=0
    g6: LineSegment StartX=6.05 StartY=-10 StartZ=0 EndX=6.25 EndY=-10 EndZ=0
    g7: LineSegment StartX=6.25 StartY=-10 StartZ=0 EndX=6.25 EndY=-6.1 EndZ=0
    g8: LineSegment StartX=3.55 StartY=-8.1 StartZ=0 EndX=6.05 EndY=-8.1 EndZ=0
    g9: LineSegment StartX=6.05 StartY=-8.1 StartZ=0 EndX=6.05 EndY=-7.9 EndZ=0
    g10: LineSegment StartX=6.05 StartY=-7.9 StartZ=0 EndX=3.55 EndY=-7.9 EndZ=0
    g11: LineSegment StartX=3.55 StartY=-7.9 StartZ=0 EndX=3.55 EndY=-8.1 EndZ=0
  constraints (33):
    c: Coincident(g0,g1)
    c: Coincident(g1,g2)
    c: Coincident(g2,g3)
    c: Coincident(g3,g0)
    c: Horizontal(g0)
    c: Horizontal(g2)
    c: Vertical(g1)
    c: Vertical(g3)
    c: Coincident(g0,g-4)
    c: Coincident(g4,g5)
    c: Coincident(g5,g6)
    c: Coincident(g6,g7)
    c: Coincident(g7,g4)
    c: Horizontal(g4)
    c: Horizontal(g6)
    c: Vertical(g5)
    c: Vertical(g7)
    c: PointOnObject(g4,g-3)
    c: PointOnObject(g5,g-5)
    c: DistanceX(g6,g6) = 0.2
    c: DistanceX(g4,g0) = 1.7
    c: Coincident(g8,g9)
    c: Coincident(g9,g10)
    c: Coincident(g10,g11)
    c: Coincident(g11,g8)
    c: Horizontal(g8)
    c: Horizontal(g10)
    c: Vertical(g9)
    c: Coincident(g8,g-6)
    c: PointOnObject(g9,g5)
    c: Coincident(g10,g-6)
    c: DistanceX(g-7,g8) = 3
    c: DistanceY(g1,g1) = 0.2
FEATURE [PartDesign::Pocket] Pocket082
  BaseFeature = -> Pocket081
  Direction = (-1,0,0)
  Length = 0.5
  Length2 = 5
  Profile = -> Sketch181
  ReferenceAxis = -> Sketch181 [N_Axis]
  Refine = true
  Suppressed = false
  Type = 0
FEATURE [Sketcher::SketchObject] Sketch182
  ArcFitTolerance = 1e-06
  AttachmentSupport = -> [Pocket082]
  ExternalGeometry = -> [Pocket082]
  FullyConstrained = true
  MakeInternals = false
  MapMode = 5
  Placement = pos=(7,0,0) rot=(0.57735,0.57735,0.57735;2.0944rad)
  sketch-geometry (12):
    g0: LineSegment StartX=7.95 StartY=-5.9 StartZ=0 EndX=7.95 EndY=-8.1 EndZ=0
    g1: LineSegment StartX=7.95 StartY=-8.1 StartZ=0 EndX=8.15 EndY=-8.1 EndZ=0
    g2: LineSegment StartX=8.15 StartY=-8.1 StartZ=0 EndX=8.15 EndY=-5.9 EndZ=0
    g3: LineSegment StartX=8.15 StartY=-5.9 StartZ=0 EndX=7.95 EndY=-5.9 EndZ=0
    g4: LineSegment StartX=10.35 StartY=-2 StartZ=0 EndX=11.85 EndY=-2 EndZ=0
    g5: LineSegment StartX=11.85 StartY=-2 StartZ=0 EndX=11.85 EndY=-1.8 EndZ=0
    g6: LineSegment StartX=11.85 StartY=-1.8 StartZ=0 EndX=10.35 EndY=-1.8 EndZ=0
    g7: LineSegment StartX=10.35 StartY=-1.8 StartZ=0 EndX=10.35 EndY=-2 EndZ=0
    g8: LineSegment StartX=11.85 StartY=-1.8 StartZ=0 EndX=11.85 EndY=-10 EndZ=0
    g9: LineSegment StartX=11.85 StartY=-10 StartZ=0 EndX=12.05 EndY=-10 EndZ=0
    g10: LineSegment StartX=12.05 StartY=-10 StartZ=0 EndX=12.05 EndY=-1.8 EndZ=0
    g11: LineSegment StartX=12.05 StartY=-1.8 StartZ=0 EndX=11.85 EndY=-1.8 EndZ=0
  constraints (33):
    c: Coincident(g0,g1)
    c: Coincident(g1,g2)
    c: Coincident(g2,g3)
    c: Coincident(g3,g0)
    c: Vertical(g0)
    c: Vertical(g2)
    c: Horizontal(g1)
    c: Horizontal(g3)
    c: Coincident(g0,g-3)
    c: DistanceY(g0,g-4) = 0
    c: DistanceX(g3,g3) = 0.2
    c: Coincident(g4,g5)
    c: Coincident(g5,g6)
    c: Coincident(g6,g7)
    c: Coincident(g7,g4)
    c: Horizontal(g4)
    c: Horizontal(g6)
    c: Vertical(g5)
    c: Vertical(g7)
    c: Coincident(g4,g-5)
    c: Coincident(g8,g9)
    c: Coincident(g9,g10)
    c: Coincident(g10,g11)
    c: Coincident(g11,g8)
    c: Vertical(g8)
    c: Vertical(g10)
    c: Horizontal(g9)
    c: Horizontal(g11)
    c: Coincident(g8,g5)
    c: PointOnObject(g8,g-6)
    c: DistanceX(g9,g9) = 0.2
    c: DistanceY(g7,g7) = 0.2
    c: DistanceX(g-7,g4) = 4
FEATURE [PartDesign::Pocket] Pocket083
  BaseFeature = -> Pocket082
  Direction = (-1,0,0)
  Length = 0.5
  Length2 = 5
  Profile = -> Sketch182
  ReferenceAxis = -> Sketch182 [N_Axis]
  Refine = true
  Suppressed = false
  Type = 0
FEATURE [Sketcher::SketchObject] Sketch183
  ArcFitTolerance = 1e-06
  AttachmentSupport = -> [Pocket083]
  ExternalGeometry = -> [Pocket083]
  FullyConstrained = true
  MakeInternals = false
  MapMode = 5
  Placement = pos=(7,0,0) rot=(0.57735,0.57735,0.57735;2.0944rad)
  sketch-geometry (7):
    g0: LineSegment StartX=11.85 StartY=-6.31716 StartZ=0 EndX=11.85 EndY=-6.11716 EndZ=0
    g1: LineSegment StartX=11.85 StartY=-6.11716 StartZ=0 EndX=9.85 EndY=-6.11716 EndZ=0
    g2: LineSegment StartX=9.93284 StartY=-6.31716 StartZ=0 EndX=11.85 EndY=-6.31716 EndZ=0
    g3: LineSegment StartX=8.15 StartY=-8.1 StartZ=0 EndX=9.93284 EndY=-6.31716 EndZ=0
    g4: LineSegment StartX=9.85 StartY=-6.11716 StartZ=0 EndX=8.15 EndY=-7.81716 EndZ=0
    g5: LineSegment StartX=8.15 StartY=-7.81716 StartZ=0 EndX=8.15 EndY=-8.1 EndZ=0
    g6: LineSegment [constr] StartX=8.85711 StartY=-7.11005 StartZ=0 EndX=8.99853 EndY=-7.25147 EndZ=0
  constraints (21):
    c: Coincident(g0,g1)
    c: Coincident(g2,g0)
    c: Vertical(g0)
    c: Horizontal(g1)
    c: Horizontal(g2)
    c: PointOnObject(g0,g-4)
    c: DistanceY(g2,g1) = 0.2
    c: DistanceX(g1,g1) = 2
    c: Coincident(g3,g-3)
    c: Coincident(g4,g1)
    c: PointOnObject(g4,g-3)
    c: Coincident(g5,g4)
    c: Coincident(g5,g3)
    c: Coincident(g3,g2)
    c: Parallel(g4,g3)
    c: Angle(g4,g-3) = 0.785398
    c: PointOnObject(g6,g4)
    c: PointOnObject(g6,g3)
    c: Angle(g4,g6) = 1.5708
    c: Distance(g6,g4) = 1
    c: Distance(g6) = 0.2
FEATURE [PartDesign::Pocket] Pocket084
  BaseFeature = -> Pocket083
  Direction = (-1,0,0)
  Length = 0.5
  Length2 = 5
  Profile = -> Sketch183
  ReferenceAxis = -> Sketch183 [N_Axis]
  Refine = true
  Suppressed = false
  Type = 0
FEATURE [Sketcher::SketchObject] Sketch184
  ArcFitTolerance = 1e-06
  AttachmentSupport = -> [Pocket084]
  ExternalGeometry = -> [Pocket084]
  FullyConstrained = true
  MakeInternals = false
  MapMode = 5
  Placement = pos=(7e-16,0,0) rot=(0.57735,-0.57735,-0.57735;2.0944rad)
  sketch-geometry (1):
    g0: Circle CenterX=-11.85 CenterY=-2.5 CenterZ=0 NormalX=0 NormalY=0 NormalZ=1 AngleXU=0 Radius=1
  constraints (3):
    c: Diameter(g0) = 2
    c: DistanceX(g0,g-3) = 1.5
    c: DistanceY(g0,g-3) = 0.5
FEATURE [PartDesign::Pocket] Pocket085
  BaseFeature = -> Pocket084
  Direction = (1,0,0)
  Length = 0.5
  Length2 = 5
  Profile = -> Sketch184
  ReferenceAxis = -> Sketch184 [N_Axis]
  Refine = true
  Suppressed = false
  Type = 0
FEATURE [PartDesign::Fillet] Fillet007
  Base = -> Pocket085 [Edge147,Edge105,Edge103,Edge101,Edge98,Edge107,Edge192,Edge92,Edge187,Edge191,Edge190,Edge200,Edge186,Edge184,Edge91,Edge185,Edge150,Edge151,Edge220,Edge218,Edge219,Edge6,Edge20,Edge57,Edge203,Edge205,Edge207,Edge19,Edge18,Edge17,Edge109,Edge106,Edge102,Edge99,Edge152,Edge75,Edge148,Edge5,Edge10]
  BaseFeature = -> Pocket085
  Radius = 0.3
  Refine = true
  SupportTransform = false
  Suppressed = false
  UseAllEdges = false
FEATURE [PartDesign::SubShapeBinder] Binder007
  BindCopyOnChange = 0
  BindMode = 2
  ClaimChildren = false
  Context = -> Body012 [Binder007.]
  Fuse = false
  MakeFace = true
  OffsetFill = false
  OffsetIntersection = false
  OffsetJoinType = 0
  OffsetOpenResult = false
  PartialLoad = false
  Refine = true
  Relative = true
  _Version = 2
FEATURE [Sketcher::SketchObject] Sketch185
  ArcFitTolerance = 1e-06
  AttachmentSupport = -> [Binder007]
  ExternalGeometry = -> [Binder007]
  FullyConstrained = true
  MakeInternals = false
  MapMode = 5
  Placement = pos=(12,0,0) rot=(0.57735,0.57735,0.57735;2.0944rad)
  sketch-geometry (4):
    g0: LineSegment StartX=26.35 StartY=-0.05 StartZ=0 EndX=26.35 EndY=-7.25 EndZ=0
    g1: LineSegment StartX=26.35 StartY=-7.25 StartZ=0 EndX=34.35 EndY=-7.25 EndZ=0
    g2: LineSegment StartX=34.35 StartY=-7.25 StartZ=0 EndX=34.35 EndY=-0.05 EndZ=0
    g3: LineSegment StartX=34.35 StartY=-0.05 StartZ=0 EndX=26.35 EndY=-0.05 EndZ=0
  constraints (12):
    c: Coincident(g0,g1)
    c: Coincident(g1,g2)
    c: Coincident(g2,g3)
    c: Coincident(g3,g0)
    c: Vertical(g0)
    c: Vertical(g2)
    c: Horizontal(g1)
    c: Horizontal(g3)
    c: DistanceX(g3,g3) = 8
    c: DistanceY(g0,g0) = 7.2
    c: DistanceX(g0,g-3) = 4
    c: DistanceY(g-3,g0) = 3.95
FEATURE [PartDesign::Pad] Pad123
  Direction = (1,0,0)
  Length = 5.3
  Length2 = 10
  Profile = -> Sketch185
  ReferenceAxis = -> Sketch185 [N_Axis]
  Refine = true
  Suppressed = false
  Type = 0
FEATURE [Sketcher::SketchObject] Sketch186
  ArcFitTolerance = 1e-06
  AttachmentSupport = -> [Pad123]
  ExternalGeometry = -> [Binder007]
  FullyConstrained = true
  MakeInternals = false
  MapMode = 5
  Placement = pos=(12,0,0) rot=(0.57735,-0.57735,-0.57735;2.0944rad)
  sketch-geometry (1):
    g0: Circle CenterX=-30.35 CenterY=-4 CenterZ=0 NormalX=0 NormalY=0 NormalZ=1 AngleXU=0 Radius=0.9
  constraints (2):
    c: Coincident(g0,g-3)
    c: Radius(g0) = 0.9
FEATURE [PartDesign::Pocket] Pocket086
  BaseFeature = -> Pad123
  Direction = (1,0,0)
  Length = 7
  Length2 = 5
  Profile = -> Sketch186
  ReferenceAxis = -> Sketch186 [N_Axis]
  Refine = true
  Suppressed = false
  Type = 0
FEATURE [Sketcher::SketchObject] Sketch187
  ArcFitTolerance = 1e-06
  AttachmentSupport = -> [Pocket086]
  ExternalGeometry = -> [Pocket086]
  FullyConstrained = true
  MakeInternals = false
  MapMode = 5
  Placement = pos=(0,34.35,0) rot=(0,0.707107,0.707107;3.14159rad)
  sketch-geometry (4):
    g0: LineSegment StartX=-17.3 StartY=-0.05 StartZ=0 EndX=-17.3 EndY=-7.25 EndZ=0
    g1: LineSegment StartX=-17.3 StartY=-7.25 StartZ=0 EndX=-16.3 EndY=-7.25 EndZ=0
    g2: LineSegment StartX=-16.3 StartY=-7.25 StartZ=0 EndX=-16.3 EndY=-0.05 EndZ=0
    g3: LineSegment StartX=-16.3 StartY=-0.05 StartZ=0 EndX=-17.3 EndY=-0.05 EndZ=0
  constraints (11):
    c: Coincident(g0,g1)
    c: Coincident(g1,g2)
    c: Coincident(g2,g3)
    c: Coincident(g3,g0)
    c: Vertical(g0)
    c: Vertical(g2)
    c: Horizontal(g1)
    c: Horizontal(g3)
    c: Coincident(g0,g-5)
    c: PointOnObject(g1,g-4)
    c: DistanceX(g1,g1) = 1
FEATURE [PartDesign::Pad] Pad124
  BaseFeature = -> Pocket086
  Direction = (0,1,-2e-16)
  Length = 1.2
  Length2 = 10
  Profile = -> Sketch187
  ReferenceAxis = -> Sketch187 [N_Axis]
  Refine = true
  Suppressed = false
  Type = 0
FEATURE [Sketcher::SketchObject] Sketch188
  ArcFitTolerance = 1e-06
  AttachmentSupport = -> [Pad124]
  ExternalGeometry = -> [Pad124]
  FullyConstrained = true
  MakeInternals = false
  MapMode = 5
  Placement = pos=(0,26.35,0) rot=(1,0,0;1.5708rad)
  sketch-geometry (4):
    g0: LineSegment StartX=17.3 StartY=-0.05 StartZ=0 EndX=16.3 EndY=-0.05 EndZ=0
    g1: LineSegment StartX=16.3 StartY=-0.05 StartZ=0 EndX=16.3 EndY=-7.25 EndZ=0
    g2: LineSegment StartX=16.3 StartY=-7.25 StartZ=0 EndX=17.3 EndY=-7.25 EndZ=0
    g3: LineSegment StartX=17.3 StartY=-7.25 StartZ=0 EndX=17.3 EndY=-0.05 EndZ=0
  constraints (11):
    c: Coincident(g0,g1)
    c: Coincident(g1,g2)
    c: Coincident(g2,g3)
    c: Coincident(g3,g0)
    c: Horizontal(g0)
    c: Horizontal(g2)
    c: Vertical(g1)
    c: Vertical(g3)
    c: Coincident(g0,g-3)
    c: PointOnObject(g1,g-4)
    c: DistanceX(g2,g2) = 1
FEATURE [PartDesign::Pad] Pad125
  BaseFeature = -> Pad124
  Direction = (0,-1,2e-16)
  Length = 1.2
  Length2 = 10
  Profile = -> Sketch188
  ReferenceAxis = -> Sketch188 [N_Axis]
  Refine = true
  Suppressed = false
  Type = 0
FEATURE [Sketcher::SketchObject] Sketch189
  ArcFitTolerance = 1e-06
  AttachmentSupport = -> [Fillet007]
  ExternalGeometry = -> [Fillet007]
  FullyConstrained = true
  MakeInternals = false
  MapMode = 5
  Placement = pos=(5,0,0) rot=(0.57735,-0.57735,-0.57735;2.0944rad)
  sketch-geometry (2):
    g0: Circle CenterX=-20.75 CenterY=-7 CenterZ=0 NormalX=0 NormalY=0 NormalZ=1 AngleXU=0 Radius=2.25
    g1: Circle CenterX=-33.95 CenterY=-7 CenterZ=0 NormalX=0 NormalY=0 NormalZ=1 AngleXU=0 Radius=2.25
  constraints (4):
    c: Coincident(g0,g-3)
    c: Coincident(g1,g-4)
    c: Diameter(g1) = 4.5
    c: Diameter(g0) = 4.5
FEATURE [PartDesign::Pad] Pad126
  BaseFeature = -> Fillet007
  Direction = (-1,0,0)
  Length = 2
  Length2 = 10
  Profile = -> Sketch189
  ReferenceAxis = -> Sketch189 [N_Axis]
  Refine = true
  Suppressed = false
  Type = 0
FEATURE [PartDesign::Pocket] Pocket087
  BaseFeature = -> Pad126
  Direction = (-1,0,0)
  Length = 5
  Length2 = 5
  Profile = -> Pad126 [Face133,Face134]
  Refine = true
  Suppressed = false
  Type = 0
FEATURE [PartDesign::Body] Body011  label="Left_Arm"
  AllowCompound = false
  Group = -> [Binder006,Sketch165,Pad116,Sketch166,Pad117,Pocket072,Sketch167,Pad118,Sketch168,Pad119,Sketch169,Pad120,Sketch170,Pad121,Sketch171,Pad122,Sketch172,Pocket073,Sketch173,Pocket074,Sketch174,Pocket075,Sketch175,Pocket076,Sketch176,Pocket077,Sketch177,Pocket078,Sketch178,Pocket079,Sketch179,Pocket080,Sketch180,Pocket081,Sketch181,Pocket082,Sketch182,Pocket083,Sketch183,Pocket084,Sketch184,Pocket085,+4 more]
  Origin = -> Origin011
  Tip = -> Pocket087
FEATURE [Sketcher::SketchObject] Sketch190
  ArcFitTolerance = 1e-06
  AttachmentSupport = -> [XY_Plane013]
  FullyConstrained = true
  MakeInternals = false
  MapMode = 5
  sketch-geometry (4):
    g0: LineSegment StartX=0 StartY=0 StartZ=0 EndX=8 EndY=0 EndZ=0
    g1: LineSegment StartX=8 StartY=0 StartZ=0 EndX=8 EndY=10 EndZ=0
    g2: LineSegment StartX=8 StartY=10 StartZ=0 EndX=0 EndY=10 EndZ=0
    g3: LineSegment StartX=0 StartY=10 StartZ=0 EndX=0 EndY=0 EndZ=0
  constraints (11):
    c: Coincident(g0,g1)
    c: Coincident(g1,g2)
    c: Coincident(g2,g3)
    c: Coincident(g3,g0)
    c: Horizontal(g0)
    c: Horizontal(g2)
    c: Vertical(g1)
    c: Vertical(g3)
    c: Coincident(g0,g-1)
    c: DistanceX(g2,g2) = 8
    c: DistanceY(g3,g3) = 10
FEATURE [PartDesign::Pad] Pad127
  Direction = (0,0,1)
  Length = 3.5
  Length2 = 10
  Profile = -> Sketch190
  ReferenceAxis = -> Sketch190 [N_Axis]
  Refine = true
  Suppressed = false
  Type = 0
FEATURE [Sketcher::SketchObject] Sketch191
  ArcFitTolerance = 1e-06
  AttachmentSupport = -> [Pad127]
  ExternalGeometry = -> [Pad127]
  FullyConstrained = true
  MakeInternals = false
  MapMode = 5
  Placement = pos=(0,0,0) rot=(1,0,0;3.14159rad)
  sketch-geometry (4):
    g0: LineSegment StartX=0 StartY=0 StartZ=0 EndX=0 EndY=-1.4 EndZ=0
    g1: LineSegment StartX=0 StartY=-1.4 StartZ=0 EndX=8 EndY=-1.4 EndZ=0
    g2: LineSegment StartX=8 StartY=-1.4 StartZ=0 EndX=8 EndY=0 EndZ=0
    g3: LineSegment StartX=8 StartY=0 StartZ=0 EndX=0 EndY=0 EndZ=0
  constraints (11):
    c: Coincident(g0,g1)
    c: Coincident(g1,g2)
    c: Coincident(g2,g3)
    c: Coincident(g3,g0)
    c: Vertical(g0)
    c: Vertical(g2)
    c: Horizontal(g1)
    c: Horizontal(g3)
    c: Coincident(g0,g-1)
    c: PointOnObject(g1,g-3)
    c: DistanceY(g0,g0) = 1.4
FEATURE [PartDesign::Pad] Pad128
  BaseFeature = -> Pad127
  Direction = (0,0,-1)
  Length = 3.5
  Length2 = 10
  Profile = -> Sketch191
  ReferenceAxis = -> Sketch191 [N_Axis]
  Refine = true
  Suppressed = false
  Type = 0
FEATURE [Sketcher::SketchObject] Sketch192
  ArcFitTolerance = 1e-06
  AttachmentSupport = -> [Pad128]
  ExternalGeometry = -> [Pad128]
  FullyConstrained = true
  MakeInternals = false
  MapMode = 5
  Placement = pos=(0,0,0) rot=(0.57735,-0.57735,-0.57735;2.0944rad)
  sketch-geometry (2):
    g0: ArcOfCircle CenterX=-8.65 CenterY=0 CenterZ=0 NormalX=0 NormalY=0 NormalZ=1 AngleXU=0 Radius=1.35 StartAngle=0 EndAngle=3.14159
    g1: LineSegment StartX=-10 StartY=2e-16 StartZ=0 EndX=-7.3 EndY=0 EndZ=0
  constraints (6):
    c: Coincident(g0,g-4)
    c: PointOnObject(g0,g-4)
    c: PointOnObject(g0,g-4)
    c: Diameter(g0) = 2.7
    c: Coincident(g1,g0)
    c: Coincident(g1,g0)
FEATURE [PartDesign::Pad] Pad129
  BaseFeature = -> Pad128
  Direction = (-1,0,0)
  Length = 1.8
  Length2 = 10
  Profile = -> Sketch192
  ReferenceAxis = -> Sketch192 [N_Axis]
  Refine = true
  Suppressed = false
  Type = 0
FEATURE [Sketcher::SketchObject] Sketch193
  ArcFitTolerance = 1e-06
  AttachmentSupport = -> [Pad129]
  ExternalGeometry = -> [Pad129]
  FullyConstrained = true
  MakeInternals = false
  MapMode = 5
  Placement = pos=(8,0,0) rot=(0.57735,0.57735,0.57735;2.0944rad)
  sketch-geometry (2):
    g0: ArcOfCircle CenterX=8.65 CenterY=0 CenterZ=0 NormalX=0 NormalY=0 NormalZ=1 AngleXU=0 Radius=1.35 StartAngle=0 EndAngle=3.14159
    g1: LineSegment StartX=7.3 StartY=2e-16 StartZ=0 EndX=10 EndY=0 EndZ=0
  constraints (6):
    c: Coincident(g0,g-4)
    c: PointOnObject(g0,g-4)
    c: PointOnObject(g0,g-4)
    c: Coincident(g1,g0)
    c: Coincident(g1,g0)
    c: Diameter(g0) = 2.7
FEATURE [PartDesign::Pad] Pad130
  BaseFeature = -> Pad129
  Direction = (1,0,0)
  Length = 1.8
  Length2 = 10
  Profile = -> Sketch193
  ReferenceAxis = -> Sketch193 [N_Axis]
  Refine = true
  Suppressed = false
  Type = 0
FEATURE [PartDesign::Pocket] Pocket088
  BaseFeature = -> Pad130
  Direction = (0,0,-1)
  Length = 0.5
  Length2 = 5
  Profile = -> Pad130 [Face1]
  Refine = true
  Suppressed = false
  Type = 0
FEATURE [PartDesign::Pad] Pad131
  BaseFeature = -> Pocket088
  Direction = (-1,0,0)
  Length = 0.1
  Length2 = 10
  Profile = -> Pocket088 [Face2]
  Refine = true
  Suppressed = false
  Type = 0
FEATURE [PartDesign::Pad] Pad132
  BaseFeature = -> Pad131
  Direction = (1,0,0)
  Length = 0.1
  Length2 = 10
  Profile = -> Pad131 [Face5]
  Refine = true
  Suppressed = false
  Type = 0
FEATURE [Sketcher::SketchObject] Sketch195
  ArcFitTolerance = 1e-06
  AttachmentOffset = pos=(0,0,-2.2) rot=(0,0,1;0rad)
  AttachmentSupport = -> [Pad132]
  ExternalGeometry = -> [Pad132]
  FullyConstrained = true
  MakeInternals = false
  MapMode = 5
  Placement = pos=(0.4,0,0) rot=(0.57735,-0.57735,-0.57735;2.0944rad)
  sketch-geometry (2):
    g0: LineSegment StartX=-10 StartY=5.6939e-12 StartZ=0 EndX=-7.3 EndY=5.694e-12 EndZ=0
    g1: ArcOfCircle CenterX=-8.65 CenterY=1e-16 CenterZ=0 NormalX=0 NormalY=0 NormalZ=1 AngleXU=0 Radius=1.35 StartAngle=3.14159 EndAngle=6.28319
  constraints (5):
    c: Coincident(g0,g-3)
    c: Coincident(g0,g-3)
    c: Coincident(g1,g0)
    c: Coincident(g1,g0)
    c: PointOnObject(g1,g0)
FEATURE [PartDesign::Pad] Pad133
  BaseFeature = -> Pad132
  Direction = (-1,0,0)
  Length = 7.2
  Length2 = 10
  Profile = -> Sketch195
  ReferenceAxis = -> Sketch195 [N_Axis]
  Refine = true
  Reversed = true
  Suppressed = false
  Type = 0
FEATURE [Sketcher::SketchObject] Sketch196
  ArcFitTolerance = 1e-06
  AttachmentSupport = -> [Pad133]
  ExternalGeometry = -> [Pad133]
  FullyConstrained = true
  MakeInternals = false
  MapMode = 5
  Placement = pos=(0,0,0) rot=(1,0,0;3.14159rad)
  sketch-geometry (16):
    g0: LineSegment StartX=6.3 StartY=-6.73887 StartZ=0 EndX=6.3 EndY=-3.23887 EndZ=0
    g1: LineSegment StartX=6.3 StartY=-3.23887 StartZ=0 EndX=7.64681 EndY=-3.56312 EndZ=0
    g2: LineSegment StartX=7.8 StartY=-3.75756 StartZ=0 EndX=7.8 EndY=-5.95756 EndZ=0
    g3: LineSegment StartX=7.67952 StartY=-6.14107 StartZ=0 EndX=6.3 EndY=-6.73887 EndZ=0
    g4: ArcOfCircle CenterX=7.6 CenterY=-5.95756 CenterZ=0 NormalX=0 NormalY=0 NormalZ=1 AngleXU=0 Radius=0.2 StartAngle=5.1213 EndAngle=6.28319
    g5: GeomPoint [constr] X=7.8 Y=-6.08887 Z=0
    g6: ArcOfCircle CenterX=7.6 CenterY=-3.75756 CenterZ=0 NormalX=0 NormalY=0 NormalZ=1 AngleXU=0 Radius=0.2 StartAngle=1e-16 EndAngle=1.33454
    g7: GeomPoint [constr] X=7.8 Y=-3.6 Z=0
    g8: LineSegment StartX=1.7 StartY=-3.23887 StartZ=0 EndX=1.7 EndY=-6.73887 EndZ=0
    g9: LineSegment StartX=1.7 StartY=-6.73887 StartZ=0 EndX=0.320479 EndY=-6.14107 EndZ=0
    g10: LineSegment StartX=0.2 StartY=-5.95756 StartZ=0 EndX=0.2 EndY=-3.75756 EndZ=0
    g11: LineSegment StartX=0.353187 StartY=-3.56312 StartZ=0 EndX=1.7 EndY=-3.23887 EndZ=0
    g12: ArcOfCircle CenterX=0.4 CenterY=-5.95756 CenterZ=0 NormalX=0 NormalY=0 NormalZ=1 AngleXU=0 Radius=0.2 StartAngle=3.14159 EndAngle=4.30348
    g13: GeomPoint [constr] X=0.2 Y=-6.08887 Z=0
    g14: ArcOfCircle CenterX=0.4 CenterY=-3.75756 CenterZ=0 NormalX=0 NormalY=0 NormalZ=1 AngleXU=0 Radius=0.2 StartAngle=1.80706 EndAngle=3.14159
    g15: GeomPoint [constr] X=0.2 Y=-3.6 Z=0
  constraints (40):
    c: Vertical(g0)
    c: Coincident(g1,g0)
    c: Vertical(g2)
    c: Coincident(g3,g0)
    c: PointOnObject(g5,g2)
    c: PointOnObject(g5,g3)
    c: Tangent(g2,g4) = 1.5708
    c: Tangent(g3,g4) = 1.5708
    c: PointOnObject(g7,g1)
    c: PointOnObject(g7,g2)
    c: Tangent(g1,g6) = 1.5708
    c: Tangent(g2,g6) = 1.5708
    c: DistanceY(g0,g0) = 3.5
    c: DistanceY(g2,g2) = 2.2
    c: Radius(g4) = 0.2
    c: Radius(g6) = 0.2
    c: DistanceY(g0,g5) = 0.65
    c: DistanceX(g0,g2) = 1.5
    c: DistanceX(g2,g-3) = 0.3
    c: DistanceY(g7,g-3) = 2.2
    c: Vertical(g8)
    c: Coincident(g9,g8)
    c: Vertical(g10)
    c: Coincident(g11,g8)
    c: DistanceY(g8,g8) = 3.5
    c: PointOnObject(g13,g9)
    c: PointOnObject(g13,g10)
    c: Tangent(g9,g12) = 1.5708
    c: Tangent(g10,g12) = 1.5708
    c: PointOnObject(g15,g10)
    c: PointOnObject(g15,g11)
    c: Tangent(g10,g14) = 1.5708
    c: Tangent(g11,g14) = 1.5708
    c: DistanceX(g-4,g10) = 0.3
    c: Radius(g14) = 0.2
    c: Radius(g12) = 0.2
    c: DistanceX(g10,g8) = 1.5
    c: DistanceY(g8,g13) = 0.65
    c: DistanceY(g15,g-4) = 2.2
    c: DistanceY(g10,g10) = 2.2
FEATURE [PartDesign::Pad] Pad134
  BaseFeature = -> Pad133
  Direction = (0,0,-1)
  Length = 0.8
  Length2 = 10
  Profile = -> Sketch196
  ReferenceAxis = -> Sketch196 [N_Axis]
  Refine = true
  Suppressed = false
  Type = 0
FEATURE [Sketcher::SketchObject] Sketch197
  ArcFitTolerance = 1e-06
  AttachmentSupport = -> [Pad134]
  ExternalGeometry = -> [Pad134]
  FullyConstrained = true
  MakeInternals = false
  MapMode = 5
  Placement = pos=(0,0,0) rot=(1,0,0;3.14159rad)
  sketch-geometry (4):
    g0: LineSegment StartX=0.8 StartY=-1.4 StartZ=0 EndX=0.8 EndY=-7.3 EndZ=0
    g1: LineSegment StartX=0.8 StartY=-7.3 StartZ=0 EndX=7.2 EndY=-7.3 EndZ=0
    g2: LineSegment StartX=7.2 StartY=-7.3 StartZ=0 EndX=7.2 EndY=-1.4 EndZ=0
    g3: LineSegment StartX=7.2 StartY=-1.4 StartZ=0 EndX=0.8 EndY=-1.4 EndZ=0
  constraints (13):
    c: Coincident(g0,g1)
    c: Coincident(g1,g2)
    c: Coincident(g2,g3)
    c: Coincident(g3,g0)
    c: Vertical(g0)
    c: Vertical(g2)
    c: Horizontal(g1)
    c: Horizontal(g3)
    c: DistanceX(g3,g3) = 6.4
    c: DistanceX(g-3,g-3) = 8.2
    c: DistanceX(g-3,g0) = 0.9
    c: PointOnObject(g2,g-3)
    c: PointOnObject(g1,g-4)
FEATURE [PartDesign::Pad] Pad135
  BaseFeature = -> Pad134
  Direction = (0,0,-1)
  Length = 0.5
  Length2 = 10
  Profile = -> Sketch197
  ReferenceAxis = -> Sketch197 [N_Axis]
  Refine = true
  Suppressed = false
  Type = 0
FEATURE [Sketcher::SketchObject] Sketch198
  ArcFitTolerance = 1e-06
  AttachmentSupport = -> [Pad135]
  ExternalGeometry = -> [Pad135]
  FullyConstrained = true
  MakeInternals = false
  MapMode = 5
  Placement = pos=(0,0,-0.5) rot=(1,0,0;3.14159rad)
  sketch-geometry (8):
    g0: LineSegment StartX=5.75 StartY=-4.7 StartZ=0 EndX=5.75 EndY=-7.3 EndZ=0
    g1: LineSegment StartX=5.75 StartY=-7.3 StartZ=0 EndX=6.65 EndY=-7.3 EndZ=0
    g2: LineSegment StartX=6.65 StartY=-7.3 StartZ=0 EndX=6.65 EndY=-4.7 EndZ=0
    g3: LineSegment StartX=6.65 StartY=-4.7 StartZ=0 EndX=5.75 EndY=-4.7 EndZ=0
    g4: LineSegment StartX=2.25 StartY=-4.7 StartZ=0 EndX=1.35 EndY=-4.7 EndZ=0
    g5: LineSegment StartX=1.35 StartY=-4.7 StartZ=0 EndX=1.35 EndY=-7.3 EndZ=0
    g6: LineSegment StartX=1.35 StartY=-7.3 StartZ=0 EndX=2.25 EndY=-7.3 EndZ=0
    g7: LineSegment StartX=2.25 StartY=-7.3 StartZ=0 EndX=2.25 EndY=-4.7 EndZ=0
  constraints (25):
    c: Coincident(g0,g1)
    c: Coincident(g1,g2)
    c: Coincident(g2,g3)
    c: Coincident(g3,g0)
    c: Vertical(g0)
    c: Vertical(g2)
    c: Horizontal(g1)
    c: Horizontal(g3)
    c: DistanceX(g3,g3) = 0.9
    c: DistanceY(g0,g0) = 2.6
    c: PointOnObject(g1,g-4)
    c: DistanceX(g1,g-4) = 0.55
    c: DistanceX(g-4,g-4) = 6.4
    c: Coincident(g4,g5)
    c: Coincident(g5,g6)
    c: Coincident(g6,g7)
    c: Coincident(g7,g4)
    c: Horizontal(g4)
    c: Horizontal(g6)
    c: Vertical(g5)
    c: Vertical(g7)
    c: DistanceX(g4,g4) = 0.9
    c: DistanceY(g7,g7) = 2.6
    c: PointOnObject(g6,g-4)
    c: DistanceX(g-4,g5) = 0.55
FEATURE [PartDesign::Pad] Pad136
  BaseFeature = -> Pad135
  Direction = (0,0,-1)
  Length = 2.5
  Length2 = 10
  Profile = -> Sketch198
  ReferenceAxis = -> Sketch198 [N_Axis]
  Refine = true
  Suppressed = false
  Type = 0
FEATURE [Sketcher::SketchObject] Sketch199
  ArcFitTolerance = 1e-06
  AttachmentSupport = -> [Pad136]
  ExternalGeometry = -> [Pad136]
  FullyConstrained = true
  MakeInternals = false
  MapMode = 5
  Placement = pos=(6.65,0,0) rot=(0.57735,0.57735,0.57735;2.0944rad)
  sketch-geometry (3):
    g0: LineSegment StartX=4.7 StartY=-3 StartZ=0 EndX=5.2 EndY=-3 EndZ=0
    g1: LineSegment StartX=5.2 StartY=-3 StartZ=0 EndX=4.7 EndY=-0.8 EndZ=0
    g2: LineSegment StartX=4.7 StartY=-0.8 StartZ=0 EndX=4.7 EndY=-3 EndZ=0
  constraints (7):
    c: Coincident(g0,g-4)
    c: PointOnObject(g0,g-4)
    c: Coincident(g1,g0)
    c: Coincident(g1,g-3)
    c: Coincident(g2,g1)
    c: Coincident(g2,g0)
    c: DistanceX(g0,g0) = 0.5
FEATURE [PartDesign::Pocket] Pocket089
  BaseFeature = -> Pad136
  Direction = (-1,0,0)
  Length = 5.3
  Length2 = 5
  Profile = -> Sketch199
  ReferenceAxis = -> Sketch199 [N_Axis]
  Refine = true
  Suppressed = false
  Type = 0
FEATURE [Sketcher::SketchObject] Sketch200
  ArcFitTolerance = 1e-06
  AttachmentSupport = -> [Pocket089]
  ExternalGeometry = -> [Pocket089]
  FullyConstrained = true
  MakeInternals = false
  MapMode = 5
  Placement = pos=(0,0,-0.5) rot=(1,0,0;3.14159rad)
  sketch-geometry (4):
    g0: LineSegment StartX=1.7 StartY=-3.23887 StartZ=0 EndX=6.3 EndY=-3.23887 EndZ=0
    g1: LineSegment StartX=6.3 StartY=-3.23887 StartZ=0 EndX=6.3 EndY=-2.73887 EndZ=0
    g2: LineSegment StartX=6.3 StartY=-2.73887 StartZ=0 EndX=1.7 EndY=-2.73887 EndZ=0
    g3: LineSegment StartX=1.7 StartY=-2.73887 StartZ=0 EndX=1.7 EndY=-3.23887 EndZ=0
  constraints (10):
    c: Coincident(g0,g1)
    c: Coincident(g1,g2)
    c: Coincident(g2,g3)
    c: Coincident(g3,g0)
    c: Horizontal(g2)
    c: Vertical(g1)
    c: Vertical(g3)
    c: DistanceY(g3,g3) = 0.5
    c: Coincident(g0,g-5)
    c: Coincident(g0,g-4)
FEATURE [PartDesign::Pad] Pad137
  BaseFeature = -> Pocket089
  Direction = (0,0,-1)
  Length = 2.5
  Length2 = 10
  Profile = -> Sketch200
  ReferenceAxis = -> Sketch200 [N_Axis]
  Refine = true
  Suppressed = false
  Type = 0
FEATURE [Sketcher::SketchObject] Sketch201
  ArcFitTolerance = 1e-06
  AttachmentSupport = -> [Pad137]
  ExternalGeometry = -> [Pad137]
  FullyConstrained = true
  MakeInternals = false
  MapMode = 5
  Placement = pos=(1.26509e-11,3.23887,0) rot=(0,0.707107,0.707107;3.14159rad)
  sketch-geometry (6):
    g0: LineSegment StartX=-1.7 StartY=-3 StartZ=0 EndX=-2.2 EndY=-3 EndZ=0
    g1: LineSegment StartX=-6.3 StartY=-3 StartZ=0 EndX=-5.8 EndY=-3 EndZ=0
    g2: LineSegment StartX=-6.3 StartY=-3 StartZ=0 EndX=-6.3 EndY=-0.5 EndZ=0
    g3: LineSegment StartX=-1.7 StartY=-3 StartZ=0 EndX=-1.7 EndY=-0.5 EndZ=0
    g4: LineSegment StartX=-1.7 StartY=-0.5 StartZ=0 EndX=-2.2 EndY=-3 EndZ=0
    g5: LineSegment StartX=-5.8 StartY=-3 StartZ=0 EndX=-6.3 EndY=-0.5 EndZ=0
  constraints (15):
    c: DistanceX(g-3,g-3) = 4.6
    c: Coincident(g0,g-5)
    c: PointOnObject(g0,g-3)
    c: Coincident(g1,g-4)
    c: PointOnObject(g1,g-3)
    c: Coincident(g2,g1)
    c: Coincident(g2,g-6)
    c: Coincident(g3,g0)
    c: Coincident(g3,g-6)
    c: Coincident(g4,g3)
    c: Coincident(g4,g0)
    c: Coincident(g5,g1)
    c: Coincident(g5,g2)
    c: DistanceX(g0,g0) = 0.5
    c: DistanceX(g1,g1) = 0.5
FEATURE [PartDesign::Pocket] Pocket090
  BaseFeature = -> Pad137
  Direction = (-3.906e-12,-1,2e-16)
  Length = 0.5
  Length2 = 5
  Profile = -> Sketch201
  ReferenceAxis = -> Sketch201 [N_Axis]
  Refine = true
  Suppressed = false
  Type = 0
FEATURE [Sketcher::SketchObject] Sketch202
  ArcFitTolerance = 1e-06
  AttachmentSupport = -> [Pocket090]
  ExternalGeometry = -> [Pocket090]
  FullyConstrained = true
  MakeInternals = false
  MapMode = 5
  Placement = pos=(0,0,-0.5) rot=(1,0,0;3.14159rad)
  sketch-geometry (4):
    g0: LineSegment StartX=1.7 StartY=-2.73887 StartZ=0 EndX=6.3 EndY=-2.73887 EndZ=0
    g1: LineSegment StartX=6.3 StartY=-2.73887 StartZ=0 EndX=5.8 EndY=-1.4 EndZ=0
    g2: LineSegment StartX=1.7 StartY=-2.73887 StartZ=0 EndX=2.2 EndY=-1.4 EndZ=0
    g3: LineSegment StartX=2.2 StartY=-1.4 StartZ=0 EndX=5.8 EndY=-1.4 EndZ=0
  constraints (12):
    c: Coincident(g0,g-4)
    c: Coincident(g0,g-3)
    c: Coincident(g1,g-3)
    c: PointOnObject(g1,g-5)
    c: Coincident(g2,g-4)
    c: PointOnObject(g2,g-5)
    c: Coincident(g3,g2)
    c: Coincident(g3,g1)
    c: DistanceX(g-4,g-3) = 3.6
    c: DistanceX(g2,g1) = 3.6
    c: DistanceX(g0,g0) = 4.6
    c: DistanceX(g0,g2) = 0.5
FEATURE [PartDesign::Pad] Pad138
  BaseFeature = -> Pocket090
  Direction = (0,0,-1)
  Length = 2.25
  Length2 = 10
  Profile = -> Sketch202
  ReferenceAxis = -> Sketch202 [N_Axis]
  Refine = true
  Suppressed = false
  Type = 0
FEATURE [Sketcher::SketchObject] Sketch203
  ArcFitTolerance = 1e-06
  AttachmentSupport = -> [Pad138]
  ExternalGeometry = -> [Pad138]
  FullyConstrained = true
  MakeInternals = false
  MapMode = 5
  Placement = pos=(9.9689e-12,2.73887,0) rot=(0,0.707107,0.707107;3.14159rad)
  sketch-geometry (6):
    g0: LineSegment StartX=-1.7 StartY=-0.5 StartZ=0 EndX=-1.7 EndY=-2.75 EndZ=0
    g1: LineSegment StartX=-1.7 StartY=-2.75 StartZ=0 EndX=-2.15 EndY=-2.75 EndZ=0
    g2: LineSegment StartX=-2.15 StartY=-2.75 StartZ=0 EndX=-1.7 EndY=-0.5 EndZ=0
    g3: LineSegment StartX=-5.85 StartY=-2.75 StartZ=0 EndX=-6.3 EndY=-2.75 EndZ=0
    g4: LineSegment StartX=-6.3 StartY=-2.75 StartZ=0 EndX=-6.3 EndY=-0.5 EndZ=0
    g5: LineSegment StartX=-6.3 StartY=-0.5 StartZ=0 EndX=-5.85 EndY=-2.75 EndZ=0
  constraints (12):
    c: Coincident(g0,g-4)
    c: Coincident(g0,g-4)
    c: Coincident(g1,g0)
    c: Coincident(g1,g-3)
    c: Coincident(g2,g1)
    c: Coincident(g2,g0)
    c: Coincident(g3,g-5)
    c: Coincident(g3,g-6)
    c: Coincident(g4,g3)
    c: Coincident(g4,g-6)
    c: Coincident(g5,g4)
    c: Coincident(g5,g3)
FEATURE [PartDesign::Pocket] Pocket091
  BaseFeature = -> Pad138
  Direction = (-3.6398e-12,-1,2e-16)
  Length = 1.3
  Length2 = 5
  Profile = -> Sketch203
  ReferenceAxis = -> Sketch203 [N_Axis]
  Refine = true
  Suppressed = false
  Type = 0
FEATURE [Sketcher::SketchObject] Sketch204
  ArcFitTolerance = 1e-06
  AttachmentSupport = -> [Pocket091]
  ExternalGeometry = -> [Pocket091]
  FullyConstrained = true
  MakeInternals = false
  MapMode = 5
  Placement = pos=(7.2,0,0) rot=(0.57735,0.57735,0.57735;2.0944rad)
  sketch-geometry (3):
    g0: LineSegment StartX=2.3 StartY=-2.75 StartZ=0 EndX=1.4 EndY=-2.75 EndZ=0
    g1: LineSegment StartX=1.4 StartY=-2.75 StartZ=0 EndX=1.4 EndY=-0.5 EndZ=0
    g2: LineSegment StartX=2.3 StartY=-2.75 StartZ=0 EndX=1.4 EndY=-0.5 EndZ=0
  constraints (7):
    c: PointOnObject(g0,g-4)
    c: Coincident(g0,g-6)
    c: Coincident(g1,g0)
    c: Coincident(g1,g-3)
    c: Coincident(g2,g0)
    c: Coincident(g2,g1)
    c: DistanceX(g0,g0) = 0.9
FEATURE [PartDesign::Pocket] Pocket092
  BaseFeature = -> Pocket091
  Direction = (-1,0,0)
  Length = 6
  Length2 = 5
  Profile = -> Sketch204
  ReferenceAxis = -> Sketch204 [N_Axis]
  Refine = true
  Suppressed = false
  Type = 0
FEATURE [Sketcher::SketchObject] Sketch205
  ArcFitTolerance = 1e-06
  AttachmentOffset = pos=(0,0,-2.35) rot=(0,0,1;0rad)
  AttachmentSupport = -> [Pocket092]
  ExternalGeometry = -> [Pocket092]
  FullyConstrained = true
  MakeInternals = false
  MapMode = 5
  Placement = pos=(4.85,0,0) rot=(0.57735,0.57735,0.57735;2.0944rad)
  sketch-geometry (3):
    g0: ArcOfCircle CenterX=1.61334 CenterY=-2.02302 CenterZ=0 NormalX=0 NormalY=0 NormalZ=1 AngleXU=0 Radius=1 StartAngle=4.4974 EndAngle=5.46927
    g1: LineSegment StartX=2.3 StartY=-2.75 StartZ=0 EndX=1.4 EndY=-0.5 EndZ=0
    g2: LineSegment StartX=1.4 StartY=-0.5 StartZ=0 EndX=1.4 EndY=-3 EndZ=0
  constraints (8):
    c: Coincident(g0,g-3)
    c: PointOnObject(g0,g-4)
    c: Coincident(g1,g0)
    c: Coincident(g1,g-5)
    c: Coincident(g2,g1)
    c: Coincident(g2,g0)
    c: Radius(g0) = 1
    c: DistanceY(g-6,g0) = 0
FEATURE [PartDesign::Pad] Pad139
  BaseFeature = -> Pocket092
  Direction = (1,0,0)
  Length = 1.7
  Length2 = 10
  Profile = -> Sketch205
  ReferenceAxis = -> Sketch205 [N_Axis]
  Refine = true
  Reversed = true
  Suppressed = false
  Type = 0
FEATURE [PartDesign::Fillet] Fillet008
  Base = -> Pad139 [Edge33,Edge34,Edge30,Edge45,Edge44,Edge6,Edge8,Edge1,Edge2]
  BaseFeature = -> Pad139
  Radius = 0.2
  Refine = true
  SupportTransform = false
  Suppressed = false
  UseAllEdges = false
FEATURE [Sketcher::SketchObject] Sketch206
  ArcFitTolerance = 1e-06
  AttachmentSupport = -> [Fillet008]
  ExternalGeometry = -> [Fillet008]
  FullyConstrained = true
  MakeInternals = false
  MapMode = 5
  Placement = pos=(0,0,-0.8) rot=(1,0,0;3.14159rad)
  sketch-geometry (8):
    g0: LineSegment StartX=1.35 StartY=-3.52885 StartZ=0 EndX=0.4 EndY=-3.75756 EndZ=0
    g1: LineSegment StartX=0.4 StartY=-3.75756 StartZ=0 EndX=0.4 EndY=-5.95756 EndZ=0
    g2: LineSegment StartX=0.4 StartY=-5.95756 StartZ=0 EndX=1.35 EndY=-6.36923 EndZ=0
    g3: LineSegment StartX=1.35 StartY=-3.52885 StartZ=0 EndX=1.35 EndY=-6.36923 EndZ=0
    g4: LineSegment StartX=7.6 StartY=-3.75756 StartZ=0 EndX=7.6 EndY=-5.95756 EndZ=0
    g5: LineSegment StartX=7.6 StartY=-5.95756 StartZ=0 EndX=6.65 EndY=-6.36923 EndZ=0
    g6: LineSegment StartX=7.6 StartY=-3.75756 StartZ=0 EndX=6.65 EndY=-3.52885 EndZ=0
    g7: LineSegment StartX=6.65 StartY=-3.52885 StartZ=0 EndX=6.65 EndY=-6.36923 EndZ=0
  constraints (20):
    c: Coincident(g1,g0)
    c: Coincident(g2,g1)
    c: Coincident(g3,g0)
    c: Coincident(g3,g2)
    c: Vertical(g3)
    c: Parallel(g0,g-3)
    c: Parallel(g2,g-7)
    c: PointOnObject(g-10,g3)
    c: Coincident(g-8,g1)
    c: Coincident(g0,g-9)
    c: Coincident(g4,g-16)
    c: Coincident(g4,g-15)
    c: Coincident(g5,g4)
    c: PointOnObject(g5,g-17)
    c: Coincident(g6,g4)
    c: Coincident(g7,g6)
    c: Coincident(g7,g5)
    c: Vertical(g7)
    c: Parallel(g-11,g6)
    c: Parallel(g5,g-14)
FEATURE [PartDesign::Pocket] Pocket093
  BaseFeature = -> Fillet008
  Direction = (0,0,1)
  Length = 0.3
  Length2 = 5
  Profile = -> Sketch206
  ReferenceAxis = -> Sketch206 [N_Axis]
  Refine = true
  Suppressed = false
  Type = 0
FEATURE [PartDesign::SubShapeBinder] Binder008
  BindCopyOnChange = 0
  BindMode = 2
  ClaimChildren = false
  Context = -> Part [Body014.Binder008.]
  Fuse = false
  MakeFace = true
  OffsetFill = false
  OffsetIntersection = false
  OffsetJoinType = 0
  OffsetOpenResult = false
  PartialLoad = false
  Refine = true
  Relative = true
  _Version = 2
FEATURE [Sketcher::SketchObject] Sketch207
  ArcFitTolerance = 1e-06
  AttachmentSupport = -> [Binder008]
  ExternalGeometry = -> [Binder008]
  FullyConstrained = true
  MakeInternals = false
  MapMode = 5
  Placement = pos=(0,0,-4.5) rot=(1,0,0;3.14159rad)
  sketch-geometry (4):
    g0: LineSegment StartX=20.3 StartY=-45.2611 StartZ=0 EndX=20.3 EndY=-43.8 EndZ=0
    g1: LineSegment StartX=20.3 StartY=-43.8 StartZ=0 EndX=15.7 EndY=-43.8 EndZ=0
    g2: LineSegment StartX=15.7 StartY=-43.8 StartZ=0 EndX=15.7 EndY=-45.2611 EndZ=0
    g3: LineSegment StartX=15.7 StartY=-45.2611 StartZ=0 EndX=20.3 EndY=-45.2611 EndZ=0
  constraints (10):
    c: Coincident(g0,g1)
    c: Coincident(g1,g2)
    c: Coincident(g2,g3)
    c: Coincident(g3,g0)
    c: Vertical(g0)
    c: Vertical(g2)
    c: Horizontal(g1)
    c: Horizontal(g3)
    c: Coincident(g0,g-8)
    c: Coincident(g1,g-10)
FEATURE [PartDesign::Pad] Pad140
  Direction = (0,0,-1)
  Length = 2
  Length2 = 10
  Profile = -> Sketch207
  ReferenceAxis = -> Sketch207 [N_Axis]
  Refine = true
  Suppressed = false
  Type = 0
FEATURE [Sketcher::SketchObject] Sketch208
  ArcFitTolerance = 1e-06
  AttachmentSupport = -> [Pad140]
  ExternalGeometry = -> [Pad140]
  FullyConstrained = true
  MakeInternals = false
  MapMode = 5
  Placement = pos=(0,43.8,0) rot=(1,0,0;1.5708rad)
  sketch-geometry (6):
    g0: LineSegment StartX=15.7 StartY=-6.5 StartZ=0 EndX=15.7 EndY=-4.5 EndZ=0
    g1: LineSegment StartX=16.25 StartY=-6.5 StartZ=0 EndX=15.7 EndY=-4.5 EndZ=0
    g2: LineSegment StartX=20.3 StartY=-4.5 StartZ=0 EndX=19.75 EndY=-6.5 EndZ=0
    g3: LineSegment StartX=15.7 StartY=-6.5 StartZ=0 EndX=16.25 EndY=-6.5 EndZ=0
    g4: LineSegment StartX=19.75 StartY=-6.5 StartZ=0 EndX=20.3 EndY=-6.5 EndZ=0
    g5: LineSegment StartX=20.3 StartY=-6.5 StartZ=0 EndX=20.3 EndY=-4.5 EndZ=0
  constraints (15):
    c: Coincident(g0,g-4)
    c: Coincident(g1,g0)
    c: DistanceX(g-3,g-3) = 4.6
    c: Coincident(g3,g0)
    c: Coincident(g3,g1)
    c: Horizontal(g3)
    c: Coincident(g4,g2)
    c: Coincident(g4,g-5)
    c: Horizontal(g4)
    c: Coincident(g5,g4)
    c: Coincident(g5,g2)
    c: DistanceX(g4,g4) = 0.55
    c: DistanceX(g3,g3) = 0.55
    c: Coincident(g2,g-5)
    c: Coincident(g0,g-4)
FEATURE [PartDesign::Pocket] Pocket094
  BaseFeature = -> Pad140
  Direction = (0,1,-2e-16)
  Length = 5
  Length2 = 5
  Profile = -> Sketch208
  ReferenceAxis = -> Sketch208 [N_Axis]
  Refine = true
  Suppressed = false
  Type = 0
FEATURE [Sketcher::SketchObject] Sketch209
  ArcFitTolerance = 1e-06
  AttachmentOffset = pos=(0,0,-2) rot=(0,0,1;0rad)
  AttachmentSupport = -> [Pocket094]
  ExternalGeometry = -> [Pocket094]
  FullyConstrained = true
  MakeInternals = false
  MapMode = 5
  Placement = pos=(0,0,-4.5) rot=(1,0,0;3.14159rad)
  sketch-geometry (6):
    g0: LineSegment StartX=19.55 StartY=-43.8 StartZ=0 EndX=16.45 EndY=-43.8 EndZ=0
    g1: LineSegment StartX=16.45 StartY=-43.8 StartZ=0 EndX=16.6 EndY=-41.6 EndZ=0
    g2: LineSegment StartX=16.6 StartY=-41.6 StartZ=0 EndX=16.9 EndY=-41.25 EndZ=0
    g3: LineSegment StartX=16.9 StartY=-41.25 StartZ=0 EndX=19.1 EndY=-41.25 EndZ=0
    g4: LineSegment StartX=19.1 StartY=-41.25 StartZ=0 EndX=19.4 EndY=-41.6 EndZ=0
    g5: LineSegment StartX=19.4 StartY=-41.6 StartZ=0 EndX=19.55 EndY=-43.8 EndZ=0
  constraints (18):
    c: PointOnObject(g0,g-3)
    c: PointOnObject(g0,g-3)
    c: DistanceX(g0,g-3) = 0.2
    c: DistanceX(g-3,g0) = 0.2
    c: Coincident(g1,g0)
    c: Coincident(g2,g1)
    c: Coincident(g3,g2)
    c: Horizontal(g3)
    c: Coincident(g4,g3)
    c: Coincident(g5,g4)
    c: Coincident(g5,g0)
    c: DistanceX(g-3,g1) = 0.35
    c: DistanceX(g4,g-3) = 0.35
    c: DistanceY(g0,g1) = 2.2
    c: DistanceY(g0,g4) = 2.2
    c: DistanceY(g4,g3) = 0.35
    c: DistanceX(g3,g4) = 0.3
    c: DistanceX(g1,g2) = 0.3
FEATURE [PartDesign::Pad] Pad141
  BaseFeature = -> Pocket094
  Direction = (0,0,-1)
  Length = 1.8
  Length2 = 10
  Profile = -> Sketch209
  ReferenceAxis = -> Sketch209 [N_Axis]
  Refine = true
  Suppressed = false
  Type = 0
FEATURE [Sketcher::SketchObject] Sketch210
  ArcFitTolerance = 1e-06
  AttachmentSupport = -> [Pad141]
  ExternalGeometry = -> [Pad141]
  FullyConstrained = true
  MakeInternals = false
  MapMode = 5
  Placement = pos=(0,0,-6.3) rot=(1,0,0;3.14159rad)
  sketch-geometry (8):
    g0: LineSegment StartX=18.3 StartY=-42.3 StartZ=0 EndX=18.3 EndY=-42.2 EndZ=0
    g1: LineSegment StartX=18.3 StartY=-42.2 StartZ=0 EndX=17.7 EndY=-42.2 EndZ=0
    g2: LineSegment StartX=17.7 StartY=-42.2 StartZ=0 EndX=17.7 EndY=-42.3 EndZ=0
    g3: LineSegment StartX=17.7 StartY=-42.3 StartZ=0 EndX=18.3 EndY=-42.3 EndZ=0
    g4: LineSegment StartX=18.3 StartY=-42.1 StartZ=0 EndX=18.3 EndY=-42 EndZ=0
    g5: LineSegment StartX=18.3 StartY=-42 StartZ=0 EndX=17.7 EndY=-42 EndZ=0
    g6: LineSegment StartX=17.7 StartY=-42 StartZ=0 EndX=17.7 EndY=-42.1 EndZ=0
    g7: LineSegment StartX=17.7 StartY=-42.1 StartZ=0 EndX=18.3 EndY=-42.1 EndZ=0
  constraints (25):
    c: Coincident(g0,g1)
    c: Coincident(g1,g2)
    c: Coincident(g2,g3)
    c: Coincident(g3,g0)
    c: Vertical(g0)
    c: Vertical(g2)
    c: Horizontal(g1)
    c: Horizontal(g3)
    c: Coincident(g4,g5)
    c: Coincident(g5,g6)
    c: Coincident(g6,g7)
    c: Coincident(g7,g4)
    c: Vertical(g4)
    c: Vertical(g6)
    c: Horizontal(g5)
    c: Horizontal(g7)
    c: DistanceX(g3,g3) = 0.6
    c: DistanceX(g5,g5) = 0.6
    c: DistanceX(g6,g1) = 0
    c: DistanceY(g1,g6) = 0.1
    c: DistanceY(g2,g2) = 0.1
    c: DistanceY(g6,g6) = 0.1
    c: DistanceX(g-3,g5) = 1.1
    c: DistanceX(g4,g-4) = 1.1
    c: DistanceY(g5,g-3) = 0.4
FEATURE [PartDesign::Pad] Pad142
  BaseFeature = -> Pad141
  Direction = (0,0,-1)
  Length = 0.2
  Length2 = 10
  Profile = -> Sketch210
  ReferenceAxis = -> Sketch210 [N_Axis]
  Refine = true
  Suppressed = false
  Type = 0
FEATURE [Sketcher::SketchObject] Sketch211
  ArcFitTolerance = 1e-06
  AttachmentSupport = -> [Pad142]
  ExternalGeometry = -> [Pad142]
  FullyConstrained = true
  MakeInternals = false
  MapMode = 5
  Placement = pos=(0,0,-6.3) rot=(1,0,0;3.14159rad)
  sketch-geometry (4):
    g0: LineSegment StartX=18.3 StartY=-43.8 StartZ=0 EndX=18.3 EndY=-43 EndZ=0
    g1: LineSegment StartX=18.3 StartY=-43 StartZ=0 EndX=17.7 EndY=-43 EndZ=0
    g2: LineSegment StartX=17.7 StartY=-43 StartZ=0 EndX=17.7 EndY=-43.8 EndZ=0
    g3: LineSegment StartX=17.7 StartY=-43.8 StartZ=0 EndX=18.3 EndY=-43.8 EndZ=0
  constraints (13):
    c: Coincident(g0,g1)
    c: Coincident(g1,g2)
    c: Coincident(g2,g3)
    c: Coincident(g3,g0)
    c: Vertical(g0)
    c: Vertical(g2)
    c: Horizontal(g1)
    c: Horizontal(g3)
    c: PointOnObject(g0,g-3)
    c: DistanceX(g1,g1) = 0.6
    c: DistanceY(g2,g2) = 0.8
    c: DistanceX(g-5,g2) = 1.25
    c: DistanceX(g0,g-4) = 1.25
FEATURE [PartDesign::Pad] Pad143
  BaseFeature = -> Pad142
  Direction = (0,0,-1)
  Length = 0.5
  Length2 = 10
  Profile = -> Sketch211
  ReferenceAxis = -> Sketch211 [N_Axis]
  Refine = true
  Suppressed = false
  Type = 0
FEATURE [Sketcher::SketchObject] Sketch212
  ArcFitTolerance = 1e-06
  AttachmentSupport = -> [Pad143]
  ExternalGeometry = -> [Pad143]
  FullyConstrained = true
  MakeInternals = false
  MapMode = 5
  Placement = pos=(17.7,0,0) rot=(0.57735,-0.57735,-0.57735;2.0944rad)
  sketch-geometry (3):
    g0: LineSegment StartX=-43.8 StartY=-6.5 StartZ=0 EndX=-43.2 EndY=-6.8 EndZ=0
    g1: LineSegment StartX=-43.2 StartY=-6.8 StartZ=0 EndX=-43.8 EndY=-6.8 EndZ=0
    g2: LineSegment StartX=-43.8 StartY=-6.8 StartZ=0 EndX=-43.8 EndY=-6.5 EndZ=0
  constraints (7):
    c: Coincident(g0,g-3)
    c: PointOnObject(g0,g-4)
    c: Coincident(g1,g0)
    c: Coincident(g1,g-4)
    c: Coincident(g2,g1)
    c: Coincident(g2,g0)
    c: DistanceX(g0,g-4) = 0.2
FEATURE [PartDesign::Pocket] Pocket095
  BaseFeature = -> Pad143
  Direction = (1,0,0)
  Length = 1
  Length2 = 5
  Profile = -> Sketch212
  ReferenceAxis = -> Sketch212 [N_Axis]
  Refine = true
  Suppressed = false
  Type = 0
FEATURE [PartDesign::SubShapeBinder] Binder009
  BindCopyOnChange = 0
  BindMode = 0
  ClaimChildren = false
  Context = -> Part [Body015.Binder009.]
  Fuse = false
  MakeFace = true
  OffsetFill = false
  OffsetIntersection = false
  OffsetJoinType = 0
  OffsetOpenResult = false
  PartialLoad = false
  Refine = true
  Relative = true
  Support = -> [Body010[Fillet006.Face6]]
  _Version = 2
FEATURE [Sketcher::SketchObject] Sketch213
  ArcFitTolerance = 1e-06
  AttachmentSupport = -> [Binder009]
  ExternalGeometry = -> [Binder009]
  FullyConstrained = true
  MakeInternals = false
  MapMode = 5
  Placement = pos=(0,0,0) rot=(1,0,0;1.5708rad)
  sketch-geometry (4):
    g0: LineSegment StartX=12.75 StartY=-6 StartZ=0 EndX=23.25 EndY=-6 EndZ=0
    g1: LineSegment StartX=12.75 StartY=-6 StartZ=0 EndX=12.75 EndY=-2 EndZ=0
    g2: LineSegment StartX=12.75 StartY=-2 StartZ=0 EndX=23.25 EndY=-2 EndZ=0
    g3: LineSegment StartX=23.25 StartY=-2 StartZ=0 EndX=23.25 EndY=-6 EndZ=0
  constraints (11):
    c: Coincident(g0,g-7)
    c: Coincident(g0,g-8)
    c: DistanceX(g0,g0) = 10.5
    c: Coincident(g1,g0)
    c: Vertical(g1)
    c: DistanceY(g1,g1) = 4
    c: Coincident(g2,g1)
    c: Horizontal(g2)
    c: Coincident(g3,g2)
    c: Coincident(g3,g0)
    c: Vertical(g3)
FEATURE [PartDesign::Pad] Pad144
  Direction = (0,-1,2e-16)
  Length = 10
  Length2 = 10
  Profile = -> Sketch213
  ReferenceAxis = -> Sketch213 [N_Axis]
  Refine = true
  Suppressed = false
  Type = 0
FEATURE [Sketcher::SketchObject] Sketch214
  ArcFitTolerance = 1e-06
  AttachmentSupport = -> [Pad144]
  ExternalGeometry = -> [Pad144]
  FullyConstrained = true
  MakeInternals = false
  MapMode = 5
  Placement = pos=(0,-4e-16,-2) rot=(0,0,1;0rad)
  sketch-geometry (4):
    g0: LineSegment StartX=15 StartY=-2.25 StartZ=0 EndX=15 EndY=-8.25 EndZ=0
    g1: LineSegment StartX=15 StartY=-8.25 StartZ=0 EndX=21 EndY=-8.25 EndZ=0
    g2: LineSegment StartX=21 StartY=-8.25 StartZ=0 EndX=21 EndY=-2.25 EndZ=0
    g3: LineSegment StartX=21 StartY=-2.25 StartZ=0 EndX=15 EndY=-2.25 EndZ=0
  constraints (13):
    c: Coincident(g0,g1)
    c: Coincident(g1,g2)
    c: Coincident(g2,g3)
    c: Coincident(g3,g0)
    c: Vertical(g0)
    c: Vertical(g2)
    c: Horizontal(g1)
    c: Horizontal(g3)
    c: DistanceX(g3,g3) = 6
    c: DistanceX(g-3,g0) = 2.25
    c: DistanceX(g-4,g-4) = 10.5
    c: DistanceY(g0,g0) = 6
    c: DistanceY(g2,g-3) = 2.25
FEATURE [PartDesign::Pocket] Pocket096
  BaseFeature = -> Pad144
  Direction = (0,0,-1)
  Length = 2
  Length2 = 5
  Profile = -> Sketch214
  ReferenceAxis = -> Sketch214 [N_Axis]
  Refine = true
  Suppressed = false
  Type = 0
FEATURE [Sketcher::SketchObject] Sketch215
  ArcFitTolerance = 1e-06
  AttachmentSupport = -> [Pocket096]
  ExternalGeometry = -> [Pocket096]
  FullyConstrained = true
  MakeInternals = false
  MapMode = 5
  Placement = pos=(0,0,-4) rot=(0,0,1;0rad)
  sketch-geometry (1):
    g0: Circle CenterX=18 CenterY=-5.25 CenterZ=0 NormalX=0 NormalY=0 NormalZ=1 AngleXU=0 Radius=2.4
  constraints (3):
    c: Diameter(g0) = 4.8
    c: DistanceX(g-3,g0) = 3
    c: DistanceY(g0,g-3) = 3
FEATURE [PartDesign::Pad] Pad145
  BaseFeature = -> Pocket096
  Direction = (0,0,1)
  Length = 4.2
  Length2 = 10
  Profile = -> Sketch215
  ReferenceAxis = -> Sketch215 [N_Axis]
  Refine = true
  Suppressed = false
  Type = 0
FEATURE [Sketcher::SketchObject] Sketch216
  ArcFitTolerance = 1e-06
  AttachmentSupport = -> [Pad145]
  ExternalGeometry = -> [Pad145]
  FullyConstrained = true
  MakeInternals = false
  MapMode = 5
  Placement = pos=(0,0,0.2) rot=(0,0,1;0rad)
  sketch-geometry (1):
    g0: Circle CenterX=18 CenterY=-5.25 CenterZ=0 NormalX=0 NormalY=0 NormalZ=1 AngleXU=0 Radius=0.75
  constraints (2):
    c: Coincident(g0,g-3)
    c: Radius(g0) = 0.75
FEATURE [PartDesign::Pocket] Pocket097
  BaseFeature = -> Pad145
  Direction = (0,0,-1)
  Length = 7
  Length2 = 5
  Profile = -> Sketch216
  ReferenceAxis = -> Sketch216 [N_Axis]
  Refine = true
  Suppressed = false
  Type = 0
FEATURE [Sketcher::SketchObject] Sketch217
  ArcFitTolerance = 1e-06
  AttachmentSupport = -> [Pocket097]
  ExternalGeometry = -> [Pocket097]
  FullyConstrained = true
  MakeInternals = false
  MapMode = 5
  Placement = pos=(0,-4e-16,-2) rot=(0,0,1;0rad)
  sketch-geometry (8):
    g0: LineSegment StartX=23.25 StartY=0 StartZ=0 EndX=23.25 EndY=-24 EndZ=0
    g1: LineSegment StartX=23.25 StartY=-24 StartZ=0 EndX=29.25 EndY=-24 EndZ=0
    g2: LineSegment StartX=29.25 StartY=-24 StartZ=0 EndX=29.25 EndY=0 EndZ=0
    g3: LineSegment StartX=29.25 StartY=0 StartZ=0 EndX=23.25 EndY=0 EndZ=0
    g4: LineSegment StartX=12.75 StartY=0 StartZ=0 EndX=6.75 EndY=0 EndZ=0
    g5: LineSegment StartX=6.75 StartY=0 StartZ=0 EndX=6.75 EndY=-24 EndZ=0
    g6: LineSegment StartX=6.75 StartY=-24 StartZ=0 EndX=12.75 EndY=-24 EndZ=0
    g7: LineSegment StartX=12.75 StartY=-24 StartZ=0 EndX=12.75 EndY=0 EndZ=0
  constraints (22):
    c: Coincident(g0,g1)
    c: Coincident(g1,g2)
    c: Coincident(g2,g3)
    c: Coincident(g3,g0)
    c: Vertical(g0)
    c: Vertical(g2)
    c: Horizontal(g1)
    c: Horizontal(g3)
    c: Coincident(g0,g-3)
    c: Coincident(g4,g5)
    c: Coincident(g5,g6)
    c: Coincident(g6,g7)
    c: Coincident(g7,g4)
    c: Horizontal(g4)
    c: Horizontal(g6)
    c: Vertical(g5)
    c: Vertical(g7)
    c: Coincident(g4,g-4)
    c: DistanceX(g1,g1) = 6
    c: DistanceX(g6,g6) = 6
    c: DistanceY(g5,g5) = 24
    c: DistanceY(g2,g2) = 24
FEATURE [PartDesign::Pad] Pad146
  BaseFeature = -> Pocket097
  Direction = (0,0,1)
  Length = 6
  Length2 = 10
  Profile = -> Sketch217
  ReferenceAxis = -> Sketch217 [N_Axis]
  Refine = true
  Reversed = true
  Suppressed = false
  Type = 0
FEATURE [Sketcher::SketchObject] Sketch218
  ArcFitTolerance = 1e-06
  AttachmentSupport = -> [Pad146]
  ExternalGeometry = -> [Pad146]
  FullyConstrained = true
  MakeInternals = false
  MapMode = 5
  Placement = pos=(0,0,-2) rot=(0,0,1;0rad)
  sketch-geometry (8):
    g0: LineSegment StartX=6.75 StartY=-10.9 StartZ=0 EndX=6.75 EndY=-34.8 EndZ=0
    g1: LineSegment StartX=6.75 StartY=-34.8 StartZ=0 EndX=12.75 EndY=-34.8 EndZ=0
    g2: LineSegment StartX=12.75 StartY=-34.8 StartZ=0 EndX=12.75 EndY=-10.9 EndZ=0
    g3: LineSegment StartX=12.75 StartY=-10.9 StartZ=0 EndX=6.75 EndY=-10.9 EndZ=0
    g4: LineSegment StartX=29.25 StartY=-10.9 StartZ=0 EndX=23.25 EndY=-10.9 EndZ=0
    g5: LineSegment StartX=23.25 StartY=-10.9 StartZ=0 EndX=23.25 EndY=-34.8 EndZ=0
    g6: LineSegment StartX=23.25 StartY=-34.8 StartZ=0 EndX=29.25 EndY=-34.8 EndZ=0
    g7: LineSegment StartX=29.25 StartY=-34.8 StartZ=0 EndX=29.25 EndY=-10.9 EndZ=0
  constraints (24):
    c: Coincident(g0,g1)
    c: Coincident(g1,g2)
    c: Coincident(g2,g3)
    c: Coincident(g3,g0)
    c: Vertical(g0)
    c: Vertical(g2)
    c: Horizontal(g1)
    c: Horizontal(g3)
    c: Coincident(g4,g5)
    c: Coincident(g5,g6)
    c: Coincident(g6,g7)
    c: Coincident(g7,g4)
    c: Horizontal(g4)
    c: Horizontal(g6)
    c: Vertical(g5)
    c: Vertical(g7)
    c: PointOnObject(g4,g-3)
    c: PointOnObject(g4,g-4)
    c: PointOnObject(g2,g-5)
    c: DistanceY(g4,g-3) = 10.9
    c: DistanceY(g0,g0) = 23.9
    c: DistanceY(g7,g7) = 23.9
    c: DistanceY(g0,g-6) = 10.9
    c: PointOnObject(g-6,g0)
FEATURE [PartDesign::Pad] Pad147
  BaseFeature = -> Pad146
  Direction = (0,0,1)
  Length = 5
  Length2 = 10
  Profile = -> Sketch218
  ReferenceAxis = -> Sketch218 [N_Axis]
  Refine = true
  Suppressed = false
  Type = 0
FEATURE [Sketcher::SketchObject] Sketch219
  ArcFitTolerance = 1e-06
  AttachmentSupport = -> [Pad147]
  ExternalGeometry = -> [Pad147]
  FullyConstrained = true
  MakeInternals = false
  MapMode = 5
  Placement = pos=(29.25,0,0) rot=(0.57735,0.57735,0.57735;2.0944rad)
  sketch-geometry (3):
    g0: ArcOfCircle CenterX=-35 CenterY=-1.99333 CenterZ=0 NormalX=0 NormalY=0 NormalZ=1 AngleXU=0 Radius=3 StartAngle=1.50408 EndAngle=6.28096
    g1: LineSegment StartX=-32 StartY=-2 StartZ=0 EndX=-34.8 EndY=-2 EndZ=0
    g2: LineSegment StartX=-34.8 StartY=-2 StartZ=0 EndX=-34.8 EndY=1 EndZ=0
  constraints (9):
    c: PointOnObject(g0,g-3)
    c: PointOnObject(g0,g-4)
    c: Diameter(g0) = 6
    c: DistanceY(g0,g-4) = 2
    c: DistanceX(g0,g-3) = 8
    c: Coincident(g1,g0)
    c: Coincident(g1,g-4)
    c: Coincident(g2,g1)
    c: Coincident(g2,g0)
FEATURE [PartDesign::Pad] Pad148
  BaseFeature = -> Pad147
  Direction = (1,0,0)
  Length = 22.5
  Length2 = 10
  Profile = -> Sketch219
  ReferenceAxis = -> Sketch219 [N_Axis]
  Refine = true
  Reversed = true
  Suppressed = false
  Type = 0
FEATURE [Sketcher::SketchObject] Sketch220
  ArcFitTolerance = 1e-06
  AttachmentSupport = -> [Pad148]
  ExternalGeometry = -> [Pad148]
  FullyConstrained = true
  MakeInternals = false
  MapMode = 5
  Placement = pos=(0,0,3) rot=(0,0,1;0rad)
  sketch-geometry (4):
    g0: LineSegment StartX=12.75 StartY=-32 StartZ=0 EndX=12.75 EndY=-38 EndZ=0
    g1: LineSegment StartX=12.75 StartY=-38 StartZ=0 EndX=23.25 EndY=-38 EndZ=0
    g2: LineSegment StartX=23.25 StartY=-38 StartZ=0 EndX=23.25 EndY=-32 EndZ=0
    g3: LineSegment StartX=23.25 StartY=-32 StartZ=0 EndX=12.75 EndY=-32 EndZ=0
  constraints (10):
    c: Coincident(g0,g1)
    c: Coincident(g1,g2)
    c: Coincident(g2,g3)
    c: Coincident(g3,g0)
    c: Vertical(g0)
    c: Vertical(g2)
    c: Horizontal(g1)
    c: Coincident(g0,g-5)
    c: Coincident(g2,g-5)
    c: DistanceY(g2,g2) = 6
FEATURE [PartDesign::Pocket] Pocket098
  BaseFeature = -> Pad148
  Direction = (0,0,-1)
  Length = 8
  Length2 = 5
  Profile = -> Sketch220
  ReferenceAxis = -> Sketch220 [N_Axis]
  Refine = true
  Suppressed = false
  Type = 0
FEATURE [Sketcher::SketchObject] Sketch221
  ArcFitTolerance = 1e-06
  AttachmentSupport = -> [Pocket098]
  ExternalGeometry = -> [Pocket098]
  FullyConstrained = true
  MakeInternals = false
  MapMode = 5
  Placement = pos=(6.75,0,0) rot=(0.57735,-0.57735,-0.57735;2.0944rad)
  sketch-geometry (5):
    g0: LineSegment StartX=36.5 StartY=0.60475 StartZ=0 EndX=34.8 EndY=1.58624 EndZ=0
    g1: LineSegment [constr] StartX=35 StartY=-1.99333 StartZ=0 EndX=38 EndY=-1.99333 EndZ=0
    g2: LineSegment [constr] StartX=35 StartY=-1.99333 StartZ=0 EndX=36.5 EndY=0.60475 EndZ=0
    g3: LineSegment StartX=34.8 StartY=1.58624 StartZ=0 EndX=34.8 EndY=1 EndZ=0
    g4: ArcOfCircle CenterX=35 CenterY=-1.99333 CenterZ=0 NormalX=0 NormalY=0 NormalZ=1 AngleXU=0 Radius=3 StartAngle=1.0472 EndAngle=1.63751
  constraints (14):
    c: PointOnObject(g0,g-3)
    c: PointOnObject(g0,g-4)
    c: Angle(g-4,g0) = 1.0472
    c: Coincident(g1,g-3)
    c: PointOnObject(g1,g-3)
    c: Horizontal(g1)
    c: Coincident(g2,g0)
    c: Angle(g1,g2) = 1.0472
    c: Coincident(g2,g1)
    c: Coincident(g3,g0)
    c: Coincident(g3,g-4)
    c: Coincident(g4,g3)
    c: Coincident(g4,g0)
    c: Tangent(g4,g-3)
FEATURE [PartDesign::Pad] Pad149
  BaseFeature = -> Pocket098
  Direction = (-1,0,0)
  Length = 22.5
  Length2 = 10
  Profile = -> Sketch221
  ReferenceAxis = -> Sketch221 [N_Axis]
  Refine = true
  Reversed = true
  Suppressed = false
  Type = 0
FEATURE [Sketcher::SketchObject] Sketch222
  ArcFitTolerance = 1e-06
  AttachmentSupport = -> [Pad149]
  ExternalGeometry = -> [Pad149]
  FullyConstrained = true
  MakeInternals = false
  MapMode = 5
  Placement = pos=(0,0,3) rot=(0,0,1;0rad)
  sketch-geometry (4):
    g0: LineSegment StartX=12.75 StartY=-32 StartZ=0 EndX=12.75 EndY=-38 EndZ=0
    g1: LineSegment StartX=12.75 StartY=-38 StartZ=0 EndX=23.25 EndY=-38 EndZ=0
    g2: LineSegment StartX=23.25 StartY=-38 StartZ=0 EndX=23.25 EndY=-32 EndZ=0
    g3: LineSegment StartX=23.25 StartY=-32 StartZ=0 EndX=12.75 EndY=-32 EndZ=0
  constraints (10):
    c: Coincident(g0,g1)
    c: Coincident(g1,g2)
    c: Coincident(g2,g3)
    c: Coincident(g3,g0)
    c: Vertical(g0)
    c: Vertical(g2)
    c: Horizontal(g1)
    c: Horizontal(g3)
    c: Coincident(g0,g-5)
    c: Coincident(g1,g-4)
FEATURE [PartDesign::Pocket] Pocket099
  BaseFeature = -> Pad149
  Direction = (0,0,-1)
  Length = 5
  Length2 = 5
  Profile = -> Sketch222
  ReferenceAxis = -> Sketch222 [N_Axis]
  Refine = true
  Suppressed = false
  Type = 0
FEATURE [Sketcher::SketchObject] Sketch223
  ArcFitTolerance = 1e-06
  AttachmentSupport = -> [Pocket099]
  ExternalGeometry = -> [Pocket099]
  FullyConstrained = true
  MakeInternals = false
  MapMode = 5
  Placement = pos=(29.25,0,0) rot=(0.57735,0.57735,0.57735;2.0944rad)
  sketch-geometry (4):
    g0: LineSegment [constr] StartX=-35 StartY=-1.99333 StartZ=0 EndX=-38 EndY=-1.99333 EndZ=0
    g1: LineSegment StartX=-34.8 StartY=1.58624 StartZ=0 EndX=-32.3513 EndY=3 EndZ=0
    g2: LineSegment StartX=-32.3513 StartY=3 StartZ=0 EndX=-34.8 EndY=3 EndZ=0
    g3: LineSegment StartX=-34.8 StartY=3 StartZ=0 EndX=-34.8 EndY=1.58624 EndZ=0
  constraints (11):
    c: Coincident(g0,g-4)
    c: PointOnObject(g0,g-4)
    c: Horizontal(g0)
    c: DistanceX(g0,g-3) = 38
    c: Coincident(g1,g-5)
    c: PointOnObject(g1,g-6)
    c: Coincident(g2,g1)
    c: Coincident(g2,g-6)
    c: Coincident(g3,g2)
    c: Coincident(g3,g1)
    c: Angle(g-7,g1) = 3.14159
FEATURE [PartDesign::Pocket] Pocket100
  BaseFeature = -> Pocket099
  Direction = (-1,0,0)
  Length = 23
  Length2 = 5
  Profile = -> Sketch223
  ReferenceAxis = -> Sketch223 [N_Axis]
  Refine = true
  Suppressed = false
  Type = 0
FEATURE [Sketcher::SketchObject] Sketch224
  ArcFitTolerance = 1e-06
  AttachmentSupport = -> [Pocket100]
  ExternalGeometry = -> [Pocket100]
  FullyConstrained = true
  MakeInternals = false
  MapMode = 5
  Placement = pos=(29.25,0,0) rot=(0.57735,0.57735,0.57735;2.0944rad)
  sketch-geometry (4):
    g0: Circle CenterX=-35 CenterY=-1.99333 CenterZ=0 NormalX=0 NormalY=0 NormalZ=1 AngleXU=0 Radius=0.8
    g1: LineSegment StartX=-24 StartY=-8 StartZ=0 EndX=-24 EndY=-5.5 EndZ=0
    g2: LineSegment StartX=-24 StartY=-5.5 StartZ=0 EndX=-17.1313 EndY=-8 EndZ=0
    g3: LineSegment StartX=-24 StartY=-8 StartZ=0 EndX=-17.1313 EndY=-8 EndZ=0
  constraints (10):
    c: Coincident(g0,g-3)
    c: Radius(g0) = 0.8
    c: Coincident(g2,g1)
    c: PointOnObject(g1,g-4)
    c: DistanceY(g1,g-4) = 3.5
    c: Coincident(g3,g1)
    c: Coincident(g3,g2)
    c: Horizontal(g3)
    c: Coincident(g1,g-4)
    c: Angle(g1,g2) = 1.22173
FEATURE [PartDesign::Pocket] Pocket101
  BaseFeature = -> Pocket100
  Direction = (-1,0,0)
  Length = 23
  Length2 = 5
  Profile = -> Sketch224
  ReferenceAxis = -> Sketch224 [N_Axis]
  Refine = true
  Suppressed = false
  Type = 0
FEATURE [Sketcher::SketchObject] Sketch225
  ArcFitTolerance = 1e-06
  AttachmentSupport = -> [Pocket101]
  ExternalGeometry = -> [Pocket101]
  FullyConstrained = true
  MakeInternals = false
  MapMode = 5
  Placement = pos=(0,0,-2) rot=(1,0,0;3.14159rad)
  sketch-geometry (5):
    g0: ArcOfCircle CenterX=9.75 CenterY=24 CenterZ=0 NormalX=0 NormalY=0 NormalZ=1 AngleXU=0 Radius=1.25 StartAngle=-9e-16 EndAngle=3.14159
    g1: ArcOfCircle CenterX=26.25 CenterY=24 CenterZ=0 NormalX=0 NormalY=0 NormalZ=1 AngleXU=0 Radius=1.25 StartAngle=1.7e-15 EndAngle=3.14159
    g2: LineSegment [constr] StartX=26.25 StartY=24 StartZ=0 EndX=26.25 EndY=25.25 EndZ=0
    g3: LineSegment StartX=25 StartY=24 StartZ=0 EndX=27.5 EndY=24 EndZ=0
    g4: LineSegment StartX=8.5 StartY=24 StartZ=0 EndX=11 EndY=24 EndZ=0
  constraints (19):
    c: PointOnObject(g0,g-4)
    c: PointOnObject(g0,g-4)
    c: PointOnObject(g1,g-3)
    c: PointOnObject(g1,g-3)
    c: PointOnObject(g0,g-4)
    c: PointOnObject(g1,g-3)
    c: Diameter(g0) = 2.5
    c: Diameter(g1) = 2.5
    c: DistanceX(g-4,g-4) = 6
    c: DistanceX(g-4,g0) = 3
    c: DistanceX(g-3,g1) = 3
    c: Coincident(g2,g1)
    c: PointOnObject(g2,g1)
    c: Vertical(g2)
    c: DistanceY(g2,g-5) = 6.75
    c: Coincident(g3,g1)
    c: Coincident(g3,g1)
    c: Coincident(g4,g0)
    c: Coincident(g4,g0)
FEATURE [PartDesign::Pad] Pad150
  BaseFeature = -> Pocket101
  Direction = (0,0,-1)
  Length = 3.5
  Length2 = 10
  Profile = -> Sketch225
  ReferenceAxis = -> Sketch225 [N_Axis]
  Refine = true
  Suppressed = false
  Type = 0
FEATURE [Sketcher::SketchObject] Sketch226
  ArcFitTolerance = 1e-06
  AttachmentSupport = -> [Pad150]
  ExternalGeometry = -> [Pad150]
  FullyConstrained = true
  MakeInternals = false
  MapMode = 5
  Placement = pos=(0,0,3) rot=(0,0,1;0rad)
  sketch-geometry (8):
    g0: LineSegment StartX=8.75 StartY=-10.9 StartZ=0 EndX=8.75 EndY=-32.3513 EndZ=0
    g1: LineSegment StartX=8.75 StartY=-32.3513 StartZ=0 EndX=10.75 EndY=-32.3513 EndZ=0
    g2: LineSegment StartX=10.75 StartY=-32.3513 StartZ=0 EndX=10.75 EndY=-10.9 EndZ=0
    g3: LineSegment StartX=10.75 StartY=-10.9 StartZ=0 EndX=8.75 EndY=-10.9 EndZ=0
    g4: LineSegment StartX=25.25 StartY=-10.9 StartZ=0 EndX=25.25 EndY=-32.3513 EndZ=0
    g5: LineSegment StartX=25.25 StartY=-32.3513 StartZ=0 EndX=27.25 EndY=-32.3513 EndZ=0
    g6: LineSegment StartX=27.25 StartY=-32.3513 StartZ=0 EndX=27.25 EndY=-10.9 EndZ=0
    g7: LineSegment StartX=27.25 StartY=-10.9 StartZ=0 EndX=25.25 EndY=-10.9 EndZ=0
  constraints (26):
    c: Coincident(g0,g1)
    c: Coincident(g1,g2)
    c: Coincident(g2,g3)
    c: Coincident(g3,g0)
    c: Vertical(g0)
    c: Vertical(g2)
    c: Horizontal(g1)
    c: Horizontal(g3)
    c: PointOnObject(g0,g-6)
    c: Coincident(g4,g5)
    c: Coincident(g5,g6)
    c: Coincident(g6,g7)
    c: Coincident(g7,g4)
    c: Vertical(g4)
    c: Vertical(g6)
    c: Horizontal(g5)
    c: Horizontal(g7)
    c: PointOnObject(g4,g-3)
    c: DistanceX(g-3,g-3) = 6
    c: DistanceX(g7,g7) = 2
    c: DistanceX(g-3,g4) = 2
    c: DistanceX(g6,g-3) = 2
    c: DistanceX(g3,g3) = 2
    c: DistanceX(g-6,g0) = 2
    c: PointOnObject(g1,g-7)
    c: PointOnObject(g5,g-5)
FEATURE [PartDesign::Pocket] Pocket102
  BaseFeature = -> Pad150
  Direction = (0,0,-1)
  Length = 3
  Length2 = 5
  Profile = -> Sketch226
  ReferenceAxis = -> Sketch226 [N_Axis]
  Refine = true
  Suppressed = false
  Type = 0
FEATURE [Sketcher::SketchObject] Sketch227
  ArcFitTolerance = 1e-06
  AttachmentSupport = -> [Pocket102]
  ExternalGeometry = -> [Pocket102]
  FullyConstrained = true
  MakeInternals = false
  MapMode = 5
  Placement = pos=(29.25,0,0) rot=(0.57735,0.57735,0.57735;2.0944rad)
  sketch-geometry (4):
    g0: LineSegment StartX=-32.3513 StartY=3 StartZ=0 EndX=-32.3513 EndY=0 EndZ=0
    g1: ArcOfCircle CenterX=-35 CenterY=-1.99333 CenterZ=0 NormalX=0 NormalY=0 NormalZ=1 AngleXU=0 Radius=3 StartAngle=0.726747 EndAngle=2.0944
    g2: LineSegment StartX=-32.758 StartY=0 StartZ=0 EndX=-32.3513 EndY=0 EndZ=0
    g3: LineSegment StartX=-32.3513 StartY=3 StartZ=0 EndX=-36.5 EndY=0.60475 EndZ=0
  constraints (10):
    c: Radius(g-3) = 3
    c: Coincident(g0,g-4)
    c: Coincident(g0,g-4)
    c: Coincident(g1,g-3)
    c: Coincident(g1,g-3)
    c: Coincident(g2,g1)
    c: Coincident(g2,g0)
    c: Horizontal(g2)
    c: Coincident(g3,g0)
    c: Coincident(g3,g1)
FEATURE [PartDesign::Pocket] Pocket103
  BaseFeature = -> Pocket102
  Direction = (-1,0,0)
  Length = 4
  Length2 = 5
  Profile = -> Sketch227
  ReferenceAxis = -> Sketch227 [N_Axis]
  Refine = true
  Suppressed = false
  Type = 0
FEATURE [Sketcher::SketchObject] Sketch228
  ArcFitTolerance = 1e-06
  AttachmentSupport = -> [Pocket103]
  ExternalGeometry = -> [Pocket103]
  FullyConstrained = true
  MakeInternals = false
  MapMode = 5
  Placement = pos=(29.25,0,0) rot=(0.57735,0.57735,0.57735;2.0944rad)
  sketch-geometry (4):
    g0: LineSegment StartX=-32.3513 StartY=3 StartZ=0 EndX=-36.5 EndY=0.60475 EndZ=0
    g1: LineSegment StartX=-32.3513 StartY=3 StartZ=0 EndX=-32.3513 EndY=0 EndZ=0
    g2: LineSegment StartX=-32.3513 StartY=0 StartZ=0 EndX=-32.758 EndY=-4.41329e-11 EndZ=0
    g3: ArcOfCircle CenterX=-35 CenterY=-1.99332 CenterZ=0 NormalX=0 NormalY=0 NormalZ=1 AngleXU=0 Radius=2.99999 StartAngle=0.726746 EndAngle=2.0944
  constraints (9):
    c: Coincident(g0,g-3)
    c: Coincident(g0,g-5)
    c: Coincident(g1,g0)
    c: Coincident(g1,g-4)
    c: Coincident(g2,g1)
    c: Coincident(g2,g-5)
    c: Coincident(g3,g0)
    c: Coincident(g3,g2)
    c: Tangent(g3,g-5)
FEATURE [PartDesign::Pad] Pad151
  BaseFeature = -> Pocket103
  Direction = (1,0,0)
  Length = 2
  Length2 = 10
  Profile = -> Sketch228
  ReferenceAxis = -> Sketch228 [N_Axis]
  Refine = true
  Reversed = true
  Suppressed = false
  Type = 0
FEATURE [Sketcher::SketchObject] Sketch229
  ArcFitTolerance = 1e-06
  AttachmentSupport = -> [Pad151]
  ExternalGeometry = -> [Pad151]
  FullyConstrained = true
  MakeInternals = false
  MapMode = 5
  Placement = pos=(6.75,0,0) rot=(0.57735,-0.57735,-0.57735;2.0944rad)
  sketch-geometry (4):
    g0: ArcOfCircle CenterX=35 CenterY=-1.99333 CenterZ=0 NormalX=0 NormalY=0 NormalZ=1 AngleXU=0 Radius=3 StartAngle=1.0472 EndAngle=2.41485
    g1: LineSegment StartX=32.3513 StartY=3 StartZ=0 EndX=32.3513 EndY=0 EndZ=0
    g2: LineSegment StartX=32.3513 StartY=0 StartZ=0 EndX=32.758 EndY=0 EndZ=0
    g3: LineSegment StartX=32.3513 StartY=3 StartZ=0 EndX=36.5 EndY=0.60475 EndZ=0
  constraints (9):
    c: Coincident(g0,g-4)
    c: Coincident(g1,g-5)
    c: Coincident(g1,g-5)
    c: Coincident(g2,g1)
    c: Coincident(g2,g0)
    c: Horizontal(g2)
    c: Coincident(g0,g-3)
    c: Coincident(g3,g1)
    c: Coincident(g3,g0)
FEATURE [PartDesign::Pocket] Pocket104
  BaseFeature = -> Pad151
  Direction = (1,0,0)
  Length = 4
  Length2 = 5
  Profile = -> Sketch229
  ReferenceAxis = -> Sketch229 [N_Axis]
  Refine = true
  Suppressed = false
  Type = 0
FEATURE [Sketcher::SketchObject] Sketch230
  ArcFitTolerance = 1e-06
  AttachmentSupport = -> [Pocket104]
  ExternalGeometry = -> [Pocket104]
  FullyConstrained = true
  MakeInternals = false
  MapMode = 5
  Placement = pos=(6.75,0,0) rot=(0.57735,-0.57735,-0.57735;2.0944rad)
  sketch-geometry (4):
    g0: LineSegment StartX=32.3513 StartY=3 StartZ=0 EndX=32.3513 EndY=0 EndZ=0
    g1: LineSegment StartX=32.3513 StartY=0 StartZ=0 EndX=32.758 EndY=0 EndZ=0
    g2: LineSegment StartX=32.3513 StartY=3 StartZ=0 EndX=36.5 EndY=0.60475 EndZ=0
    g3: ArcOfCircle CenterX=35 CenterY=-1.99332 CenterZ=0 NormalX=0 NormalY=0 NormalZ=1 AngleXU=0 Radius=2.99999 StartAngle=1.0472 EndAngle=2.41485
  constraints (9):
    c: Coincident(g0,g-5)
    c: Coincident(g0,g-6)
    c: Coincident(g1,g0)
    c: Coincident(g1,g-6)
    c: Coincident(g2,g0)
    c: Coincident(g2,g-5)
    c: Coincident(g3,g1)
    c: Coincident(g3,g2)
    c: Tangent(g3,g-3)
FEATURE [PartDesign::Pad] Pad152
  BaseFeature = -> Pocket104
  Direction = (-1,0,0)
  Length = 2
  Length2 = 10
  Profile = -> Sketch230
  ReferenceAxis = -> Sketch230 [N_Axis]
  Refine = true
  Reversed = true
  Suppressed = false
  Type = 0
FEATURE [Sketcher::SketchObject] Sketch231
  ArcFitTolerance = 1e-06
  AttachmentSupport = -> [Pad152]
  ExternalGeometry = -> [Pad152]
  FullyConstrained = true
  MakeInternals = false
  MapMode = 5
  Placement = pos=(6.75,0,-1.7e-15) rot=(0.57735,-0.57735,-0.57735;2.0944rad)
  sketch-geometry (4):
    g0: LineSegment StartX=25.9 StartY=3 StartZ=0 EndX=25.9 EndY=1 EndZ=0
    g1: LineSegment StartX=25.9 StartY=1 StartZ=0 EndX=30.4 EndY=1 EndZ=0
    g2: LineSegment StartX=30.4 StartY=1 StartZ=0 EndX=30.4 EndY=3 EndZ=0
    g3: LineSegment StartX=30.4 StartY=3 StartZ=0 EndX=25.9 EndY=3 EndZ=0
  constraints (12):
    c: Coincident(g0,g1)
    c: Coincident(g1,g2)
    c: Coincident(g2,g3)
    c: Coincident(g3,g0)
    c: Vertical(g0)
    c: Vertical(g2)
    c: Horizontal(g1)
    c: Horizontal(g3)
    c: PointOnObject(g0,g-3)
    c: DistanceX(g3,g3) = 4.5
    c: DistanceX(g-3,g0) = 15
    c: DistanceY(g0,g0) = 2
FEATURE [PartDesign::Pocket] Pocket105
  BaseFeature = -> Pad152
  Direction = (1,0,0)
  Length = 23
  Length2 = 5
  Profile = -> Sketch231
  ReferenceAxis = -> Sketch231 [N_Axis]
  Refine = true
  Suppressed = false
  Type = 0
FEATURE [Sketcher::SketchObject] Sketch232
  ArcFitTolerance = 1e-06
  AttachmentSupport = -> [Pocket105]
  ExternalGeometry = -> [Pocket105]
  FullyConstrained = true
  MakeInternals = false
  MapMode = 5
  Placement = pos=(0,0,3) rot=(0,0,1;0rad)
  sketch-geometry (8):
    g0: LineSegment StartX=10.75 StartY=-22 StartZ=0 EndX=10.75 EndY=-2 EndZ=0
    g1: LineSegment StartX=10.75 StartY=-2 StartZ=0 EndX=8.75 EndY=-2 EndZ=0
    g2: LineSegment StartX=8.75 StartY=-2 StartZ=0 EndX=8.75 EndY=-22 EndZ=0
    g3: LineSegment StartX=8.75 StartY=-22 StartZ=0 EndX=10.75 EndY=-22 EndZ=0
    g4: LineSegment StartX=27.25 StartY=-22 StartZ=0 EndX=27.25 EndY=-2 EndZ=0
    g5: LineSegment StartX=27.25 StartY=-2 StartZ=0 EndX=25.25 EndY=-2 EndZ=0
    g6: LineSegment StartX=25.25 StartY=-2 StartZ=0 EndX=25.25 EndY=-22 EndZ=0
    g7: LineSegment StartX=25.25 StartY=-22 StartZ=0 EndX=27.25 EndY=-22 EndZ=0
  constraints (24):
    c: Coincident(g0,g1)
    c: Coincident(g1,g2)
    c: Coincident(g2,g3)
    c: Coincident(g3,g0)
    c: Vertical(g0)
    c: Vertical(g2)
    c: Horizontal(g1)
    c: Horizontal(g3)
    c: PointOnObject(g0,g-3)
    c: Coincident(g4,g5)
    c: Coincident(g5,g6)
    c: Coincident(g6,g7)
    c: Coincident(g7,g4)
    c: Vertical(g4)
    c: Vertical(g6)
    c: Horizontal(g5)
    c: Horizontal(g7)
    c: PointOnObject(g4,g-6)
    c: PointOnObject(g2,g-4)
    c: PointOnObject(g6,g-5)
    c: DistanceY(g-8,g4) = 2
    c: DistanceY(g-7,g2) = 2
    c: DistanceY(g1,g-1) = 2
    c: DistanceY(g5,g-1) = 2
FEATURE [PartDesign::Pocket] Pocket106
  BaseFeature = -> Pocket105
  Direction = (0,0,-1)
  Length = 7.5
  Length2 = 5
  Profile = -> Sketch232
  ReferenceAxis = -> Sketch232 [N_Axis]
  Refine = true
  Suppressed = false
  Type = 0
FEATURE [Sketcher::SketchObject] Sketch233
  ArcFitTolerance = 1e-06
  AttachmentSupport = -> [Pocket106]
  ExternalGeometry = -> [Pocket106]
  FullyConstrained = true
  MakeInternals = false
  MapMode = 5
  Placement = pos=(0,0,-8) rot=(1,0,0;3.14159rad)
  sketch-geometry (16):
    g0: LineSegment StartX=23.25 StartY=15.1313 StartZ=0 EndX=25.75 EndY=12.6313 EndZ=0
    g1: LineSegment StartX=25.75 StartY=12.6313 StartZ=0 EndX=29.25 EndY=12.6313 EndZ=0
    g2: LineSegment StartX=29.25 StartY=12.6313 StartZ=0 EndX=29.25 EndY=12.1313 EndZ=0
    g3: LineSegment StartX=29.25 StartY=12.1313 StartZ=0 EndX=25.5429 EndY=12.1313 EndZ=0
    g4: LineSegment StartX=25.5429 StartY=12.1313 StartZ=0 EndX=24.0429 EndY=13.6313 EndZ=0
    g5: LineSegment StartX=23.25 StartY=13.6313 StartZ=0 EndX=23.25 EndY=15.1313 EndZ=0
    g6: LineSegment StartX=24.0429 StartY=13.6313 StartZ=0 EndX=23.25 EndY=13.6313 EndZ=0
    g7: LineSegment [constr] StartX=25.3964 StartY=12.9849 StartZ=0 EndX=25.0429 EndY=12.6313 EndZ=0
    g8: LineSegment StartX=6.75 StartY=12.1313 StartZ=0 EndX=6.75 EndY=12.6313 EndZ=0
    g9: LineSegment StartX=6.75 StartY=12.6313 StartZ=0 EndX=10.25 EndY=12.6313 EndZ=0
    g10: LineSegment StartX=10.25 StartY=12.6313 StartZ=0 EndX=12.75 EndY=15.1313 EndZ=0
    g11: LineSegment StartX=6.75 StartY=12.1313 StartZ=0 EndX=10.4571 EndY=12.1313 EndZ=0
    g12: LineSegment StartX=10.4571 StartY=12.1313 StartZ=0 EndX=11.9571 EndY=13.6313 EndZ=0
    g13: LineSegment StartX=11.9571 StartY=13.6313 StartZ=0 EndX=12.75 EndY=13.6313 EndZ=0
    g14: LineSegment StartX=12.75 StartY=13.6313 StartZ=0 EndX=12.75 EndY=15.1313 EndZ=0
    g15: LineSegment [constr] StartX=10.9571 StartY=12.6313 StartZ=0 EndX=10.6036 EndY=12.9849 EndZ=0
  constraints (50):
    c: PointOnObject(g0,g-3)
    c: Coincident(g1,g0)
    c: PointOnObject(g1,g-4)
    c: Horizontal(g1)
    c: Coincident(g2,g1)
    c: PointOnObject(g2,g-4)
    c: Coincident(g3,g2)
    c: Horizontal(g3)
    c: Coincident(g4,g3)
    c: PointOnObject(g5,g-3)
    c: Coincident(g5,g0)
    c: Coincident(g6,g4)
    c: Coincident(g6,g5)
    c: Horizontal(g6)
    c: DistanceY(g2,g2) = 0.5
    c: DistanceY(g1,g-4) = 4.5
    c: Angle(g1,g0) = 2.35619
    c: Parallel(g4,g0)
    c: DistanceX(g0,g0) = 2.5
    c: PointOnObject(g7,g0)
    c: PointOnObject(g7,g4)
    c: Angle(g0,g7) = 1.5708
    c: Distance(g7) = 0.5
    c: Distance(g7,g0) = 0.5
    c: DistanceY(g5,g5) = 1.5
    c: PointOnObject(g8,g-6)
    c: PointOnObject(g8,g-6)
    c: Coincident(g9,g8)
    c: Horizontal(g9)
    c: Coincident(g10,g9)
    c: PointOnObject(g10,g-5)
    c: Coincident(g11,g8)
    c: Horizontal(g11)
    c: Coincident(g12,g11)
    c: Coincident(g13,g12)
    c: PointOnObject(g13,g-5)
    c: Horizontal(g13)
    c: Angle(g10,g9) = 2.35619
    c: Parallel(g12,g10)
    c: Coincident(g14,g13)
    c: Coincident(g14,g10)
    c: DistanceY(g14,g14) = 1.5
    c: DistanceY(g8,g-6) = 4.5
    c: DistanceY(g8,g8) = 0.5
    c: DistanceX(g9,g10) = 2.5
    c: PointOnObject(g15,g12)
    c: PointOnObject(g15,g10)
    c: Angle(g15,g12) = 1.5708
    c: Distance(g15,g9) = 0.5
    c: Distance(g15) = 0.5
FEATURE [PartDesign::Pocket] Pocket107
  BaseFeature = -> Pocket106
  Direction = (0,0,1)
  Length = 0.5
  Length2 = 5
  Profile = -> Sketch233
  ReferenceAxis = -> Sketch233 [N_Axis]
  Refine = true
  Suppressed = false
  Type = 0
FEATURE [Sketcher::SketchObject] Sketch234
  ArcFitTolerance = 1e-06
  AttachmentSupport = -> [Pocket107]
  ExternalGeometry = -> [Pocket107]
  FullyConstrained = true
  MakeInternals = false
  MapMode = 5
  Placement = pos=(0,0,-2) rot=(0,0,1;0rad)
  sketch-geometry (4):
    g0: LineSegment StartX=29.25 StartY=0 StartZ=0 EndX=29.25 EndY=-5 EndZ=0
    g1: LineSegment StartX=29.25 StartY=-5 StartZ=0 EndX=36 EndY=-5 EndZ=0
    g2: LineSegment StartX=36 StartY=-5 StartZ=0 EndX=36 EndY=0 EndZ=0
    g3: LineSegment StartX=36 StartY=0 StartZ=0 EndX=29.25 EndY=0 EndZ=0
  constraints (11):
    c: Coincident(g0,g1)
    c: Coincident(g1,g2)
    c: Coincident(g2,g3)
    c: Coincident(g3,g0)
    c: Vertical(g0)
    c: Vertical(g2)
    c: Horizontal(g1)
    c: Horizontal(g3)
    c: Coincident(g0,g-3)
    c: DistanceX(g3,g3) = 6.75
    c: DistanceY(g2,g2) = 5
FEATURE [PartDesign::Pad] Pad153
  BaseFeature = -> Pocket107
  Direction = (0,0,1)
  Length = 8.2
  Length2 = 10
  Profile = -> Sketch234
  ReferenceAxis = -> Sketch234 [N_Axis]
  Refine = true
  Reversed = true
  Suppressed = false
  Type = 0
FEATURE [Sketcher::SketchObject] Sketch235
  ArcFitTolerance = 1e-06
  AttachmentSupport = -> [Pad153]
  ExternalGeometry = -> [Pad153]
  FullyConstrained = true
  MakeInternals = false
  MapMode = 5
  Placement = pos=(0,0,-10.2) rot=(1,0,0;3.14159rad)
  sketch-geometry (1):
    g0: Circle CenterX=31.75 CenterY=2.5 CenterZ=0 NormalX=0 NormalY=0 NormalZ=1 AngleXU=0 Radius=1.75
  constraints (4):
    c: Diameter(g0) = 3.5
    c: DistanceX(g0,g-3) = 4.25
    c: DistanceY(g-3,g-3) = 5
    c: DistanceY(g0,g-4) = 2.5
FEATURE [PartDesign::Pad] Pad154
  BaseFeature = -> Pad153
  Direction = (0,0,-1)
  Length = 0.5
  Length2 = 10
  Profile = -> Sketch235
  ReferenceAxis = -> Sketch235 [N_Axis]
  Refine = true
  Suppressed = false
  Type = 0
FEATURE [Sketcher::SketchObject] Sketch236
  ArcFitTolerance = 1e-06
  AttachmentSupport = -> [Pad154]
  ExternalGeometry = -> [Pad154]
  FullyConstrained = true
  MakeInternals = false
  MapMode = 5
  Placement = pos=(0,0,-2) rot=(0,0,1;0rad)
  sketch-geometry (4):
    g0: LineSegment StartX=34 StartY=-2 StartZ=0 EndX=29.25 EndY=-2 EndZ=0
    g1: LineSegment StartX=29.25 StartY=-2 StartZ=0 EndX=29.25 EndY=-3 EndZ=0
    g2: LineSegment StartX=29.25 StartY=-3 StartZ=0 EndX=34 EndY=-3 EndZ=0
    g3: LineSegment StartX=34 StartY=-3 StartZ=0 EndX=34 EndY=-2 EndZ=0
  constraints (12):
    c: Coincident(g0,g1)
    c: Coincident(g1,g2)
    c: Coincident(g2,g3)
    c: Coincident(g3,g0)
    c: Horizontal(g0)
    c: Horizontal(g2)
    c: Vertical(g1)
    c: Vertical(g3)
    c: DistanceY(g0,g-3) = 2
    c: DistanceY(g-4,g2) = 2
    c: DistanceX(g2,g-4) = 2
    c: DistanceX(g-4,g1) = 0
FEATURE [PartDesign::Pocket] Pocket108
  BaseFeature = -> Pad154
  Direction = (0,0,-1)
  Length = 6.2
  Length2 = 5
  Profile = -> Sketch236
  ReferenceAxis = -> Sketch236 [N_Axis]
  Refine = true
  Suppressed = false
  Type = 0
FEATURE [Sketcher::SketchObject] Sketch237
  ArcFitTolerance = 1e-06
  AttachmentSupport = -> [Pocket108]
  ExternalGeometry = -> [Pocket108]
  FullyConstrained = true
  MakeInternals = false
  MapMode = 5
  Placement = pos=(0,0,3) rot=(0,0,1;0rad)
  sketch-geometry (4):
    g0: LineSegment StartX=6.75 StartY=0 StartZ=0 EndX=0 EndY=0 EndZ=0
    g1: LineSegment StartX=0 StartY=0 StartZ=0 EndX=0 EndY=-10 EndZ=0
    g2: LineSegment StartX=0 StartY=-10 StartZ=0 EndX=6.75 EndY=-10 EndZ=0
    g3: LineSegment StartX=6.75 StartY=-10 StartZ=0 EndX=6.75 EndY=0 EndZ=0
  constraints (11):
    c: Coincident(g0,g1)
    c: Coincident(g1,g2)
    c: Coincident(g2,g3)
    c: Coincident(g3,g0)
    c: Horizontal(g0)
    c: Horizontal(g2)
    c: Vertical(g1)
    c: Vertical(g3)
    c: Coincident(g0,g-3)
    c: PointOnObject(g1,g-2)
    c: DistanceY(g1,g1) = 10
FEATURE [PartDesign::Pad] Pad155
  BaseFeature = -> Pocket108
  Direction = (0,0,1)
  Length = 13.2
  Length2 = 10
  Profile = -> Sketch237
  ReferenceAxis = -> Sketch237 [N_Axis]
  Refine = true
  Reversed = true
  Suppressed = false
  Type = 0
FEATURE [Sketcher::SketchObject] Sketch238
  ArcFitTolerance = 1e-06
  AttachmentSupport = -> [Pad155]
  ExternalGeometry = -> [Pad155]
  FullyConstrained = true
  MakeInternals = false
  MapMode = 5
  Placement = pos=(0,0,-2) rot=(0,0,1;0rad)
  sketch-geometry (4):
    g0: LineSegment StartX=6.75 StartY=0 StartZ=0 EndX=6.75 EndY=-10 EndZ=0
    g1: LineSegment StartX=6.75 StartY=-10 StartZ=0 EndX=8.75 EndY=-10 EndZ=0
    g2: LineSegment StartX=8.75 StartY=-10 StartZ=0 EndX=8.75 EndY=0 EndZ=0
    g3: LineSegment StartX=8.75 StartY=0 StartZ=0 EndX=6.75 EndY=0 EndZ=0
  constraints (10):
    c: Coincident(g0,g1)
    c: Coincident(g1,g2)
    c: Coincident(g2,g3)
    c: Coincident(g3,g0)
    c: Vertical(g2)
    c: Horizontal(g1)
    c: Horizontal(g3)
    c: Coincident(g0,g-4)
    c: PointOnObject(g1,g-3)
    c: Coincident(g0,g-4)
FEATURE [PartDesign::Pad] Pad156
  BaseFeature = -> Pad155
  Direction = (0,0,1)
  Length = 2
  Length2 = 10
  Profile = -> Sketch238
  ReferenceAxis = -> Sketch238 [N_Axis]
  Refine = true
  Suppressed = false
  Type = 0
FEATURE [Sketcher::SketchObject] Sketch239
  ArcFitTolerance = 1e-06
  AttachmentSupport = -> [Pad156]
  ExternalGeometry = -> [Pad156]
  FullyConstrained = true
  MakeInternals = false
  MapMode = 5
  Placement = pos=(0,0,3) rot=(0,0,1;0rad)
  sketch-geometry (4):
    g0: LineSegment StartX=0 StartY=-1.3 StartZ=0 EndX=0 EndY=-8.7 EndZ=0
    g1: LineSegment StartX=0 StartY=-8.7 StartZ=0 EndX=6.75 EndY=-8.7 EndZ=0
    g2: LineSegment StartX=6.75 StartY=-8.7 StartZ=0 EndX=6.75 EndY=-1.3 EndZ=0
    g3: LineSegment StartX=6.75 StartY=-1.3 StartZ=0 EndX=0 EndY=-1.3 EndZ=0
  constraints (12):
    c: Coincident(g0,g1)
    c: Coincident(g1,g2)
    c: Coincident(g2,g3)
    c: Coincident(g3,g0)
    c: Vertical(g0)
    c: Vertical(g2)
    c: Horizontal(g1)
    c: Horizontal(g3)
    c: PointOnObject(g0,g-4)
    c: PointOnObject(g1,g-3)
    c: DistanceY(g0,g-1) = 1.3
    c: DistanceY(g-4,g0) = 1.3
FEATURE [PartDesign::Pocket] Pocket109
  BaseFeature = -> Pad156
  Direction = (0,0,-1)
  Length = 3
  Length2 = 5
  Profile = -> Sketch239
  ReferenceAxis = -> Sketch239 [N_Axis]
  Refine = true
  Suppressed = false
  Type = 0
FEATURE [Sketcher::SketchObject] Sketch240
  ArcFitTolerance = 1e-06
  AttachmentSupport = -> [Pocket109]
  ExternalGeometry = -> [Pocket109]
  FullyConstrained = true
  MakeInternals = false
  MapMode = 5
  sketch-geometry (1):
    g0: Circle CenterX=6.25 CenterY=-3.8 CenterZ=0 NormalX=0 NormalY=0 NormalZ=1 AngleXU=0 Radius=2.5
  constraints (3):
    c: Diameter(g0) = 5
    c: Tangent(g0,g-3)
    c: Tangent(g0,g-5)
FEATURE [PartDesign::Pad] Pad157
  BaseFeature = -> Pocket109
  Direction = (0,0,1)
  Length = 7.9
  Length2 = 10
  Profile = -> Sketch240
  ReferenceAxis = -> Sketch240 [N_Axis]
  Refine = true
  Suppressed = false
  Type = 0
FEATURE [Sketcher::SketchObject] Sketch241
  ArcFitTolerance = 1e-06
  AttachmentSupport = -> [Pad157]
  ExternalGeometry = -> [Pad157]
  FullyConstrained = true
  MakeInternals = false
  MapMode = 5
  Placement = pos=(0,0,0) rot=(0.57735,-0.57735,-0.57735;2.0944rad)
  sketch-geometry (4):
    g0: LineSegment StartX=8.7 StartY=0 StartZ=0 EndX=1.3 EndY=0 EndZ=0
    g1: LineSegment StartX=1.3 StartY=0 StartZ=0 EndX=1.3 EndY=-6.2 EndZ=0
    g2: LineSegment StartX=1.3 StartY=-6.2 StartZ=0 EndX=8.7 EndY=-6.2 EndZ=0
    g3: LineSegment StartX=8.7 StartY=-6.2 StartZ=0 EndX=8.7 EndY=0 EndZ=0
  constraints (10):
    c: Coincident(g0,g1)
    c: Coincident(g1,g2)
    c: Coincident(g2,g3)
    c: Coincident(g3,g0)
    c: Horizontal(g2)
    c: Vertical(g1)
    c: Vertical(g3)
    c: Coincident(g0,g-3)
    c: Coincident(g0,g-3)
    c: DistanceY(g-4,g2) = 4
FEATURE [PartDesign::Pocket] Pocket110
  BaseFeature = -> Pad157
  Direction = (1,0,0)
  Length = 3
  Length2 = 5
  Profile = -> Sketch241
  ReferenceAxis = -> Sketch241 [N_Axis]
  Refine = true
  Suppressed = false
  Type = 0
FEATURE [Sketcher::SketchObject] Sketch242
  ArcFitTolerance = 1e-06
  AttachmentSupport = -> [Pocket110]
  ExternalGeometry = -> [Pocket110]
  FullyConstrained = true
  MakeInternals = false
  MapMode = 5
  Placement = pos=(0,0,-10.2) rot=(1,0,0;3.14159rad)
  sketch-geometry (4):
    g0: LineSegment StartX=6.75 StartY=8.7 StartZ=0 EndX=2 EndY=8.7 EndZ=0
    g1: LineSegment StartX=2 StartY=8.7 StartZ=0 EndX=2 EndY=1.3 EndZ=0
    g2: LineSegment StartX=2 StartY=1.3 StartZ=0 EndX=6.75 EndY=1.3 EndZ=0
    g3: LineSegment StartX=6.75 StartY=1.3 StartZ=0 EndX=6.75 EndY=8.7 EndZ=0
  constraints (12):
    c: Coincident(g0,g1)
    c: Coincident(g1,g2)
    c: Coincident(g2,g3)
    c: Coincident(g3,g0)
    c: Horizontal(g0)
    c: Horizontal(g2)
    c: Vertical(g1)
    c: Vertical(g3)
    c: PointOnObject(g0,g-3)
    c: DistanceX(g-4,g0) = 2
    c: DistanceY(g0,g-4) = 1.3
    c: DistanceY(g-3,g2) = 1.3
FEATURE [PartDesign::Pocket] Pocket111
  BaseFeature = -> Pocket110
  Direction = (0,0,1)
  Length = 7.2
  Length2 = 5
  Profile = -> Sketch242
  ReferenceAxis = -> Sketch242 [N_Axis]
  Refine = true
  Suppressed = false
  Type = 0
FEATURE [Sketcher::SketchObject] Sketch243
  ArcFitTolerance = 1e-06
  AttachmentSupport = -> [Pocket111]
  ExternalGeometry = -> [Pocket111]
  FullyConstrained = true
  MakeInternals = false
  MapMode = 5
  Placement = pos=(0,0,-3) rot=(1,0,0;3.14159rad)
  sketch-geometry (4):
    g0: LineSegment StartX=6.75 StartY=8.7 StartZ=0 EndX=4.875 EndY=8.7 EndZ=0
    g1: LineSegment StartX=4.875 StartY=8.7 StartZ=0 EndX=4.875 EndY=1.3 EndZ=0
    g2: LineSegment StartX=4.875 StartY=1.3 StartZ=0 EndX=6.75 EndY=1.3 EndZ=0
    g3: LineSegment StartX=6.75 StartY=1.3 StartZ=0 EndX=6.75 EndY=8.7 EndZ=0
  constraints (10):
    c: Coincident(g0,g1)
    c: Coincident(g1,g2)
    c: Coincident(g2,g3)
    c: Coincident(g3,g0)
    c: Horizontal(g0)
    c: Horizontal(g2)
    c: Vertical(g1)
    c: Vertical(g3)
    c: Coincident(g0,g-4)
    c: Symmetric(g-5,g-5,g1)
FEATURE [PartDesign::Pocket] Pocket112
  BaseFeature = -> Pocket111
  Direction = (0,0,1)
  Length = 1
  Length2 = 5
  Profile = -> Sketch243
  ReferenceAxis = -> Sketch243 [N_Axis]
  Refine = true
  Suppressed = false
  Type = 0
FEATURE [Sketcher::SketchObject] Sketch244
  ArcFitTolerance = 1e-06
  AttachmentSupport = -> [Pocket112]
  ExternalGeometry = -> [Pocket112]
  FullyConstrained = true
  MakeInternals = false
  MapMode = 5
  Placement = pos=(0,-1.3,0) rot=(1,0,0;1.5708rad)
  sketch-geometry (4):
    g0: LineSegment StartX=3 StartY=-3 StartZ=0 EndX=3 EndY=-10.2 EndZ=0
    g1: LineSegment StartX=3 StartY=-10.2 StartZ=0 EndX=4.875 EndY=-10.2 EndZ=0
    g2: LineSegment StartX=4.875 StartY=-10.2 StartZ=0 EndX=4.875 EndY=-3 EndZ=0
    g3: LineSegment StartX=4.875 StartY=-3 StartZ=0 EndX=3 EndY=-3 EndZ=0
  constraints (10):
    c: Coincident(g0,g1)
    c: Coincident(g1,g2)
    c: Coincident(g2,g3)
    c: Coincident(g3,g0)
    c: Vertical(g0)
    c: Vertical(g2)
    c: Horizontal(g1)
    c: Coincident(g0,g-4)
    c: Coincident(g2,g-5)
    c: PointOnObject(g1,g-6)
FEATURE [PartDesign::Pad] Pad158
  BaseFeature = -> Pocket112
  Direction = (0,-1,2e-16)
  Length = 0.75
  Length2 = 10
  Profile = -> Sketch244
  ReferenceAxis = -> Sketch244 [N_Axis]
  Refine = true
  Suppressed = false
  Type = 0
FEATURE [Sketcher::SketchObject] Sketch245
  ArcFitTolerance = 1e-06
  AttachmentSupport = -> [Pad158]
  ExternalGeometry = -> [Pad158]
  FullyConstrained = true
  MakeInternals = false
  MapMode = 5
  Placement = pos=(0,-8.7,0) rot=(0,0.707107,0.707107;3.14159rad)
  sketch-geometry (4):
    g0: LineSegment StartX=-4.875 StartY=-3 StartZ=0 EndX=-4.875 EndY=-10.2 EndZ=0
    g1: LineSegment StartX=-4.875 StartY=-10.2 StartZ=0 EndX=-3 EndY=-10.2 EndZ=0
    g2: LineSegment StartX=-3 StartY=-10.2 StartZ=0 EndX=-3 EndY=-3 EndZ=0
    g3: LineSegment StartX=-3 StartY=-3 StartZ=0 EndX=-4.875 EndY=-3 EndZ=0
  constraints (10):
    c: Coincident(g0,g1)
    c: Coincident(g1,g2)
    c: Coincident(g2,g3)
    c: Coincident(g3,g0)
    c: Vertical(g0)
    c: Vertical(g2)
    c: Horizontal(g1)
    c: Coincident(g0,g-4)
    c: PointOnObject(g1,g-3)
    c: Coincident(g2,g-4)
FEATURE [PartDesign::Pad] Pad159
  BaseFeature = -> Pad158
  Direction = (0,1,-2e-16)
  Length = 0.75
  Length2 = 10
  Profile = -> Sketch245
  ReferenceAxis = -> Sketch245 [N_Axis]
  Refine = true
  Suppressed = false
  Type = 0
FEATURE [PartDesign::Chamfer] Chamfer002
  Angle = 45
  Base = -> Pad159 [Edge357,Edge364]
  BaseFeature = -> Pad159
  ChamferType = 0
  FlipDirection = false
  Refine = true
  Size = 0.5
  Size2 = 1
  SupportTransform = false
  Suppressed = false
  UseAllEdges = false
FEATURE [PartDesign::Fillet] Fillet009
  Base = -> Chamfer002 [Edge73,Edge160,Edge60,Edge309,Edge188,Edge113,Edge206,Edge271,Edge269,Edge289,Edge178,Edge123,Edge254,Edge126,Edge197,Edge65,Edge44,Edge54,Edge199,Edge201,Edge130,Edge246,Edge119,Edge128,Edge250,Edge121,Edge180,Edge291,Edge276,Edge302,Edge182,Edge293,Edge274,Edge300,Edge78,Edge83,Edge38,Edge47,Edge62,Edge165]
  BaseFeature = -> Chamfer002
  Radius = 0.5
  Refine = true
  SupportTransform = false
  Suppressed = false
  UseAllEdges = false
FEATURE [PartDesign::Pad] Pad160
  BaseFeature = -> Fillet009
  Direction = (0,0,1)
  Length = 1
  Length2 = 10
  Profile = -> Fillet009 [Face164]
  Refine = true
  Suppressed = false
  Type = 0
FEATURE [PartDesign::Fillet] Fillet010
  Base = -> Pad160 [Edge48,Edge87,Edge90,Edge303,Edge49,Edge53]
  BaseFeature = -> Pad160
  Radius = 0.5
  Refine = true
  SupportTransform = false
  Suppressed = false
  UseAllEdges = false
FEATURE [PartDesign::Fillet] Fillet011
  Base = -> Fillet010 [Edge390]
  BaseFeature = -> Fillet010
  Radius = 0.25
  Refine = true
  SupportTransform = false
  Suppressed = false
  UseAllEdges = false
FEATURE [PartDesign::Pocket] Pocket113
  BaseFeature = -> Fillet011
  Direction = (0,0,-1)
  Length = 1
  Length2 = 5
  Profile = -> Fillet011 [Face119,Face14]
  Refine = true
  Suppressed = false
  Type = 0
FEATURE [PartDesign::SubShapeBinder] Binder010
  BindCopyOnChange = 0
  BindMode = 2
  ClaimChildren = false
  Context = -> Body016 [Binder010.]
  Fuse = false
  MakeFace = true
  OffsetFill = false
  OffsetIntersection = false
  OffsetJoinType = 0
  OffsetOpenResult = false
  PartialLoad = false
  Refine = true
  Relative = true
  _Version = 2
FEATURE [Sketcher::SketchObject] Sketch246
  ArcFitTolerance = 1e-06
  AttachmentSupport = -> [Binder010]
  ExternalGeometry = -> [Binder010]
  FullyConstrained = true
  MakeInternals = false
  MapMode = 5
  Placement = pos=(29.25,0,-7.6e-15) rot=(0.57735,0.57735,0.57735;2.0944rad)
  sketch-geometry (13):
    g0: LineSegment StartX=-33.5313 StartY=3 StartZ=0 EndX=-17.1313 EndY=3 EndZ=0
    g1: LineSegment StartX=-17.1313 StartY=3 StartZ=0 EndX=-17.1313 EndY=-9.8 EndZ=0
    g2: LineSegment StartX=-17.1313 StartY=-9.8 StartZ=0 EndX=-22.1313 EndY=-9.8 EndZ=0
    g3: ArcOfCircle CenterX=-26.2738 CenterY=-7 CenterZ=0 NormalX=0 NormalY=0 NormalZ=1 AngleXU=0 Radius=5 StartAngle=3.73598 EndAngle=5.6888
    g4: LineSegment StartX=-30.4162 StartY=-9.8 StartZ=0 EndX=-44.062 EndY=-4.89651 EndZ=0
    g5: LineSegment StartX=-42.095 StartY=-1.94424 StartZ=0 EndX=-33.5313 EndY=3 EndZ=0
    g6: LineSegment [constr] StartX=-26.2738 StartY=-12 StartZ=0 EndX=-17.1313 EndY=-12 EndZ=0
    g7: LineSegment [constr] StartX=-17.1313 StartY=-9.8 StartZ=0 EndX=-17.1313 EndY=-12 EndZ=0
    g8: LineSegment [constr] StartX=-26.2738 StartY=-7 StartZ=0 EndX=-26.2738 EndY=-12 EndZ=0
    g9: LineSegment StartX=-42.095 StartY=-1.94424 StartZ=0 EndX=-44.595 EndY=-1.94424 EndZ=0
    g10: LineSegment StartX=-44.062 StartY=-4.89651 StartZ=0 EndX=-44.595 EndY=-1.94424 EndZ=0
    g11: Circle CenterX=-35 CenterY=-1.99333 CenterZ=0 NormalX=0 NormalY=0 NormalZ=1 AngleXU=0 Radius=0.8
    g12: Circle CenterX=-26.2738 CenterY=-7 CenterZ=0 NormalX=0 NormalY=0 NormalZ=1 AngleXU=0 Radius=0.8
  constraints (41):
    c: Horizontal(g0)
    c: Coincident(g1,g0)
    c: Vertical(g1)
    c: Coincident(g2,g1)
    c: Horizontal(g2)
    c: Coincident(g3,g2)
    c: Coincident(g4,g3)
    c: Coincident(g5,g0)
    c: Radius(g3) = 5
    c: DistanceY(g1,g1) = 12.8
    c: DistanceY(g2,g3) = 0
    c: PointOnObject(g6,g3)
    c: Horizontal(g6)
    c: Coincident(g7,g1)
    c: Coincident(g7,g6)
    c: Vertical(g7)
    c: DistanceY(g7,g7) = 2.2
    c: PointOnObject(g-3,g1)
    c: PointOnObject(g0,g-4)
    c: DistanceX(g0,g0) = 16.4
    c: Parallel(g5,g-5)
    c: Coincident(g8,g3)
    c: Coincident(g8,g6)
    c: Vertical(g8)
    c: Coincident(g9,g5)
    c: Horizontal(g9)
    c: Coincident(g10,g4)
    c: Coincident(g10,g9)
    c: Distance(g4) = 14.5
    c: DistanceX(g9,g9) = 2.5
    c: Angle(g4,g10) = 2.0944
    c: Distance(g10) = 3
    c: DistanceX(g2,g2) = 5
    c: DistanceX(g4,g1) = 26.9307
    c: DistanceX(g9,g0) = 27.4637
    c: DistanceX(g-6,g0) = 17.8687
    c: DistanceY(g5,g0) = 4.94424
    c: Coincident(g11,g-6)
    c: Equal(g11,g-6)
    c: Coincident(g12,g3)
    c: Radius(g12) = 0.8
FEATURE [PartDesign::Pad] Pad161
  Direction = (1,0,0)
  Length = 2
  Length2 = 10
  Profile = -> Sketch246
  ReferenceAxis = -> Sketch246 [N_Axis]
  Refine = true
  Suppressed = false
  Type = 0
FEATURE [Sketcher::SketchObject] Sketch247
  ArcFitTolerance = 1e-06
  AttachmentSupport = -> [Pad161]
  ExternalGeometry = -> [Pad161]
  FullyConstrained = true
  MakeInternals = false
  MapMode = 5
  Placement = pos=(31.25,0,0) rot=(0.57735,0.57735,0.57735;2.0944rad)
  sketch-geometry (10):
    g0: LineSegment StartX=-17.1313 StartY=3 StartZ=0 EndX=-33.5313 EndY=3 EndZ=0
    g1: LineSegment StartX=-33.5313 StartY=3 StartZ=0 EndX=-42.095 EndY=-1.94424 EndZ=0
    g2: LineSegment StartX=-17.1313 StartY=3 StartZ=0 EndX=-17.1313 EndY=5 EndZ=0
    g3: LineSegment StartX=-17.1313 StartY=5 StartZ=0 EndX=-36.4313 EndY=5 EndZ=0
    g4: LineSegment StartX=-36.4313 StartY=5 StartZ=0 EndX=-36.4313 EndY=3.63509 EndZ=0
    g5: LineSegment StartX=-36.4313 StartY=3.63509 StartZ=0 EndX=-42.6309 EndY=0.0557565 EndZ=0
    g6: LineSegment StartX=-42.6309 StartY=0.0557565 StartZ=0 EndX=-44.9561 EndY=0.0557565 EndZ=0
    g7: LineSegment StartX=-44.595 StartY=-1.94424 StartZ=0 EndX=-44.9561 EndY=0.0557565 EndZ=0
    g8: LineSegment [constr] StartX=-36.7303 StartY=1.15303 StartZ=0 EndX=-37.7303 EndY=2.88509 EndZ=0
    g9: LineSegment StartX=-42.095 StartY=-1.94424 StartZ=0 EndX=-44.595 EndY=-1.94424 EndZ=0
  constraints (27):
    c: Coincident(g0,g-4)
    c: Coincident(g0,g-5)
    c: Coincident(g1,g0)
    c: Coincident(g1,g-6)
    c: Coincident(g2,g0)
    c: Vertical(g2)
    c: Coincident(g3,g2)
    c: Horizontal(g3)
    c: DistanceX(g3,g3) = 19.3
    c: DistanceY(g2,g2) = 2
    c: Coincident(g4,g3)
    c: Vertical(g4)
    c: Coincident(g5,g4)
    c: Coincident(g6,g5)
    c: Coincident(g7,g-7)
    c: Coincident(g7,g6)
    c: DistanceY(g1,g5) = 2
    c: PointOnObject(g8,g1)
    c: PointOnObject(g8,g5)
    c: Angle(g8,g1) = 1.5708
    c: Parallel(g1,g5)
    c: Horizontal(g6)
    c: Distance(g8) = 2
    c: Angle(g7,g-7) = 3.14159
    c: Coincident(g9,g1)
    c: Coincident(g9,g7)
    c: Distance(g4,g8) = 1.5
FEATURE [PartDesign::Pad] Pad162
  BaseFeature = -> Pad161
  Direction = (1,0,0)
  Length = 13.25
  Length2 = 10
  Profile = -> Sketch247
  ReferenceAxis = -> Sketch247 [N_Axis]
  Refine = true
  Reversed = true
  Suppressed = false
  Type = 0
FEATURE [Sketcher::SketchObject] Sketch248
  ArcFitTolerance = 1e-06
  AttachmentSupport = -> [Pad162]
  ExternalGeometry = -> [Pad162]
  FullyConstrained = true
  MakeInternals = false
  MapMode = 5
  Placement = pos=(18,0,0) rot=(0.57735,-0.57735,-0.57735;2.0944rad)
  sketch-geometry (9):
    g0: LineSegment StartX=33.5313 StartY=3 StartZ=0 EndX=42.095 EndY=-1.94424 EndZ=0
    g1: LineSegment StartX=42.095 StartY=-1.94424 StartZ=0 EndX=44.595 EndY=-1.94424 EndZ=0
    g2: LineSegment StartX=44.595 StartY=-1.94424 StartZ=0 EndX=44.062 EndY=-4.89651 EndZ=0
    g3: LineSegment StartX=44.062 StartY=-4.89651 StartZ=0 EndX=30.4162 EndY=-9.8 EndZ=0
    g4: LineSegment StartX=30.4162 StartY=-9.8 StartZ=0 EndX=22.1313 EndY=-9.8 EndZ=0
    g5: LineSegment StartX=22.1313 StartY=-9.8 StartZ=0 EndX=19.2313 EndY=-2 EndZ=0
    g6: LineSegment StartX=19.2313 StartY=-2 StartZ=0 EndX=23.2313 EndY=-2 EndZ=0
    g7: LineSegment StartX=23.2313 StartY=-2 StartZ=0 EndX=23.2313 EndY=3 EndZ=0
    g8: LineSegment StartX=33.5313 StartY=3 StartZ=0 EndX=23.2313 EndY=3 EndZ=0
  constraints (21):
    c: Coincident(g0,g-8)
    c: Coincident(g1,g0)
    c: Coincident(g1,g-8)
    c: Coincident(g2,g1)
    c: Coincident(g2,g-4)
    c: Coincident(g3,g2)
    c: Coincident(g3,g-4)
    c: Coincident(g4,g3)
    c: Coincident(g5,g4)
    c: Coincident(g6,g5)
    c: Horizontal(g6)
    c: Coincident(g7,g6)
    c: Vertical(g7)
    c: Coincident(g8,g0)
    c: PointOnObject(g8,g-6)
    c: Coincident(g7,g8)
    c: DistanceY(g7,g7) = 5
    c: DistanceX(g-9,g7) = 6.1
    c: DistanceX(g6,g6) = 4
    c: Coincident(g0,g-7)
    c: Coincident(g4,g-5)
FEATURE [PartDesign::Pad] Pad163
  BaseFeature = -> Pad162
  Direction = (-1,0,0)
  Length = 2
  Length2 = 10
  Profile = -> Sketch248
  ReferenceAxis = -> Sketch248 [N_Axis]
  Refine = true
  Reversed = true
  Suppressed = false
  Type = 0
FEATURE [Sketcher::SketchObject] Sketch249
  ArcFitTolerance = 1e-06
  AttachmentSupport = -> [Pad163]
  ExternalGeometry = -> [Pad163]
  FullyConstrained = true
  MakeInternals = false
  MapMode = 5
  Placement = pos=(20,0,0) rot=(0.57735,0.57735,0.57735;2.0944rad)
  sketch-geometry (4):
    g0: LineSegment StartX=-23.2313 StartY=3 StartZ=0 EndX=-25.2313 EndY=3 EndZ=0
    g1: LineSegment StartX=-25.2313 StartY=3 StartZ=0 EndX=-25.2313 EndY=-9.8 EndZ=0
    g2: LineSegment StartX=-25.2313 StartY=-9.8 StartZ=0 EndX=-23.2313 EndY=-9.8 EndZ=0
    g3: LineSegment StartX=-23.2313 StartY=-9.8 StartZ=0 EndX=-23.2313 EndY=3 EndZ=0
  constraints (11):
    c: Coincident(g0,g1)
    c: Coincident(g1,g2)
    c: Coincident(g2,g3)
    c: Coincident(g3,g0)
    c: Horizontal(g0)
    c: Horizontal(g2)
    c: Vertical(g1)
    c: Vertical(g3)
    c: Coincident(g0,g-3)
    c: PointOnObject(g1,g-4)
    c: DistanceX(g2,g2) = 2
FEATURE [PartDesign::Pad] Pad164
  BaseFeature = -> Pad163
  Direction = (1,0,0)
  Length = 3.3
  Length2 = 10
  Profile = -> Sketch249
  ReferenceAxis = -> Sketch249 [N_Axis]
  Refine = true
  Suppressed = false
  Type = 0
FEATURE [Sketcher::SketchObject] Sketch250
  ArcFitTolerance = 1e-06
  AttachmentSupport = -> [Pad164]
  ExternalGeometry = -> [Pad164]
  FullyConstrained = true
  MakeInternals = false
  MapMode = 5
  Placement = pos=(0,-23.2313,0) rot=(0,0.707107,0.707107;3.14159rad)
  sketch-geometry (3):
    g0: LineSegment StartX=-20 StartY=-9.8 StartZ=0 EndX=-23.3 EndY=-9.8 EndZ=0
    g1: LineSegment StartX=-23.3 StartY=-9.8 StartZ=0 EndX=-23.3 EndY=-6.5 EndZ=0
    g2: LineSegment StartX=-20 StartY=-9.8 StartZ=0 EndX=-23.3 EndY=-6.5 EndZ=0
  constraints (7):
    c: Coincident(g0,g-3)
    c: Coincident(g0,g-4)
    c: Coincident(g1,g0)
    c: PointOnObject(g1,g-4)
    c: Coincident(g2,g0)
    c: Coincident(g2,g1)
    c: Angle(g2,g0) = 0.785398
FEATURE [PartDesign::Pocket] Pocket114
  BaseFeature = -> Pad164
  Direction = (0,-1,2e-16)
  Length = 5
  Length2 = 5
  Profile = -> Sketch250
  ReferenceAxis = -> Sketch250 [N_Axis]
  Refine = true
  Suppressed = false
  Type = 0
FEATURE [Sketcher::SketchObject] Sketch251
  ArcFitTolerance = 1e-06
  AttachmentSupport = -> [Pocket114]
  ExternalGeometry = -> [Pocket114]
  FullyConstrained = true
  MakeInternals = false
  MapMode = 5
  Placement = pos=(20,0,0) rot=(0.57735,0.57735,0.57735;2.0944rad)
  sketch-geometry (1):
    g0: Circle CenterX=-35 CenterY=-1.99333 CenterZ=0 NormalX=0 NormalY=0 NormalZ=1 AngleXU=0 Radius=0.8
  constraints (2):
    c: Coincident(g0,g-3)
    c: Equal(g0,g-3)
FEATURE [PartDesign::Pocket] Pocket115
  BaseFeature = -> Pocket114
  Direction = (-1,0,0)
  Length = 5
  Length2 = 5
  Profile = -> Sketch251
  ReferenceAxis = -> Sketch251 [N_Axis]
  Refine = true
  Suppressed = false
  Type = 0
FEATURE [Sketcher::SketchObject] Sketch252
  ArcFitTolerance = 1e-06
  AttachmentSupport = -> [Pocket115]
  ExternalGeometry = -> [Pocket115]
  FullyConstrained = true
  MakeInternals = false
  MapMode = 5
  Placement = pos=(29.25,0,0) rot=(0.57735,-0.57735,-0.57735;2.0944rad)
  sketch-geometry (6):
    g0: LineSegment StartX=39.505 StartY=-0.448906 StartZ=0 EndX=39.505 EndY=-6.44891 EndZ=0
    g1: LineSegment StartX=39.505 StartY=-6.44891 StartZ=0 EndX=38.005 EndY=-6.44891 EndZ=0
    g2: LineSegment StartX=38.005 StartY=-6.44891 StartZ=0 EndX=38.005 EndY=0.417119 EndZ=0
    g3: LineSegment StartX=39.505 StartY=-0.448906 StartZ=0 EndX=38.005 EndY=0.417119 EndZ=0
    g4: GeomPoint [constr] X=39.505 Y=-6.44891 Z=0
    g5: GeomPoint [constr] X=38.005 Y=-6.44891 Z=0
  constraints (14):
    c: PointOnObject(g0,g-3)
    c: Vertical(g0)
    c: Horizontal(g1)
    c: Vertical(g2)
    c: Coincident(g3,g0)
    c: Coincident(g3,g2)
    c: DistanceX(g5,g4) = 1.5
    c: PointOnObject(g2,g-3)
    c: DistanceX(g0,g-3) = 2.59
    c: DistanceY(g0,g0) = 6
    c: Coincident(g1,g5)
    c: Coincident(g2,g1)
    c: Coincident(g1,g4)
    c: Coincident(g0,g1)
FEATURE [PartDesign::Pad] Pad165
  BaseFeature = -> Pocket115
  Direction = (-1,0,0)
  Length = 3.3
  Length2 = 10
  Profile = -> Sketch252
  ReferenceAxis = -> Sketch252 [N_Axis]
  Refine = true
  Suppressed = false
  Type = 0
FEATURE [Sketcher::SketchObject] Sketch253
  ArcFitTolerance = 1e-06
  AttachmentSupport = -> [Pad165]
  ExternalGeometry = -> [Pad165]
  FullyConstrained = true
  MakeInternals = false
  MapMode = 5
  Placement = pos=(0,-38.005,0) rot=(0,0.707107,0.707107;3.14159rad)
  sketch-geometry (3):
    g0: LineSegment StartX=-29.25 StartY=-6.44891 StartZ=0 EndX=-25.95 EndY=-6.44891 EndZ=0
    g1: LineSegment StartX=-25.95 StartY=-6.44891 StartZ=0 EndX=-25.95 EndY=-5.2478 EndZ=0
    g2: LineSegment StartX=-25.95 StartY=-5.2478 StartZ=0 EndX=-29.25 EndY=-6.44891 EndZ=0
  constraints (7):
    c: Coincident(g0,g-4)
    c: Coincident(g0,g-4)
    c: Coincident(g1,g-3)
    c: PointOnObject(g1,g-3)
    c: Coincident(g2,g1)
    c: Coincident(g2,g-4)
    c: Angle(g0,g2) = 0.349066
FEATURE [PartDesign::Pocket] Pocket116
  BaseFeature = -> Pad165
  Direction = (0,-1,2e-16)
  Length = 5
  Length2 = 5
  Profile = -> Sketch253
  ReferenceAxis = -> Sketch253 [N_Axis]
  Refine = true
  Suppressed = false
  Type = 0
FEATURE [Sketcher::SketchObject] Sketch254
  ArcFitTolerance = 1e-06
  AttachmentSupport = -> [Pocket116]
  ExternalGeometry = -> [Pocket116]
  FullyConstrained = true
  MakeInternals = false
  MapMode = 5
  Placement = pos=(0,0,5) rot=(0,0,1;0rad)
  sketch-geometry (1):
    g0: Circle CenterX=24.25 CenterY=-28.2313 CenterZ=0 NormalX=0 NormalY=0 NormalZ=1 AngleXU=0 Radius=1
  constraints (3):
    c: Radius(g0) = 1
    c: DistanceX(g-5,g0) = 6.25
    c: DistanceY(g0,g-5) = 11.1
FEATURE [PartDesign::Pocket] Pocket117
  BaseFeature = -> Pocket116
  Direction = (0,0,-1)
  Length = 5
  Length2 = 5
  Profile = -> Sketch254
  ReferenceAxis = -> Sketch254 [N_Axis]
  Refine = true
  Suppressed = false
  Type = 0
FEATURE [Sketcher::SketchObject] Sketch255
  ArcFitTolerance = 1e-06
  AttachmentSupport = -> [Pocket117]
  ExternalGeometry = -> [Pocket117]
  FullyConstrained = true
  MakeInternals = false
  MapMode = 5
  Placement = pos=(31.25,0,0) rot=(0.57735,0.57735,0.57735;2.0944rad)
  sketch-geometry (24):
    g0: LineSegment StartX=-36.4313 StartY=5 StartZ=0 EndX=-17.1313 EndY=5 EndZ=0
    g1: LineSegment StartX=-17.1313 StartY=5 StartZ=0 EndX=-17.1313 EndY=-9.8 EndZ=0
    g2: LineSegment StartX=-36.4313 StartY=5 StartZ=0 EndX=-36.4313 EndY=3.63509 EndZ=0
    g3: LineSegment StartX=-36.4313 StartY=3.63509 StartZ=0 EndX=-42.6309 EndY=0.0557565 EndZ=0
    g4: LineSegment StartX=-42.6309 StartY=0.0557565 StartZ=0 EndX=-44.9561 EndY=0.0557565 EndZ=0
    g5: LineSegment StartX=-44.9561 StartY=0.0557565 StartZ=0 EndX=-44.062 EndY=-4.89651 EndZ=0
    g6: LineSegment StartX=-44.062 StartY=-4.89651 StartZ=0 EndX=-32.8313 EndY=-8.93216 EndZ=0
    g7: LineSegment StartX=-32.8313 StartY=-8.93216 StartZ=0 EndX=-32.8313 EndY=-3.6 EndZ=0
    g8: LineSegment StartX=-32.8313 StartY=-3.6 StartZ=0 EndX=-28.8813 EndY=0.35 EndZ=0
    g9: LineSegment StartX=-28.8813 StartY=0.35 StartZ=0 EndX=-22.7813 EndY=0.35 EndZ=0
    g10: LineSegment StartX=-22.7813 StartY=0.35 StartZ=0 EndX=-18.8313 EndY=-3.6 EndZ=0
    g11: LineSegment StartX=-18.8313 StartY=-3.6 StartZ=0 EndX=-18.8313 EndY=-9.8 EndZ=0
    g12: LineSegment StartX=-17.1313 StartY=-9.8 StartZ=0 EndX=-18.8313 EndY=-9.8 EndZ=0
    g13: LineSegment StartX=-34.5313 StartY=3 StartZ=0 EndX=-28.6355 EndY=3 EndZ=0
    g14: LineSegment StartX=-28.6355 StartY=3 StartZ=0 EndX=-34.5313 EndY=-2.89584 EndZ=0
    g15: LineSegment StartX=-34.5313 StartY=-2.89584 StartZ=0 EndX=-34.5313 EndY=-6.19607 EndZ=0
    g16: LineSegment StartX=-34.5313 StartY=-6.19607 StartZ=0 EndX=-41.7556 EndY=-3.60007 EndZ=0
    g17: LineSegment StartX=-42.1528 StartY=-1.40026 StartZ=0 EndX=-34.5313 EndY=3 EndZ=0
    g18: Circle CenterX=-19.7813 CenterY=2.15 CenterZ=0 NormalX=0 NormalY=0 NormalZ=1 AngleXU=0 Radius=1.45
    g19: LineSegment [constr] StartX=-29.5884 StartY=-0.357107 StartZ=0 EndX=-30.7905 EndY=0.844975 EndZ=0
    g20: LineSegment [constr] StartX=-36.5473 StartY=1.83605 StartZ=0 EndX=-37.2973 EndY=3.13509 EndZ=0
    g21: LineSegment [constr] StartX=-40.8145 StartY=-3.93824 StartZ=0 EndX=-41.4909 EndY=-5.82041 EndZ=0
    g22: LineSegment StartX=-41.7556 StartY=-3.60007 StartZ=0 EndX=-42.1528 EndY=-1.40026 EndZ=0
    g23: LineSegment [constr] StartX=-41.9751 StartY=-2.38435 StartZ=0 EndX=-44.4353 EndY=-2.82854 EndZ=0
  constraints (69):
    c: Coincident(g0,g-4)
    c: Coincident(g0,g-10)
    c: Coincident(g1,g0)
    c: Coincident(g1,g-10)
    c: Coincident(g2,g0)
    c: Coincident(g2,g-5)
    c: Coincident(g3,g2)
    c: Coincident(g3,g-6)
    c: Coincident(g4,g3)
    c: Coincident(g4,g-7)
    c: Coincident(g5,g4)
    c: Coincident(g5,g-8)
    c: Coincident(g6,g5)
    c: PointOnObject(g6,g-8)
    c: Coincident(g7,g6)
    c: Vertical(g7)
    c: Coincident(g8,g7)
    c: Coincident(g9,g8)
    c: Horizontal(g9)
    c: Coincident(g10,g9)
    c: Coincident(g11,g10)
    c: PointOnObject(g11,g-9)
    c: Vertical(g11)
    c: Coincident(g12,g1)
    c: Coincident(g12,g11)
    c: Horizontal(g13)
    c: Coincident(g14,g13)
    c: Coincident(g15,g14)
    c: Vertical(g15)
    c: Coincident(g16,g15)
    c: Coincident(g17,g13)
    c: Diameter(g18) = 2.9
    c: DistanceX(g18,g0) = 2.65
    c: DistanceY(g18,g0) = 2.85
    c: DistanceX(g12,g12) = 1.7
    c: Angle(g10,g11) = 2.35619
    c: Angle(g8,g9) = 2.35619
    c: DistanceX(g9,g9) = 6.1
    c: DistanceY(g11,g11) = 6.2
    c: DistanceY(g7,g10) = 0
    c: DistanceX(g6,g11) = 14
    c: Parallel(g8,g14)
    c: PointOnObject(g19,g8)
    c: PointOnObject(g19,g14)
    c: Angle(g19,g8) = 1.5708
    c: Distance(g19) = 1.7
    c: Distance(g8,g19) = 1
    c: Parallel(g17,g3)
    c: Parallel(g16,g6)
    c: PointOnObject(g20,g17)
    c: PointOnObject(g20,g3)
    c: PointOnObject(g21,g16)
    c: PointOnObject(g21,g6)
    c: Angle(g21,g16) = 1.5708
    c: Angle(g3,g20) = 1.5708
    c: Distance(g20,g2) = 1
    c: Distance(g21,g16) = 1
    c: Distance(g21) = 2
    c: Distance(g20) = 1.5
    c: DistanceY(g13,g0) = 2
    c: DistanceX(g15,g7) = 1.7
    c: Coincident(g22,g16)
    c: Coincident(g22,g17)
    c: Parallel(g5,g22)
    c: PointOnObject(g23,g22)
    c: PointOnObject(g23,g5)
    c: Angle(g23,g22) = 1.5708
    c: Distance(g23) = 2.5
    c: Distance(g23,g17) = 1
FEATURE [PartDesign::Pad] Pad166
  BaseFeature = -> Pocket117
  Direction = (1,0,0)
  Length = 3.5
  Length2 = 10
  Profile = -> Sketch255
  ReferenceAxis = -> Sketch255 [N_Axis]
  Refine = true
  Suppressed = false
  Type = 0
FEATURE [Sketcher::SketchObject] Sketch256
  ArcFitTolerance = 1e-06
  AttachmentSupport = -> [Pad166]
  ExternalGeometry = -> [Pad166]
  FullyConstrained = true
  MakeInternals = false
  MapMode = 5
  Placement = pos=(34.75,0,0) rot=(0.57735,0.57735,0.57735;2.0944rad)
  sketch-geometry (1):
    g0: Circle CenterX=-35 CenterY=-1.99333 CenterZ=0 NormalX=0 NormalY=0 NormalZ=1 AngleXU=0 Radius=2
  constraints (3):
    c: Radius(g-3) = 0.8
    c: Coincident(g0,g-3)
    c: Radius(g0) = 2
FEATURE [PartDesign::Pocket] Pocket118
  BaseFeature = -> Pad166
  Direction = (-1,0,0)
  Length = 1.5
  Length2 = 5
  Profile = -> Sketch256
  ReferenceAxis = -> Sketch256 [N_Axis]
  Refine = true
  Suppressed = false
  Type = 0
FEATURE [Sketcher::SketchObject] Sketch257
  ArcFitTolerance = 1e-06
  AttachmentSupport = -> [Pocket118]
  ExternalGeometry = -> [Pocket118]
  FullyConstrained = true
  MakeInternals = false
  MapMode = 5
  Placement = pos=(31.25,0,0) rot=(0.57735,0.57735,0.57735;2.0944rad)
  sketch-geometry (2):
    g0: Circle CenterX=-26.2738 CenterY=-7 CenterZ=0 NormalX=0 NormalY=0 NormalZ=1 AngleXU=0 Radius=0.8
    g1: Circle CenterX=-26.2738 CenterY=-7 CenterZ=0 NormalX=0 NormalY=0 NormalZ=1 AngleXU=0 Radius=2.25
  constraints (4):
    c: Coincident(g0,g-3)
    c: Equal(g0,g-3)
    c: Coincident(g1,g0)
    c: Radius(g1) = 2.25
FEATURE [PartDesign::Pad] Pad167
  BaseFeature = -> Pocket118
  Direction = (1,0,0)
  Length = 2
  Length2 = 10
  Profile = -> Sketch257
  ReferenceAxis = -> Sketch257 [N_Axis]
  Refine = true
  Suppressed = false
  Type = 0
FEATURE [Sketcher::SketchObject] Sketch258
  ArcFitTolerance = 1e-06
  AttachmentSupport = -> [Pad167]
  ExternalGeometry = -> [Pad167]
  FullyConstrained = false
  MakeInternals = false
  MapMode = 5
  Placement = pos=(31.25,0,0) rot=(0.57735,0.57735,0.57735;2.0944rad)
  sketch-geometry (3):
    g0: Circle CenterX=-41.1657 CenterY=-2.53692 CenterZ=0 NormalX=0 NormalY=0 NormalZ=1 AngleXU=0 Radius=0.9
    g1: LineSegment [constr] StartX=-41.1657 StartY=-2.53692 StartZ=0 EndX=-44.5116 EndY=-3.14102 EndZ=0
    g2: LineSegment [constr] StartX=-41.1657 StartY=-2.53692 StartZ=0 EndX=-42.2479 EndY=-5.54839 EndZ=0
  constraints (8):
    c: Diameter(g0) = 1.8
    c: Coincident(g1,g0)
    c: Coincident(g2,g0)
    c: PointOnObject(g2,g-4)
    c: Angle(g1,g-3) = 1.5708
    c: Angle(g-4,g2) = 1.5708
    c: Distance(g1) = 3.4
    c: Distance(g2) = 3.2
FEATURE [PartDesign::Pad] Pad168
  BaseFeature = -> Pad167
  Direction = (1,0,0)
  Length = 5
  Length2 = 10
  Profile = -> Sketch258
  ReferenceAxis = -> Sketch258 [N_Axis]
  Refine = true
  Suppressed = false
  Type = 0
FEATURE [Sketcher::SketchObject] Sketch259
  ArcFitTolerance = 1e-06
  AttachmentSupport = -> [Pad168]
  ExternalGeometry = -> [Pad168]
  FullyConstrained = true
  MakeInternals = false
  MapMode = 5
  Placement = pos=(18,0,-4.7e-15) rot=(0.57735,-0.57735,-0.57735;2.0944rad)
  sketch-geometry (4):
    g0: LineSegment StartX=44.9561 StartY=0.0557565 StartZ=0 EndX=45.0825 EndY=0.755757 EndZ=0
    g1: LineSegment StartX=45.0825 StartY=0.755757 StartZ=0 EndX=42.7573 EndY=0.755757 EndZ=0
    g2: LineSegment StartX=42.7573 StartY=0.755757 StartZ=0 EndX=42.6309 EndY=0.0557565 EndZ=0
    g3: LineSegment StartX=42.6309 StartY=0.0557565 StartZ=0 EndX=44.9561 EndY=0.0557565 EndZ=0
  constraints (10):
    c: Coincident(g0,g-4)
    c: Coincident(g1,g0)
    c: Horizontal(g1)
    c: Coincident(g2,g1)
    c: Coincident(g3,g2)
    c: Coincident(g3,g0)
    c: Angle(g-3,g0) = 3.14159
    c: Parallel(g0,g2)
    c: Coincident(g2,g-4)
    c: DistanceY(g0,g0) = 0.7
FEATURE [PartDesign::Pad] Pad169
  BaseFeature = -> Pad168
  Direction = (-1,0,0)
  Length = 2.5
  Length2 = 10
  Profile = -> Sketch259
  ReferenceAxis = -> Sketch259 [N_Axis]
  Refine = true
  Reversed = true
  Suppressed = false
  Type = 0
FEATURE [Sketcher::SketchObject] Sketch260
  ArcFitTolerance = 1e-06
  AttachmentSupport = -> [Pad169]
  ExternalGeometry = -> [Pad169]
  FullyConstrained = true
  MakeInternals = false
  MapMode = 5
  Placement = pos=(20.5,0,0) rot=(0.57735,0.57735,0.57735;2.0944rad)
  sketch-geometry (4):
    g0: LineSegment StartX=-44.0825 StartY=0.755757 StartZ=0 EndX=-43.9561 EndY=0.0557565 EndZ=0
    g1: LineSegment StartX=-43.9561 StartY=0.0557565 StartZ=0 EndX=-42.6309 EndY=0.0557565 EndZ=0
    g2: LineSegment StartX=-42.6309 StartY=0.0557565 StartZ=0 EndX=-42.7573 EndY=0.755757 EndZ=0
    g3: LineSegment StartX=-42.7573 StartY=0.755757 StartZ=0 EndX=-44.0825 EndY=0.755757 EndZ=0
  constraints (10):
    c: PointOnObject(g0,g-4)
    c: PointOnObject(g0,g-6)
    c: Coincident(g1,g0)
    c: Coincident(g1,g-6)
    c: Coincident(g2,g1)
    c: Coincident(g2,g-4)
    c: Coincident(g3,g2)
    c: Coincident(g3,g0)
    c: Parallel(g0,g-5)
    c: DistanceX(g-5,g0) = 1
FEATURE [PartDesign::Pocket] Pocket119
  BaseFeature = -> Pad169
  Direction = (-1,0,0)
  Length = 1.5
  Length2 = 5
  Profile = -> Sketch260
  ReferenceAxis = -> Sketch260 [N_Axis]
  Refine = true
  Suppressed = false
  Type = 0
FEATURE [Sketcher::SketchObject] Sketch261
  ArcFitTolerance = 1e-06
  AttachmentOffset = pos=(0,0,6.5) rot=(0,0,1;0rad)
  AttachmentSupport = -> [Pocket119]
  ExternalGeometry = -> [Pocket119]
  FullyConstrained = true
  MakeInternals = false
  MapMode = 5
  Placement = pos=(0,-42.9313,1.4e-15) rot=(1,0,0;1.5708rad)
  sketch-geometry (3):
    g0: ArcOfCircle CenterX=30.85 CenterY=0.0557565 CenterZ=0 NormalX=0 NormalY=0 NormalZ=1 AngleXU=0 Radius=1.9 StartAngle=0 EndAngle=3.14159
    g1: LineSegment StartX=32.75 StartY=0.0557565 StartZ=0 EndX=32.75 EndY=0.0557582 EndZ=0
    g2: LineSegment StartX=32.75 StartY=0.0557582 StartZ=0 EndX=28.95 EndY=0.0557565 EndZ=0
  constraints (9):
    c: PointOnObject(g0,g-3)
    c: PointOnObject(g0,g-3)
    c: PointOnObject(g0,g-3)
    c: Diameter(g0) = 3.8
    c: Tangent(g1,g0) = -1.5708
    c: PointOnObject(g1,g0)
    c: Coincident(g2,g1)
    c: Coincident(g2,g0)
    c: DistanceX(g1,g-3) = 2
FEATURE [PartDesign::Pad] Pad170
  BaseFeature = -> Pocket119
  Direction = (0,-1,2e-16)
  Length = 1
  Length2 = 10
  Profile = -> Sketch261
  ReferenceAxis = -> Sketch261 [N_Axis]
  Refine = true
  Suppressed = false
  Type = 0
FEATURE [Sketcher::SketchObject] Sketch262
  ArcFitTolerance = 1e-06
  AttachmentSupport = -> [Pad170]
  ExternalGeometry = -> [Pad170]
  FullyConstrained = true
  MakeInternals = false
  MapMode = 5
  Placement = pos=(0,-43.9313,0) rot=(1,0,0;1.5708rad)
  sketch-geometry (2):
    g0: ArcOfCircle CenterX=30.85 CenterY=0.0557565 CenterZ=0 NormalX=0 NormalY=0 NormalZ=1 AngleXU=0 Radius=1.45 StartAngle=1.06273e-06 EndAngle=3.14159
    g1: LineSegment StartX=29.4 StartY=0.0557567 StartZ=0 EndX=32.3 EndY=0.055758 EndZ=0
  constraints (6):
    c: PointOnObject(g0,g-4)
    c: Diameter(g0) = 2.9
    c: Coincident(g0,g-3)
    c: PointOnObject(g0,g-4)
    c: Coincident(g1,g0)
    c: Coincident(g1,g0)
FEATURE [PartDesign::Pad] Pad171
  BaseFeature = -> Pad170
  Direction = (0,-1,2e-16)
  Length = 0.5
  Length2 = 10
  Profile = -> Sketch262
  ReferenceAxis = -> Sketch262 [N_Axis]
  Refine = true
  Suppressed = false
  Type = 0
FEATURE [PartDesign::SubShapeBinder] Binder011
  BindCopyOnChange = 0
  BindMode = 2
  ClaimChildren = false
  Context = -> Body017 [Binder011.]
  Fuse = false
  MakeFace = true
  OffsetFill = false
  OffsetIntersection = false
  OffsetJoinType = 0
  OffsetOpenResult = false
  PartialLoad = false
  Refine = true
  Relative = true
  _Version = 2
FEATURE [Sketcher::SketchObject] Sketch263
  ArcFitTolerance = 1e-06
  AttachmentSupport = -> [Binder011]
  ExternalGeometry = -> [Binder011]
  FullyConstrained = true
  MakeInternals = false
  MapMode = 5
  Placement = pos=(29.25,0,-7.6e-15) rot=(0.57735,0.57735,0.57735;2.0944rad)
  sketch-geometry (13):
    g0: LineSegment StartX=-33.5313 StartY=3 StartZ=0 EndX=-17.1313 EndY=3 EndZ=0
    g1: LineSegment StartX=-17.1313 StartY=3 StartZ=0 EndX=-17.1313 EndY=-9.8 EndZ=0
    g2: LineSegment StartX=-17.1313 StartY=-9.8 StartZ=0 EndX=-22.1313 EndY=-9.8 EndZ=0
    g3: ArcOfCircle CenterX=-26.2738 CenterY=-7 CenterZ=0 NormalX=0 NormalY=0 NormalZ=1 AngleXU=0 Radius=5 StartAngle=3.73598 EndAngle=5.6888
    g4: LineSegment StartX=-30.4162 StartY=-9.8 StartZ=0 EndX=-44.062 EndY=-4.89651 EndZ=0
    g5: LineSegment StartX=-42.095 StartY=-1.94424 StartZ=0 EndX=-33.5313 EndY=3 EndZ=0
    g6: LineSegment [constr] StartX=-26.2738 StartY=-12 StartZ=0 EndX=-17.1313 EndY=-12 EndZ=0
    g7: LineSegment [constr] StartX=-17.1313 StartY=-9.8 StartZ=0 EndX=-17.1313 EndY=-12 EndZ=0
    g8: LineSegment [constr] StartX=-26.2738 StartY=-7 StartZ=0 EndX=-26.2738 EndY=-12 EndZ=0
    g9: LineSegment StartX=-42.095 StartY=-1.94424 StartZ=0 EndX=-44.595 EndY=-1.94424 EndZ=0
    g10: LineSegment StartX=-44.062 StartY=-4.89651 StartZ=0 EndX=-44.595 EndY=-1.94424 EndZ=0
    g11: Circle CenterX=-35 CenterY=-1.99333 CenterZ=0 NormalX=0 NormalY=0 NormalZ=1 AngleXU=0 Radius=0.8
    g12: Circle CenterX=-26.2738 CenterY=-7 CenterZ=0 NormalX=0 NormalY=0 NormalZ=1 AngleXU=0 Radius=0.8
  constraints (41):
    c: Horizontal(g0)
    c: Coincident(g1,g0)
    c: Vertical(g1)
    c: Coincident(g2,g1)
    c: Horizontal(g2)
    c: Coincident(g3,g2)
    c: Coincident(g4,g3)
    c: Coincident(g5,g0)
    c: Radius(g3) = 5
    c: DistanceY(g1,g1) = 12.8
    c: DistanceY(g2,g3) = 0
    c: PointOnObject(g6,g3)
    c: Horizontal(g6)
    c: Coincident(g7,g1)
    c: Coincident(g7,g6)
    c: Vertical(g7)
    c: DistanceY(g7,g7) = 2.2
    c: PointOnObject(g-3,g1)
    c: PointOnObject(g0,g-4)
    c: DistanceX(g0,g0) = 16.4
    c: Parallel(g5,g-5)
    c: Coincident(g8,g3)
    c: Coincident(g8,g6)
    c: Vertical(g8)
    c: Coincident(g9,g5)
    c: Horizontal(g9)
    c: Coincident(g10,g4)
    c: Coincident(g10,g9)
    c: Distance(g4) = 14.5
    c: DistanceX(g9,g9) = 2.5
    c: Angle(g4,g10) = 2.0944
    c: Distance(g10) = 3
    c: DistanceX(g2,g2) = 5
    c: DistanceX(g4,g1) = 26.9307
    c: DistanceX(g9,g0) = 27.4637
    c: DistanceX(g-6,g0) = 17.8687
    c: DistanceY(g5,g0) = 4.94424
    c: Coincident(g11,g-6)
    c: Equal(g11,g-6)
    c: Coincident(g12,g3)
    c: Radius(g12) = 0.8
FEATURE [PartDesign::Pad] Pad172
  Direction = (1,0,0)
  Length = 2
  Length2 = 10
  Profile = -> Sketch263
  ReferenceAxis = -> Sketch263 [N_Axis]
  Refine = true
  Suppressed = false
  Type = 0
FEATURE [Sketcher::SketchObject] Sketch264
  ArcFitTolerance = 1e-06
  AttachmentSupport = -> [Pad172]
  ExternalGeometry = -> [Pad172]
  FullyConstrained = true
  MakeInternals = false
  MapMode = 5
  Placement = pos=(31.25,0,0) rot=(0.57735,0.57735,0.57735;2.0944rad)
  sketch-geometry (10):
    g0: LineSegment StartX=-17.1313 StartY=3 StartZ=0 EndX=-33.5313 EndY=3 EndZ=0
    g1: LineSegment StartX=-33.5313 StartY=3 StartZ=0 EndX=-42.095 EndY=-1.94424 EndZ=0
    g2: LineSegment StartX=-17.1313 StartY=3 StartZ=0 EndX=-17.1313 EndY=5 EndZ=0
    g3: LineSegment StartX=-17.1313 StartY=5 StartZ=0 EndX=-36.4313 EndY=5 EndZ=0
    g4: LineSegment StartX=-36.4313 StartY=5 StartZ=0 EndX=-36.4313 EndY=3.63509 EndZ=0
    g5: LineSegment StartX=-36.4313 StartY=3.63509 StartZ=0 EndX=-42.6309 EndY=0.0557565 EndZ=0
    g6: LineSegment StartX=-42.6309 StartY=0.0557565 StartZ=0 EndX=-44.9561 EndY=0.0557565 EndZ=0
    g7: LineSegment StartX=-44.595 StartY=-1.94424 StartZ=0 EndX=-44.9561 EndY=0.0557565 EndZ=0
    g8: LineSegment [constr] StartX=-36.7303 StartY=1.15303 StartZ=0 EndX=-37.7303 EndY=2.88509 EndZ=0
    g9: LineSegment StartX=-42.095 StartY=-1.94424 StartZ=0 EndX=-44.595 EndY=-1.94424 EndZ=0
  constraints (27):
    c: Coincident(g0,g-4)
    c: Coincident(g0,g-5)
    c: Coincident(g1,g0)
    c: Coincident(g1,g-6)
    c: Coincident(g2,g0)
    c: Vertical(g2)
    c: Coincident(g3,g2)
    c: Horizontal(g3)
    c: DistanceX(g3,g3) = 19.3
    c: DistanceY(g2,g2) = 2
    c: Coincident(g4,g3)
    c: Vertical(g4)
    c: Coincident(g5,g4)
    c: Coincident(g6,g5)
    c: Coincident(g7,g-7)
    c: Coincident(g7,g6)
    c: DistanceY(g1,g5) = 2
    c: PointOnObject(g8,g1)
    c: PointOnObject(g8,g5)
    c: Angle(g8,g1) = 1.5708
    c: Parallel(g1,g5)
    c: Horizontal(g6)
    c: Distance(g8) = 2
    c: Angle(g7,g-7) = 3.14159
    c: Coincident(g9,g1)
    c: Coincident(g9,g7)
    c: Distance(g4,g8) = 1.5
FEATURE [PartDesign::Pad] Pad173
  BaseFeature = -> Pad172
  Direction = (1,0,0)
  Length = 13.25
  Length2 = 10
  Profile = -> Sketch264
  ReferenceAxis = -> Sketch264 [N_Axis]
  Refine = true
  Reversed = true
  Suppressed = false
  Type = 0
FEATURE [Sketcher::SketchObject] Sketch265
  ArcFitTolerance = 1e-06
  AttachmentSupport = -> [Pad173]
  ExternalGeometry = -> [Pad173]
  FullyConstrained = true
  MakeInternals = false
  MapMode = 5
  Placement = pos=(18,0,0) rot=(0.57735,-0.57735,-0.57735;2.0944rad)
  sketch-geometry (9):
    g0: LineSegment StartX=33.5313 StartY=3 StartZ=0 EndX=42.095 EndY=-1.94424 EndZ=0
    g1: LineSegment StartX=42.095 StartY=-1.94424 StartZ=0 EndX=44.595 EndY=-1.94424 EndZ=0
    g2: LineSegment StartX=44.595 StartY=-1.94424 StartZ=0 EndX=44.062 EndY=-4.89651 EndZ=0
    g3: LineSegment StartX=44.062 StartY=-4.89651 StartZ=0 EndX=30.4162 EndY=-9.8 EndZ=0
    g4: LineSegment StartX=30.4162 StartY=-9.8 StartZ=0 EndX=22.1313 EndY=-9.8 EndZ=0
    g5: LineSegment StartX=22.1313 StartY=-9.8 StartZ=0 EndX=19.2313 EndY=-2 EndZ=0
    g6: LineSegment StartX=19.2313 StartY=-2 StartZ=0 EndX=23.2313 EndY=-2 EndZ=0
    g7: LineSegment StartX=23.2313 StartY=-2 StartZ=0 EndX=23.2313 EndY=3 EndZ=0
    g8: LineSegment StartX=33.5313 StartY=3 StartZ=0 EndX=23.2313 EndY=3 EndZ=0
  constraints (21):
    c: Coincident(g0,g-8)
    c: Coincident(g1,g0)
    c: Coincident(g1,g-8)
    c: Coincident(g2,g1)
    c: Coincident(g2,g-4)
    c: Coincident(g3,g2)
    c: Coincident(g3,g-4)
    c: Coincident(g4,g3)
    c: Coincident(g5,g4)
    c: Coincident(g6,g5)
    c: Horizontal(g6)
    c: Coincident(g7,g6)
    c: Vertical(g7)
    c: Coincident(g8,g0)
    c: PointOnObject(g8,g-6)
    c: Coincident(g7,g8)
    c: DistanceY(g7,g7) = 5
    c: DistanceX(g-9,g7) = 6.1
    c: DistanceX(g6,g6) = 4
    c: Coincident(g0,g-7)
    c: Coincident(g4,g-5)
FEATURE [PartDesign::Pad] Pad174
  BaseFeature = -> Pad173
  Direction = (-1,0,0)
  Length = 2
  Length2 = 10
  Profile = -> Sketch265
  ReferenceAxis = -> Sketch265 [N_Axis]
  Refine = true
  Reversed = true
  Suppressed = false
  Type = 0
FEATURE [Sketcher::SketchObject] Sketch266
  ArcFitTolerance = 1e-06
  AttachmentSupport = -> [Pad174]
  ExternalGeometry = -> [Pad174]
  FullyConstrained = true
  MakeInternals = false
  MapMode = 5
  Placement = pos=(20,0,0) rot=(0.57735,0.57735,0.57735;2.0944rad)
  sketch-geometry (4):
    g0: LineSegment StartX=-23.2313 StartY=3 StartZ=0 EndX=-25.2313 EndY=3 EndZ=0
    g1: LineSegment StartX=-25.2313 StartY=3 StartZ=0 EndX=-25.2313 EndY=-9.8 EndZ=0
    g2: LineSegment StartX=-25.2313 StartY=-9.8 StartZ=0 EndX=-23.2313 EndY=-9.8 EndZ=0
    g3: LineSegment StartX=-23.2313 StartY=-9.8 StartZ=0 EndX=-23.2313 EndY=3 EndZ=0
  constraints (11):
    c: Coincident(g0,g1)
    c: Coincident(g1,g2)
    c: Coincident(g2,g3)
    c: Coincident(g3,g0)
    c: Horizontal(g0)
    c: Horizontal(g2)
    c: Vertical(g1)
    c: Vertical(g3)
    c: Coincident(g0,g-3)
    c: PointOnObject(g1,g-4)
    c: DistanceX(g2,g2) = 2
FEATURE [PartDesign::Pad] Pad175
  BaseFeature = -> Pad174
  Direction = (1,0,0)
  Length = 3.3
  Length2 = 10
  Profile = -> Sketch266
  ReferenceAxis = -> Sketch266 [N_Axis]
  Refine = true
  Suppressed = false
  Type = 0
FEATURE [Sketcher::SketchObject] Sketch267
  ArcFitTolerance = 1e-06
  AttachmentSupport = -> [Pad175]
  ExternalGeometry = -> [Pad175]
  FullyConstrained = true
  MakeInternals = false
  MapMode = 5
  Placement = pos=(0,-23.2313,0) rot=(0,0.707107,0.707107;3.14159rad)
  sketch-geometry (3):
    g0: LineSegment StartX=-20 StartY=-9.8 StartZ=0 EndX=-23.3 EndY=-9.8 EndZ=0
    g1: LineSegment StartX=-23.3 StartY=-9.8 StartZ=0 EndX=-23.3 EndY=-6.5 EndZ=0
    g2: LineSegment StartX=-20 StartY=-9.8 StartZ=0 EndX=-23.3 EndY=-6.5 EndZ=0
  constraints (7):
    c: Coincident(g0,g-3)
    c: Coincident(g0,g-4)
    c: Coincident(g1,g0)
    c: PointOnObject(g1,g-4)
    c: Coincident(g2,g0)
    c: Coincident(g2,g1)
    c: Angle(g2,g0) = 0.785398
FEATURE [PartDesign::Pocket] Pocket120
  BaseFeature = -> Pad175
  Direction = (0,-1,2e-16)
  Length = 5
  Length2 = 5
  Profile = -> Sketch267
  ReferenceAxis = -> Sketch267 [N_Axis]
  Refine = true
  Suppressed = false
  Type = 0
FEATURE [Sketcher::SketchObject] Sketch268
  ArcFitTolerance = 1e-06
  AttachmentSupport = -> [Pocket120]
  ExternalGeometry = -> [Pocket120]
  FullyConstrained = true
  MakeInternals = false
  MapMode = 5
  Placement = pos=(20,0,0) rot=(0.57735,0.57735,0.57735;2.0944rad)
  sketch-geometry (1):
    g0: Circle CenterX=-35 CenterY=-1.99333 CenterZ=0 NormalX=0 NormalY=0 NormalZ=1 AngleXU=0 Radius=0.8
  constraints (2):
    c: Coincident(g0,g-3)
    c: Equal(g0,g-3)
FEATURE [PartDesign::Pocket] Pocket121
  BaseFeature = -> Pocket120
  Direction = (-1,0,0)
  Length = 5
  Length2 = 5
  Profile = -> Sketch268
  ReferenceAxis = -> Sketch268 [N_Axis]
  Refine = true
  Suppressed = false
  Type = 0
FEATURE [Sketcher::SketchObject] Sketch269
  ArcFitTolerance = 1e-06
  AttachmentSupport = -> [Pocket121]
  ExternalGeometry = -> [Pocket121]
  FullyConstrained = true
  MakeInternals = false
  MapMode = 5
  Placement = pos=(29.25,0,0) rot=(0.57735,-0.57735,-0.57735;2.0944rad)
  sketch-geometry (6):
    g0: LineSegment StartX=39.505 StartY=-0.448906 StartZ=0 EndX=39.505 EndY=-6.44891 EndZ=0
    g1: LineSegment StartX=39.505 StartY=-6.44891 StartZ=0 EndX=38.005 EndY=-6.44891 EndZ=0
    g2: LineSegment StartX=38.005 StartY=-6.44891 StartZ=0 EndX=38.005 EndY=0.417119 EndZ=0
    g3: LineSegment StartX=39.505 StartY=-0.448906 StartZ=0 EndX=38.005 EndY=0.417119 EndZ=0
    g4: GeomPoint [constr] X=39.505 Y=-6.44891 Z=0
    g5: GeomPoint [constr] X=38.005 Y=-6.44891 Z=0
  constraints (14):
    c: PointOnObject(g0,g-3)
    c: Vertical(g0)
    c: Horizontal(g1)
    c: Vertical(g2)
    c: Coincident(g3,g0)
    c: Coincident(g3,g2)
    c: DistanceX(g5,g4) = 1.5
    c: PointOnObject(g2,g-3)
    c: DistanceX(g0,g-3) = 2.59
    c: DistanceY(g0,g0) = 6
    c: Coincident(g1,g5)
    c: Coincident(g2,g1)
    c: Coincident(g1,g4)
    c: Coincident(g0,g1)
FEATURE [PartDesign::Pad] Pad176
  BaseFeature = -> Pocket121
  Direction = (-1,0,0)
  Length = 3.3
  Length2 = 10
  Profile = -> Sketch269
  ReferenceAxis = -> Sketch269 [N_Axis]
  Refine = true
  Suppressed = false
  Type = 0
FEATURE [Sketcher::SketchObject] Sketch270
  ArcFitTolerance = 1e-06
  AttachmentSupport = -> [Pad176]
  ExternalGeometry = -> [Pad176]
  FullyConstrained = true
  MakeInternals = false
  MapMode = 5
  Placement = pos=(0,-38.005,0) rot=(0,0.707107,0.707107;3.14159rad)
  sketch-geometry (3):
    g0: LineSegment StartX=-29.25 StartY=-6.44891 StartZ=0 EndX=-25.95 EndY=-6.44891 EndZ=0
    g1: LineSegment StartX=-25.95 StartY=-6.44891 StartZ=0 EndX=-25.95 EndY=-5.2478 EndZ=0
    g2: LineSegment StartX=-25.95 StartY=-5.2478 StartZ=0 EndX=-29.25 EndY=-6.44891 EndZ=0
  constraints (7):
    c: Coincident(g0,g-4)
    c: Coincident(g0,g-4)
    c: Coincident(g1,g-3)
    c: PointOnObject(g1,g-3)
    c: Coincident(g2,g1)
    c: Coincident(g2,g-4)
    c: Angle(g0,g2) = 0.349066
FEATURE [PartDesign::Pocket] Pocket122
  BaseFeature = -> Pad176
  Direction = (0,-1,2e-16)
  Length = 5
  Length2 = 5
  Profile = -> Sketch270
  ReferenceAxis = -> Sketch270 [N_Axis]
  Refine = true
  Suppressed = false
  Type = 0
FEATURE [Sketcher::SketchObject] Sketch271
  ArcFitTolerance = 1e-06
  AttachmentSupport = -> [Pocket122]
  ExternalGeometry = -> [Pocket122]
  FullyConstrained = true
  MakeInternals = false
  MapMode = 5
  Placement = pos=(0,0,5) rot=(0,0,1;0rad)
  sketch-geometry (1):
    g0: Circle CenterX=24.25 CenterY=-28.2313 CenterZ=0 NormalX=0 NormalY=0 NormalZ=1 AngleXU=0 Radius=1
  constraints (3):
    c: Radius(g0) = 1
    c: DistanceX(g-5,g0) = 6.25
    c: DistanceY(g0,g-5) = 11.1
FEATURE [PartDesign::Pocket] Pocket123
  BaseFeature = -> Pocket122
  Direction = (0,0,-1)
  Length = 5
  Length2 = 5
  Profile = -> Sketch271
  ReferenceAxis = -> Sketch271 [N_Axis]
  Refine = true
  Suppressed = false
  Type = 0
FEATURE [Sketcher::SketchObject] Sketch272
  ArcFitTolerance = 1e-06
  AttachmentSupport = -> [Pocket123]
  ExternalGeometry = -> [Pocket123]
  FullyConstrained = true
  MakeInternals = false
  MapMode = 5
  Placement = pos=(31.25,0,0) rot=(0.57735,0.57735,0.57735;2.0944rad)
  sketch-geometry (24):
    g0: LineSegment StartX=-36.4313 StartY=5 StartZ=0 EndX=-17.1313 EndY=5 EndZ=0
    g1: LineSegment StartX=-17.1313 StartY=5 StartZ=0 EndX=-17.1313 EndY=-9.8 EndZ=0
    g2: LineSegment StartX=-36.4313 StartY=5 StartZ=0 EndX=-36.4313 EndY=3.63509 EndZ=0
    g3: LineSegment StartX=-36.4313 StartY=3.63509 StartZ=0 EndX=-42.6309 EndY=0.0557565 EndZ=0
    g4: LineSegment StartX=-42.6309 StartY=0.0557565 StartZ=0 EndX=-44.9561 EndY=0.0557565 EndZ=0
    g5: LineSegment StartX=-44.9561 StartY=0.0557565 StartZ=0 EndX=-44.062 EndY=-4.89651 EndZ=0
    g6: LineSegment StartX=-44.062 StartY=-4.89651 StartZ=0 EndX=-32.8313 EndY=-8.93216 EndZ=0
    g7: LineSegment StartX=-32.8313 StartY=-8.93216 StartZ=0 EndX=-32.8313 EndY=-3.6 EndZ=0
    g8: LineSegment StartX=-32.8313 StartY=-3.6 StartZ=0 EndX=-28.8813 EndY=0.35 EndZ=0
    g9: LineSegment StartX=-28.8813 StartY=0.35 StartZ=0 EndX=-22.7813 EndY=0.35 EndZ=0
    g10: LineSegment StartX=-22.7813 StartY=0.35 StartZ=0 EndX=-18.8313 EndY=-3.6 EndZ=0
    g11: LineSegment StartX=-18.8313 StartY=-3.6 StartZ=0 EndX=-18.8313 EndY=-9.8 EndZ=0
    g12: LineSegment StartX=-17.1313 StartY=-9.8 StartZ=0 EndX=-18.8313 EndY=-9.8 EndZ=0
    g13: LineSegment StartX=-34.5313 StartY=3 StartZ=0 EndX=-28.6355 EndY=3 EndZ=0
    g14: LineSegment StartX=-28.6355 StartY=3 StartZ=0 EndX=-34.5313 EndY=-2.89584 EndZ=0
    g15: LineSegment StartX=-34.5313 StartY=-2.89584 StartZ=0 EndX=-34.5313 EndY=-6.19607 EndZ=0
    g16: LineSegment StartX=-34.5313 StartY=-6.19607 StartZ=0 EndX=-41.7556 EndY=-3.60007 EndZ=0
    g17: LineSegment StartX=-42.1528 StartY=-1.40026 StartZ=0 EndX=-34.5313 EndY=3 EndZ=0
    g18: Circle CenterX=-19.7813 CenterY=2.15 CenterZ=0 NormalX=0 NormalY=0 NormalZ=1 AngleXU=0 Radius=1.45
    g19: LineSegment [constr] StartX=-29.5884 StartY=-0.357107 StartZ=0 EndX=-30.7905 EndY=0.844975 EndZ=0
    g20: LineSegment [constr] StartX=-36.5473 StartY=1.83605 StartZ=0 EndX=-37.2973 EndY=3.13509 EndZ=0
    g21: LineSegment [constr] StartX=-40.8145 StartY=-3.93824 StartZ=0 EndX=-41.4909 EndY=-5.82041 EndZ=0
    g22: LineSegment StartX=-41.7556 StartY=-3.60007 StartZ=0 EndX=-42.1528 EndY=-1.40026 EndZ=0
    g23: LineSegment [constr] StartX=-41.9751 StartY=-2.38435 StartZ=0 EndX=-44.4353 EndY=-2.82854 EndZ=0
  constraints (69):
    c: Coincident(g0,g-4)
    c: Coincident(g0,g-10)
    c: Coincident(g1,g0)
    c: Coincident(g1,g-10)
    c: Coincident(g2,g0)
    c: Coincident(g2,g-5)
    c: Coincident(g3,g2)
    c: Coincident(g3,g-6)
    c: Coincident(g4,g3)
    c: Coincident(g4,g-7)
    c: Coincident(g5,g4)
    c: Coincident(g5,g-8)
    c: Coincident(g6,g5)
    c: PointOnObject(g6,g-8)
    c: Coincident(g7,g6)
    c: Vertical(g7)
    c: Coincident(g8,g7)
    c: Coincident(g9,g8)
    c: Horizontal(g9)
    c: Coincident(g10,g9)
    c: Coincident(g11,g10)
    c: PointOnObject(g11,g-9)
    c: Vertical(g11)
    c: Coincident(g12,g1)
    c: Coincident(g12,g11)
    c: Horizontal(g13)
    c: Coincident(g14,g13)
    c: Coincident(g15,g14)
    c: Vertical(g15)
    c: Coincident(g16,g15)
    c: Coincident(g17,g13)
    c: Diameter(g18) = 2.9
    c: DistanceX(g18,g0) = 2.65
    c: DistanceY(g18,g0) = 2.85
    c: DistanceX(g12,g12) = 1.7
    c: Angle(g10,g11) = 2.35619
    c: Angle(g8,g9) = 2.35619
    c: DistanceX(g9,g9) = 6.1
    c: DistanceY(g11,g11) = 6.2
    c: DistanceY(g7,g10) = 0
    c: DistanceX(g6,g11) = 14
    c: Parallel(g8,g14)
    c: PointOnObject(g19,g8)
    c: PointOnObject(g19,g14)
    c: Angle(g19,g8) = 1.5708
    c: Distance(g19) = 1.7
    c: Distance(g8,g19) = 1
    c: Parallel(g17,g3)
    c: Parallel(g16,g6)
    c: PointOnObject(g20,g17)
    c: PointOnObject(g20,g3)
    c: PointOnObject(g21,g16)
    c: PointOnObject(g21,g6)
    c: Angle(g21,g16) = 1.5708
    c: Angle(g3,g20) = 1.5708
    c: Distance(g20,g2) = 1
    c: Distance(g21,g16) = 1
    c: Distance(g21) = 2
    c: Distance(g20) = 1.5
    c: DistanceY(g13,g0) = 2
    c: DistanceX(g15,g7) = 1.7
    c: Coincident(g22,g16)
    c: Coincident(g22,g17)
    c: Parallel(g5,g22)
    c: PointOnObject(g23,g22)
    c: PointOnObject(g23,g5)
    c: Angle(g23,g22) = 1.5708
    c: Distance(g23) = 2.5
    c: Distance(g23,g17) = 1
FEATURE [PartDesign::Pad] Pad177
  BaseFeature = -> Pocket123
  Direction = (1,0,0)
  Length = 3.5
  Length2 = 10
  Profile = -> Sketch272
  ReferenceAxis = -> Sketch272 [N_Axis]
  Refine = true
  Suppressed = false
  Type = 0
FEATURE [Sketcher::SketchObject] Sketch273
  ArcFitTolerance = 1e-06
  AttachmentSupport = -> [Pad177]
  ExternalGeometry = -> [Pad177]
  FullyConstrained = true
  MakeInternals = false
  MapMode = 5
  Placement = pos=(34.75,0,0) rot=(0.57735,0.57735,0.57735;2.0944rad)
  sketch-geometry (1):
    g0: Circle CenterX=-35 CenterY=-1.99333 CenterZ=0 NormalX=0 NormalY=0 NormalZ=1 AngleXU=0 Radius=2
  constraints (3):
    c: Radius(g-3) = 0.8
    c: Coincident(g0,g-3)
    c: Radius(g0) = 2
FEATURE [PartDesign::Pocket] Pocket124
  BaseFeature = -> Pad177
  Direction = (-1,0,0)
  Length = 1.5
  Length2 = 5
  Profile = -> Sketch273
  ReferenceAxis = -> Sketch273 [N_Axis]
  Refine = true
  Suppressed = false
  Type = 0
FEATURE [Sketcher::SketchObject] Sketch274
  ArcFitTolerance = 1e-06
  AttachmentSupport = -> [Pocket124]
  ExternalGeometry = -> [Pocket124]
  FullyConstrained = true
  MakeInternals = false
  MapMode = 5
  Placement = pos=(31.25,0,0) rot=(0.57735,0.57735,0.57735;2.0944rad)
  sketch-geometry (2):
    g0: Circle CenterX=-26.2738 CenterY=-7 CenterZ=0 NormalX=0 NormalY=0 NormalZ=1 AngleXU=0 Radius=0.8
    g1: Circle CenterX=-26.2738 CenterY=-7 CenterZ=0 NormalX=0 NormalY=0 NormalZ=1 AngleXU=0 Radius=2.25
  constraints (4):
    c: Coincident(g0,g-3)
    c: Equal(g0,g-3)
    c: Coincident(g1,g0)
    c: Radius(g1) = 2.25
FEATURE [PartDesign::Pad] Pad178
  BaseFeature = -> Pocket124
  Direction = (1,0,0)
  Length = 2
  Length2 = 10
  Profile = -> Sketch274
  ReferenceAxis = -> Sketch274 [N_Axis]
  Refine = true
  Suppressed = false
  Type = 0
FEATURE [Sketcher::SketchObject] Sketch275
  ArcFitTolerance = 1e-06
  AttachmentSupport = -> [Pad178]
  ExternalGeometry = -> [Pad178]
  FullyConstrained = false
  MakeInternals = false
  MapMode = 5
  Placement = pos=(31.25,0,0) rot=(0.57735,0.57735,0.57735;2.0944rad)
  sketch-geometry (3):
    g0: Circle CenterX=-41.1657 CenterY=-2.53692 CenterZ=0 NormalX=0 NormalY=0 NormalZ=1 AngleXU=0 Radius=0.9
    g1: LineSegment [constr] StartX=-41.1657 StartY=-2.53692 StartZ=0 EndX=-44.5116 EndY=-3.14102 EndZ=0
    g2: LineSegment [constr] StartX=-41.1657 StartY=-2.53692 StartZ=0 EndX=-42.2479 EndY=-5.54839 EndZ=0
  constraints (8):
    c: Diameter(g0) = 1.8
    c: Coincident(g1,g0)
    c: Coincident(g2,g0)
    c: PointOnObject(g2,g-4)
    c: Angle(g1,g-3) = 1.5708
    c: Angle(g-4,g2) = 1.5708
    c: Distance(g1) = 3.4
    c: Distance(g2) = 3.2
FEATURE [PartDesign::Pad] Pad179
  BaseFeature = -> Pad178
  Direction = (1,0,0)
  Length = 5
  Length2 = 10
  Profile = -> Sketch275
  ReferenceAxis = -> Sketch275 [N_Axis]
  Refine = true
  Suppressed = false
  Type = 0
FEATURE [Sketcher::SketchObject] Sketch276
  ArcFitTolerance = 1e-06
  AttachmentSupport = -> [Pad179]
  ExternalGeometry = -> [Pad179]
  FullyConstrained = true
  MakeInternals = false
  MapMode = 5
  Placement = pos=(18,0,-4.7e-15) rot=(0.57735,-0.57735,-0.57735;2.0944rad)
  sketch-geometry (4):
    g0: LineSegment StartX=44.9561 StartY=0.0557565 StartZ=0 EndX=45.0825 EndY=0.755757 EndZ=0
    g1: LineSegment StartX=45.0825 StartY=0.755757 StartZ=0 EndX=42.7573 EndY=0.755757 EndZ=0
    g2: LineSegment StartX=42.7573 StartY=0.755757 StartZ=0 EndX=42.6309 EndY=0.0557565 EndZ=0
    g3: LineSegment StartX=42.6309 StartY=0.0557565 StartZ=0 EndX=44.9561 EndY=0.0557565 EndZ=0
  constraints (10):
    c: Coincident(g0,g-4)
    c: Coincident(g1,g0)
    c: Horizontal(g1)
    c: Coincident(g2,g1)
    c: Coincident(g3,g2)
    c: Coincident(g3,g0)
    c: Angle(g-3,g0) = 3.14159
    c: Parallel(g0,g2)
    c: Coincident(g2,g-4)
    c: DistanceY(g0,g0) = 0.7
FEATURE [PartDesign::Pad] Pad180
  BaseFeature = -> Pad179
  Direction = (-1,0,0)
  Length = 2.5
  Length2 = 10
  Profile = -> Sketch276
  ReferenceAxis = -> Sketch276 [N_Axis]
  Refine = true
  Reversed = true
  Suppressed = false
  Type = 0
FEATURE [Sketcher::SketchObject] Sketch277
  ArcFitTolerance = 1e-06
  AttachmentSupport = -> [Pad180]
  ExternalGeometry = -> [Pad180]
  FullyConstrained = true
  MakeInternals = false
  MapMode = 5
  Placement = pos=(20.5,0,0) rot=(0.57735,0.57735,0.57735;2.0944rad)
  sketch-geometry (4):
    g0: LineSegment StartX=-44.0825 StartY=0.755757 StartZ=0 EndX=-43.9561 EndY=0.0557565 EndZ=0
    g1: LineSegment StartX=-43.9561 StartY=0.0557565 StartZ=0 EndX=-42.6309 EndY=0.0557565 EndZ=0
    g2: LineSegment StartX=-42.6309 StartY=0.0557565 StartZ=0 EndX=-42.7573 EndY=0.755757 EndZ=0
    g3: LineSegment StartX=-42.7573 StartY=0.755757 StartZ=0 EndX=-44.0825 EndY=0.755757 EndZ=0
  constraints (10):
    c: PointOnObject(g0,g-4)
    c: PointOnObject(g0,g-6)
    c: Coincident(g1,g0)
    c: Coincident(g1,g-6)
    c: Coincident(g2,g1)
    c: Coincident(g2,g-4)
    c: Coincident(g3,g2)
    c: Coincident(g3,g0)
    c: Parallel(g0,g-5)
    c: DistanceX(g-5,g0) = 1
FEATURE [PartDesign::Pocket] Pocket125
  BaseFeature = -> Pad180
  Direction = (-1,0,0)
  Length = 1.5
  Length2 = 5
  Profile = -> Sketch277
  ReferenceAxis = -> Sketch277 [N_Axis]
  Refine = true
  Suppressed = false
  Type = 0
FEATURE [PartDesign::SubShapeBinder] Binder012
  BindCopyOnChange = 0
  BindMode = 0
  ClaimChildren = false
  Context = -> Body018 [Binder012.]
  Fuse = false
  MakeFace = true
  OffsetFill = false
  OffsetIntersection = false
  OffsetJoinType = 0
  OffsetOpenResult = false
  PartialLoad = false
  Refine = true
  Relative = true
  Support = -> [Body016[Pad171.Face23]]
  _Version = 2
FEATURE [Sketcher::SketchObject] Sketch278
  ArcFitTolerance = 1e-06
  AttachmentSupport = -> [Binder012]
  ExternalGeometry = -> [Binder012]
  FullyConstrained = true
  MakeInternals = false
  MapMode = 5
  Placement = pos=(0,0,5) rot=(0,0,1;0rad)
  sketch-geometry (5):
    g0: LineSegment StartX=18 StartY=-17.1313 StartZ=0 EndX=18 EndY=-36.4313 EndZ=0
    g1: LineSegment StartX=18 StartY=-36.4313 StartZ=0 EndX=36.25 EndY=-36.4313 EndZ=0
    g2: LineSegment StartX=36.25 StartY=-36.4313 StartZ=0 EndX=36.25 EndY=-17.1313 EndZ=0
    g3: LineSegment StartX=36.25 StartY=-17.1313 StartZ=0 EndX=18 EndY=-17.1313 EndZ=0
    g4: Circle CenterX=24.25 CenterY=-28.2313 CenterZ=0 NormalX=0 NormalY=0 NormalZ=1 AngleXU=0 Radius=0.75
  constraints (13):
    c: Coincident(g0,g1)
    c: Coincident(g1,g2)
    c: Coincident(g2,g3)
    c: Coincident(g3,g0)
    c: Vertical(g0)
    c: Vertical(g2)
    c: Horizontal(g1)
    c: Horizontal(g3)
    c: Coincident(g0,g-6)
    c: PointOnObject(g-7,g1)
    c: DistanceX(g-5,g2) = 1.5
    c: Coincident(g4,g-3)
    c: Radius(g4) = 0.75
FEATURE [PartDesign::Pad] Pad181
  Direction = (0,0,1)
  Length = 1.5
  Length2 = 10
  Profile = -> Sketch278
  ReferenceAxis = -> Sketch278 [N_Axis]
  Refine = true
  Suppressed = false
  Type = 0
FEATURE [Sketcher::SketchObject] Sketch279
  ArcFitTolerance = 1e-06
  AttachmentSupport = -> [Pad181]
  ExternalGeometry = -> [Pad181]
  FullyConstrained = true
  MakeInternals = false
  MapMode = 5
  Placement = pos=(0,-17.1313,0) rot=(0,0.707107,0.707107;3.14159rad)
  sketch-geometry (6):
    g0: LineSegment StartX=-18 StartY=6.5 StartZ=0 EndX=-18 EndY=3 EndZ=0
    g1: LineSegment StartX=-18 StartY=3 StartZ=0 EndX=-29.25 EndY=3 EndZ=0
    g2: LineSegment StartX=-29.25 StartY=3 StartZ=0 EndX=-29.25 EndY=-9.8 EndZ=0
    g3: LineSegment StartX=-29.25 StartY=-9.8 StartZ=0 EndX=-36.25 EndY=-9.8 EndZ=0
    g4: LineSegment StartX=-36.25 StartY=-9.8 StartZ=0 EndX=-36.25 EndY=6.5 EndZ=0
    g5: LineSegment StartX=-36.25 StartY=6.5 StartZ=0 EndX=-18 EndY=6.5 EndZ=0
  constraints (16):
    c: Coincident(g0,g-4)
    c: Vertical(g0)
    c: Coincident(g1,g0)
    c: Horizontal(g1)
    c: Coincident(g2,g1)
    c: Vertical(g2)
    c: Coincident(g3,g2)
    c: Horizontal(g3)
    c: Coincident(g4,g3)
    c: Coincident(g4,g-6)
    c: Coincident(g5,g4)
    c: Coincident(g5,g0)
    c: Vertical(g4)
    c: DistanceY(g0,g0) = 3.5
    c: DistanceY(g2,g2) = 12.8
    c: DistanceX(g1,g1) = 11.25
FEATURE [PartDesign::Pad] Pad182
  BaseFeature = -> Pad181
  Direction = (0,1,-2e-16)
  Length = 1.5
  Length2 = 10
  Profile = -> Sketch279
  ReferenceAxis = -> Sketch279 [N_Axis]
  Refine = true
  Suppressed = false
  Type = 0
FEATURE [Sketcher::SketchObject] Sketch280
  ArcFitTolerance = 1e-06
  AttachmentSupport = -> [Pad182]
  ExternalGeometry = -> [Pad182]
  FullyConstrained = true
  MakeInternals = false
  MapMode = 5
  Placement = pos=(36.25,1.31e-14,-1.66e-14) rot=(0.57735,0.57735,0.57735;2.0944rad)
  sketch-geometry (13):
    g0: LineSegment StartX=-36.4313 StartY=5 StartZ=0 EndX=-17.1313 EndY=5 EndZ=0
    g1: LineSegment StartX=-17.1313 StartY=5 StartZ=0 EndX=-17.1313 EndY=-9.8 EndZ=0
    g2: LineSegment StartX=-17.1313 StartY=-9.8 StartZ=0 EndX=-18.8313 EndY=-9.8 EndZ=0
    g3: LineSegment StartX=-18.8313 StartY=-9.8 StartZ=0 EndX=-18.8313 EndY=-3.6 EndZ=0
    g4: LineSegment StartX=-18.8313 StartY=-3.6 StartZ=0 EndX=-22.784 EndY=0.352727 EndZ=0
    g5: LineSegment StartX=-22.784 StartY=0.352727 StartZ=0 EndX=-28.884 EndY=0.352727 EndZ=0
    g6: LineSegment StartX=-28.884 StartY=0.352727 StartZ=0 EndX=-32.8368 EndY=-3.6 EndZ=0
    g7: LineSegment StartX=-32.8368 StartY=-3.6 StartZ=0 EndX=-32.8368 EndY=-8.93 EndZ=0
    g8: LineSegment StartX=-32.8368 StartY=-8.93 StartZ=0 EndX=-44.0636 EndY=-4.89473 EndZ=0
    g9: LineSegment StartX=-44.0636 StartY=-4.89473 StartZ=0 EndX=-44.9569 EndY=0.0553024 EndZ=0
    g10: LineSegment StartX=-44.9569 StartY=0.0553024 StartZ=0 EndX=-36.4313 EndY=6.5 EndZ=0
    g11: LineSegment StartX=-36.4313 StartY=6.5 StartZ=0 EndX=-36.4313 EndY=5 EndZ=0
    g12: Circle CenterX=-41.1636 CenterY=-2.53473 CenterZ=0 NormalX=0 NormalY=0 NormalZ=1 AngleXU=0 Radius=0.95
  constraints (36):
    c: Coincident(g0,g-3)
    c: Coincident(g0,g-4)
    c: Coincident(g1,g0)
    c: Coincident(g1,g-4)
    c: Coincident(g2,g1)
    c: Horizontal(g2)
    c: Coincident(g3,g2)
    c: Vertical(g3)
    c: Coincident(g4,g3)
    c: Coincident(g5,g4)
    c: Horizontal(g5)
    c: Coincident(g6,g5)
    c: Coincident(g7,g6)
    c: Vertical(g7)
    c: Coincident(g8,g7)
    c: Coincident(g9,g8)
    c: Coincident(g10,g9)
    c: Coincident(g11,g10)
    c: Coincident(g11,g0)
    c: Vertical(g11)
    c: DistanceX(g2,g2) = 1.7
    c: DistanceY(g3,g3) = 6.2
    c: DistanceX(g5,g5) = 6.1
    c: Angle(g4,g3) = 2.35619
    c: Angle(g6,g5) = 2.35619
    c: Distance(g4) = 5.59
    c: Distance(g6) = 5.59
    c: DistanceY(g11,g11) = 1.5
    c: DistanceY(g7,g7) = 5.33
    c: Distance(g8) = 11.93
    c: Angle(g7,g8) = 1.22574
    c: Distance(g9) = 5.03
    c: Angle(g8,g9) = 2.0944
    c: Radius(g12) = 0.95
    c: DistanceX(g8,g12) = 2.9
    c: DistanceY(g8,g12) = 2.36
FEATURE [PartDesign::Pad] Pad183
  BaseFeature = -> Pad182
  Direction = (1,0,0)
  Length = 1.5
  Length2 = 10
  Profile = -> Sketch280
  ReferenceAxis = -> Sketch280 [N_Axis]
  Refine = true
  Reversed = true
  Suppressed = false
  Type = 0
FEATURE [Sketcher::SketchObject] Sketch281
  ArcFitTolerance = 1e-06
  AttachmentSupport = -> [Pad183]
  ExternalGeometry = -> [Pad183]
  FullyConstrained = true
  MakeInternals = false
  MapMode = 5
  Placement = pos=(0,0,6.5) rot=(0,0,1;0rad)
  sketch-geometry (4):
    g0: LineSegment StartX=36.25 StartY=-15.6313 StartZ=0 EndX=34.75 EndY=-15.6313 EndZ=0
    g1: LineSegment StartX=34.75 StartY=-15.6313 StartZ=0 EndX=34.75 EndY=-36.4313 EndZ=0
    g2: LineSegment StartX=34.75 StartY=-36.4313 StartZ=0 EndX=36.25 EndY=-36.4313 EndZ=0
    g3: LineSegment StartX=36.25 StartY=-36.4313 StartZ=0 EndX=36.25 EndY=-15.6313 EndZ=0
  constraints (10):
    c: Coincident(g0,g1)
    c: Coincident(g1,g2)
    c: Coincident(g2,g3)
    c: Coincident(g3,g0)
    c: Horizontal(g0)
    c: Horizontal(g2)
    c: Vertical(g1)
    c: Vertical(g3)
    c: Coincident(g0,g-5)
    c: Coincident(g1,g-4)
FEATURE [PartDesign::Pad] Pad184
  BaseFeature = -> Pad183
  Direction = (0,0,1)
  Length = 2
  Length2 = 10
  Profile = -> Sketch281
  ReferenceAxis = -> Sketch281 [N_Axis]
  Refine = true
  Suppressed = false
  Type = 0
FEATURE [Sketcher::SketchObject] Sketch282
  ArcFitTolerance = 1e-06
  AttachmentSupport = -> [Pad184]
  ExternalGeometry = -> [Pad184]
  FullyConstrained = true
  MakeInternals = false
  MapMode = 5
  Placement = pos=(36.25,0,0) rot=(0.57735,0.57735,0.57735;2.0944rad)
  sketch-geometry (6):
    g0: LineSegment StartX=-15.6313 StartY=8.5 StartZ=0 EndX=-15.6313 EndY=6.5 EndZ=0
    g1: LineSegment StartX=-15.6313 StartY=8.5 StartZ=0 EndX=-17.6313 EndY=8.5 EndZ=0
    g2: LineSegment StartX=-17.6313 StartY=8.5 StartZ=0 EndX=-15.6313 EndY=6.5 EndZ=0
    g3: LineSegment StartX=-36.4313 StartY=6.5 StartZ=0 EndX=-36.4313 EndY=8.5 EndZ=0
    g4: LineSegment StartX=-36.4313 StartY=8.5 StartZ=0 EndX=-33.7855 EndY=8.5 EndZ=0
    g5: LineSegment StartX=-33.7855 StartY=8.5 StartZ=0 EndX=-36.4313 EndY=6.5 EndZ=0
  constraints (15):
    c: Coincident(g0,g-6)
    c: PointOnObject(g0,g-6)
    c: Coincident(g1,g0)
    c: PointOnObject(g1,g-4)
    c: Coincident(g2,g1)
    c: Coincident(g2,g0)
    c: Coincident(g3,g-5)
    c: Coincident(g3,g-4)
    c: Coincident(g4,g3)
    c: PointOnObject(g4,g-4)
    c: Coincident(g5,g4)
    c: Coincident(g5,g3)
    c: Angle(g-5,g5) = 3.14159
    c: DistanceY(g0,g0) = 2
    c: DistanceX(g1,g1) = 2
FEATURE [PartDesign::Pocket] Pocket126
  BaseFeature = -> Pad184
  Direction = (-1,0,0)
  Length = 5
  Length2 = 5
  Profile = -> Sketch282
  ReferenceAxis = -> Sketch282 [N_Axis]
  Refine = true
  Suppressed = false
  Type = 0
FEATURE [Sketcher::SketchObject] Sketch283
  ArcFitTolerance = 1e-06
  AttachmentSupport = -> [Pocket126]
  FullyConstrained = true
  MakeInternals = false
  MapMode = 5
  Placement = pos=(0,0,6.5) rot=(0,0,1;0rad)
  sketch-geometry (1):
    g0: Circle CenterX=24.25 CenterY=-28.2313 CenterZ=0 NormalX=0 NormalY=0 NormalZ=1 AngleXU=0 Radius=2.6
  constraints (2):
    c: Coincident(g0,g-3)
    c: Diameter(g0) = 5.2
FEATURE [PartDesign::Pad] Pad185
  BaseFeature = -> Pocket126
  Direction = (0,0,1)
  Length = 4
  Length2 = 10
  Profile = -> Sketch283
  ReferenceAxis = -> Sketch283 [N_Axis]
  Refine = true
  Suppressed = false
  Type = 0
FEATURE [PartDesign::Pocket] Pocket127
  BaseFeature = -> Pad185
  Direction = (0,0,1)
  Length = 2
  Length2 = 5
  Profile = -> Pad185 [Face27]
  Refine = true
  Suppressed = false
  Type = 0
FEATURE [Sketcher::SketchObject] Sketch284
  ArcFitTolerance = 1e-06
  AttachmentSupport = -> [Pocket127]
  ExternalGeometry = -> [Pocket127]
  FullyConstrained = true
  MakeInternals = false
  MapMode = 5
  Placement = pos=(0,0,6.5) rot=(0,0,1;0rad)
  sketch-geometry (4):
    g0: LineSegment StartX=26.85 StartY=-28.2313 StartZ=0 EndX=26.85 EndY=-34.0313 EndZ=0
    g1: LineSegment StartX=26.85 StartY=-34.0313 StartZ=0 EndX=32.65 EndY=-34.0313 EndZ=0
    g2: LineSegment StartX=32.65 StartY=-34.0313 StartZ=0 EndX=32.65 EndY=-28.2313 EndZ=0
    g3: LineSegment StartX=32.65 StartY=-28.2313 StartZ=0 EndX=26.85 EndY=-28.2313 EndZ=0
  constraints (11):
    c: Coincident(g0,g1)
    c: Coincident(g1,g2)
    c: Coincident(g2,g3)
    c: Coincident(g3,g0)
    c: Vertical(g0)
    c: Vertical(g2)
    c: Horizontal(g1)
    c: Horizontal(g3)
    c: Coincident(g0,g-4)
    c: DistanceX(g3,g3) = 5.8
    c: DistanceY(g2,g2) = 5.8
FEATURE [PartDesign::Pad] Pad186
  BaseFeature = -> Pocket127
  Direction = (0,0,1)
  Length = 4
  Length2 = 10
  Profile = -> Sketch284
  ReferenceAxis = -> Sketch284 [N_Axis]
  Refine = true
  Suppressed = false
  Type = 0
FEATURE [Sketcher::SketchObject] Sketch285
  ArcFitTolerance = 1e-06
  AttachmentSupport = -> [Pad186]
  ExternalGeometry = -> [Pad186]
  FullyConstrained = true
  MakeInternals = false
  MapMode = 5
  Placement = pos=(0,0,6.5) rot=(0,0,1;0rad)
  sketch-geometry (4):
    g0: LineSegment [constr] StartX=24.25 StartY=-28.2313 StartZ=0 EndX=24.25 EndY=-30.8313 EndZ=0
    g1: LineSegment StartX=24.25 StartY=-30.8313 StartZ=0 EndX=26.85 EndY=-30.8313 EndZ=0
    g2: LineSegment StartX=26.85 StartY=-30.8313 StartZ=0 EndX=26.85 EndY=-28.2313 EndZ=0
    g3: ArcOfCircle CenterX=24.25 CenterY=-28.2313 CenterZ=0 NormalX=0 NormalY=0 NormalZ=1 AngleXU=0 Radius=2.6 StartAngle=4.71239 EndAngle=6.28319
  constraints (11):
    c: Coincident(g0,g-3)
    c: PointOnObject(g0,g-3)
    c: Vertical(g0)
    c: Coincident(g1,g0)
    c: PointOnObject(g1,g-5)
    c: Horizontal(g1)
    c: Coincident(g2,g1)
    c: Coincident(g2,g-5)
    c: Coincident(g3,g2)
    c: Coincident(g3,g0)
    c: Tangent(g3,g-3)
FEATURE [PartDesign::Pad] Pad187
  BaseFeature = -> Pad186
  Direction = (0,0,1)
  Length = 4
  Length2 = 10
  Profile = -> Sketch285
  ReferenceAxis = -> Sketch285 [N_Axis]
  Refine = true
  Suppressed = false
  Type = 0
FEATURE [Sketcher::SketchObject] Sketch286
  ArcFitTolerance = 1e-06
  AttachmentSupport = -> [Pad187]
  ExternalGeometry = -> [Pad187]
  FullyConstrained = true
  MakeInternals = false
  MapMode = 5
  Placement = pos=(0,0,10.5) rot=(0,0,1;0rad)
  sketch-geometry (1):
    g0: Circle CenterX=29.75 CenterY=-31.1313 CenterZ=0 NormalX=0 NormalY=0 NormalZ=1 AngleXU=0 Radius=1.45
  constraints (4):
    c: DistanceX(g-3,g-3) = 5.8
    c: DistanceX(g0,g-4) = 2.9
    c: DistanceY(g0,g-4) = 2.9
    c: Radius(g0) = 1.45
FEATURE [PartDesign::Pocket] Pocket128
  BaseFeature = -> Pad187
  Direction = (0,0,-1)
  Length = 4
  Length2 = 5
  Profile = -> Sketch286
  ReferenceAxis = -> Sketch286 [N_Axis]
  Refine = true
  Suppressed = false
  Type = 0
FEATURE [Sketcher::SketchObject] Sketch287
  ArcFitTolerance = 1e-06
  AttachmentSupport = -> [Pocket128]
  ExternalGeometry = -> [Pocket128]
  FullyConstrained = true
  MakeInternals = false
  MapMode = 5
  Placement = pos=(36.25,0,0) rot=(0.57735,0.57735,0.57735;2.0944rad)
  sketch-geometry (9):
    g0: LineSegment StartX=-15.6313 StartY=3.5 StartZ=0 EndX=-15.6313 EndY=3.3 EndZ=0
    g1: LineSegment StartX=-15.6313 StartY=3.3 StartZ=0 EndX=-28.884 EndY=3.3 EndZ=0
    g2: LineSegment StartX=-28.884 StartY=3.3 StartZ=0 EndX=-32.3287 EndY=-0.144698 EndZ=0
    g3: LineSegment StartX=-32.3287 StartY=-0.144698 StartZ=0 EndX=-44.9208 EndY=-0.144698 EndZ=0
    g4: LineSegment StartX=-44.9208 StartY=-0.144698 StartZ=0 EndX=-44.9569 EndY=0.0553024 EndZ=0
    g5: LineSegment StartX=-44.9569 StartY=0.0553024 StartZ=0 EndX=-32.4116 EndY=0.0553024 EndZ=0
    g6: LineSegment StartX=-32.4116 StartY=0.0553024 StartZ=0 EndX=-28.9669 EndY=3.5 EndZ=0
    g7: LineSegment StartX=-28.9669 StartY=3.5 StartZ=0 EndX=-15.6313 EndY=3.5 EndZ=0
    g8: LineSegment [constr] StartX=-29.5326 StartY=2.65147 StartZ=0 EndX=-29.674 EndY=2.79289 EndZ=0
  constraints (27):
    c: PointOnObject(g0,g-8)
    c: PointOnObject(g0,g-8)
    c: Coincident(g1,g0)
    c: Horizontal(g1)
    c: Coincident(g2,g1)
    c: Coincident(g3,g2)
    c: PointOnObject(g3,g-4)
    c: Horizontal(g3)
    c: Coincident(g4,g3)
    c: Coincident(g5,g4)
    c: Horizontal(g5)
    c: Coincident(g6,g5)
    c: Coincident(g7,g6)
    c: Coincident(g7,g0)
    c: Horizontal(g7)
    c: DistanceY(g0,g0) = 0.2
    c: DistanceY(g0,g-8) = 3
    c: DistanceX(g1,g-7) = 0
    c: Coincident(g4,g-4)
    c: Parallel(g2,g6)
    c: PointOnObject(g8,g2)
    c: PointOnObject(g8,g6)
    c: Angle(g6,g8) = 1.5708
    c: Distance(g8) = 0.2
    c: Angle(g2,g1) = 2.35619
    c: DistanceY(g2,g5) = 0.2
    c: Distance(g8,g6) = 1
FEATURE [PartDesign::Pocket] Pocket129
  BaseFeature = -> Pocket128
  Direction = (-1,0,0)
  Length = 0.3
  Length2 = 5
  Profile = -> Sketch287
  ReferenceAxis = -> Sketch287 [N_Axis]
  Refine = true
  Suppressed = false
  Type = 0
FEATURE [PartDesign::Body] Body018  label="Right_Outer_Leg"
  AllowCompound = false
  Group = -> [Binder012,Sketch278,Pad181,Sketch279,Pad182,Sketch280,Pad183,Sketch281,Pad184,Sketch282,Pocket126,Sketch283,Pad185,Pocket127,Sketch284,Pad186,Sketch285,Pad187,Sketch286,Pocket128,Sketch287,Pocket129]
  Origin = -> Origin019
  Placement = pos=(0,8.9e-15,0) rot=(0,0,1;0rad)
  Tip = -> Pocket129
FEATURE [PartDesign::SubShapeBinder] Binder013
  BindCopyOnChange = 0
  BindMode = 0
  ClaimChildren = false
  Context = -> Body019 [Binder013.]
  Fuse = false
  MakeFace = true
  OffsetFill = false
  OffsetIntersection = false
  OffsetJoinType = 0
  OffsetOpenResult = false
  PartialLoad = false
  Refine = true
  Relative = true
  Support = -> [Part__Mirroring001[Face7]]
  _Version = 2
FEATURE [Sketcher::SketchObject] Sketch288
  ArcFitTolerance = 1e-06
  AttachmentSupport = -> [Binder013]
  ExternalGeometry = -> [Binder013]
  FullyConstrained = true
  MakeInternals = false
  MapMode = 5
  Placement = pos=(1.25,0,0) rot=(0.57735,-0.57735,-0.57735;2.0944rad)
  sketch-geometry (39):
    g0: LineSegment StartX=17.1313 StartY=-9.8 StartZ=0 EndX=17.1313 EndY=18.7 EndZ=0
    g1: LineSegment StartX=17.1313 StartY=-9.8 StartZ=0 EndX=18.8313 EndY=-9.8 EndZ=0
    g2: LineSegment StartX=18.8313 StartY=-9.8 StartZ=0 EndX=18.8313 EndY=-3.6 EndZ=0
    g3: Circle CenterX=41.1657 CenterY=-2.53692 CenterZ=0 NormalX=0 NormalY=0 NormalZ=1 AngleXU=0 Radius=0.95
    g4: LineSegment StartX=18.8313 StartY=-3.6 StartZ=0 EndX=22.7813 EndY=0.35 EndZ=0
    g5: LineSegment StartX=22.7813 StartY=0.35 StartZ=0 EndX=28.8813 EndY=0.35 EndZ=0
    g6: LineSegment StartX=28.8813 StartY=0.35 StartZ=0 EndX=32.8313 EndY=-3.6 EndZ=0
    g7: LineSegment StartX=32.8313 StartY=-3.6 StartZ=0 EndX=32.8313 EndY=-8.93216 EndZ=0
    g8: LineSegment StartX=32.8313 StartY=-8.93216 StartZ=0 EndX=44.062 EndY=-4.89651 EndZ=0
    g9: LineSegment StartX=44.062 StartY=-4.89651 StartZ=0 EndX=44.9561 EndY=0.0557565 EndZ=0
    g10: LineSegment StartX=44.9561 StartY=0.0557565 StartZ=0 EndX=43.9561 EndY=0.0557565 EndZ=0
    g11: LineSegment StartX=43.9561 StartY=0.0557565 StartZ=0 EndX=43.9561 EndY=5 EndZ=0
    g12: LineSegment StartX=43.9561 StartY=5 StartZ=0 EndX=41.9561 EndY=5 EndZ=0
    g13: LineSegment StartX=17.1313 StartY=18.7 StartZ=0 EndX=36.1313 EndY=18.7 EndZ=0
    g14: LineSegment StartX=36.1313 StartY=18.7 StartZ=0 EndX=41.9561 EndY=5 EndZ=0
    g15: LineSegment StartX=18.9313 StartY=14.2 StartZ=0 EndX=18.9313 EndY=8.1 EndZ=0
    g16: LineSegment StartX=19.4313 StartY=7.6 StartZ=0 EndX=25.5313 EndY=7.6 EndZ=0
    g17: LineSegment StartX=26.0313 StartY=8.1 StartZ=0 EndX=26.0313 EndY=14.2 EndZ=0
    g18: LineSegment StartX=25.5313 StartY=14.7 StartZ=0 EndX=19.4313 EndY=14.7 EndZ=0
    g19: LineSegment StartX=28.5313 StartY=14.7 StartZ=0 EndX=34.8006 EndY=14.7 EndZ=0
    g20: LineSegment StartX=35.2607 StartY=14.3956 StartZ=0 EndX=37.8542 EndY=8.29564 EndZ=0
    g21: LineSegment StartX=37.3941 StartY=7.6 StartZ=0 EndX=28.5313 EndY=7.6 EndZ=0
    g22: LineSegment StartX=28.0313 StartY=8.1 StartZ=0 EndX=28.0313 EndY=14.2 EndZ=0
    g23: ArcOfCircle CenterX=37.3941 CenterY=8.1 CenterZ=0 NormalX=0 NormalY=0 NormalZ=1 AngleXU=0 Radius=0.5 StartAngle=4.71239 EndAngle=6.6852
    g24: GeomPoint [constr] X=38.15 Y=7.6 Z=0
    g25: ArcOfCircle CenterX=34.8006 CenterY=14.2 CenterZ=0 NormalX=0 NormalY=0 NormalZ=1 AngleXU=0 Radius=0.5 StartAngle=0.402012 EndAngle=1.5708
    g26: GeomPoint [constr] X=35.1313 Y=14.7 Z=0
    g27: ArcOfCircle CenterX=28.5313 CenterY=14.2 CenterZ=0 NormalX=0 NormalY=0 NormalZ=1 AngleXU=0 Radius=0.5 StartAngle=1.5708 EndAngle=3.14159
    g28: GeomPoint [constr] X=28.0313 Y=14.7 Z=0
    g29: ArcOfCircle CenterX=28.5313 CenterY=8.1 CenterZ=0 NormalX=0 NormalY=0 NormalZ=1 AngleXU=0 Radius=0.5 StartAngle=3.14159 EndAngle=4.71239
    g30: GeomPoint [constr] X=28.0313 Y=7.6 Z=0
    g31: ArcOfCircle CenterX=25.5313 CenterY=8.1 CenterZ=0 NormalX=0 NormalY=0 NormalZ=1 AngleXU=0 Radius=0.5 StartAngle=4.71239 EndAngle=6.28319
    g32: GeomPoint [constr] X=26.0313 Y=7.6 Z=0
    g33: ArcOfCircle CenterX=25.5313 CenterY=14.2 CenterZ=0 NormalX=0 NormalY=0 NormalZ=1 AngleXU=0 Radius=0.5 StartAngle=1.2e-15 EndAngle=1.5708
    g34: GeomPoint [constr] X=26.0313 Y=14.7 Z=0
    g35: ArcOfCircle CenterX=19.4313 CenterY=14.2 CenterZ=0 NormalX=0 NormalY=0 NormalZ=1 AngleXU=0 Radius=0.5 StartAngle=1.5708 EndAngle=3.14159
    g36: GeomPoint [constr] X=18.9313 Y=14.7 Z=0
    g37: ArcOfCircle CenterX=19.4313 CenterY=8.1 CenterZ=0 NormalX=0 NormalY=0 NormalZ=1 AngleXU=0 Radius=0.5 StartAngle=3.14159 EndAngle=4.71239
    g38: GeomPoint [constr] X=18.9313 Y=7.6 Z=0
  constraints (91):
    c: Coincident(g0,g-4)
    c: Vertical(g0)
    c: DistanceY(g0,g0) = 28.5
    c: Coincident(g1,g0)
    c: Coincident(g1,g-5)
    c: Coincident(g2,g1)
    c: Coincident(g3,g-13)
    c: Coincident(g2,g-6)
    c: Coincident(g4,g2)
    c: Coincident(g4,g-7)
    c: Coincident(g5,g4)
    c: Coincident(g5,g-8)
    c: Coincident(g6,g5)
    c: Coincident(g6,g-9)
    c: Coincident(g7,g6)
    c: Coincident(g7,g-10)
    c: Coincident(g8,g7)
    c: Coincident(g8,g-11)
    c: Coincident(g9,g8)
    c: Coincident(g9,g-12)
    c: Coincident(g10,g9)
    c: DistanceX(g10,g10) = 1
    c: Coincident(g11,g10)
    c: Vertical(g11)
    c: Coincident(g12,g11)
    c: Horizontal(g12)
    c: Coincident(g13,g0)
    c: Horizontal(g13)
    c: Coincident(g14,g13)
    c: Coincident(g14,g12)
    c: Radius(g3) = 0.95
    c: DistanceY(g-14,g12) = 0
    c: DistanceX(g12,g12) = 2
    c: DistanceX(g13,g13) = 19
    c: PointOnObject(g10,g-12)
    c: Vertical(g15)
    c: Vertical(g17)
    c: Horizontal(g16)
    c: Horizontal(g18)
    c: Horizontal(g19)
    c: Horizontal(g21)
    c: Vertical(g22)
    c: DistanceX(g36,g34) = 7.1
    c: DistanceY(g38,g36) = 7.1
    c: DistanceX(g28,g26) = 7.1
    c: Parallel(g20,g14)
    c: DistanceX(g0,g36) = 1.8
    c: DistanceY(g36,g0) = 4
    c: DistanceY(g30,g28) = 7.1
    c: DistanceY(g26,g13) = 4
    c: DistanceX(g34,g28) = 2
    c: PointOnObject(g24,g20)
    c: PointOnObject(g24,g21)
    c: Tangent(g20,g23) = 1.5708
    c: Tangent(g21,g23) = 1.5708
    c: PointOnObject(g26,g19)
    c: PointOnObject(g26,g20)
    c: Tangent(g19,g25) = 1.5708
    c: Tangent(g20,g25) = 1.5708
    c: PointOnObject(g28,g19)
    c: PointOnObject(g28,g22)
    c: Tangent(g19,g27) = 1.5708
    c: Tangent(g22,g27) = 1.5708
    c: PointOnObject(g30,g21)
    c: PointOnObject(g30,g22)
    c: Tangent(g21,g29) = 1.5708
    c: Tangent(g22,g29) = 1.5708
    c: PointOnObject(g32,g16)
    c: PointOnObject(g32,g17)
    c: Tangent(g16,g31) = -1.5708
    c: Tangent(g17,g31) = -1.5708
    c: PointOnObject(g34,g17)
    c: PointOnObject(g34,g18)
    c: Tangent(g17,g33) = -1.5708
    c: Tangent(g18,g33) = -1.5708
    c: PointOnObject(g36,g15)
    c: PointOnObject(g36,g18)
    c: Tangent(g15,g35) = -1.5708
    c: Tangent(g18,g35) = -1.5708
    c: PointOnObject(g38,g15)
    c: PointOnObject(g38,g16)
    c: Tangent(g15,g37) = -1.5708
    c: Tangent(g16,g37) = -1.5708
    c: Radius(g37) = 0.5
    c: Radius(g35) = 0.5
    c: Radius(g33) = 0.5
    c: Radius(g31) = 0.5
    c: Radius(g29) = 0.5
    c: Radius(g27) = 0.5
    c: Radius(g23) = 0.5
    c: Radius(g25) = 0.5
FEATURE [PartDesign::Pad] Pad188
  Direction = (-1,0,0)
  Length = 1.5
  Length2 = 10
  Profile = -> Sketch288
  ReferenceAxis = -> Sketch288 [N_Axis]
  Refine = true
  Suppressed = false
  Type = 0
FEATURE [Sketcher::SketchObject] Sketch289
  ArcFitTolerance = 1e-06
  AttachmentSupport = -> [Pad188]
  ExternalGeometry = -> [Pad188]
  FullyConstrained = true
  MakeInternals = false
  MapMode = 5
  Placement = pos=(0,-17.1313,0) rot=(0,0.707107,0.707107;3.14159rad)
  sketch-geometry (8):
    g0: LineSegment StartX=0.25 StartY=18.7 StartZ=0 EndX=-11.75 EndY=18.7 EndZ=0
    g1: LineSegment StartX=-11.75 StartY=18.7 StartZ=0 EndX=-11.75 EndY=5 EndZ=0
    g2: LineSegment StartX=-11.75 StartY=5 StartZ=0 EndX=-18 EndY=5 EndZ=0
    g3: LineSegment StartX=-18 StartY=5 StartZ=0 EndX=-18 EndY=3 EndZ=0
    g4: LineSegment StartX=-18 StartY=3 StartZ=0 EndX=-6.75 EndY=3 EndZ=0
    g5: LineSegment StartX=-6.75 StartY=3 StartZ=0 EndX=-6.75 EndY=-9.8 EndZ=0
    g6: LineSegment StartX=-6.75 StartY=-9.8 StartZ=0 EndX=0.25 EndY=-9.8 EndZ=0
    g7: LineSegment StartX=0.25 StartY=-9.8 StartZ=0 EndX=0.25 EndY=18.7 EndZ=0
  constraints (22):
    c: Coincident(g0,g-4)
    c: Horizontal(g0)
    c: Coincident(g1,g0)
    c: Vertical(g1)
    c: Coincident(g2,g1)
    c: Horizontal(g2)
    c: Coincident(g3,g2)
    c: Vertical(g3)
    c: Coincident(g4,g3)
    c: Horizontal(g4)
    c: Coincident(g5,g4)
    c: Vertical(g5)
    c: Coincident(g6,g5)
    c: Coincident(g6,g-4)
    c: Horizontal(g6)
    c: DistanceX(g0,g0) = 12
    c: DistanceY(g1,g1) = 13.7
    c: DistanceX(g2,g2) = 6.25
    c: DistanceY(g3,g3) = 2
    c: DistanceX(g4,g4) = 11.25
    c: Coincident(g7,g6)
    c: Coincident(g7,g0)
FEATURE [PartDesign::Pad] Pad189
  BaseFeature = -> Pad188
  Direction = (0,1,-2e-16)
  Length = 1.5
  Length2 = 10
  Profile = -> Sketch289
  ReferenceAxis = -> Sketch289 [N_Axis]
  Refine = true
  Suppressed = false
  Type = 0
FEATURE [Sketcher::SketchObject] Sketch290
  ArcFitTolerance = 1e-06
  AttachmentSupport = -> [Pad189]
  ExternalGeometry = -> [Pad189]
  FullyConstrained = true
  MakeInternals = false
  MapMode = 5
  Placement = pos=(1.25,0,0) rot=(0.57735,0.57735,0.57735;2.0944rad)
  sketch-geometry (5):
    g0: LineSegment StartX=-41.9561 StartY=5 StartZ=0 EndX=-43.9561 EndY=5 EndZ=0
    g1: LineSegment StartX=-43.9561 StartY=5 StartZ=0 EndX=-43.9561 EndY=0.0557565 EndZ=0
    g2: LineSegment StartX=-42.7061 StartY=0.0557565 StartZ=0 EndX=-43.9561 EndY=0.0557565 EndZ=0
    g3: LineSegment StartX=-41.9561 StartY=5 StartZ=0 EndX=-41.9561 EndY=0.488769 EndZ=0
    g4: LineSegment StartX=-42.7061 StartY=0.0557565 StartZ=0 EndX=-41.9561 EndY=0.488769 EndZ=0
  constraints (12):
    c: Coincident(g0,g-3)
    c: Coincident(g0,g-4)
    c: Coincident(g1,g0)
    c: Coincident(g1,g-4)
    c: Horizontal(g2)
    c: Coincident(g2,g1)
    c: Coincident(g3,g0)
    c: Vertical(g3)
    c: Coincident(g4,g2)
    c: Coincident(g4,g3)
    c: DistanceX(g2,g2) = 1.25
    c: Angle(g4,g2) = 2.61799
FEATURE [PartDesign::Pad] Pad190
  BaseFeature = -> Pad189
  Direction = (1,0,0)
  Length = 10.5
  Length2 = 10
  Profile = -> Sketch290
  ReferenceAxis = -> Sketch290 [N_Axis]
  Refine = true
  Suppressed = false
  Type = 0
FEATURE [Sketcher::SketchObject] Sketch291
  ArcFitTolerance = 1e-06
  AttachmentSupport = -> [Pad190]
  ExternalGeometry = -> [Pad190]
  FullyConstrained = true
  MakeInternals = false
  MapMode = 5
  Placement = pos=(0,1.1e-15,5) rot=(0,0,1;0rad)
  sketch-geometry (6):
    g0: LineSegment StartX=11.75 StartY=-15.6313 StartZ=0 EndX=18 EndY=-15.6313 EndZ=0
    g1: LineSegment StartX=18 StartY=-15.6313 StartZ=0 EndX=18 EndY=-36.4313 EndZ=0
    g2: LineSegment StartX=11.75 StartY=-15.6313 StartZ=0 EndX=11.75 EndY=-17.1313 EndZ=0
    g3: LineSegment StartX=11.75 StartY=-17.1313 StartZ=0 EndX=10.25 EndY=-17.1313 EndZ=0
    g4: LineSegment StartX=10.25 StartY=-17.1313 StartZ=0 EndX=10.25 EndY=-36.4313 EndZ=0
    g5: LineSegment StartX=10.25 StartY=-36.4313 StartZ=0 EndX=18 EndY=-36.4313 EndZ=0
  constraints (16):
    c: Coincident(g0,g-4)
    c: Coincident(g0,g-4)
    c: Coincident(g1,g0)
    c: Vertical(g1)
    c: Coincident(g2,g0)
    c: Vertical(g2)
    c: Coincident(g3,g2)
    c: Horizontal(g3)
    c: Coincident(g4,g3)
    c: Vertical(g4)
    c: Coincident(g5,g4)
    c: Coincident(g5,g1)
    c: Horizontal(g5)
    c: DistanceX(g3,g3) = 1.5
    c: DistanceY(g2,g2) = 1.5
    c: DistanceY(g4,g4) = 19.3
FEATURE [PartDesign::Pad] Pad191
  BaseFeature = -> Pad190
  Direction = (0,0,1)
  Length = 1.5
  Length2 = 10
  Profile = -> Sketch291
  ReferenceAxis = -> Sketch291 [N_Axis]
  Refine = true
  Suppressed = false
  Type = 0
FEATURE [Sketcher::SketchObject] Sketch292
  ArcFitTolerance = 1e-06
  AttachmentSupport = -> [Pad191]
  ExternalGeometry = -> [Pad191]
  FullyConstrained = true
  MakeInternals = false
  MapMode = 5
  Placement = pos=(0,0,6.5) rot=(0,0,1;0rad)
  sketch-geometry (1):
    g0: Circle CenterX=11.75 CenterY=-28.2313 CenterZ=0 NormalX=0 NormalY=0 NormalZ=1 AngleXU=0 Radius=0.75
  constraints (3):
    c: Radius(g0) = 0.75
    c: DistanceX(g-3,g0) = 1.5
    c: DistanceY(g-3,g0) = 8.2
FEATURE [PartDesign::Pocket] Pocket130
  BaseFeature = -> Pad191
  Direction = (0,0,-1)
  Length = 5
  Length2 = 5
  Profile = -> Sketch292
  ReferenceAxis = -> Sketch292 [N_Axis]
  Refine = true
  Suppressed = false
  Type = 0
FEATURE [Sketcher::SketchObject] Sketch293
  ArcFitTolerance = 1e-06
  AttachmentSupport = -> [Pocket130]
  ExternalGeometry = -> [Pocket130]
  FullyConstrained = true
  MakeInternals = false
  MapMode = 5
  Placement = pos=(1.25,0,0) rot=(0.57735,0.57735,0.57735;2.0944rad)
  sketch-geometry (4):
    g0: LineSegment StartX=-36.1313 StartY=18.7 StartZ=0 EndX=-36.7691 EndY=17.2 EndZ=0
    g1: LineSegment StartX=-36.7691 StartY=17.2 StartZ=0 EndX=-17.1313 EndY=17.2 EndZ=0
    g2: LineSegment StartX=-17.1313 StartY=17.2 StartZ=0 EndX=-17.1313 EndY=18.7 EndZ=0
    g3: LineSegment StartX=-17.1313 StartY=18.7 StartZ=0 EndX=-36.1313 EndY=18.7 EndZ=0
  constraints (10):
    c: Coincident(g0,g-5)
    c: PointOnObject(g0,g-5)
    c: Coincident(g1,g0)
    c: PointOnObject(g1,g-3)
    c: Horizontal(g1)
    c: Coincident(g2,g1)
    c: Coincident(g2,g-4)
    c: Coincident(g3,g2)
    c: Coincident(g3,g0)
    c: DistanceY(g2,g2) = 1.5
FEATURE [PartDesign::Pad] Pad192
  BaseFeature = -> Pocket130
  Direction = (1,0,0)
  Length = 10.5
  Length2 = 10
  Profile = -> Sketch293
  ReferenceAxis = -> Sketch293 [N_Axis]
  Refine = true
  Suppressed = false
  Type = 0
FEATURE [Sketcher::SketchObject] Sketch294
  ArcFitTolerance = 1e-06
  AttachmentSupport = -> [Pad192]
  ExternalGeometry = -> [Pad192]
  FullyConstrained = false
  MakeInternals = false
  MapMode = 5
  Placement = pos=(11.75,0,0) rot=(0.57735,0.57735,0.57735;2.0944rad)
  sketch-geometry (7):
    g0: LineSegment StartX=-36.4313 StartY=3.64 StartZ=0 EndX=-41.9561 EndY=0.488769 EndZ=0
    g1: LineSegment StartX=-41.9561 StartY=0.488769 StartZ=0 EndX=-41.9561 EndY=5 EndZ=0
    g2: LineSegment StartX=-41.9561 StartY=5 StartZ=0 EndX=-36.7691 EndY=17.2 EndZ=0
    g3: LineSegment StartX=-36.7691 StartY=17.2 StartZ=0 EndX=-17.1313 EndY=17.2 EndZ=0
    g4: LineSegment StartX=-17.1313 StartY=17.2 StartZ=0 EndX=-17.1313 EndY=6.5 EndZ=0
    g5: LineSegment StartX=-17.1313 StartY=6.5 StartZ=0 EndX=-36.4313 EndY=6.5 EndZ=0
    g6: LineSegment StartX=-36.4313 StartY=6.5 StartZ=0 EndX=-36.4313 EndY=3.64 EndZ=0
  constraints (11):
    c: Coincident(g1,g0)
    c: Coincident(g1,g-3)
    c: Coincident(g2,g1)
    c: Coincident(g2,g-7)
    c: Coincident(g3,g2)
    c: Coincident(g3,g-7)
    c: Coincident(g4,g3)
    c: Coincident(g4,g-6)
    c: Coincident(g5,g4)
    c: Coincident(g0,g-3)
    c: DistanceY(g0,g-5) = 2.86
FEATURE [PartDesign::Pad] Pad193
  BaseFeature = -> Pad192
  Direction = (1,0,0)
  Length = 1.5
  Length2 = 10
  Profile = -> Sketch294
  ReferenceAxis = -> Sketch294 [N_Axis]
  Refine = true
  Reversed = true
  Suppressed = false
  Type = 0
FEATURE [Sketcher::SketchObject] Sketch295
  ArcFitTolerance = 1e-06
  AttachmentSupport = -> [Pad193]
  ExternalGeometry = -> [Pad193]
  FullyConstrained = true
  MakeInternals = false
  MapMode = 5
  Placement = pos=(0,0,6.5) rot=(0,0,1;0rad)
  sketch-geometry (1):
    g0: Circle CenterX=11.75 CenterY=-28.2313 CenterZ=0 NormalX=0 NormalY=0 NormalZ=1 AngleXU=0 Radius=2.6
  constraints (2):
    c: Coincident(g0,g-3)
    c: Radius(g0) = 2.6
FEATURE [PartDesign::Pad] Pad194
  BaseFeature = -> Pad193
  Direction = (0,0,1)
  Length = 4
  Length2 = 10
  Profile = -> Sketch295
  ReferenceAxis = -> Sketch295 [N_Axis]
  Refine = true
  Suppressed = false
  Type = 0
FEATURE [PartDesign::Pad] Pad195
  BaseFeature = -> Pad194
  Direction = (0,0,-1)
  Length = 1.5
  Length2 = 10
  Profile = -> Pad194 [Face52]
  Refine = true
  Suppressed = false
  Type = 0
FEATURE [PartDesign::Pad] Pad196
  BaseFeature = -> Pad195
  Direction = (0,0,1)
  Length = 7
  Length2 = 10
  Profile = -> Pad195 [Face50]
  Refine = true
  Suppressed = false
  Type = 0
FEATURE [PartDesign::Pocket] Pocket131
  BaseFeature = -> Pad196
  Direction = (0,0,1)
  Length = 2
  Length2 = 5
  Profile = -> Pad196 [Face53]
  Refine = true
  Suppressed = false
  Type = 0
FEATURE [Sketcher::SketchObject] Sketch296
  ArcFitTolerance = 1e-06
  AttachmentSupport = -> [Pocket131]
  ExternalGeometry = -> [Pocket131]
  FullyConstrained = true
  MakeInternals = false
  MapMode = 5
  Placement = pos=(0,0,18.7) rot=(0,0,1;0rad)
  sketch-geometry (8):
    g0: ArcOfCircle CenterX=8.75 CenterY=-18.3813 CenterZ=0 NormalX=0 NormalY=0 NormalZ=1 AngleXU=0 Radius=1 StartAngle=1.7e-15 EndAngle=3.14159
    g1: ArcOfCircle CenterX=8.75 CenterY=-33.3813 CenterZ=0 NormalX=0 NormalY=0 NormalZ=1 AngleXU=0 Radius=1 StartAngle=3.14159 EndAngle=6.28319
    g2: LineSegment StartX=9.75 StartY=-18.3813 StartZ=0 EndX=9.75 EndY=-33.3813 EndZ=0
    g3: LineSegment StartX=7.75 StartY=-18.3813 StartZ=0 EndX=7.75 EndY=-33.3813 EndZ=0
    g4: ArcOfCircle CenterX=2.75 CenterY=-18.3813 CenterZ=0 NormalX=0 NormalY=0 NormalZ=1 AngleXU=0 Radius=1 StartAngle=0 EndAngle=3.14159
    g5: ArcOfCircle CenterX=2.75 CenterY=-33.3813 CenterZ=0 NormalX=0 NormalY=0 NormalZ=1 AngleXU=0 Radius=1 StartAngle=3.14159 EndAngle=6.28319
    g6: LineSegment StartX=3.75 StartY=-18.3813 StartZ=0 EndX=3.75 EndY=-33.3813 EndZ=0
    g7: LineSegment StartX=1.75 StartY=-18.3813 StartZ=0 EndX=1.75 EndY=-33.3813 EndZ=0
  constraints (21):
    c: Tangent(g0,g2) = 1.5708
    c: Tangent(g0,g3) = -1.5708
    c: Tangent(g1,g2) = 1.5708
    c: Tangent(g1,g3) = -1.5708
    c: Equal(g0,g1)
    c: Vertical(g2)
    c: Tangent(g4,g6) = 1.5708
    c: Tangent(g4,g7) = -1.5708
    c: Tangent(g5,g6) = 1.5708
    c: Tangent(g5,g7) = -1.5708
    c: Equal(g4,g5)
    c: Vertical(g6)
    c: Diameter(g4) = 2
    c: Diameter(g0) = 2
    c: DistanceY(g1,g0) = 15
    c: DistanceY(g5,g4) = 15
    c: DistanceY(g-3,g-3) = 20.5
    c: DistanceY(g0,g-4) = 2.75
    c: DistanceY(g4,g-6) = 2.75
    c: DistanceX(g-6,g4) = 2
    c: DistanceX(g0,g-4) = 2
FEATURE [PartDesign::Pad] Pad197
  BaseFeature = -> Pocket131
  Direction = (0,0,1)
  Length = 0.5
  Length2 = 10
  Profile = -> Sketch296
  ReferenceAxis = -> Sketch296 [N_Axis]
  Refine = true
  Suppressed = false
  Type = 0
FEATURE [Sketcher::SketchObject] Sketch297
  ArcFitTolerance = 1e-06
  AttachmentSupport = -> [Pad197]
  ExternalGeometry = -> [Pad197]
  FullyConstrained = true
  MakeInternals = false
  MapMode = 5
  Placement = pos=(-0.25,0,0) rot=(0.57735,-0.57735,-0.57735;2.0944rad)
  sketch-geometry (32):
    g0: LineSegment StartX=43.9561 StartY=0.0557565 StartZ=0 EndX=32.4084 EndY=0.0557565 EndZ=0
    g1: LineSegment StartX=32.4084 StartY=0.0557565 StartZ=0 EndX=28.9641 EndY=3.5 EndZ=0
    g2: LineSegment StartX=28.9641 StartY=3.5 StartZ=0 EndX=15.6313 EndY=3.5 EndZ=0
    g3: LineSegment StartX=15.6313 StartY=3.5 StartZ=0 EndX=15.6313 EndY=3.3 EndZ=0
    g4: LineSegment StartX=15.6313 StartY=3.3 StartZ=0 EndX=28.8813 EndY=3.3 EndZ=0
    g5: LineSegment StartX=28.8813 StartY=3.3 StartZ=0 EndX=32.3255 EndY=-0.144243 EndZ=0
    g6: LineSegment StartX=32.3255 StartY=-0.144243 StartZ=0 EndX=44.92 EndY=-0.144243 EndZ=0
    g7: LineSegment StartX=44.92 StartY=-0.144243 StartZ=0 EndX=44.9561 EndY=0.0557565 EndZ=0
    g8: LineSegment [constr] StartX=31.7599 StartY=0.704285 StartZ=0 EndX=31.6184 EndY=0.562863 EndZ=0
    g9: LineSegment StartX=43.9561 StartY=0.0557565 StartZ=0 EndX=44.9561 EndY=0.0557565 EndZ=0
    g10: LineSegment StartX=18.4313 StartY=15.2 StartZ=0 EndX=18.4313 EndY=7.1 EndZ=0
    g11: LineSegment StartX=18.4313 StartY=7.1 StartZ=0 EndX=26.5313 EndY=7.1 EndZ=0
    g12: LineSegment StartX=26.5313 StartY=7.1 StartZ=0 EndX=26.5313 EndY=15.2 EndZ=0
    g13: LineSegment StartX=26.5313 StartY=15.2 StartZ=0 EndX=18.4313 EndY=15.2 EndZ=0
    g14: LineSegment StartX=18.2313 StartY=15.4 StartZ=0 EndX=18.2313 EndY=6.9 EndZ=0
    g15: LineSegment StartX=18.2313 StartY=6.9 StartZ=0 EndX=26.7313 EndY=6.9 EndZ=0
    g16: LineSegment StartX=26.7313 StartY=6.9 StartZ=0 EndX=26.7313 EndY=15.4 EndZ=0
    g17: LineSegment StartX=26.7313 StartY=15.4 StartZ=0 EndX=18.2313 EndY=15.4 EndZ=0
    g18: LineSegment StartX=27.5313 StartY=15.2 StartZ=0 EndX=35.462 EndY=15.2 EndZ=0
    g19: LineSegment StartX=35.462 StartY=15.2 StartZ=0 EndX=38.3144 EndY=8.49127 EndZ=0
    g20: LineSegment StartX=37.3941 StartY=7.1 StartZ=0 EndX=27.5313 EndY=7.1 EndZ=0
    g21: LineSegment StartX=27.5313 StartY=7.1 StartZ=0 EndX=27.5313 EndY=15.2 EndZ=0
    g22: LineSegment StartX=27.3313 StartY=15.4 StartZ=0 EndX=35.5943 EndY=15.4 EndZ=0
    g23: LineSegment StartX=35.5943 StartY=15.4 StartZ=0 EndX=38.4984 EndY=8.56952 EndZ=0
    g24: LineSegment StartX=37.3941 StartY=6.9 StartZ=0 EndX=27.3313 EndY=6.9 EndZ=0
    g25: LineSegment StartX=27.3313 StartY=6.9 StartZ=0 EndX=27.3313 EndY=15.4 EndZ=0
    g26: ArcOfCircle CenterX=37.3941 CenterY=8.1 CenterZ=0 NormalX=0 NormalY=0 NormalZ=1 AngleXU=0 Radius=1 StartAngle=4.71239 EndAngle=6.6852
    g27: GeomPoint [constr] X=38.9059 Y=7.1 Z=0
    g28: ArcOfCircle CenterX=37.3941 CenterY=8.1 CenterZ=0 NormalX=0 NormalY=0 NormalZ=1 AngleXU=0 Radius=1.2 StartAngle=4.71239 EndAngle=6.6852
    g29: GeomPoint [constr] X=39.2082 Y=6.9 Z=0
    g30: LineSegment [constr] StartX=36.0374 StartY=14.358 StartZ=0 EndX=35.8533 EndY=14.2797 EndZ=0
    g31: LineSegment [constr] StartX=36.2446 StartY=13.3594 StartZ=0 EndX=35.7844 EndY=13.1638 EndZ=0
  constraints (91):
    c: Coincident(g0,g-3)
    c: Horizontal(g0)
    c: Coincident(g1,g0)
    c: Coincident(g2,g1)
    c: PointOnObject(g2,g-5)
    c: Horizontal(g2)
    c: Coincident(g3,g2)
    c: PointOnObject(g3,g-5)
    c: Coincident(g4,g3)
    c: Horizontal(g4)
    c: Coincident(g5,g4)
    c: Coincident(g6,g5)
    c: PointOnObject(g6,g-4)
    c: Horizontal(g6)
    c: Coincident(g7,g6)
    c: Coincident(g7,g-4)
    c: DistanceY(g6,g7) = 0.2
    c: DistanceY(g3,g2) = 0.2
    c: PointOnObject(g8,g1)
    c: PointOnObject(g8,g5)
    c: Parallel(g1,g5)
    c: Angle(g8,g1) = 1.5708
    c: Distance(g8) = 0.2
    c: DistanceX(g-6,g4) = 0
    c: Angle(g0,g1) = 2.35619
    c: DistanceY(g2,g-7) = 3
    c: Distance(g8,g5) = 1
    c: Coincident(g9,g0)
    c: Coincident(g9,g7)
    c: Coincident(g10,g11)
    c: Coincident(g11,g12)
    c: Coincident(g12,g13)
    c: Coincident(g13,g10)
    c: Vertical(g10)
    c: Vertical(g12)
    c: Horizontal(g11)
    c: Horizontal(g13)
    c: Coincident(g14,g15)
    c: Coincident(g15,g16)
    c: Coincident(g16,g17)
    c: Coincident(g17,g14)
    c: Vertical(g14)
    c: Vertical(g16)
    c: Horizontal(g15)
    c: Horizontal(g17)
    c: Horizontal(g18)
    c: Coincident(g19,g18)
    c: Horizontal(g20)
    c: Coincident(g21,g20)
    c: Coincident(g21,g18)
    c: Vertical(g21)
    c: Horizontal(g22)
    c: Coincident(g23,g22)
    c: Horizontal(g24)
    c: Coincident(g25,g24)
    c: Coincident(g25,g22)
    c: Vertical(g25)
    c: DistanceY(g12,g16) = 0.2
    c: DistanceY(g18,g22) = 0.2
    c: DistanceY(g15,g11) = 0.2
    c: DistanceX(g14,g10) = 0.2
    c: DistanceX(g11,g15) = 0.2
    c: DistanceX(g-9,g11) = 0.5
    c: DistanceX(g10,g-10) = 0.5
    c: DistanceY(g10,g-8) = 0.5
    c: DistanceY(g-11,g10) = 0.5
    c: PointOnObject(g27,g19)
    c: PointOnObject(g27,g20)
    c: Tangent(g19,g26) = 1.5708
    c: Tangent(g20,g26) = 1.5708
    c: PointOnObject(g29,g23)
    c: PointOnObject(g29,g24)
    c: Tangent(g23,g28) = 1.5708
    c: Tangent(g24,g28) = 1.5708
    c: Coincident(g28,g26)
    c: DistanceY(g24,g20) = 0.2
    c: DistanceY(g20,g-12) = 0.5
    c: DistanceY(g-13,g18) = 0.5
    c: DistanceX(g18,g-15) = 0.5
    c: DistanceX(g22,g18) = 0.2
    c: PointOnObject(g30,g23)
    c: PointOnObject(g30,g19)
    c: Angle(g30,g23) = 1.5708
    c: Distance(g30) = 0.2
    c: Distance(g18,g30) = 1
    c: Parallel(g19,g-14)
    c: PointOnObject(g31,g19)
    c: PointOnObject(g31,g-14)
    c: Angle(g31,g19) = 1.5708
    c: Coincident(g26,g-16)
    c: Distance(g31,g18) = 2
FEATURE [PartDesign::Pocket] Pocket132
  BaseFeature = -> Pad197
  Direction = (1,0,0)
  Length = 0.3
  Length2 = 5
  Profile = -> Sketch297
  ReferenceAxis = -> Sketch297 [N_Axis]
  Refine = true
  Suppressed = false
  Type = 0
FEATURE [PartDesign::SubShapeBinder] Binder014
  BindCopyOnChange = 0
  BindMode = 2
  ClaimChildren = false
  Context = -> Body020 [Binder014.]
  Fuse = false
  MakeFace = true
  OffsetFill = false
  OffsetIntersection = false
  OffsetJoinType = 0
  OffsetOpenResult = false
  PartialLoad = false
  Refine = true
  Relative = true
  _Version = 2
FEATURE [Sketcher::SketchObject] Sketch298
  ArcFitTolerance = 1e-06
  AttachmentSupport = -> [Binder014]
  ExternalGeometry = -> [Binder014]
  FullyConstrained = true
  MakeInternals = false
  MapMode = 5
  Placement = pos=(1.25,0,0) rot=(0.57735,0.57735,0.57735;2.0944rad)
  sketch-geometry (5):
    g0: LineSegment StartX=-36.736 StartY=17.15 StartZ=0 EndX=-41.8805 EndY=5.05 EndZ=0
    g1: LineSegment StartX=-41.8805 StartY=5.05 StartZ=0 EndX=-17.1813 EndY=5.05 EndZ=0
    g2: LineSegment StartX=-17.1813 StartY=5.05 StartZ=0 EndX=-17.1813 EndY=17.15 EndZ=0
    g3: LineSegment StartX=-17.1813 StartY=17.15 StartZ=0 EndX=-36.736 EndY=17.15 EndZ=0
    g4: LineSegment [constr] StartX=-41.1735 StartY=6.84055 StartZ=0 EndX=-41.1275 EndY=6.82099 EndZ=0
  constraints (16):
    c: Coincident(g1,g0)
    c: Horizontal(g1)
    c: Coincident(g2,g1)
    c: Vertical(g2)
    c: Coincident(g3,g2)
    c: Horizontal(g3)
    c: Coincident(g3,g0)
    c: Parallel(g0,g-5)
    c: DistanceY(g0,g-5) = 0.05
    c: DistanceX(g2,g-4) = 0.05
    c: DistanceY(g-5,g0) = 0.05
    c: PointOnObject(g4,g-5)
    c: PointOnObject(g4,g0)
    c: Angle(g0,g4) = 1.5708
    c: Distance(g4) = 0.05
    c: Distance(g4,g-5) = 2
FEATURE [PartDesign::Pad] Pad198
  Direction = (1,0,0)
  Length = 8.95
  Length2 = 10
  Profile = -> Sketch298
  ReferenceAxis = -> Sketch298 [N_Axis]
  Refine = true
  Suppressed = false
  Type = 0
FEATURE [PartDesign::Pocket] Pocket133
  BaseFeature = -> Pad198
  Direction = (1,0,0)
  Length = 0.05
  Length2 = 5
  Profile = -> Pad198 [Face5]
  Refine = true
  Suppressed = false
  Type = 0
FEATURE [Sketcher::SketchObject] Sketch299
  ArcFitTolerance = 1e-06
  AttachmentSupport = -> [Pocket133]
  ExternalGeometry = -> [Pocket133]
  FullyConstrained = true
  MakeInternals = false
  MapMode = 5
  Placement = pos=(0,0,5.05) rot=(1,0,0;3.14159rad)
  sketch-geometry (2):
    g0: ArcOfCircle CenterX=11.7492 CenterY=28.2305 CenterZ=0 NormalX=0 NormalY=0 NormalZ=1 AngleXU=0 Radius=2.65 StartAngle=2.19518 EndAngle=4.088
    g1: LineSegment StartX=10.2 StartY=30.3805 StartZ=0 EndX=10.2 EndY=26.0805 EndZ=0
  constraints (7):
    c: PointOnObject(g0,g-3)
    c: Radius(g0) = 2.65
    c: PointOnObject(g0,g-3)
    c: DistanceY(g0,g0) = 4.3
    c: DistanceY(g0,g-3) = 11.5
    c: Coincident(g1,g0)
    c: Coincident(g1,g0)
FEATURE [PartDesign::Pocket] Pocket134
  BaseFeature = -> Pocket133
  Direction = (0,0,1)
  Length = 13
  Length2 = 5
  Profile = -> Sketch299
  ReferenceAxis = -> Sketch299 [N_Axis]
  Refine = true
  Suppressed = false
  Type = 0
FEATURE [Sketcher::SketchObject] Sketch300
  ArcFitTolerance = 1e-06
  AttachmentSupport = -> [Pocket134]
  ExternalGeometry = -> [Pocket134]
  FullyConstrained = true
  MakeInternals = false
  MapMode = 5
  Placement = pos=(1.3,0,0) rot=(0.57735,-0.57735,-0.57735;2.0944rad)
  sketch-geometry (5):
    g0: LineSegment StartX=19.1813 StartY=5.05 StartZ=0 EndX=19.1813 EndY=15.15 EndZ=0
    g1: LineSegment StartX=19.1813 StartY=15.15 StartZ=0 EndX=35.4131 EndY=15.15 EndZ=0
    g2: LineSegment StartX=35.4131 StartY=15.15 StartZ=0 EndX=39.7072 EndY=5.05 EndZ=0
    g3: LineSegment StartX=39.7072 StartY=5.05 StartZ=0 EndX=19.1813 EndY=5.05 EndZ=0
    g4: LineSegment [constr] StartX=37.6449 StartY=15.0123 StartZ=0 EndX=35.8043 EndY=14.2297 EndZ=0
  constraints (16):
    c: PointOnObject(g0,g-6)
    c: Vertical(g0)
    c: Coincident(g1,g0)
    c: Horizontal(g1)
    c: Coincident(g2,g1)
    c: PointOnObject(g2,g-6)
    c: Coincident(g3,g2)
    c: Coincident(g3,g0)
    c: DistanceX(g-5,g0) = 2
    c: DistanceY(g0,g-5) = 2
    c: Parallel(g2,g-3)
    c: PointOnObject(g4,g-3)
    c: PointOnObject(g4,g2)
    c: Angle(g4,g-3) = 1.5708
    c: Distance(g4) = 2
    c: Distance(g4,g1) = 1
FEATURE [PartDesign::Pocket] Pocket135
  BaseFeature = -> Pocket134
  Direction = (1,0,0)
  Length = 6.9
  Length2 = 5
  Profile = -> Sketch300
  ReferenceAxis = -> Sketch300 [N_Axis]
  Refine = true
  Suppressed = false
  Type = 0
FEATURE [Sketcher::SketchObject] Sketch301
  ArcFitTolerance = 1e-06
  AttachmentSupport = -> [Pocket135]
  ExternalGeometry = -> [Pocket135]
  FullyConstrained = true
  MakeInternals = false
  MapMode = 5
  Placement = pos=(1.3,0,0) rot=(0.57735,-0.57735,-0.57735;2.0944rad)
  sketch-geometry (4):
    g0: LineSegment StartX=19.1813 StartY=15.15 StartZ=0 EndX=35.4131 EndY=15.15 EndZ=0
    g1: LineSegment StartX=35.4131 StartY=15.15 StartZ=0 EndX=39.7072 EndY=5.05 EndZ=0
    g2: LineSegment StartX=39.7072 StartY=5.05 StartZ=0 EndX=19.1813 EndY=5.05 EndZ=0
    g3: LineSegment StartX=19.1813 StartY=5.05 StartZ=0 EndX=19.1813 EndY=15.15 EndZ=0
  constraints (8):
    c: Coincident(g0,g-5)
    c: Coincident(g0,g-4)
    c: Coincident(g1,g0)
    c: Coincident(g1,g-4)
    c: Coincident(g2,g1)
    c: Coincident(g2,g-5)
    c: Coincident(g3,g2)
    c: Coincident(g3,g0)
FEATURE [PartDesign::Pad] Pad199
  BaseFeature = -> Pocket135
  Direction = (-1,0,0)
  Length = 2
  Length2 = 10
  Profile = -> Sketch301
  ReferenceAxis = -> Sketch301 [N_Axis]
  Refine = true
  Reversed = true
  Suppressed = false
  Type = 0
FEATURE [Sketcher::SketchObject] Sketch302
  ArcFitTolerance = 1e-06
  AttachmentSupport = -> [Pad199]
  ExternalGeometry = -> [Pad199]
  FullyConstrained = true
  MakeInternals = false
  MapMode = 5
  Placement = pos=(0,0,5.05) rot=(1,0,0;3.14159rad)
  sketch-geometry (4):
    g0: LineSegment StartX=8.2 StartY=39.7072 StartZ=0 EndX=8.2 EndY=41.8305 EndZ=0
    g1: LineSegment StartX=8.2 StartY=41.8305 StartZ=0 EndX=3.3 EndY=41.8305 EndZ=0
    g2: LineSegment StartX=3.3 StartY=41.8305 StartZ=0 EndX=3.3 EndY=39.7072 EndZ=0
    g3: LineSegment StartX=3.3 StartY=39.7072 StartZ=0 EndX=8.2 EndY=39.7072 EndZ=0
  constraints (10):
    c: Coincident(g0,g1)
    c: Coincident(g1,g2)
    c: Coincident(g2,g3)
    c: Coincident(g3,g0)
    c: Vertical(g0)
    c: Vertical(g2)
    c: Horizontal(g1)
    c: Coincident(g0,g-4)
    c: Coincident(g-4,g2)
    c: DistanceY(g1,g-3) = 0.05
FEATURE [PartDesign::Pad] Pad200
  BaseFeature = -> Pad199
  Direction = (0,0,-1)
  Length = 1.5
  Length2 = 10
  Profile = -> Sketch302
  ReferenceAxis = -> Sketch302 [N_Axis]
  Refine = true
  Suppressed = false
  Type = 0
FEATURE [PartDesign::Body] Body020  label="Front_Windows"
  AllowCompound = false
  Group = -> [Binder014,Sketch298,Pad198,Pocket133,Sketch299,Pocket134,Sketch300,Pocket135,Sketch301,Pad199,Sketch302,Pad200]
  Origin = -> Origin021
  Placement = pos=(0,8.9e-15,0) rot=(0,0,1;0rad)
  Tip = -> Pad200
FEATURE [Sketcher::SketchObject] Sketch303
  ArcFitTolerance = 1e-06
  AttachmentSupport = -> [Pocket132]
  ExternalGeometry = -> [Pocket132]
  FullyConstrained = true
  MakeInternals = false
  MapMode = 5
  Placement = pos=(0,-43.9561,0) rot=(1,0,0;1.5708rad)
  sketch-geometry (2):
    g0: ArcOfCircle CenterX=5.4 CenterY=0.0557565 CenterZ=0 NormalX=0 NormalY=0 NormalZ=1 AngleXU=0 Radius=1.45 StartAngle=0 EndAngle=3.14159
    g1: LineSegment StartX=3.95 StartY=0.0557565 StartZ=0 EndX=6.85 EndY=0.0557565 EndZ=0
  constraints (7):
    c: PointOnObject(g0,g-7)
    c: PointOnObject(g0,g-7)
    c: Diameter(g0) = 2.9
    c: PointOnObject(g0,g-7)
    c: DistanceX(g-5,g0) = 4.2
    c: Coincident(g1,g0)
    c: Coincident(g1,g0)
FEATURE [PartDesign::Pad] Pad201
  BaseFeature = -> Pocket132
  Direction = (0,-1,2e-16)
  Length = 0.5
  Length2 = 10
  Profile = -> Sketch303
  ReferenceAxis = -> Sketch303 [N_Axis]
  Refine = true
  Suppressed = false
  Type = 0
FEATURE [PartDesign::Body] Body019  label="Left_Outer_Leg"
  AllowCompound = false
  Group = -> [Binder013,Sketch288,Pad188,Sketch289,Pad189,Sketch290,Pad190,Sketch291,Pad191,Sketch292,Pocket130,Sketch293,Pad192,Sketch294,Pad193,Sketch295,Pad194,Pad195,Pad196,Pocket131,Sketch296,Pad197,Sketch297,Pocket132,Sketch303,Pad201]
  Origin = -> Origin020
  Placement = pos=(0,8.9e-15,0) rot=(0,0,1;0rad)
  Tip = -> Pad201
FEATURE [PartDesign::SubShapeBinder] Binder015
  BindCopyOnChange = 0
  BindMode = 2
  ClaimChildren = false
  Context = -> Body021 [Binder015.]
  Fuse = false
  MakeFace = true
  OffsetFill = false
  OffsetIntersection = false
  OffsetJoinType = 0
  OffsetOpenResult = false
  PartialLoad = false
  Refine = true
  Relative = true
  _Version = 2
FEATURE [Sketcher::SketchObject] Sketch304
  ArcFitTolerance = 1e-06
  AttachmentSupport = -> [Binder015]
  ExternalGeometry = -> [Binder015]
  FullyConstrained = true
  MakeInternals = false
  MapMode = 5
  Placement = pos=(0,0,0) rot=(1,0,0;3.14159rad)
  sketch-geometry (4):
    g0: LineSegment StartX=7 StartY=-41.35 StartZ=0 EndX=7 EndY=-10.35 EndZ=0
    g1: LineSegment StartX=7 StartY=-10.35 StartZ=0 EndX=5 EndY=-10.35 EndZ=0
    g2: LineSegment StartX=5 StartY=-10.35 StartZ=0 EndX=5 EndY=-41.35 EndZ=0
    g3: LineSegment StartX=7 StartY=-41.35 StartZ=0 EndX=5 EndY=-41.35 EndZ=0
  constraints (12):
    c: PointOnObject(g0,g-3)
    c: PointOnObject(g0,g-5)
    c: Coincident(g1,g0)
    c: Horizontal(g1)
    c: Coincident(g2,g1)
    c: Vertical(g2)
    c: Coincident(g3,g0)
    c: Coincident(g3,g2)
    c: Horizontal(g3)
    c: DistanceY(g-4,g0) = 0.05
    c: DistanceY(g0,g-6) = 0.05
    c: DistanceX(g1,g1) = 2
FEATURE [PartDesign::Pad] Pad202
  Direction = (0,0,-1)
  Length = 10
  Length2 = 10
  Profile = -> Sketch304
  ReferenceAxis = -> Sketch304 [N_Axis]
  Refine = true
  Suppressed = false
  Type = 0
FEATURE [Sketcher::SketchObject] Sketch305
  ArcFitTolerance = 1e-06
  AttachmentSupport = -> [Pad202]
  ExternalGeometry = -> [Pad202]
  FullyConstrained = true
  MakeInternals = false
  MapMode = 5
  Placement = pos=(7,-4e-16,0) rot=(0.57735,0.57735,0.57735;2.0944rad)
  sketch-geometry (4):
    g0: LineSegment StartX=10.35 StartY=-2 StartZ=0 EndX=3.05 EndY=-2 EndZ=0
    g1: LineSegment StartX=3.05 StartY=-2 StartZ=0 EndX=3.05 EndY=-10 EndZ=0
    g2: LineSegment StartX=3.05 StartY=-10 StartZ=0 EndX=10.35 EndY=-10 EndZ=0
    g3: LineSegment StartX=10.35 StartY=-10 StartZ=0 EndX=10.35 EndY=-2 EndZ=0
  constraints (11):
    c: Coincident(g0,g1)
    c: Coincident(g1,g2)
    c: Coincident(g2,g3)
    c: Coincident(g3,g0)
    c: Horizontal(g0)
    c: Horizontal(g2)
    c: Vertical(g1)
    c: Vertical(g3)
    c: DistanceX(g0,g0) = 7.3
    c: Coincident(g2,g-3)
    c: DistanceY(g1,g1) = 8
FEATURE [PartDesign::Pad] Pad203
  BaseFeature = -> Pad202
  Direction = (1,0,0)
  Length = 7
  Length2 = 10
  Profile = -> Sketch305
  ReferenceAxis = -> Sketch305 [N_Axis]
  Refine = true
  Reversed = true
  Suppressed = false
  Type = 0
FEATURE [PartDesign::Pocket] Pocket136
  BaseFeature = -> Pad203
  Direction = (0,-1,0)
  Length = 0.05
  Length2 = 5
  Profile = -> Pad203 [Face7]
  Refine = true
  Suppressed = false
  Type = 0
FEATURE [Sketcher::SketchObject] Sketch306
  ArcFitTolerance = 1e-06
  AttachmentSupport = -> [Pocket136]
  ExternalGeometry = -> [Pocket136]
  FullyConstrained = true
  MakeInternals = false
  MapMode = 5
  Placement = pos=(5,0,0) rot=(0.57735,-0.57735,-0.57735;2.0944rad)
  sketch-geometry (7):
    g0: ArcOfCircle CenterX=-33.95 CenterY=-7 CenterZ=0 NormalX=0 NormalY=0 NormalZ=1 AngleXU=0 Radius=5 StartAngle=3.78509 EndAngle=5.63968
    g1: ArcOfCircle CenterX=-20.75 CenterY=-7 CenterZ=0 NormalX=0 NormalY=0 NormalZ=1 AngleXU=0 Radius=5 StartAngle=3.78509 EndAngle=5.63968
    g2: LineSegment [constr] StartX=-10.3 StartY=-12 StartZ=0 EndX=-41.35 EndY=-12 EndZ=0
    g3: LineSegment [constr] StartX=-10.3 StartY=-12 StartZ=0 EndX=-10.3 EndY=-10 EndZ=0
    g4: LineSegment [constr] StartX=-41.35 StartY=-10 StartZ=0 EndX=-41.35 EndY=-12 EndZ=0
    g5: LineSegment StartX=-24.75 StartY=-10 StartZ=0 EndX=-16.75 EndY=-10 EndZ=0
    g6: LineSegment StartX=-37.95 StartY=-10 StartZ=0 EndX=-29.95 EndY=-10 EndZ=0
  constraints (22):
    c: PointOnObject(g0,g-3)
    c: PointOnObject(g1,g-3)
    c: PointOnObject(g1,g-3)
    c: Radius(g0) = 5
    c: Radius(g1) = 5
    c: Horizontal(g2)
    c: Tangent(g2,g0)
    c: Coincident(g3,g2)
    c: Coincident(g3,g-4)
    c: Vertical(g3)
    c: DistanceY(g3,g3) = 2
    c: Tangent(g1,g2)
    c: Coincident(g4,g-3)
    c: Coincident(g4,g2)
    c: Vertical(g4)
    c: PointOnObject(g0,g-3)
    c: DistanceX(g4,g0) = 3.4
    c: DistanceX(g0,g1) = 5.2
    c: Coincident(g5,g1)
    c: Coincident(g5,g1)
    c: Coincident(g6,g0)
    c: Coincident(g6,g0)
FEATURE [PartDesign::Pad] Pad204
  BaseFeature = -> Pocket136
  Direction = (-1,0,0)
  Length = 2
  Length2 = 10
  Profile = -> Sketch306
  ReferenceAxis = -> Sketch306 [N_Axis]
  Refine = true
  Reversed = true
  Suppressed = false
  Type = 0
FEATURE [Sketcher::SketchObject] Sketch307
  ArcFitTolerance = 1e-06
  AttachmentSupport = -> [Pad204]
  ExternalGeometry = -> [Pad204]
  FullyConstrained = true
  MakeInternals = false
  MapMode = 5
  Placement = pos=(5,0,0) rot=(0.57735,-0.57735,-0.57735;2.0944rad)
  sketch-geometry (6):
    g0: LineSegment StartX=-10.3 StartY=-10 StartZ=0 EndX=-12.05 EndY=-10 EndZ=0
    g1: LineSegment StartX=-12.05 StartY=-10 StartZ=0 EndX=-12.05 EndY=0 EndZ=0
    g2: LineSegment StartX=-12.05 StartY=0 StartZ=0 EndX=-10.35 EndY=0 EndZ=0
    g3: LineSegment StartX=-10.35 StartY=0 StartZ=0 EndX=-10.35 EndY=-2 EndZ=0
    g4: LineSegment StartX=-10.35 StartY=-2 StartZ=0 EndX=-10.3 EndY=-2 EndZ=0
    g5: LineSegment StartX=-10.3 StartY=-2 StartZ=0 EndX=-10.3 EndY=-10 EndZ=0
  constraints (14):
    c: Coincident(g0,g-5)
    c: PointOnObject(g0,g-5)
    c: DistanceX(g0,g0) = 1.75
    c: Coincident(g1,g0)
    c: PointOnObject(g1,g-6)
    c: Vertical(g1)
    c: Coincident(g2,g1)
    c: Coincident(g2,g-6)
    c: Coincident(g3,g2)
    c: Coincident(g3,g-4)
    c: Coincident(g4,g3)
    c: Coincident(g4,g-3)
    c: Coincident(g5,g4)
    c: Coincident(g5,g0)
FEATURE [PartDesign::Pad] Pad205
  BaseFeature = -> Pad204
  Direction = (-1,0,0)
  Length = 5
  Length2 = 10
  Profile = -> Sketch307
  ReferenceAxis = -> Sketch307 [N_Axis]
  Refine = true
  Suppressed = false
  Type = 0
FEATURE [Sketcher::SketchObject] Sketch308
  ArcFitTolerance = 1e-06
  AttachmentSupport = -> [Pad205]
  ExternalGeometry = -> [Pad205]
  FullyConstrained = true
  MakeInternals = false
  MapMode = 5
  Placement = pos=(5,0,0) rot=(0.57735,-0.57735,-0.57735;2.0944rad)
  sketch-geometry (3):
    g0: LineSegment StartX=-12.05 StartY=0 StartZ=0 EndX=-16.35 EndY=0 EndZ=0
    g1: LineSegment StartX=-16.35 StartY=0 StartZ=0 EndX=-12.05 EndY=-4.3 EndZ=0
    g2: LineSegment StartX=-12.05 StartY=-4.3 StartZ=0 EndX=-12.05 EndY=0 EndZ=0
  constraints (9):
    c: PointOnObject(g0,g-3)
    c: PointOnObject(g0,g-3)
    c: Coincident(g1,g0)
    c: PointOnObject(g1,g-4)
    c: Coincident(g2,g1)
    c: Coincident(g2,g0)
    c: Vertical(g2)
    c: DistanceX(g0,g0) = 4.3
    c: Angle(g1,g0) = 0.785398
FEATURE [PartDesign::Pad] Pad206
  BaseFeature = -> Pad205
  Direction = (-1,0,0)
  Length = 5
  Length2 = 10
  Profile = -> Sketch308
  ReferenceAxis = -> Sketch308 [N_Axis]
  Refine = true
  Suppressed = false
  Type = 0
FEATURE [Sketcher::SketchObject] Sketch309
  ArcFitTolerance = 1e-06
  AttachmentSupport = -> [Pad206]
  ExternalGeometry = -> [Pad206]
  FullyConstrained = true
  MakeInternals = false
  MapMode = 5
  Placement = pos=(5,0,0) rot=(0.57735,-0.57735,-0.57735;2.0944rad)
  sketch-geometry (3):
    g0: LineSegment StartX=-41.35 StartY=0 StartZ=0 EndX=-37.35 EndY=0 EndZ=0
    g1: LineSegment StartX=-37.35 StartY=0 StartZ=0 EndX=-41.35 EndY=-4 EndZ=0
    g2: LineSegment StartX=-41.35 StartY=-4 StartZ=0 EndX=-41.35 EndY=0 EndZ=0
  constraints (8):
    c: Coincident(g0,g-4)
    c: PointOnObject(g0,g-3)
    c: Coincident(g1,g0)
    c: Coincident(g2,g1)
    c: Coincident(g2,g0)
    c: Vertical(g2)
    c: DistanceY(g2,g2) = 4
    c: DistanceX(g0,g0) = 4
FEATURE [PartDesign::Pad] Pad207
  BaseFeature = -> Pad206
  Direction = (-1,0,0)
  Length = 5
  Length2 = 10
  Profile = -> Sketch309
  ReferenceAxis = -> Sketch309 [N_Axis]
  Refine = true
  Suppressed = false
  Type = 0
FEATURE [Sketcher::SketchObject] Sketch310
  ArcFitTolerance = 1e-06
  AttachmentSupport = -> [Pad207]
  ExternalGeometry = -> [Pad207]
  FullyConstrained = true
  MakeInternals = false
  MapMode = 5
  Placement = pos=(7,0,0) rot=(0.57735,0.57735,0.57735;2.0944rad)
  sketch-geometry (1):
    g0: Circle CenterX=30.35 CenterY=-4 CenterZ=0 NormalX=0 NormalY=0 NormalZ=1 AngleXU=0 Radius=4
  constraints (3):
    c: Diameter(g0) = 8
    c: Tangent(g0,g-3)
    c: DistanceX(g0,g-3) = 11
FEATURE [PartDesign::Pad] Pad208
  BaseFeature = -> Pad207
  Direction = (1,0,0)
  Length = 5
  Length2 = 10
  Profile = -> Sketch310
  ReferenceAxis = -> Sketch310 [N_Axis]
  Refine = true
  Suppressed = false
  Type = 0
FEATURE [Sketcher::SketchObject] Sketch311
  ArcFitTolerance = 1e-06
  AttachmentSupport = -> [Pad208]
  ExternalGeometry = -> [Pad208]
  FullyConstrained = true
  MakeInternals = false
  MapMode = 5
  Placement = pos=(5,0,0) rot=(0.57735,-0.57735,-0.57735;2.0944rad)
  sketch-geometry (1):
    g0: Circle CenterX=-30.35 CenterY=-4 CenterZ=0 NormalX=0 NormalY=0 NormalZ=1 AngleXU=0 Radius=2.1
  constraints (2):
    c: Coincident(g0,g-3)
    c: Diameter(g0) = 4.2
FEATURE [PartDesign::Pocket] Pocket137
  BaseFeature = -> Pad208
  Direction = (1,0,0)
  Length = 5
  Length2 = 5
  Profile = -> Sketch311
  ReferenceAxis = -> Sketch311 [N_Axis]
  Refine = true
  Suppressed = false
  Type = 0
FEATURE [Sketcher::SketchObject] Sketch312
  ArcFitTolerance = 1e-06
  AttachmentSupport = -> [Pocket137]
  ExternalGeometry = -> [Pocket137]
  FullyConstrained = true
  MakeInternals = false
  MapMode = 5
  Placement = pos=(12,0,0) rot=(0.57735,0.57735,0.57735;2.0944rad)
  sketch-geometry (1):
    g0: Circle CenterX=30.35 CenterY=-4 CenterZ=0 NormalX=0 NormalY=0 NormalZ=1 AngleXU=0 Radius=1.4
  constraints (2):
    c: Coincident(g0,g-3)
    c: Diameter(g0) = 2.8
FEATURE [PartDesign::Pocket] Pocket138
  BaseFeature = -> Pocket137
  Direction = (-1,0,0)
  Length = 5
  Length2 = 5
  Profile = -> Sketch312
  ReferenceAxis = -> Sketch312 [N_Axis]
  Refine = true
  Suppressed = false
  Type = 0
FEATURE [Sketcher::SketchObject] Sketch313
  ArcFitTolerance = 1e-06
  AttachmentSupport = -> [Pocket138]
  ExternalGeometry = -> [Pocket138]
  FullyConstrained = true
  MakeInternals = false
  MapMode = 5
  Placement = pos=(5,0,0) rot=(0.57735,-0.57735,-0.57735;2.0944rad)
  sketch-geometry (2):
    g0: Circle CenterX=-33.95 CenterY=-7 CenterZ=0 NormalX=0 NormalY=0 NormalZ=1 AngleXU=0 Radius=0.75
    g1: Circle CenterX=-20.75 CenterY=-7 CenterZ=0 NormalX=0 NormalY=0 NormalZ=1 AngleXU=0 Radius=0.75
  constraints (4):
    c: Coincident(g0,g-4)
    c: Coincident(g1,g-3)
    c: Radius(g0) = 0.75
    c: Radius(g1) = 0.75
FEATURE [PartDesign::Pocket] Pocket139
  BaseFeature = -> Pocket138
  Direction = (1,0,0)
  Length = 8
  Length2 = 5
  Profile = -> Sketch313
  ReferenceAxis = -> Sketch313 [N_Axis]
  Refine = true
  Suppressed = false
  Type = 0
FEATURE [Sketcher::SketchObject] Sketch314
  ArcFitTolerance = 1e-06
  AttachmentSupport = -> [Pocket139]
  ExternalGeometry = -> [Pocket139]
  FullyConstrained = true
  MakeInternals = false
  MapMode = 5
  Placement = pos=(0,0,-10) rot=(1,0,0;3.14159rad)
  sketch-geometry (1):
    g0: Circle CenterX=3.55 CenterY=-7.2 CenterZ=0 NormalX=0 NormalY=0 NormalZ=1 AngleXU=0 Radius=1.45
  constraints (3):
    c: Radius(g0) = 1.45
    c: DistanceX(g0,g-4) = 3.45
    c: DistanceY(g0,g-4) = 4.15
FEATURE [PartDesign::Pocket] Pocket140
  BaseFeature = -> Pocket139
  Direction = (0,0,1)
  Length = 6
  Length2 = 5
  Profile = -> Sketch314
  ReferenceAxis = -> Sketch314 [N_Axis]
  Refine = true
  Suppressed = false
  Type = 0
FEATURE [Sketcher::SketchObject] Sketch315
  ArcFitTolerance = 1e-06
  AttachmentSupport = -> [Pocket140]
  ExternalGeometry = -> [Pocket140]
  FullyConstrained = true
  MakeInternals = false
  MapMode = 5
  Placement = pos=(0,0,-10) rot=(1,0,0;3.14159rad)
  sketch-geometry (3):
    g0: LineSegment StartX=9e-16 StartY=-3.05 StartZ=0 EndX=1.5 EndY=-3.05 EndZ=0
    g1: LineSegment StartX=1.5 StartY=-3.05 StartZ=0 EndX=9e-16 EndY=-4.55 EndZ=0
    g2: LineSegment StartX=9e-16 StartY=-4.55 StartZ=0 EndX=9e-16 EndY=-3.05 EndZ=0
  constraints (8):
    c: Coincident(g0,g-4)
    c: PointOnObject(g0,g-3)
    c: Coincident(g1,g0)
    c: PointOnObject(g1,g-4)
    c: Coincident(g2,g1)
    c: Coincident(g2,g0)
    c: DistanceX(g0,g0) = 1.5
    c: DistanceY(g2,g2) = 1.5
FEATURE [PartDesign::Pocket] Pocket141
  BaseFeature = -> Pocket140
  Direction = (0,0,1)
  Length = 8
  Length2 = 5
  Profile = -> Sketch315
  ReferenceAxis = -> Sketch315 [N_Axis]
  Refine = true
  Suppressed = false
  Type = 0
FEATURE [Sketcher::SketchObject] Sketch316
  ArcFitTolerance = 1e-06
  AttachmentSupport = -> [Pocket141]
  ExternalGeometry = -> [Pocket141]
  FullyConstrained = true
  MakeInternals = false
  MapMode = 5
  Placement = pos=(7e-16,0,0) rot=(0.57735,-0.57735,-0.57735;2.0944rad)
  sketch-geometry (4):
    g0: LineSegment StartX=-7.15 StartY=-4.4 StartZ=0 EndX=-10.15 EndY=-4.4 EndZ=0
    g1: LineSegment StartX=-10.15 StartY=-4.4 StartZ=0 EndX=-10.15 EndY=-7.6 EndZ=0
    g2: LineSegment StartX=-10.15 StartY=-7.6 StartZ=0 EndX=-7.15 EndY=-7.6 EndZ=0
    g3: LineSegment StartX=-7.15 StartY=-7.6 StartZ=0 EndX=-7.15 EndY=-4.4 EndZ=0
  constraints (12):
    c: Coincident(g0,g1)
    c: Coincident(g1,g2)
    c: Coincident(g2,g3)
    c: Coincident(g3,g0)
    c: Horizontal(g0)
    c: Horizontal(g2)
    c: Vertical(g1)
    c: Vertical(g3)
    c: DistanceX(g0,g0) = 3
    c: DistanceY(g1,g1) = 3.2
    c: DistanceY(g-3,g2) = 2.4
    c: DistanceX(g-4,g1) = 1.9
FEATURE [PartDesign::Pocket] Pocket142
  BaseFeature = -> Pocket141
  Direction = (1,0,0)
  Length = 1.5
  Length2 = 5
  Profile = -> Sketch316
  ReferenceAxis = -> Sketch316 [N_Axis]
  Refine = true
  Suppressed = false
  Type = 0
FEATURE [Sketcher::SketchObject] Sketch317
  ArcFitTolerance = 1e-06
  AttachmentSupport = -> [Pocket142]
  ExternalGeometry = -> [Pocket142]
  FullyConstrained = true
  MakeInternals = false
  MapMode = 5
  Placement = pos=(2.275,2.275,0) rot=(0.862856,-0.357407,-0.357407;1.71777rad)
  sketch-geometry (12):
    g0: LineSegment StartX=-3.21734 StartY=-3.9 StartZ=0 EndX=-3.21734 EndY=-4.1 EndZ=0
    g1: LineSegment StartX=-3.21734 StartY=-4.1 StartZ=0 EndX=-1.09602 EndY=-4.1 EndZ=0
    g2: LineSegment StartX=-1.09602 StartY=-4.1 StartZ=0 EndX=-1.09602 EndY=-3.9 EndZ=0
    g3: LineSegment StartX=-1.09602 StartY=-3.9 StartZ=0 EndX=-3.21734 EndY=-3.9 EndZ=0
    g4: LineSegment StartX=-3.21734 StartY=-5.9 StartZ=0 EndX=-3.21734 EndY=-6.1 EndZ=0
    g5: LineSegment StartX=-3.21734 StartY=-6.1 StartZ=0 EndX=-1.09602 EndY=-6.1 EndZ=0
    g6: LineSegment StartX=-1.09602 StartY=-6.1 StartZ=0 EndX=-1.09602 EndY=-5.9 EndZ=0
    g7: LineSegment StartX=-1.09602 StartY=-5.9 StartZ=0 EndX=-3.21734 EndY=-5.9 EndZ=0
    g8: LineSegment StartX=-3.21734 StartY=-7.9 StartZ=0 EndX=-3.21734 EndY=-8.1 EndZ=0
    g9: LineSegment StartX=-3.21734 StartY=-8.1 StartZ=0 EndX=-1.09602 EndY=-8.1 EndZ=0
    g10: LineSegment StartX=-1.09602 StartY=-8.1 StartZ=0 EndX=-1.09602 EndY=-7.9 EndZ=0
    g11: LineSegment StartX=-1.09602 StartY=-7.9 StartZ=0 EndX=-3.21734 EndY=-7.9 EndZ=0
  constraints (36):
    c: Coincident(g0,g1)
    c: Coincident(g1,g2)
    c: Coincident(g2,g3)
    c: Coincident(g3,g0)
    c: Vertical(g0)
    c: Vertical(g2)
    c: Horizontal(g1)
    c: Horizontal(g3)
    c: PointOnObject(g0,g-5)
    c: PointOnObject(g1,g-3)
    c: Coincident(g4,g5)
    c: Coincident(g5,g6)
    c: Coincident(g6,g7)
    c: Coincident(g7,g4)
    c: Vertical(g4)
    c: Vertical(g6)
    c: Horizontal(g5)
    c: Horizontal(g7)
    c: PointOnObject(g4,g-5)
    c: Coincident(g8,g9)
    c: Coincident(g9,g10)
    c: Coincident(g10,g11)
    c: Coincident(g11,g8)
    c: Vertical(g8)
    c: Vertical(g10)
    c: Horizontal(g9)
    c: Horizontal(g11)
    c: PointOnObject(g8,g-5)
    c: PointOnObject(g9,g-3)
    c: DistanceY(g6,g6) = 0.2
    c: DistanceY(g10,g10) = 0.2
    c: DistanceY(g2,g2) = 0.2
    c: DistanceY(g6,g-4) = 3.9
    c: PointOnObject(g6,g-3)
    c: DistanceY(g6,g1) = 1.8
    c: DistanceY(g10,g5) = 1.8
FEATURE [PartDesign::Pocket] Pocket143
  BaseFeature = -> Pocket142
  Direction = (0.707107,0.707107,0)
  Length = 0.5
  Length2 = 5
  Profile = -> Sketch317
  ReferenceAxis = -> Sketch317 [N_Axis]
  Refine = true
  Suppressed = false
  Type = 0
FEATURE [Sketcher::SketchObject] Sketch318
  ArcFitTolerance = 1e-06
  AttachmentSupport = -> [Pocket143]
  ExternalGeometry = -> [Pocket143]
  FullyConstrained = true
  MakeInternals = false
  MapMode = 5
  Placement = pos=(0,3.05,0) rot=(1,0,0;1.5708rad)
  sketch-geometry (12):
    g0: LineSegment StartX=1.5 StartY=-3.9 StartZ=0 EndX=1.5 EndY=-4.1 EndZ=0
    g1: LineSegment StartX=1.5 StartY=-4.1 StartZ=0 EndX=7 EndY=-4.1 EndZ=0
    g2: LineSegment StartX=7 StartY=-4.1 StartZ=0 EndX=7 EndY=-3.9 EndZ=0
    g3: LineSegment StartX=7 StartY=-3.9 StartZ=0 EndX=1.5 EndY=-3.9 EndZ=0
    g4: LineSegment StartX=1.5 StartY=-5.9 StartZ=0 EndX=1.5 EndY=-6.1 EndZ=0
    g5: LineSegment StartX=1.5 StartY=-6.1 StartZ=0 EndX=7 EndY=-6.1 EndZ=0
    g6: LineSegment StartX=7 StartY=-6.1 StartZ=0 EndX=7 EndY=-5.9 EndZ=0
    g7: LineSegment StartX=7 StartY=-5.9 StartZ=0 EndX=1.5 EndY=-5.9 EndZ=0
    g8: LineSegment StartX=1.5 StartY=-7.9 StartZ=0 EndX=1.5 EndY=-8.1 EndZ=0
    g9: LineSegment StartX=1.5 StartY=-8.1 StartZ=0 EndX=7 EndY=-8.1 EndZ=0
    g10: LineSegment StartX=7 StartY=-8.1 StartZ=0 EndX=7 EndY=-7.9 EndZ=0
    g11: LineSegment StartX=7 StartY=-7.9 StartZ=0 EndX=1.5 EndY=-7.9 EndZ=0
  constraints (30):
    c: Coincident(g0,g1)
    c: Coincident(g1,g2)
    c: Coincident(g2,g3)
    c: Coincident(g3,g0)
    c: Vertical(g2)
    c: Horizontal(g1)
    c: Horizontal(g3)
    c: Coincident(g0,g-5)
    c: PointOnObject(g1,g-3)
    c: Coincident(g4,g5)
    c: Coincident(g5,g6)
    c: Coincident(g6,g7)
    c: Coincident(g7,g4)
    c: Vertical(g6)
    c: Horizontal(g5)
    c: Horizontal(g7)
    c: Coincident(g4,g-6)
    c: PointOnObject(g5,g-3)
    c: Coincident(g8,g9)
    c: Coincident(g9,g10)
    c: Coincident(g10,g11)
    c: Coincident(g11,g8)
    c: Vertical(g10)
    c: Horizontal(g9)
    c: Horizontal(g11)
    c: Coincident(g8,g-7)
    c: PointOnObject(g9,g-3)
    c: Coincident(g8,g-7)
    c: Coincident(g4,g-6)
    c: Coincident(g0,g-5)
FEATURE [PartDesign::Pocket] Pocket144
  BaseFeature = -> Pocket143
  Direction = (0,1,-2e-16)
  Length = 0.5
  Length2 = 5
  Profile = -> Sketch318
  ReferenceAxis = -> Sketch318 [N_Axis]
  Refine = true
  Suppressed = false
  Type = 0
FEATURE [Sketcher::SketchObject] Sketch319
  ArcFitTolerance = 1e-06
  AttachmentSupport = -> [Pocket144]
  ExternalGeometry = -> [Pocket144]
  FullyConstrained = true
  MakeInternals = false
  MapMode = 5
  Placement = pos=(7,0,0) rot=(0.57735,0.57735,0.57735;2.0944rad)
  sketch-geometry (12):
    g0: LineSegment StartX=3.05 StartY=-3.9 StartZ=0 EndX=3.05 EndY=-4.1 EndZ=0
    g1: LineSegment StartX=3.05 StartY=-4.1 StartZ=0 EndX=7.65 EndY=-4.1 EndZ=0
    g2: LineSegment StartX=7.65 StartY=-4.1 StartZ=0 EndX=7.65 EndY=-3.9 EndZ=0
    g3: LineSegment StartX=7.65 StartY=-3.9 StartZ=0 EndX=3.05 EndY=-3.9 EndZ=0
    g4: LineSegment StartX=3.05 StartY=-5.9 StartZ=0 EndX=3.05 EndY=-6.1 EndZ=0
    g5: LineSegment StartX=3.05 StartY=-6.1 StartZ=0 EndX=7.65 EndY=-6.1 EndZ=0
    g6: LineSegment StartX=7.65 StartY=-6.1 StartZ=0 EndX=7.65 EndY=-5.9 EndZ=0
    g7: LineSegment StartX=7.65 StartY=-5.9 StartZ=0 EndX=3.05 EndY=-5.9 EndZ=0
    g8: LineSegment StartX=7.65 StartY=-6.1 StartZ=0 EndX=7.85 EndY=-6.1 EndZ=0
    g9: LineSegment StartX=7.85 StartY=-6.1 StartZ=0 EndX=7.85 EndY=-2 EndZ=0
    g10: LineSegment StartX=7.85 StartY=-2 StartZ=0 EndX=7.65 EndY=-2 EndZ=0
    g11: LineSegment StartX=7.65 StartY=-2 StartZ=0 EndX=7.65 EndY=-6.1 EndZ=0
  constraints (31):
    c: Coincident(g0,g1)
    c: Coincident(g1,g2)
    c: Coincident(g2,g3)
    c: Coincident(g3,g0)
    c: Vertical(g2)
    c: Horizontal(g1)
    c: Horizontal(g3)
    c: Coincident(g0,g-4)
    c: Coincident(g4,g5)
    c: Coincident(g5,g6)
    c: Coincident(g6,g7)
    c: Coincident(g7,g4)
    c: Vertical(g6)
    c: Horizontal(g5)
    c: Horizontal(g7)
    c: Coincident(g4,g-7)
    c: Coincident(g0,g-7)
    c: Coincident(g4,g-8)
    c: DistanceX(g3,g3) = 4.6
    c: DistanceX(g7,g7) = 4.6
    c: Coincident(g8,g9)
    c: Coincident(g9,g10)
    c: Coincident(g10,g11)
    c: Coincident(g11,g8)
    c: Horizontal(g8)
    c: Horizontal(g10)
    c: Vertical(g9)
    c: Vertical(g11)
    c: Coincident(g8,g5)
    c: PointOnObject(g9,g-3)
    c: DistanceX(g8,g8) = 0.2
FEATURE [PartDesign::Pocket] Pocket145
  BaseFeature = -> Pocket144
  Direction = (-1,0,0)
  Length = 0.5
  Length2 = 5
  Profile = -> Sketch319
  ReferenceAxis = -> Sketch319 [N_Axis]
  Refine = true
  Suppressed = false
  Type = 0
FEATURE [Sketcher::SketchObject] Sketch320
  ArcFitTolerance = 1e-06
  AttachmentSupport = -> [Pocket145]
  ExternalGeometry = -> [Pocket145]
  FullyConstrained = true
  MakeInternals = false
  MapMode = 5
  Placement = pos=(7,0,0) rot=(0.57735,0.57735,0.57735;2.0944rad)
  sketch-geometry (12):
    g0: LineSegment StartX=7.85 StartY=-6.1 StartZ=0 EndX=7.95 EndY=-6.1 EndZ=0
    g1: LineSegment StartX=7.95 StartY=-6.1 StartZ=0 EndX=7.95 EndY=-5.9 EndZ=0
    g2: LineSegment StartX=7.95 StartY=-5.9 StartZ=0 EndX=7.85 EndY=-5.9 EndZ=0
    g3: LineSegment StartX=7.85 StartY=-5.9 StartZ=0 EndX=7.85 EndY=-6.1 EndZ=0
    g4: LineSegment StartX=6.25 StartY=-6.1 StartZ=0 EndX=6.05 EndY=-6.1 EndZ=0
    g5: LineSegment StartX=6.05 StartY=-6.1 StartZ=0 EndX=6.05 EndY=-10 EndZ=0
    g6: LineSegment StartX=6.05 StartY=-10 StartZ=0 EndX=6.25 EndY=-10 EndZ=0
    g7: LineSegment StartX=6.25 StartY=-10 StartZ=0 EndX=6.25 EndY=-6.1 EndZ=0
    g8: LineSegment StartX=3.55 StartY=-8.1 StartZ=0 EndX=6.05 EndY=-8.1 EndZ=0
    g9: LineSegment StartX=6.05 StartY=-8.1 StartZ=0 EndX=6.05 EndY=-7.9 EndZ=0
    g10: LineSegment StartX=6.05 StartY=-7.9 StartZ=0 EndX=3.55 EndY=-7.9 EndZ=0
    g11: LineSegment StartX=3.55 StartY=-7.9 StartZ=0 EndX=3.55 EndY=-8.1 EndZ=0
  constraints (33):
    c: Coincident(g0,g1)
    c: Coincident(g1,g2)
    c: Coincident(g2,g3)
    c: Coincident(g3,g0)
    c: Horizontal(g0)
    c: Horizontal(g2)
    c: Vertical(g1)
    c: Vertical(g3)
    c: Coincident(g0,g-4)
    c: Coincident(g4,g5)
    c: Coincident(g5,g6)
    c: Coincident(g6,g7)
    c: Coincident(g7,g4)
    c: Horizontal(g4)
    c: Horizontal(g6)
    c: Vertical(g5)
    c: Vertical(g7)
    c: PointOnObject(g4,g-3)
    c: PointOnObject(g5,g-5)
    c: DistanceX(g6,g6) = 0.2
    c: DistanceX(g4,g0) = 1.7
    c: Coincident(g8,g9)
    c: Coincident(g9,g10)
    c: Coincident(g10,g11)
    c: Coincident(g11,g8)
    c: Horizontal(g8)
    c: Horizontal(g10)
    c: Vertical(g9)
    c: Coincident(g8,g-6)
    c: PointOnObject(g9,g5)
    c: Coincident(g10,g-6)
    c: DistanceX(g-7,g8) = 3
    c: DistanceY(g1,g1) = 0.2
FEATURE [PartDesign::Pocket] Pocket146
  BaseFeature = -> Pocket145
  Direction = (-1,0,0)
  Length = 0.5
  Length2 = 5
  Profile = -> Sketch320
  ReferenceAxis = -> Sketch320 [N_Axis]
  Refine = true
  Suppressed = false
  Type = 0
FEATURE [Sketcher::SketchObject] Sketch321
  ArcFitTolerance = 1e-06
  AttachmentSupport = -> [Pocket146]
  ExternalGeometry = -> [Pocket146]
  FullyConstrained = true
  MakeInternals = false
  MapMode = 5
  Placement = pos=(7,0,0) rot=(0.57735,0.57735,0.57735;2.0944rad)
  sketch-geometry (12):
    g0: LineSegment StartX=7.95 StartY=-5.9 StartZ=0 EndX=7.95 EndY=-8.1 EndZ=0
    g1: LineSegment StartX=7.95 StartY=-8.1 StartZ=0 EndX=8.15 EndY=-8.1 EndZ=0
    g2: LineSegment StartX=8.15 StartY=-8.1 StartZ=0 EndX=8.15 EndY=-5.9 EndZ=0
    g3: LineSegment StartX=8.15 StartY=-5.9 StartZ=0 EndX=7.95 EndY=-5.9 EndZ=0
    g4: LineSegment StartX=10.35 StartY=-2 StartZ=0 EndX=11.85 EndY=-2 EndZ=0
    g5: LineSegment StartX=11.85 StartY=-2 StartZ=0 EndX=11.85 EndY=-1.8 EndZ=0
    g6: LineSegment StartX=11.85 StartY=-1.8 StartZ=0 EndX=10.35 EndY=-1.8 EndZ=0
    g7: LineSegment StartX=10.35 StartY=-1.8 StartZ=0 EndX=10.35 EndY=-2 EndZ=0
    g8: LineSegment StartX=11.85 StartY=-1.8 StartZ=0 EndX=11.85 EndY=-10 EndZ=0
    g9: LineSegment StartX=11.85 StartY=-10 StartZ=0 EndX=12.05 EndY=-10 EndZ=0
    g10: LineSegment StartX=12.05 StartY=-10 StartZ=0 EndX=12.05 EndY=-1.8 EndZ=0
    g11: LineSegment StartX=12.05 StartY=-1.8 StartZ=0 EndX=11.85 EndY=-1.8 EndZ=0
  constraints (33):
    c: Coincident(g0,g1)
    c: Coincident(g1,g2)
    c: Coincident(g2,g3)
    c: Coincident(g3,g0)
    c: Vertical(g0)
    c: Vertical(g2)
    c: Horizontal(g1)
    c: Horizontal(g3)
    c: Coincident(g0,g-3)
    c: DistanceY(g0,g-4) = 0
    c: DistanceX(g3,g3) = 0.2
    c: Coincident(g4,g5)
    c: Coincident(g5,g6)
    c: Coincident(g6,g7)
    c: Coincident(g7,g4)
    c: Horizontal(g4)
    c: Horizontal(g6)
    c: Vertical(g5)
    c: Vertical(g7)
    c: Coincident(g4,g-5)
    c: Coincident(g8,g9)
    c: Coincident(g9,g10)
    c: Coincident(g10,g11)
    c: Coincident(g11,g8)
    c: Vertical(g8)
    c: Vertical(g10)
    c: Horizontal(g9)
    c: Horizontal(g11)
    c: Coincident(g8,g5)
    c: PointOnObject(g8,g-6)
    c: DistanceX(g9,g9) = 0.2
    c: DistanceY(g7,g7) = 0.2
    c: DistanceX(g-7,g4) = 4
FEATURE [PartDesign::Pocket] Pocket147
  BaseFeature = -> Pocket146
  Direction = (-1,0,0)
  Length = 0.5
  Length2 = 5
  Profile = -> Sketch321
  ReferenceAxis = -> Sketch321 [N_Axis]
  Refine = true
  Suppressed = false
  Type = 0
FEATURE [Sketcher::SketchObject] Sketch322
  ArcFitTolerance = 1e-06
  AttachmentSupport = -> [Pocket147]
  ExternalGeometry = -> [Pocket147]
  FullyConstrained = true
  MakeInternals = false
  MapMode = 5
  Placement = pos=(7,0,0) rot=(0.57735,0.57735,0.57735;2.0944rad)
  sketch-geometry (7):
    g0: LineSegment StartX=11.85 StartY=-6.31716 StartZ=0 EndX=11.85 EndY=-6.11716 EndZ=0
    g1: LineSegment StartX=11.85 StartY=-6.11716 StartZ=0 EndX=9.85 EndY=-6.11716 EndZ=0
    g2: LineSegment StartX=9.93284 StartY=-6.31716 StartZ=0 EndX=11.85 EndY=-6.31716 EndZ=0
    g3: LineSegment StartX=8.15 StartY=-8.1 StartZ=0 EndX=9.93284 EndY=-6.31716 EndZ=0
    g4: LineSegment StartX=9.85 StartY=-6.11716 StartZ=0 EndX=8.15 EndY=-7.81716 EndZ=0
    g5: LineSegment StartX=8.15 StartY=-7.81716 StartZ=0 EndX=8.15 EndY=-8.1 EndZ=0
    g6: LineSegment [constr] StartX=8.85711 StartY=-7.11005 StartZ=0 EndX=8.99853 EndY=-7.25147 EndZ=0
  constraints (21):
    c: Coincident(g0,g1)
    c: Coincident(g2,g0)
    c: Vertical(g0)
    c: Horizontal(g1)
    c: Horizontal(g2)
    c: PointOnObject(g0,g-4)
    c: DistanceY(g2,g1) = 0.2
    c: DistanceX(g1,g1) = 2
    c: Coincident(g3,g-3)
    c: Coincident(g4,g1)
    c: PointOnObject(g4,g-3)
    c: Coincident(g5,g4)
    c: Coincident(g5,g3)
    c: Coincident(g3,g2)
    c: Parallel(g4,g3)
    c: Angle(g4,g-3) = 0.785398
    c: PointOnObject(g6,g4)
    c: PointOnObject(g6,g3)
    c: Angle(g4,g6) = 1.5708
    c: Distance(g6,g4) = 1
    c: Distance(g6) = 0.2
FEATURE [PartDesign::Pocket] Pocket148
  BaseFeature = -> Pocket147
  Direction = (-1,0,0)
  Length = 0.5
  Length2 = 5
  Profile = -> Sketch322
  ReferenceAxis = -> Sketch322 [N_Axis]
  Refine = true
  Suppressed = false
  Type = 0
FEATURE [Sketcher::SketchObject] Sketch323
  ArcFitTolerance = 1e-06
  AttachmentSupport = -> [Pocket148]
  ExternalGeometry = -> [Pocket148]
  FullyConstrained = true
  MakeInternals = false
  MapMode = 5
  Placement = pos=(7e-16,0,0) rot=(0.57735,-0.57735,-0.57735;2.0944rad)
  sketch-geometry (1):
    g0: Circle CenterX=-11.85 CenterY=-2.5 CenterZ=0 NormalX=0 NormalY=0 NormalZ=1 AngleXU=0 Radius=1
  constraints (3):
    c: Diameter(g0) = 2
    c: DistanceX(g0,g-3) = 1.5
    c: DistanceY(g0,g-3) = 0.5
FEATURE [PartDesign::Pocket] Pocket149
  BaseFeature = -> Pocket148
  Direction = (1,0,0)
  Length = 0.5
  Length2 = 5
  Profile = -> Sketch323
  ReferenceAxis = -> Sketch323 [N_Axis]
  Refine = true
  Suppressed = false
  Type = 0
FEATURE [PartDesign::Fillet] Fillet012
  Base = -> Pocket149 [Edge147,Edge105,Edge103,Edge101,Edge98,Edge107,Edge192,Edge92,Edge187,Edge191,Edge190,Edge200,Edge186,Edge184,Edge91,Edge185,Edge150,Edge151,Edge220,Edge218,Edge219,Edge6,Edge20,Edge57,Edge203,Edge205,Edge207,Edge19,Edge18,Edge17,Edge109,Edge106,Edge102,Edge99,Edge152,Edge75,Edge148,Edge5,Edge10]
  BaseFeature = -> Pocket149
  Radius = 0.3
  Refine = true
  SupportTransform = false
  Suppressed = false
  UseAllEdges = false
FEATURE [Sketcher::SketchObject] Sketch324
  ArcFitTolerance = 1e-06
  AttachmentSupport = -> [Fillet012]
  ExternalGeometry = -> [Fillet012]
  FullyConstrained = true
  MakeInternals = false
  MapMode = 5
  Placement = pos=(5,0,0) rot=(0.57735,-0.57735,-0.57735;2.0944rad)
  sketch-geometry (2):
    g0: Circle CenterX=-20.75 CenterY=-7 CenterZ=0 NormalX=0 NormalY=0 NormalZ=1 AngleXU=0 Radius=2.25
    g1: Circle CenterX=-33.95 CenterY=-7 CenterZ=0 NormalX=0 NormalY=0 NormalZ=1 AngleXU=0 Radius=2.25
  constraints (4):
    c: Coincident(g0,g-3)
    c: Coincident(g1,g-4)
    c: Diameter(g1) = 4.5
    c: Diameter(g0) = 4.5
FEATURE [PartDesign::Pad] Pad209
  BaseFeature = -> Fillet012
  Direction = (-1,0,0)
  Length = 2
  Length2 = 10
  Profile = -> Sketch324
  ReferenceAxis = -> Sketch324 [N_Axis]
  Refine = true
  Suppressed = false
  Type = 0
FEATURE [PartDesign::Pocket] Pocket150
  BaseFeature = -> Pad209
  Direction = (-1,0,0)
  Length = 5
  Length2 = 5
  Profile = -> Pad209 [Face133,Face134]
  Refine = true
  Suppressed = false
  Type = 0
FEATURE [PartDesign::Body] Body021  label="Pre_Right_Arm"
  AllowCompound = false
  Group = -> [Binder015,Sketch304,Pad202,Sketch305,Pad203,Pocket136,Sketch306,Pad204,Sketch307,Pad205,Sketch308,Pad206,Sketch309,Pad207,Sketch310,Pad208,Sketch311,Pocket137,Sketch312,Pocket138,Sketch313,Pocket139,Sketch314,Pocket140,Sketch315,Pocket141,Sketch316,Pocket142,Sketch317,Pocket143,Sketch318,Pocket144,Sketch319,Pocket145,Sketch320,Pocket146,Sketch321,Pocket147,Sketch322,Pocket148,Sketch323,Pocket149,+4 more]
  Origin = -> Origin022
  Tip = -> Pocket150
FEATURE [Part::Mirroring] Part__Mirroring002  label="Right_Arm"
  Base = (0,0,0)
  Normal = (1,0,0)
  Placement = pos=(36,0,0) rot=(0,0,1;0rad)
  Source = -> Body021
FEATURE [PartDesign::SubShapeBinder] Binder016
  BindCopyOnChange = 0
  BindMode = 2
  ClaimChildren = false
  Context = -> Body022 [Binder016.]
  Fuse = false
  MakeFace = true
  OffsetFill = false
  OffsetIntersection = false
  OffsetJoinType = 0
  OffsetOpenResult = false
  PartialLoad = false
  Refine = true
  Relative = true
  _Version = 2
FEATURE [Sketcher::SketchObject] Sketch325
  ArcFitTolerance = 1e-06
  AttachmentSupport = -> [Binder016]
  ExternalGeometry = -> [Binder016]
  FullyConstrained = true
  MakeInternals = false
  MapMode = 5
  Placement = pos=(12,0,0) rot=(0.57735,0.57735,0.57735;2.0944rad)
  sketch-geometry (4):
    g0: LineSegment StartX=26.35 StartY=-0.05 StartZ=0 EndX=26.35 EndY=-7.25 EndZ=0
    g1: LineSegment StartX=26.35 StartY=-7.25 StartZ=0 EndX=34.35 EndY=-7.25 EndZ=0
    g2: LineSegment StartX=34.35 StartY=-7.25 StartZ=0 EndX=34.35 EndY=-0.05 EndZ=0
    g3: LineSegment StartX=34.35 StartY=-0.05 StartZ=0 EndX=26.35 EndY=-0.05 EndZ=0
  constraints (12):
    c: Coincident(g0,g1)
    c: Coincident(g1,g2)
    c: Coincident(g2,g3)
    c: Coincident(g3,g0)
    c: Vertical(g0)
    c: Vertical(g2)
    c: Horizontal(g1)
    c: Horizontal(g3)
    c: DistanceX(g3,g3) = 8
    c: DistanceY(g0,g0) = 7.2
    c: DistanceX(g0,g-3) = 4
    c: DistanceY(g-3,g0) = 3.95
FEATURE [PartDesign::Pad] Pad210
  Direction = (1,0,0)
  Length = 5.3
  Length2 = 10
  Profile = -> Sketch325
  ReferenceAxis = -> Sketch325 [N_Axis]
  Refine = true
  Suppressed = false
  Type = 0
FEATURE [Sketcher::SketchObject] Sketch326
  ArcFitTolerance = 1e-06
  AttachmentSupport = -> [Pad210]
  ExternalGeometry = -> [Binder016]
  FullyConstrained = true
  MakeInternals = false
  MapMode = 5
  Placement = pos=(12,0,0) rot=(0.57735,-0.57735,-0.57735;2.0944rad)
  sketch-geometry (1):
    g0: Circle CenterX=-30.35 CenterY=-4 CenterZ=0 NormalX=0 NormalY=0 NormalZ=1 AngleXU=0 Radius=0.9
  constraints (2):
    c: Coincident(g0,g-3)
    c: Radius(g0) = 0.9
FEATURE [PartDesign::Pocket] Pocket151
  BaseFeature = -> Pad210
  Direction = (1,0,0)
  Length = 7
  Length2 = 5
  Profile = -> Sketch326
  ReferenceAxis = -> Sketch326 [N_Axis]
  Refine = true
  Suppressed = false
  Type = 0
FEATURE [Sketcher::SketchObject] Sketch327
  ArcFitTolerance = 1e-06
  AttachmentSupport = -> [Pocket151]
  ExternalGeometry = -> [Pocket151]
  FullyConstrained = true
  MakeInternals = false
  MapMode = 5
  Placement = pos=(0,34.35,0) rot=(0,0.707107,0.707107;3.14159rad)
  sketch-geometry (4):
    g0: LineSegment StartX=-17.3 StartY=-0.05 StartZ=0 EndX=-17.3 EndY=-7.25 EndZ=0
    g1: LineSegment StartX=-17.3 StartY=-7.25 StartZ=0 EndX=-16.3 EndY=-7.25 EndZ=0
    g2: LineSegment StartX=-16.3 StartY=-7.25 StartZ=0 EndX=-16.3 EndY=-0.05 EndZ=0
    g3: LineSegment StartX=-16.3 StartY=-0.05 StartZ=0 EndX=-17.3 EndY=-0.05 EndZ=0
  constraints (11):
    c: Coincident(g0,g1)
    c: Coincident(g1,g2)
    c: Coincident(g2,g3)
    c: Coincident(g3,g0)
    c: Vertical(g0)
    c: Vertical(g2)
    c: Horizontal(g1)
    c: Horizontal(g3)
    c: Coincident(g0,g-5)
    c: PointOnObject(g1,g-4)
    c: DistanceX(g1,g1) = 1
FEATURE [PartDesign::Pad] Pad211
  BaseFeature = -> Pocket151
  Direction = (0,1,-2e-16)
  Length = 1.2
  Length2 = 10
  Profile = -> Sketch327
  ReferenceAxis = -> Sketch327 [N_Axis]
  Refine = true
  Suppressed = false
  Type = 0
FEATURE [Sketcher::SketchObject] Sketch328
  ArcFitTolerance = 1e-06
  AttachmentSupport = -> [Pad211]
  ExternalGeometry = -> [Pad211]
  FullyConstrained = true
  MakeInternals = false
  MapMode = 5
  Placement = pos=(0,26.35,0) rot=(1,0,0;1.5708rad)
  sketch-geometry (4):
    g0: LineSegment StartX=17.3 StartY=-0.05 StartZ=0 EndX=16.3 EndY=-0.05 EndZ=0
    g1: LineSegment StartX=16.3 StartY=-0.05 StartZ=0 EndX=16.3 EndY=-7.25 EndZ=0
    g2: LineSegment StartX=16.3 StartY=-7.25 StartZ=0 EndX=17.3 EndY=-7.25 EndZ=0
    g3: LineSegment StartX=17.3 StartY=-7.25 StartZ=0 EndX=17.3 EndY=-0.05 EndZ=0
  constraints (11):
    c: Coincident(g0,g1)
    c: Coincident(g1,g2)
    c: Coincident(g2,g3)
    c: Coincident(g3,g0)
    c: Horizontal(g0)
    c: Horizontal(g2)
    c: Vertical(g1)
    c: Vertical(g3)
    c: Coincident(g0,g-3)
    c: PointOnObject(g1,g-4)
    c: DistanceX(g2,g2) = 1
FEATURE [PartDesign::Pad] Pad212
  BaseFeature = -> Pad211
  Direction = (0,-1,2e-16)
  Length = 1.2
  Length2 = 10
  Profile = -> Sketch328
  ReferenceAxis = -> Sketch328 [N_Axis]
  Refine = true
  Suppressed = false
  Type = 0
FEATURE [Sketcher::SketchObject] Sketch329
  ArcFitTolerance = 1e-06
  AttachmentSupport = -> [XY_Plane024]
  FullyConstrained = true
  MakeInternals = false
  MapMode = 5
  sketch-geometry (1):
    g0: Circle CenterX=0 CenterY=0 CenterZ=0 NormalX=0 NormalY=0 NormalZ=1 AngleXU=0 Radius=6.05
  constraints (2):
    c: Coincident(g0,g-1)
    c: Diameter(g0) = 12.1
FEATURE [PartDesign::Pad] Pad213
  Direction = (0,0,1)
  Length = 3.6
  Length2 = 10
  Profile = -> Sketch329
  ReferenceAxis = -> Sketch329 [N_Axis]
  Refine = true
  Suppressed = false
  Type = 0
FEATURE [Sketcher::SketchObject] Sketch330
  ArcFitTolerance = 1e-06
  AttachmentSupport = -> [Pad213]
  FullyConstrained = true
  MakeInternals = false
  MapMode = 5
  Placement = pos=(0,0,3.6) rot=(0,0,1;0rad)
  sketch-geometry (1):
    g0: Circle CenterX=0 CenterY=0 CenterZ=0 NormalX=0 NormalY=0 NormalZ=1 AngleXU=0 Radius=3.55
  constraints (2):
    c: Coincident(g0,g-1)
    c: Diameter(g0) = 7.1
FEATURE [PartDesign::Pad] Pad214
  BaseFeature = -> Pad213
  Direction = (0,0,1)
  Length = 0.5
  Length2 = 10
  Profile = -> Sketch330
  ReferenceAxis = -> Sketch330 [N_Axis]
  Refine = true
  Suppressed = false
  Type = 0
FEATURE [Sketcher::SketchObject] Sketch331
  ArcFitTolerance = 1e-06
  AttachmentSupport = -> [Pad214]
  ExternalGeometry = -> [Pad214]
  FullyConstrained = true
  MakeInternals = false
  MapMode = 5
  Placement = pos=(0,0,3.6) rot=(0,0,1;0rad)
  sketch-geometry (2):
    g0: Circle CenterX=0 CenterY=0 CenterZ=0 NormalX=0 NormalY=0 NormalZ=1 AngleXU=0 Radius=5
    g1: Circle CenterX=0 CenterY=0 CenterZ=0 NormalX=0 NormalY=0 NormalZ=1 AngleXU=0 Radius=6.05
  constraints (5):
    c: Diameter(g0) = 10
    c: Coincident(g1,g0)
    c: Diameter(g-3) = 12.1
    c: Diameter(g1) = 12.1
    c: Coincident(g0,g-1)
FEATURE [PartDesign::Pocket] Pocket152
  BaseFeature = -> Pad214
  Direction = (0,0,-1)
  Length = 1
  Length2 = 5
  Profile = -> Sketch331
  ReferenceAxis = -> Sketch331 [N_Axis]
  Refine = true
  Suppressed = false
  Type = 0
FEATURE [Sketcher::SketchObject] Sketch332
  ArcFitTolerance = 1e-06
  AttachmentSupport = -> [Pocket152]
  ExternalGeometry = -> [Pocket152]
  FullyConstrained = true
  MakeInternals = false
  MapMode = 5
  Placement = pos=(0,0,3.6) rot=(0,0,1;0rad)
  sketch-geometry (50):
    g0: Circle [constr] CenterX=0 CenterY=0 CenterZ=0 NormalX=0 NormalY=0 NormalZ=1 AngleXU=0 Radius=6.05
    g1: LineSegment StartX=4e-16 StartY=6.05 StartZ=0 EndX=-0.789683 EndY=5.99824 EndZ=0
    g2: LineSegment StartX=-0.789683 StartY=5.99824 StartZ=0 EndX=-1.56586 EndY=5.84385 EndZ=0
    g3: LineSegment StartX=-1.56586 StartY=5.84385 StartZ=0 EndX=-2.31523 EndY=5.58947 EndZ=0
    g4: LineSegment StartX=-2.31523 StartY=5.58947 StartZ=0 EndX=-3.025 EndY=5.23945 EndZ=0
    g5: LineSegment StartX=-3.025 StartY=5.23945 StartZ=0 EndX=-3.68301 EndY=4.79979 EndZ=0
    g6: LineSegment StartX=-3.68301 StartY=4.79979 StartZ=0 EndX=-4.278 EndY=4.278 EndZ=0
    g7: LineSegment StartX=-4.278 StartY=4.278 StartZ=0 EndX=-4.79979 EndY=3.68301 EndZ=0
    g8: LineSegment StartX=-4.79979 StartY=3.68301 StartZ=0 EndX=-5.23945 EndY=3.025 EndZ=0
    g9: LineSegment StartX=-5.23945 StartY=3.025 StartZ=0 EndX=-5.58947 EndY=2.31523 EndZ=0
    g10: LineSegment StartX=-5.58947 StartY=2.31523 StartZ=0 EndX=-5.84385 EndY=1.56586 EndZ=0
    g11: LineSegment StartX=-5.84385 StartY=1.56586 StartZ=0 EndX=-5.99824 EndY=0.789683 EndZ=0
    g12: LineSegment StartX=-5.99824 StartY=0.789683 StartZ=0 EndX=-6.05 EndY=4e-16 EndZ=0
    g13: LineSegment StartX=-6.05 StartY=4e-16 StartZ=0 EndX=-5.99824 EndY=-0.789683 EndZ=0
    g14: LineSegment StartX=-5.99824 StartY=-0.789683 StartZ=0 EndX=-5.84385 EndY=-1.56586 EndZ=0
    g15: LineSegment StartX=-5.84385 StartY=-1.56586 StartZ=0 EndX=-5.58947 EndY=-2.31523 EndZ=0
    g16: LineSegment StartX=-5.58947 StartY=-2.31523 StartZ=0 EndX=-5.23945 EndY=-3.025 EndZ=0
    g17: LineSegment StartX=-5.23945 StartY=-3.025 StartZ=0 EndX=-4.79979 EndY=-3.68301 EndZ=0
    g18: LineSegment StartX=-4.79979 StartY=-3.68301 StartZ=0 EndX=-4.278 EndY=-4.278 EndZ=0
    g19: LineSegment StartX=-4.278 StartY=-4.278 StartZ=0 EndX=-3.68301 EndY=-4.79979 EndZ=0
    g20: LineSegment StartX=-3.68301 StartY=-4.79979 StartZ=0 EndX=-3.025 EndY=-5.23945 EndZ=0
    g21: LineSegment StartX=-3.025 StartY=-5.23945 StartZ=0 EndX=-2.31523 EndY=-5.58947 EndZ=0
    g22: LineSegment StartX=-2.31523 StartY=-5.58947 StartZ=0 EndX=-1.56586 EndY=-5.84385 EndZ=0
    g23: LineSegment StartX=-1.56586 StartY=-5.84385 StartZ=0 EndX=-0.789683 EndY=-5.99824 EndZ=0
    g24: LineSegment StartX=-0.789683 StartY=-5.99824 StartZ=0 EndX=-1e-16 EndY=-6.05 EndZ=0
    g25: LineSegment StartX=-1e-16 StartY=-6.05 StartZ=0 EndX=0.789683 EndY=-5.99824 EndZ=0
    g26: LineSegment StartX=0.789683 StartY=-5.99824 StartZ=0 EndX=1.56586 EndY=-5.84385 EndZ=0
    g27: LineSegment StartX=1.56586 StartY=-5.84385 StartZ=0 EndX=2.31523 EndY=-5.58947 EndZ=0
    g28: LineSegment StartX=2.31523 StartY=-5.58947 StartZ=0 EndX=3.025 EndY=-5.23945 EndZ=0
    g29: LineSegment StartX=3.025 StartY=-5.23945 StartZ=0 EndX=3.68301 EndY=-4.79979 EndZ=0
    g30: LineSegment StartX=3.68301 StartY=-4.79979 StartZ=0 EndX=4.278 EndY=-4.278 EndZ=0
    g31: LineSegment StartX=4.278 StartY=-4.278 StartZ=0 EndX=4.79979 EndY=-3.68301 EndZ=0
    g32: LineSegment StartX=4.79979 StartY=-3.68301 StartZ=0 EndX=5.23945 EndY=-3.025 EndZ=0
    g33: LineSegment StartX=5.23945 StartY=-3.025 StartZ=0 EndX=5.58947 EndY=-2.31523 EndZ=0
    g34: LineSegment StartX=5.58947 StartY=-2.31523 StartZ=0 EndX=5.84385 EndY=-1.56586 EndZ=0
    g35: LineSegment StartX=5.84385 StartY=-1.56586 StartZ=0 EndX=5.99824 EndY=-0.789683 EndZ=0
    g36: LineSegment StartX=5.99824 StartY=-0.789683 StartZ=0 EndX=6.05 EndY=0 EndZ=0
    g37: LineSegment StartX=6.05 StartY=0 StartZ=0 EndX=5.99824 EndY=0.789683 EndZ=0
    g38: LineSegment StartX=5.99824 StartY=0.789683 StartZ=0 EndX=5.84385 EndY=1.56586 EndZ=0
    g39: LineSegment StartX=5.84385 StartY=1.56586 StartZ=0 EndX=5.58947 EndY=2.31523 EndZ=0
    g40: LineSegment StartX=5.58947 StartY=2.31523 StartZ=0 EndX=5.23945 EndY=3.025 EndZ=0
    g41: LineSegment StartX=5.23945 StartY=3.025 StartZ=0 EndX=4.79979 EndY=3.68301 EndZ=0
    g42: LineSegment StartX=4.79979 StartY=3.68301 StartZ=0 EndX=4.278 EndY=4.278 EndZ=0
    g43: LineSegment StartX=4.278 StartY=4.278 StartZ=0 EndX=3.68301 EndY=4.79979 EndZ=0
    g44: LineSegment StartX=3.68301 StartY=4.79979 StartZ=0 EndX=3.025 EndY=5.23945 EndZ=0
    g45: LineSegment StartX=3.025 StartY=5.23945 StartZ=0 EndX=2.31523 EndY=5.58947 EndZ=0
    g46: LineSegment StartX=2.31523 StartY=5.58947 StartZ=0 EndX=1.56586 EndY=5.84385 EndZ=0
    g47: LineSegment StartX=1.56586 StartY=5.84385 StartZ=0 EndX=0.789683 EndY=5.99824 EndZ=0
    g48: LineSegment StartX=0.789683 StartY=5.99824 StartZ=0 EndX=4e-16 EndY=6.05 EndZ=0
    g49: Circle [constr] CenterX=0 CenterY=0 CenterZ=0 NormalX=0 NormalY=0 NormalZ=1 AngleXU=0 Radius=6.05
  constraints (102):
    c: Coincident(g0,g-1)
    c: Coincident(g1,g2)
    c: Coincident(g2,g3)
    c: Coincident(g3,g4)
    c: Coincident(g4,g5)
    c: Coincident(g5,g6)
    c: Coincident(g6,g7)
    c: Coincident(g7,g8)
    c: Coincident(g8,g9)
    c: Coincident(g9,g10)
    c: Coincident(g10,g11)
    c: Coincident(g11,g12)
    c: Coincident(g12,g13)
    c: Coincident(g13,g14)
    c: Coincident(g14,g15)
    c: Coincident(g15,g16)
    c: Coincident(g16,g17)
    c: Coincident(g17,g18)
    c: Coincident(g18,g19)
    c: Coincident(g19,g20)
    c: Coincident(g20,g21)
    c: Coincident(g21,g22)
    c: Coincident(g22,g23)
    c: Coincident(g23,g24)
    c: Coincident(g24,g25)
    c: Coincident(g25,g26)
    c: Coincident(g26,g27)
    c: Coincident(g27,g28)
    c: Coincident(g28,g29)
    c: Coincident(g29,g30)
    c: Coincident(g30,g31)
    c: Coincident(g31,g32)
    c: Coincident(g32,g33)
    c: Coincident(g33,g34)
    c: Coincident(g34,g35)
    c: Coincident(g35,g36)
    c: Coincident(g36,g37)
    c: Coincident(g37,g38)
    c: Coincident(g38,g39)
    c: Coincident(g39,g40)
    c: Coincident(g40,g41)
    c: Coincident(g41,g42)
    c: Coincident(g42,g43)
    c: Coincident(g43,g44)
    c: Coincident(g44,g45)
    c: Coincident(g45,g46)
    c: Coincident(g46,g47)
    c: Coincident(g47,g48)
    c: Coincident(g48,g1)
    c: Equal(g1, g2-g48) x47
    c: PointOnObject(g1,g49)
    c: PointOnObject(g2,g49)
    c: PointOnObject(g3,g49)
    c: PointOnObject(g4,g49)
    c: PointOnObject(g5,g49)
    c: PointOnObject(g6,g49)
    c: PointOnObject(g7,g49)
    c: PointOnObject(g8,g49)
    c: PointOnObject(g9,g49)
    c: PointOnObject(g10,g49)
    c: PointOnObject(g11,g49)
    c: PointOnObject(g12,g49)
    c: PointOnObject(g13,g49)
    c: PointOnObject(g14,g49)
    c: PointOnObject(g15,g49)
    c: PointOnObject(g16,g49)
    c: PointOnObject(g17,g49)
    c: PointOnObject(g18,g49)
    c: PointOnObject(g19,g49)
    c: PointOnObject(g20,g49)
    c: PointOnObject(g21,g49)
    c: PointOnObject(g22,g49)
    c: PointOnObject(g23,g49)
    c: PointOnObject(g24,g49)
    c: PointOnObject(g25,g49)
    c: PointOnObject(g26,g49)
    c: PointOnObject(g27,g49)
    c: PointOnObject(g28,g49)
    c: PointOnObject(g29,g49)
    c: PointOnObject(g30,g49)
    c: PointOnObject(g31,g49)
    c: PointOnObject(g32,g49)
    c: PointOnObject(g33,g49)
    c: PointOnObject(g34,g49)
    c: PointOnObject(g35,g49)
    c: PointOnObject(g36,g49)
    c: PointOnObject(g37,g49)
    c: PointOnObject(g38,g49)
    c: PointOnObject(g39,g49)
    c: PointOnObject(g40,g49)
    c: PointOnObject(g41,g49)
    c: PointOnObject(g42,g49)
    c: PointOnObject(g43,g49)
    c: PointOnObject(g44,g49)
    c: PointOnObject(g45,g49)
    c: PointOnObject(g46,g49)
    c: PointOnObject(g47,g49)
    c: PointOnObject(g48,g49)
    c: Coincident(g49,g0)
    c: PointOnObject(g48,g0)
    c: PointOnObject(g1,g-3)
    c: DistanceY(g0,g36) = 0
FEATURE [PartDesign::Pad] Pad215
  BaseFeature = -> Pocket152
  Direction = (0,0,1)
  Length = 1
  Length2 = 10
  Profile = -> Sketch332
  ReferenceAxis = -> Sketch332 [N_Axis]
  Refine = true
  Reversed = true
  Suppressed = false
  Type = 0
FEATURE [PartDesign::Chamfer] Chamfer003
  Angle = 45
  Base = -> Pad215 [Edge137,Edge139,Edge141,Edge143,Edge145,Edge147,Edge149,Edge151,Edge153,Edge135,Edge133,Edge131,Edge129,Edge127,Edge125,Edge123,Edge121,Edge119,Edge117,Edge115,Edge113,Edge111,Edge109,Edge107,Edge105,Edge103,Edge101,Edge194,Edge193,Edge191,Edge189,Edge187,Edge185,Edge183,Edge181,Edge179,Edge177,Edge175,Edge173,Edge171,+8 more]
  BaseFeature = -> Pad215
  ChamferType = 0
  FlipDirection = false
  Refine = true
  Size = 0.99
  Size2 = 1
  SupportTransform = false
  Suppressed = false
  UseAllEdges = false
FEATURE [PartDesign::Pad] Pad216
  BaseFeature = -> Chamfer003
  Direction = (-0.312745,0.634185,0.707107)
  Length = 0.2
  Length2 = 10
  Profile = -> Chamfer003 [Face44]
  Refine = true
  Suppressed = false
  Type = 0
FEATURE [PartDesign::Pad] Pad217
  BaseFeature = -> Pad216
  Direction = (0.587938,-0.392847,0.707107)
  Length = 0.2
  Length2 = 10
  Profile = -> Pad216 [Face45]
  Refine = true
  Suppressed = false
  Type = 0
FEATURE [PartDesign::Pad] Pad218
  BaseFeature = -> Pad217
  Direction = (-0.13795,0.69352,0.707107)
  Length = 0.2
  Length2 = 10
  Profile = -> Pad217 [Face48]
  Refine = true
  Suppressed = false
  Type = 0
FEATURE [PartDesign::Pad] Pad219
  BaseFeature = -> Pad218
  Direction = (0.046247,0.705593,0.707107)
  Length = 0.2
  Length2 = 10
  Profile = -> Pad218 [Face50]
  Refine = true
  Suppressed = false
  Type = 0
FEATURE [PartDesign::Pad] Pad220
  BaseFeature = -> Pad219
  Direction = (0.227292,0.669581,0.707107)
  Length = 0.2
  Length2 = 10
  Profile = -> Pad219 [Face52]
  Refine = true
  Suppressed = false
  Type = 0
FEATURE [PartDesign::Pad] Pad221
  BaseFeature = -> Pad220
  Direction = (0.392847,0.587938,0.707107)
  Length = 0.2
  Length2 = 10
  Profile = -> Pad220 [Face56]
  Refine = true
  Suppressed = false
  Type = 0
FEATURE [PartDesign::Pad] Pad222
  BaseFeature = -> Pad221
  Direction = (0.531631,0.466228,0.707107)
  Length = 0.2
  Length2 = 10
  Profile = -> Pad221 [Face60]
  Refine = true
  Suppressed = false
  Type = 0
FEATURE [PartDesign::Pad] Pad223
  BaseFeature = -> Pad222
  Direction = (0.634185,0.312745,0.707107)
  Length = 0.2
  Length2 = 10
  Profile = -> Pad222 [Face57]
  Refine = true
  Suppressed = false
  Type = 0
FEATURE [PartDesign::Pad] Pad224
  BaseFeature = -> Pad223
  Direction = (-0.466228,0.531631,0.707107)
  Length = 0.2
  Length2 = 10
  Profile = -> Pad223 [Face40]
  Refine = true
  Suppressed = false
  Type = 0
FEATURE [PartDesign::Pad] Pad225
  BaseFeature = -> Pad224
  Direction = (-0.587938,0.392847,0.707107)
  Length = 0.2
  Length2 = 10
  Profile = -> Pad224 [Face36]
  Refine = true
  Suppressed = false
  Type = 0
FEATURE [PartDesign::Pad] Pad226
  BaseFeature = -> Pad225
  Direction = (-0.669581,0.227292,0.707107)
  Length = 0.2
  Length2 = 10
  Profile = -> Pad225 [Face32]
  Refine = true
  Suppressed = false
  Type = 0
FEATURE [PartDesign::Pad] Pad227
  BaseFeature = -> Pad226
  Direction = (-0.705593,0.046247,0.707107)
  Length = 0.2
  Length2 = 10
  Profile = -> Pad226 [Face28]
  Refine = true
  Suppressed = false
  Type = 0
FEATURE [PartDesign::Pad] Pad228
  BaseFeature = -> Pad227
  Direction = (-0.69352,-0.13795,0.707107)
  Length = 0.2
  Length2 = 10
  Profile = -> Pad227 [Face24]
  Refine = true
  Suppressed = false
  Type = 0
FEATURE [PartDesign::Pad] Pad229
  BaseFeature = -> Pad228
  Direction = (-0.634185,-0.312745,0.707107)
  Length = 0.2
  Length2 = 10
  Profile = -> Pad228 [Face20]
  Refine = true
  Suppressed = false
  Type = 0
FEATURE [PartDesign::Pad] Pad230
  BaseFeature = -> Pad229
  Direction = (0.69352,0.13795,0.707107)
  Length = 0.2
  Length2 = 10
  Profile = -> Pad229 [Face53]
  Refine = true
  Suppressed = false
  Type = 0
FEATURE [PartDesign::Pad] Pad231
  BaseFeature = -> Pad230
  Direction = (0.705593,-0.046247,0.707107)
  Length = 0.2
  Length2 = 10
  Profile = -> Pad230 [Face3]
  Refine = true
  Suppressed = false
  Type = 0
FEATURE [PartDesign::Pad] Pad232
  BaseFeature = -> Pad231
  Direction = (0.669581,-0.227292,0.707107)
  Length = 0.2
  Length2 = 10
  Profile = -> Pad231 [Face17]
  Refine = true
  Suppressed = false
  Type = 0
FEATURE [PartDesign::Pad] Pad233
  BaseFeature = -> Pad232
  Direction = (0.466228,-0.531631,0.707107)
  Length = 0.2
  Length2 = 10
  Profile = -> Pad232 [Face99]
  Refine = true
  Suppressed = false
  Type = 0
FEATURE [PartDesign::Pad] Pad234
  BaseFeature = -> Pad233
  Direction = (-0.531631,-0.466228,0.707107)
  Length = 0.2
  Length2 = 10
  Profile = -> Pad233 [Face75]
  Refine = true
  Suppressed = false
  Type = 0
FEATURE [PartDesign::Pad] Pad235
  BaseFeature = -> Pad234
  Direction = (-0.392847,-0.587938,0.707107)
  Length = 0.2
  Length2 = 10
  Profile = -> Pad234 [Face79]
  Refine = true
  Suppressed = false
  Type = 0
FEATURE [PartDesign::Pad] Pad236
  BaseFeature = -> Pad235
  Direction = (-0.227292,-0.669581,0.707107)
  Length = 0.2
  Length2 = 10
  Profile = -> Pad235 [Face83]
  Refine = true
  Suppressed = false
  Type = 0
FEATURE [PartDesign::Pad] Pad237
  BaseFeature = -> Pad236
  Direction = (-0.046247,-0.705593,0.707107)
  Length = 0.2
  Length2 = 10
  Profile = -> Pad236 [Face87]
  Refine = true
  Suppressed = false
  Type = 0
FEATURE [PartDesign::Pad] Pad238
  BaseFeature = -> Pad237
  Direction = (0.312745,-0.634185,0.707107)
  Length = 0.2
  Length2 = 10
  Profile = -> Pad237 [Face95]
  Refine = true
  Suppressed = false
  Type = 0
FEATURE [PartDesign::Pad] Pad239
  BaseFeature = -> Pad238
  Direction = (0.13795,-0.69352,0.707107)
  Length = 0.2
  Length2 = 10
  Profile = -> Pad238 [Face91]
  Refine = true
  Suppressed = false
  Type = 0
FEATURE [Sketcher::SketchObject] Sketch333
  ArcFitTolerance = 1e-06
  AttachmentSupport = -> [Pad239]
  FullyConstrained = true
  MakeInternals = false
  MapMode = 5
  Placement = pos=(0,0,3.6) rot=(0,0,1;0rad)
  sketch-geometry (2):
    g0: Circle CenterX=0 CenterY=0 CenterZ=0 NormalX=0 NormalY=0 NormalZ=1 AngleXU=0 Radius=5.5
    g1: Circle CenterX=0 CenterY=0 CenterZ=0 NormalX=0 NormalY=0 NormalZ=1 AngleXU=0 Radius=4.5
  constraints (4):
    c: Coincident(g0,g-1)
    c: Diameter(g0) = 11
    c: Coincident(g1,g0)
    c: Diameter(g1) = 9
FEATURE [PartDesign::Pocket] Pocket153
  BaseFeature = -> Pad239
  Direction = (0,0,-1)
  Length = 5
  Length2 = 5
  Profile = -> Sketch333 [Edge2,Edge1]
  ReferenceAxis = -> Sketch333 [N_Axis]
  Refine = true
  Reversed = true
  Suppressed = false
  Type = 0
FEATURE [Sketcher::SketchObject] Sketch334
  ArcFitTolerance = 1e-06
  AttachmentSupport = -> [Pocket153]
  ExternalGeometry = -> [Pocket153]
  FullyConstrained = false
  MakeInternals = false
  MapMode = 5
  Placement = pos=(0,0,0) rot=(1,0,0;3.14159rad)
  sketch-geometry (2):
    g0: Circle CenterX=0 CenterY=0 CenterZ=0 NormalX=0 NormalY=0 NormalZ=1 AngleXU=0 Radius=6.05
    g1: Circle CenterX=0 CenterY=0 CenterZ=0 NormalX=0 NormalY=0 NormalZ=1 AngleXU=0 Radius=6.5
  constraints (3):
    c: Coincident(g0,g-1)
    c: Coincident(g1,g0)
    c: Diameter(g1) = 13
FEATURE [PartDesign::Pocket] Pocket154
  BaseFeature = -> Pocket153
  Direction = (0,0,1)
  Length = 5
  Length2 = 5
  Profile = -> Sketch334
  ReferenceAxis = -> Sketch334 [N_Axis]
  Refine = true
  Suppressed = false
  Type = 0
FEATURE [Sketcher::SketchObject] Sketch335
  ArcFitTolerance = 1e-06
  AttachmentSupport = -> [Pocket154]
  FullyConstrained = true
  MakeInternals = false
  MapMode = 5
  Placement = pos=(0,0,4.1) rot=(0,0,1;0rad)
  sketch-geometry (1):
    g0: Circle CenterX=0 CenterY=0 CenterZ=0 NormalX=0 NormalY=0 NormalZ=1 AngleXU=0 Radius=1.05
  constraints (2):
    c: Coincident(g0,g-1)
    c: Diameter(g0) = 2.1
FEATURE [PartDesign::Pocket] Pocket155
  BaseFeature = -> Pocket154
  Direction = (0,0,-1)
  Length = 5
  Length2 = 5
  Profile = -> Sketch335
  ReferenceAxis = -> Sketch335 [N_Axis]
  Refine = true
  Suppressed = false
  Type = 0
FEATURE [Sketcher::SketchObject] Sketch336
  ArcFitTolerance = 1e-06
  AttachmentSupport = -> [Pocket155]
  FullyConstrained = true
  MakeInternals = false
  MapMode = 5
  Placement = pos=(0,0,4.1) rot=(0,0,1;0rad)
  sketch-geometry (1):
    g0: Circle CenterX=0 CenterY=0 CenterZ=0 NormalX=0 NormalY=0 NormalZ=1 AngleXU=0 Radius=1.75
  constraints (2):
    c: Coincident(g0,g-1)
    c: Diameter(g0) = 3.5
FEATURE [PartDesign::Pocket] Pocket156
  BaseFeature = -> Pocket155
  Direction = (0,0,-1)
  Length = 1
  Length2 = 5
  Profile = -> Sketch336
  ReferenceAxis = -> Sketch336 [N_Axis]
  Refine = true
  Suppressed = false
  Type = 0
FEATURE [Sketcher::SketchObject] Sketch337
  ArcFitTolerance = 1e-06
  AttachmentSupport = -> [Pocket156]
  ExternalGeometry = -> [Pocket156]
  FullyConstrained = true
  MakeInternals = false
  MapMode = 5
  Placement = pos=(0,0,4.1) rot=(0,0,1;0rad)
  sketch-geometry (12):
    g0: Circle CenterX=0 CenterY=2.65 CenterZ=0 NormalX=0 NormalY=0 NormalZ=1 AngleXU=0 Radius=0.25
    g1: Circle CenterX=2.65 CenterY=0 CenterZ=0 NormalX=0 NormalY=0 NormalZ=1 AngleXU=0 Radius=0.25
    g2: Circle CenterX=0 CenterY=-2.65 CenterZ=0 NormalX=0 NormalY=0 NormalZ=1 AngleXU=0 Radius=0.25
    g3: Circle CenterX=-2.65 CenterY=0 CenterZ=0 NormalX=0 NormalY=0 NormalZ=1 AngleXU=0 Radius=0.25
    g4: Circle CenterX=1.87383 CenterY=1.87383 CenterZ=0 NormalX=0 NormalY=0 NormalZ=1 AngleXU=0 Radius=0.25
    g5: Circle CenterX=1.87383 CenterY=-1.87383 CenterZ=0 NormalX=0 NormalY=0 NormalZ=1 AngleXU=0 Radius=0.25
    g6: Circle CenterX=-1.87383 CenterY=-1.87383 CenterZ=0 NormalX=0 NormalY=0 NormalZ=1 AngleXU=0 Radius=0.25
    g7: Circle CenterX=-1.87383 CenterY=1.87383 CenterZ=0 NormalX=0 NormalY=0 NormalZ=1 AngleXU=0 Radius=0.25
    g8: LineSegment StartX=1.87383 StartY=1.87383 StartZ=0 EndX=0 EndY=0 EndZ=0
    g9: LineSegment StartX=0 StartY=0 StartZ=0 EndX=1.87383 EndY=-1.87383 EndZ=0
    g10: LineSegment StartX=0 StartY=0 StartZ=0 EndX=-1.87383 EndY=-1.87383 EndZ=0
    g11: LineSegment StartX=0 StartY=0 StartZ=0 EndX=-1.87383 EndY=1.87383 EndZ=0
  constraints (34):
    c: PointOnObject(g0,g-2)
    c: Diameter(g-3) = 7.1
    c: Diameter(g-4) = 3.5
    c: DistanceY(g-1,g0) = 2.65
    c: Diameter(g0) = 0.5
    c: PointOnObject(g1,g-1)
    c: PointOnObject(g2,g-2)
    c: PointOnObject(g3,g-1)
    c: Diameter(g3) = 0.5
    c: Diameter(g1) = 0.5
    c: Diameter(g2) = 0.5
    c: DistanceX(g3,g-1) = 2.65
    c: DistanceX(g-1,g1) = 2.65
    c: DistanceY(g2,g-1) = 2.65
    c: Diameter(g7) = 0.5
    c: Diameter(g4) = 0.5
    c: Diameter(g5) = 0.5
    c: Diameter(g6) = 0.5
    c: Distance(g-1,g6) = 2.65
    c: Distance(g-1,g5) = 2.65
    c: Distance(g-1,g4) = 2.65
    c: Distance(g-1,g7) = 2.65
    c: Coincident(g8,g4)
    c: Coincident(g8,g-1)
    c: Angle(g-1,g8) = 0.785398
    c: Coincident(g9,g8)
    c: Coincident(g9,g5)
    c: Coincident(g10,g8)
    c: Coincident(g10,g6)
    c: Coincident(g11,g8)
    c: Coincident(g11,g7)
    c: Angle(g9,g-1) = 0.785398
    c: Angle(g-2,g10) = 2.35619
    c: Angle(g-1,g11) = 2.35619
FEATURE [PartDesign::Pocket] Pocket157
  BaseFeature = -> Pocket156
  Direction = (0,0,-1)
  Length = 0.2
  Length2 = 5
  Profile = -> Sketch337 [Edge8,Edge4,Edge7,Edge3,Edge6,Edge2,Edge5,Edge1]
  ReferenceAxis = -> Sketch337 [N_Axis]
  Refine = true
  Suppressed = false
  Type = 0
FEATURE [Sketcher::SketchObject] Sketch338
  ArcFitTolerance = 1e-06
  AttachmentSupport = -> [Pocket157]
  FullyConstrained = true
  MakeInternals = false
  MapMode = 5
  Placement = pos=(0,0,0) rot=(1,0,0;3.14159rad)
  sketch-geometry (1):
    g0: Circle CenterX=0 CenterY=0 CenterZ=0 NormalX=0 NormalY=0 NormalZ=1 AngleXU=0 Radius=2.5
  constraints (2):
    c: Coincident(g0,g-1)
    c: Diameter(g0) = 5
FEATURE [PartDesign::Pocket] Pocket158
  BaseFeature = -> Pocket157
  Direction = (0,0,1)
  Length = 1.5
  Length2 = 5
  Profile = -> Sketch338
  ReferenceAxis = -> Sketch338 [N_Axis]
  Refine = true
  Suppressed = false
  Type = 0
FEATURE [Sketcher::SketchObject] Sketch339
  ArcFitTolerance = 1e-06
  AttachmentSupport = -> [Pocket158]
  FullyConstrained = true
  MakeInternals = false
  MapMode = 5
  Placement = pos=(0,0,0) rot=(1,0,0;3.14159rad)
  sketch-geometry (2):
    g0: Circle CenterX=0 CenterY=0 CenterZ=0 NormalX=0 NormalY=0 NormalZ=1 AngleXU=0 Radius=4.75
    g1: Circle CenterX=0 CenterY=0 CenterZ=0 NormalX=0 NormalY=0 NormalZ=1 AngleXU=0 Radius=5.5
  constraints (4):
    c: Coincident(g0,g-1)
    c: Coincident(g1,g0)
    c: Diameter(g0) = 9.5
    c: Diameter(g1) = 11
FEATURE [PartDesign::Pocket] Pocket159
  BaseFeature = -> Pocket158
  Direction = (0,0,1)
  Length = 1.5
  Length2 = 5
  Profile = -> Sketch339
  ReferenceAxis = -> Sketch339 [N_Axis]
  Refine = true
  Suppressed = false
  Type = 0
FEATURE [PartDesign::Body] Body023  label="Tire1"
  AllowCompound = false
  Group = -> [Sketch329,Pad213,Sketch330,Pad214,Sketch331,Pocket152,Sketch332,Pad215,Chamfer003,Pad216,Pad217,Pad218,Pad219,Pad220,Pad221,Pad222,Pad223,Pad224,Pad225,Pad226,Pad227,Pad228,Pad229,Pad230,Pad231,Pad232,Pad233,Pad234,Pad235,Pad236,Pad237,Pad238,Pad239,Sketch333,Pocket153,Sketch334,Pocket154,Sketch335,Pocket155,Sketch336,Pocket156,Sketch337,Pocket157,Sketch338,Pocket158,Sketch339,Pocket159]
  Origin = -> Origin024
  Placement = pos=(31.8,-26.27,-7) rot=(-0.707107,0,-0.707107;3.14159rad)
  Tip = -> Pocket159
FEATURE [App::Link] Link  label="Tire2"
  LinkPlacement = pos=(31.8,20.75,-7) rot=(0,1,0;1.5708rad)
  LinkedObject = -> Body023
  Placement = pos=(31.8,20.75,-7) rot=(0,1,0;1.5708rad)
FEATURE [App::Link] Link001  label="Tire3"
  LinkPlacement = pos=(31.8,33.96,-7) rot=(0,1,0;1.5708rad)
  LinkedObject = -> Body023
  Placement = pos=(31.8,33.96,-7) rot=(0,1,0;1.5708rad)
FEATURE [App::Link] Link002  label="Tire4"
  LinkPlacement = pos=(4.2,-26.3,-7) rot=(0,-1,0;1.5708rad)
  LinkedObject = -> Body023
  Placement = pos=(4.2,-26.3,-7) rot=(0,-1,0;1.5708rad)
FEATURE [App::Link] Link003  label="Tire5"
  LinkPlacement = pos=(4.4,20.75,-7) rot=(0,1,0;-1.5708rad)
  LinkedObject = -> Body023
  Placement = pos=(4.4,20.75,-7) rot=(0,1,0;-1.5708rad)
FEATURE [App::Link] Link004  label="Tire6"
  LinkPlacement = pos=(4.4,34,-7) rot=(0,1,0;-1.5708rad)
  LinkedObject = -> Body023
  Placement = pos=(4.4,34,-7) rot=(0,1,0;-1.5708rad)
FEATURE [PartDesign::Pad] Pad240
  BaseFeature = -> Pad100
  Direction = (0,0,-1)
  Length = 6.95
  Length2 = 10
  Profile = -> Pad100 [Face6]
  Refine = true
  Suppressed = false
  Type = 0
FEATURE [PartDesign::Chamfer] Chamfer004
  Angle = 45
  Base = -> Pocket025 [Edge136]
  BaseFeature = -> Pocket025
  ChamferType = 0
  FlipDirection = false
  Refine = true
  Size = 0.249
  Size2 = 1
  SupportTransform = false
  Suppressed = false
  UseAllEdges = false
FEATURE [PartDesign::Body] Body002  label="Outer_Left_Crane_Boom"
  AllowCompound = false
  Group = -> [Binder,Sketch036,Pad021,Sketch037,Pad022,Pad023,Sketch038,Pad024,Chamfer,Sketch039,Pad025,Sketch040,Pad026,Sketch041,Pocket016,Sketch042,Pad027,Sketch043,Pocket017,Sketch044,Pad028,Sketch045,Pad029,Sketch046,Pad030,Sketch047,Pad031,Sketch048,Pad032,Sketch049,Pad033,Pocket024,Pocket025,Chamfer004]
  Origin = -> Origin002
  Placement = pos=(19.43,-36.85,26.35) rot=(0.57735,0.57735,-0.57735;4.18879rad)
  Tip = -> Chamfer004
FEATURE [PartDesign::Chamfer] Chamfer005
  Angle = 45
  Base = -> Pocket027 [Edge127]
  BaseFeature = -> Pocket027
  ChamferType = 0
  FlipDirection = false
  Refine = true
  Size = 0.249
  Size2 = 1
  SupportTransform = false
  Suppressed = false
  UseAllEdges = false
FEATURE [PartDesign::Body] Body003  label="Pre_Outer_Right_Crane_Boom"
  AllowCompound = false
  Group = -> [Binder001,Sketch050,Pad034,Sketch051,Pad035,Pad036,Sketch052,Pad037,Chamfer001,Sketch053,Pad038,Sketch054,Pad039,Sketch055,Pocket018,Sketch056,Pad040,Sketch057,Pocket019,Sketch058,Pad041,Sketch059,Pad042,Sketch060,Pad043,Sketch061,Pad044,Sketch062,Pad045,Sketch063,Pad046,Pocket020,Pocket021,Sketch064,Pocket022,Pocket026,Pocket027,Chamfer005]
  Origin = -> Origin003
  Tip = -> Chamfer005
FEATURE [Part::Mirroring] Part__Mirroring  label="Outer_Right_Crane_Boom"
  Base = (0,0,0)
  Normal = (0,0,1)
  Placement = pos=(16.78,-36.85,26.35) rot=(0.57735,0.57735,-0.57735;4.18879rad)
  Source = -> Body003
FEATURE [Sketcher::SketchObject] Sketch340
  ArcFitTolerance = 1e-06
  AttachmentSupport = -> [Pocket023]
  ExternalGeometry = -> [Pocket023]
  FullyConstrained = true
  MakeInternals = false
  MapMode = 5
  Placement = pos=(0,0,0) rot=(1,0,0;3.14159rad)
  sketch-geometry (3):
    g0: LineSegment StartX=58.3 StartY=-4 StartZ=0 EndX=56.3 EndY=-4 EndZ=0
    g1: LineSegment StartX=56.3 StartY=-4 StartZ=0 EndX=58.3 EndY=-4.25 EndZ=0
    g2: LineSegment StartX=58.3 StartY=-4.25 StartZ=0 EndX=58.3 EndY=-4 EndZ=0
  constraints (8):
    c: Coincident(g0,g-4)
    c: PointOnObject(g0,g-4)
    c: Coincident(g1,g0)
    c: PointOnObject(g1,g-3)
    c: Coincident(g2,g1)
    c: Coincident(g2,g0)
    c: DistanceY(g2,g2) = 0.25
    c: DistanceX(g0,g0) = 2
FEATURE [PartDesign::Pad] Pad241
  BaseFeature = -> Pocket023
  Direction = (0,0,-1)
  Length = 2.75
  Length2 = 10
  Profile = -> Sketch340
  ReferenceAxis = -> Sketch340 [N_Axis]
  Refine = true
  Reversed = true
  Suppressed = false
  Type = 0
FEATURE [PartDesign::Body] Body001  label="Inner_Crane_Boom"
  AllowCompound = false
  Group = -> [Sketch028,Pad015,Sketch029,Pad016,Sketch030,Pad017,Sketch031,Pad018,Sketch032,Pocket014,Sketch033,Pad019,Sketch034,Pocket015,Sketch035,Pad020,Pocket023,Sketch340,Pad241]
  Origin = -> Origin001
  Placement = pos=(19.43,-36.85,26.85) rot=(0.57735,0.57735,-0.57735;4.18879rad)
  Tip = -> Pad241
FEATURE [Sketcher::SketchObject] Sketch341
  ArcFitTolerance = 1e-06
  AttachmentSupport = -> [Pad240]
  ExternalGeometry = -> [Pad240]
  FullyConstrained = true
  MakeInternals = false
  MapMode = 5
  Placement = pos=(0,0,3.5) rot=(1,0,0;3.14159rad)
  sketch-geometry (6):
    g0: LineSegment StartX=1.6 StartY=-31.7 StartZ=0 EndX=7 EndY=-31.7 EndZ=0
    g1: LineSegment StartX=7 StartY=-31.7 StartZ=0 EndX=7 EndY=-30.2 EndZ=0
    g2: LineSegment StartX=7 StartY=-30.2 StartZ=0 EndX=3.1 EndY=-30.2 EndZ=0
    g3: LineSegment StartX=3.1 StartY=-30.2 StartZ=0 EndX=3.1 EndY=-27.2 EndZ=0
    g4: LineSegment StartX=3.1 StartY=-27.2 StartZ=0 EndX=1.6 EndY=-27.2 EndZ=0
    g5: LineSegment StartX=1.6 StartY=-27.2 StartZ=0 EndX=1.6 EndY=-31.7 EndZ=0
  constraints (15):
    c: Coincident(g0,g1)
    c: Coincident(g1,g2)
    c: Vertical(g1)
    c: Horizontal(g0)
    c: Coincident(g1,g-3)
    c: Coincident(g3,g2)
    c: PointOnObject(g3,g-5)
    c: Coincident(g4,g3)
    c: PointOnObject(g4,g-6)
    c: Horizontal(g4)
    c: Coincident(g5,g4)
    c: Coincident(g5,g-6)
    c: Coincident(g0,g5)
    c: Coincident(g2,g-5)
    c: DistanceY(g3,g3) = 3
FEATURE [PartDesign::Pocket] Pocket160
  BaseFeature = -> Pad240
  Direction = (0,0,1)
  Length = 6.9
  Length2 = 5
  Profile = -> Sketch341
  ReferenceAxis = -> Sketch341 [N_Axis]
  Refine = true
  Suppressed = false
  Type = 0
FEATURE [PartDesign::Body] Body009  label="Rear_Windows"
  AllowCompound = false
  Group = -> [Binder004,Sketch129,Pad098,Sketch130,Pad099,Sketch131,Pad100,Pad240,Sketch341,Pocket160]
  Origin = -> Origin009
  Tip = -> Pocket160
FEATURE [PartDesign::Pad] Pad242
  BaseFeature = -> Pad125
  Direction = (3e-16,0,-1)
  Length = 0.1
  Length2 = 10
  Profile = -> Pad125 [Face9]
  Refine = true
  Suppressed = false
  Type = 0
FEATURE [PartDesign::Pad] Pad244
  BaseFeature = -> Pad212
  Direction = (3e-16,0,-1)
  Length = 0.1
  Length2 = 10
  Profile = -> Pad212 [Face9]
  Refine = true
  Suppressed = false
  Type = 0
FEATURE [PartDesign::Pad] Pad245
  BaseFeature = -> Pad244
  Direction = (0,0,1)
  Length = 0.05
  Length2 = 10
  Profile = -> Pad244 [Face3]
  Refine = true
  Suppressed = false
  Type = 0
FEATURE [PartDesign::Pad] Pad243
  BaseFeature = -> Pad242
  Direction = (0,0,1)
  Length = 0.05
  Length2 = 10
  Profile = -> Pad242 [Face3]
  Refine = true
  Suppressed = false
  Type = 0
FEATURE [Sketcher::SketchObject] Sketch342
  ArcFitTolerance = 1e-06
  AttachmentSupport = -> [Pocket093]
  ExternalGeometry = -> [Pocket093]
  FullyConstrained = true
  MakeInternals = false
  MapMode = 5
  Placement = pos=(-0.1,0,0) rot=(0.57735,-0.57735,-0.57735;2.0944rad)
  sketch-geometry (4):
    g0: LineSegment StartX=-7.3 StartY=0 StartZ=0 EndX=-4.3 EndY=0 EndZ=0
    g1: LineSegment StartX=-4.3 StartY=0 StartZ=0 EndX=-4.3 EndY=3 EndZ=0
    g2: LineSegment StartX=-4.3 StartY=3 StartZ=0 EndX=-7.3 EndY=3 EndZ=0
    g3: LineSegment StartX=-7.3 StartY=3 StartZ=0 EndX=-7.3 EndY=0 EndZ=0
  constraints (11):
    c: Coincident(g0,g1)
    c: Coincident(g1,g2)
    c: Coincident(g2,g3)
    c: Coincident(g3,g0)
    c: Horizontal(g0)
    c: Horizontal(g2)
    c: Vertical(g1)
    c: Vertical(g3)
    c: Coincident(g0,g-4)
    c: PointOnObject(g1,g-3)
    c: DistanceX(g2,g2) = 3
FEATURE [PartDesign::Pad] Pad246
  BaseFeature = -> Pocket093
  Direction = (-1,0,0)
  Length = 0.05
  Length2 = 10
  Profile = -> Sketch342
  ReferenceAxis = -> Sketch342 [N_Axis]
  Refine = true
  Suppressed = false
  Type = 0
FEATURE [Sketcher::SketchObject] Sketch343
  ArcFitTolerance = 1e-06
  AttachmentSupport = -> [Pad246]
  ExternalGeometry = -> [Pad246]
  FullyConstrained = true
  MakeInternals = false
  MapMode = 5
  Placement = pos=(8.1,0,0) rot=(0.57735,0.57735,0.57735;2.0944rad)
  sketch-geometry (4):
    g0: LineSegment StartX=7.3 StartY=0 StartZ=0 EndX=7.3 EndY=3 EndZ=0
    g1: LineSegment StartX=7.3 StartY=3 StartZ=0 EndX=4.3 EndY=3 EndZ=0
    g2: LineSegment StartX=4.3 StartY=3 StartZ=0 EndX=4.3 EndY=0 EndZ=0
    g3: LineSegment StartX=4.3 StartY=0 StartZ=0 EndX=7.3 EndY=0 EndZ=0
  constraints (11):
    c: Coincident(g0,g1)
    c: Coincident(g1,g2)
    c: Coincident(g2,g3)
    c: Coincident(g3,g0)
    c: Vertical(g0)
    c: Vertical(g2)
    c: Horizontal(g1)
    c: Horizontal(g3)
    c: Coincident(g0,g-4)
    c: PointOnObject(g1,g-3)
    c: DistanceX(g1,g1) = 3
FEATURE [PartDesign::Pad] Pad247
  BaseFeature = -> Pad246
  Direction = (1,0,0)
  Length = 0.05
  Length2 = 10
  Profile = -> Sketch343
  ReferenceAxis = -> Sketch343 [N_Axis]
  Refine = true
  Suppressed = false
  Type = 0
FEATURE [PartDesign::Body] Body013  label="Main_Head"
  AllowCompound = false
  Group = -> [Sketch190,Pad127,Sketch191,Pad128,Sketch192,Pad129,Sketch193,Pad130,Pocket088,Pad131,Pad132,Sketch195,Pad133,Sketch196,Pad134,Sketch197,Pad135,Sketch198,Pad136,Sketch199,Pocket089,Sketch200,Pad137,Sketch201,Pocket090,Sketch202,Pad138,Sketch203,Pocket091,Sketch204,Pocket092,Sketch205,Pad139,Fillet008,Sketch206,Pocket093,Sketch342,Pad246,Sketch343,Pad247]
  Origin = -> Origin013
  Placement = pos=(22,48.5,-4) rot=(0,0,1;3.14159rad)
  Tip = -> Pad247
FEATURE [Sketcher::SketchObject] Sketch344
  ArcFitTolerance = 1e-06
  AttachmentSupport = -> [Pocket095]
  ExternalGeometry = -> [Pocket095]
  FullyConstrained = true
  MakeInternals = false
  MapMode = 5
  Placement = pos=(0,0,-6.3) rot=(1,0,0;3.14159rad)
  sketch-geometry (4):
    g0: LineSegment StartX=18.3 StartY=-42.2 StartZ=0 EndX=18.3 EndY=-42.1 EndZ=0
    g1: LineSegment StartX=18.3 StartY=-42.1 StartZ=0 EndX=17.7 EndY=-42.1 EndZ=0
    g2: LineSegment StartX=17.7 StartY=-42.1 StartZ=0 EndX=17.7 EndY=-42.2 EndZ=0
    g3: LineSegment StartX=17.7 StartY=-42.2 StartZ=0 EndX=18.3 EndY=-42.2 EndZ=0
  constraints (10):
    c: Coincident(g0,g1)
    c: Coincident(g1,g2)
    c: Coincident(g2,g3)
    c: Coincident(g3,g0)
    c: Vertical(g0)
    c: Vertical(g2)
    c: Horizontal(g1)
    c: Horizontal(g3)
    c: Coincident(g0,g-4)
    c: Coincident(g1,g-3)
FEATURE [PartDesign::Pocket] Pocket161
  BaseFeature = -> Pocket095
  Direction = (0,0,1)
  Length = 0.2
  Length2 = 5
  Profile = -> Sketch344
  ReferenceAxis = -> Sketch344 [N_Axis]
  Refine = true
  Suppressed = false
  Type = 0
FEATURE [PartDesign::Body] Body014  label="Face"
  AllowCompound = false
  Group = -> [Binder008,Sketch207,Pad140,Sketch208,Pocket094,Sketch209,Pad141,Sketch210,Pad142,Sketch211,Pad143,Sketch212,Pocket095,Sketch344,Pocket161]
  Origin = -> Origin015
  Tip = -> Pocket161
FEATURE [App::Part] Part  label="Head"
  Group = -> [Body013,Body014]
  Origin = -> Origin014
  Placement = pos=(0,44,38) rot=(1,0,0;-1.5708rad)
FEATURE [PartDesign::Pad] Pad248
  BaseFeature = -> Pad171
  Direction = (1,0,0)
  Length = 0.05
  Length2 = 10
  Profile = -> Pad171 [Face43]
  Refine = true
  Suppressed = false
  Type = 0
FEATURE [Sketcher::SketchObject] Sketch345
  ArcFitTolerance = 1e-06
  AttachmentSupport = -> [Pad248]
  ExternalGeometry = -> [Pad248]
  FullyConstrained = true
  MakeInternals = false
  MapMode = 5
  Placement = pos=(0,-23.2313,0) rot=(0,0.707107,0.707107;3.14159rad)
  sketch-geometry (3):
    g0: LineSegment StartX=-23.3 StartY=-6.5 StartZ=0 EndX=-23.35 EndY=-6.5 EndZ=0
    g1: LineSegment StartX=-23.3 StartY=-6.5 StartZ=0 EndX=-23.35 EndY=-6.45 EndZ=0
    g2: LineSegment StartX=-23.35 StartY=-6.45 StartZ=0 EndX=-23.35 EndY=-6.5 EndZ=0
  constraints (7):
    c: Coincident(g0,g-3)
    c: Coincident(g0,g-4)
    c: Coincident(g1,g0)
    c: PointOnObject(g1,g-4)
    c: Coincident(g2,g1)
    c: Coincident(g2,g0)
    c: Angle(g-3,g1) = 3.14159
FEATURE [PartDesign::Pocket] Pocket162
  BaseFeature = -> Pad248
  Direction = (0,-1,2e-16)
  Length = 5
  Length2 = 5
  Profile = -> Sketch345
  ReferenceAxis = -> Sketch345 [N_Axis]
  Refine = true
  Suppressed = false
  Type = 0
FEATURE [PartDesign::Pad] Pad249
  BaseFeature = -> Pocket162
  Direction = (-1,0,0)
  Length = 0.05
  Length2 = 10
  Profile = -> Pocket162 [Face46]
  Refine = true
  Suppressed = false
  Type = 0
FEATURE [Sketcher::SketchObject] Sketch346
  ArcFitTolerance = 1e-06
  AttachmentSupport = -> [Pad249]
  ExternalGeometry = -> [Pad249]
  FullyConstrained = true
  MakeInternals = false
  MapMode = 5
  Placement = pos=(0,-39.505,0) rot=(1,0,0;1.5708rad)
  sketch-geometry (3):
    g0: LineSegment StartX=25.95 StartY=-5.2478 StartZ=0 EndX=25.9 EndY=-5.22961 EndZ=0
    g1: LineSegment StartX=25.9 StartY=-5.22961 StartZ=0 EndX=25.9 EndY=-5.2478 EndZ=0
    g2: LineSegment StartX=25.9 StartY=-5.2478 StartZ=0 EndX=25.95 EndY=-5.2478 EndZ=0
  constraints (7):
    c: Coincident(g0,g-3)
    c: PointOnObject(g0,g-5)
    c: Coincident(g1,g0)
    c: Coincident(g1,g-5)
    c: Coincident(g2,g-5)
    c: Coincident(g2,g-3)
    c: Angle(g-3,g0) = 3.14159
FEATURE [PartDesign::Pocket] Pocket163
  BaseFeature = -> Pad249
  Direction = (0,1,-2e-16)
  Length = 5
  Length2 = 5
  Profile = -> Sketch346
  ReferenceAxis = -> Sketch346 [N_Axis]
  Refine = true
  Suppressed = false
  Type = 0
FEATURE [PartDesign::Pad] Pad250
  BaseFeature = -> Pocket125
  Direction = (-1,0,0)
  Length = 0.05
  Length2 = 10
  Profile = -> Pocket125 [Face45]
  Refine = true
  Suppressed = false
  Type = 0
FEATURE [Sketcher::SketchObject] Sketch347
  ArcFitTolerance = 1e-06
  AttachmentSupport = -> [Pad250]
  ExternalGeometry = -> [Pad250]
  FullyConstrained = true
  MakeInternals = false
  MapMode = 5
  Placement = pos=(0,-39.505,0) rot=(1,0,0;1.5708rad)
  sketch-geometry (3):
    g0: LineSegment StartX=25.95 StartY=-5.2478 StartZ=0 EndX=25.9 EndY=-5.2478 EndZ=0
    g1: LineSegment StartX=25.9 StartY=-5.2478 StartZ=0 EndX=25.9 EndY=-5.22961 EndZ=0
    g2: LineSegment StartX=25.95 StartY=-5.2478 StartZ=0 EndX=25.9 EndY=-5.22961 EndZ=0
  constraints (7):
    c: Coincident(g0,g-4)
    c: Coincident(g0,g-5)
    c: Coincident(g1,g-5)
    c: PointOnObject(g1,g-5)
    c: Coincident(g2,g-4)
    c: Coincident(g2,g1)
    c: Angle(g-3,g2) = 3.14159
FEATURE [PartDesign::Pocket] Pocket164
  BaseFeature = -> Pad250
  Direction = (0,1,-2e-16)
  Length = 5
  Length2 = 5
  Profile = -> Sketch347
  ReferenceAxis = -> Sketch347 [N_Axis]
  Refine = true
  Suppressed = false
  Type = 0
FEATURE [PartDesign::Pad] Pad251
  BaseFeature = -> Pocket164
  Direction = (1,0,0)
  Length = 0.05
  Length2 = 10
  Profile = -> Pocket164 [Face42]
  Refine = true
  Suppressed = false
  Type = 0
FEATURE [Sketcher::SketchObject] Sketch348
  ArcFitTolerance = 1e-06
  AttachmentSupport = -> [Pad251]
  ExternalGeometry = -> [Pad251]
  FullyConstrained = true
  MakeInternals = false
  MapMode = 5
  Placement = pos=(0,-25.2313,0) rot=(1,0,0;1.5708rad)
  sketch-geometry (3):
    g0: LineSegment StartX=23.3 StartY=-6.5 StartZ=0 EndX=23.35 EndY=-6.45 EndZ=0
    g1: LineSegment StartX=23.35 StartY=-6.45 StartZ=0 EndX=23.35 EndY=-6.5 EndZ=0
    g2: LineSegment StartX=23.35 StartY=-6.5 StartZ=0 EndX=23.3 EndY=-6.5 EndZ=0
  constraints (7):
    c: Coincident(g0,g-5)
    c: PointOnObject(g0,g-3)
    c: Coincident(g1,g0)
    c: Coincident(g1,g-4)
    c: Coincident(g2,g1)
    c: Coincident(g2,g0)
    c: Angle(g-5,g0) = 3.14159
FEATURE [PartDesign::Pocket] Pocket165
  BaseFeature = -> Pad251
  Direction = (0,1,-2e-16)
  Length = 5
  Length2 = 5
  Profile = -> Sketch348
  ReferenceAxis = -> Sketch348 [N_Axis]
  Refine = true
  Suppressed = false
  Type = 0
FEATURE [PartDesign::Pad] Pad252
  BaseFeature = -> Pocket165
  Direction = (1,0,0)
  Length = 0.8
  Length2 = 10
  Profile = -> Pocket165 [Face54]
  Refine = true
  Suppressed = false
  Type = 0
FEATURE [PartDesign::Pad] Pad253
  BaseFeature = -> Pocket163
  Direction = (1,0,0)
  Length = 0.8
  Length2 = 10
  Profile = -> Pocket163 [Face58]
  Refine = true
  Suppressed = false
  Type = 0
FEATURE [Part::Feature] Part__Feature  label="Hook_Gun"
  Placement = pos=(-28,0,7) rot=(0.57735,-0.57735,0.57735;4.18879rad)
  shape: bbox 5.2 x 29.8 x 15.82 mm, 158 faces (baked)
FEATURE [Sketcher::SketchObject] Sketch349
  ArcFitTolerance = 1e-06
  AttachmentSupport = -> [Pad253]
  ExternalGeometry = -> [Pad253]
  FullyConstrained = true
  MakeInternals = false
  MapMode = 5
  Placement = pos=(31.25,0,0) rot=(0.57735,0.57735,0.57735;2.0944rad)
  sketch-geometry (1):
    g0: Circle CenterX=-35 CenterY=-1.99333 CenterZ=0 NormalX=0 NormalY=0 NormalZ=1 AngleXU=0 Radius=0.9
  constraints (2):
    c: Coincident(g0,g-3)
    c: Radius(g0) = 0.9
FEATURE [PartDesign::Pocket] Pocket166
  BaseFeature = -> Pad253
  Direction = (-1,0,0)
  Length = 5
  Length2 = 5
  Profile = -> Sketch349
  ReferenceAxis = -> Sketch349 [N_Axis]
  Refine = true
  Suppressed = false
  Type = 1
FEATURE [Sketcher::SketchObject] Sketch350
  ArcFitTolerance = 1e-06
  AttachmentSupport = -> [Pocket166]
  ExternalGeometry = -> [Pocket166]
  FullyConstrained = true
  MakeInternals = false
  MapMode = 5
  Placement = pos=(33.25,0,0) rot=(0.57735,0.57735,0.57735;2.0944rad)
  sketch-geometry (1):
    g0: Circle CenterX=-26.2738 CenterY=-7 CenterZ=0 NormalX=0 NormalY=0 NormalZ=1 AngleXU=0 Radius=0.9
  constraints (2):
    c: Coincident(g0,g-3)
    c: Radius(g0) = 0.9
FEATURE [PartDesign::Pocket] Pocket167
  BaseFeature = -> Pocket166
  Direction = (-1,0,0)
  Length = 4
  Length2 = 5
  Profile = -> Sketch350
  ReferenceAxis = -> Sketch350 [N_Axis]
  Refine = true
  Suppressed = false
  Type = 0
FEATURE [PartDesign::Body] Body016  label="Right_Inner_Leg"
  AllowCompound = false
  Group = -> [Binder010,Sketch246,Pad161,Sketch247,Pad162,Sketch248,Pad163,Sketch249,Pad164,Sketch250,Pocket114,Sketch251,Pocket115,Sketch252,Pad165,Sketch253,Pocket116,Sketch254,Pocket117,Sketch255,Pad166,Sketch256,Pocket118,Sketch257,Pad167,Sketch258,Pad168,Sketch259,Pad169,Sketch260,Pocket119,Sketch261,Pad170,Sketch262,Pad171,Pad248,Sketch345,Pocket162,Pad249,Sketch346,Pocket163,Pad253,Sketch349,Pocket166,+2 more]
  Origin = -> Origin017
  Placement = pos=(0,8.9e-15,0) rot=(0,0,1;0rad)
  Tip = -> Pocket167
FEATURE [Sketcher::SketchObject] Sketch351
  ArcFitTolerance = 1e-06
  AttachmentSupport = -> [Pad252]
  ExternalGeometry = -> [Pad252]
  FullyConstrained = true
  MakeInternals = false
  MapMode = 5
  Placement = pos=(31.25,0,0) rot=(0.57735,0.57735,0.57735;2.0944rad)
  sketch-geometry (1):
    g0: Circle CenterX=-35 CenterY=-1.99333 CenterZ=0 NormalX=0 NormalY=0 NormalZ=1 AngleXU=0 Radius=0.9
  constraints (2):
    c: Coincident(g0,g-3)
    c: Radius(g0) = 0.9
FEATURE [PartDesign::Pocket] Pocket168
  BaseFeature = -> Pad252
  Direction = (-1,0,0)
  Length = 5
  Length2 = 5
  Profile = -> Sketch351
  ReferenceAxis = -> Sketch351 [N_Axis]
  Refine = true
  Suppressed = false
  Type = 1
FEATURE [Sketcher::SketchObject] Sketch352
  ArcFitTolerance = 1e-06
  AttachmentSupport = -> [Pocket168]
  ExternalGeometry = -> [Pocket168]
  FullyConstrained = true
  MakeInternals = false
  MapMode = 5
  Placement = pos=(33.25,0,0) rot=(0.57735,0.57735,0.57735;2.0944rad)
  sketch-geometry (1):
    g0: Circle CenterX=-26.2738 CenterY=-7 CenterZ=0 NormalX=0 NormalY=0 NormalZ=1 AngleXU=0 Radius=0.9
  constraints (2):
    c: Coincident(g0,g-3)
    c: Radius(g0) = 0.9
FEATURE [PartDesign::Pocket] Pocket169
  BaseFeature = -> Pocket168
  Direction = (-1,0,0)
  Length = 4
  Length2 = 5
  Profile = -> Sketch352
  ReferenceAxis = -> Sketch352 [N_Axis]
  Refine = true
  Suppressed = false
  Type = 0
FEATURE [PartDesign::Body] Body017  label="Pre_Left_Inner_Leg"
  AllowCompound = false
  Group = -> [Binder011,Sketch263,Pad172,Sketch264,Pad173,Sketch265,Pad174,Sketch266,Pad175,Sketch267,Pocket120,Sketch268,Pocket121,Sketch269,Pad176,Sketch270,Pocket122,Sketch271,Pocket123,Sketch272,Pad177,Sketch273,Pocket124,Sketch274,Pad178,Sketch275,Pad179,Sketch276,Pad180,Sketch277,Pocket125,Pad250,Sketch347,Pocket164,Pad251,Sketch348,Pocket165,Pad252,Sketch351,Pocket168,Sketch352,Pocket169]
  Origin = -> Origin018
  Tip = -> Pocket169
FEATURE [Part::Mirroring] Part__Mirroring001  label="Left_Inner_Leg"
  Base = (0,0,0)
  Normal = (1,0,0)
  Placement = pos=(36,0,0) rot=(0,0,1;0rad)
  Source = -> Body017
FEATURE [Sketcher::SketchObject] Sketch353
  ArcFitTolerance = 1e-06
  AttachmentSupport = -> [Pocket113]
  ExternalGeometry = -> [Pocket113]
  FullyConstrained = true
  MakeInternals = false
  MapMode = 5
  Placement = pos=(6.75,0,-1.7e-15) rot=(0.57735,-0.57735,-0.57735;2.0944rad)
  sketch-geometry (1):
    g0: Circle CenterX=35 CenterY=-1.99333 CenterZ=0 NormalX=0 NormalY=0 NormalZ=1 AngleXU=0 Radius=0.9
  constraints (2):
    c: Coincident(g0,g-3)
    c: Radius(g0) = 0.9
FEATURE [PartDesign::Pocket] Pocket170
  BaseFeature = -> Pocket113
  Direction = (1,0,0)
  Length = 5
  Length2 = 5
  Profile = -> Sketch353
  ReferenceAxis = -> Sketch353 [N_Axis]
  Refine = true
  Suppressed = false
  Type = 1
FEATURE [PartDesign::Body] Body015  label="Legs"
  AllowCompound = false
  Group = -> [Binder009,Sketch213,Pad144,Sketch214,Pocket096,Sketch215,Pad145,Sketch216,Pocket097,Sketch217,Pad146,Sketch218,Pad147,Sketch219,Pad148,Sketch220,Pocket098,Sketch221,Pad149,Sketch222,Pocket099,Sketch223,Pocket100,Sketch224,Pocket101,Sketch225,Pad150,Sketch226,Pocket102,Sketch227,Pocket103,Sketch228,Pad151,Sketch229,Pocket104,Sketch230,Pad152,Sketch231,Pocket105,Sketch232,Pocket106,Sketch233,+33 more]
  Origin = -> Origin016
  Placement = pos=(0,8.9e-15,0) rot=(0,0,1;0rad)
  Tip = -> Pocket170
FEATURE [Sketcher::SketchObject] Sketch354
  ArcFitTolerance = 1e-06
  AttachmentSupport = -> [Pad243]
  ExternalGeometry = -> [Pad243]
  FullyConstrained = true
  MakeInternals = false
  MapMode = 5
  Placement = pos=(2.1e-15,0,-7.35) rot=(1,0,0;3.14159rad)
  sketch-geometry (12):
    g0: LineSegment StartX=16.3 StartY=-25.15 StartZ=0 EndX=16.3 EndY=-26.3 EndZ=0
    g1: LineSegment StartX=16.3 StartY=-26.3 StartZ=0 EndX=17.3 EndY=-26.3 EndZ=0
    g2: LineSegment StartX=17.3 StartY=-26.3 StartZ=0 EndX=17.3 EndY=-25.15 EndZ=0
    g3: LineSegment StartX=17.3 StartY=-25.15 StartZ=0 EndX=16.3 EndY=-25.15 EndZ=0
    g4: LineSegment StartX=12 StartY=-28.3 StartZ=0 EndX=12 EndY=-32.4 EndZ=0
    g5: LineSegment StartX=12 StartY=-32.4 StartZ=0 EndX=17.3 EndY=-32.4 EndZ=0
    g6: LineSegment StartX=17.3 StartY=-32.4 StartZ=0 EndX=17.3 EndY=-28.3 EndZ=0
    g7: LineSegment StartX=17.3 StartY=-28.3 StartZ=0 EndX=12 EndY=-28.3 EndZ=0
    g8: LineSegment StartX=16.3 StartY=-34.4 StartZ=0 EndX=16.3 EndY=-35.55 EndZ=0
    g9: LineSegment StartX=16.3 StartY=-35.55 StartZ=0 EndX=17.3 EndY=-35.55 EndZ=0
    g10: LineSegment StartX=17.3 StartY=-35.55 StartZ=0 EndX=17.3 EndY=-34.4 EndZ=0
    g11: LineSegment StartX=17.3 StartY=-34.4 StartZ=0 EndX=16.3 EndY=-34.4 EndZ=0
  constraints (34):
    c: Coincident(g0,g1)
    c: Coincident(g1,g2)
    c: Coincident(g2,g3)
    c: Coincident(g3,g0)
    c: Vertical(g0)
    c: Vertical(g2)
    c: Horizontal(g1)
    c: Horizontal(g3)
    c: Coincident(g0,g-8)
    c: PointOnObject(g1,g-4)
    c: Coincident(g4,g5)
    c: Coincident(g5,g6)
    c: Coincident(g6,g7)
    c: Coincident(g7,g4)
    c: Vertical(g4)
    c: Vertical(g6)
    c: Horizontal(g5)
    c: Horizontal(g7)
    c: PointOnObject(g4,g-5)
    c: PointOnObject(g5,g-4)
    c: Coincident(g8,g9)
    c: Coincident(g9,g10)
    c: Coincident(g10,g11)
    c: Coincident(g11,g8)
    c: Vertical(g8)
    c: Vertical(g10)
    c: Horizontal(g9)
    c: Horizontal(g11)
    c: PointOnObject(g8,g-9)
    c: Coincident(g9,g-10)
    c: DistanceY(g8,g8) = 1.15
    c: DistanceY(g10,g5) = 2
    c: DistanceY(g6,g1) = 2
    c: DistanceY(g1,g2) = 1.15
FEATURE [PartDesign::Pad] Pad254
  BaseFeature = -> Pad243
  Direction = (0,0,-1)
  Length = 0.6
  Length2 = 10
  Profile = -> Sketch354
  ReferenceAxis = -> Sketch354 [N_Axis]
  Refine = true
  Suppressed = false
  Type = 0
FEATURE [PartDesign::Body] Body012  label="Left_Shoulder"
  AllowCompound = false
  Group = -> [Binder007,Sketch185,Pad123,Sketch186,Pocket086,Sketch187,Pad124,Sketch188,Pad125,Pad242,Pad243,Sketch354,Pad254]
  Origin = -> Origin012
  Tip = -> Pad254
FEATURE [Sketcher::SketchObject] Sketch355
  ArcFitTolerance = 1e-06
  AttachmentSupport = -> [Pad245]
  ExternalGeometry = -> [Pad245]
  FullyConstrained = true
  MakeInternals = false
  MapMode = 5
  Placement = pos=(2.1e-15,0,-7.35) rot=(1,0,0;3.14159rad)
  sketch-geometry (12):
    g0: LineSegment StartX=12 StartY=-28.3 StartZ=0 EndX=12 EndY=-32.4 EndZ=0
    g1: LineSegment StartX=12 StartY=-32.4 StartZ=0 EndX=17.3 EndY=-32.4 EndZ=0
    g2: LineSegment StartX=17.3 StartY=-32.4 StartZ=0 EndX=17.3 EndY=-28.3 EndZ=0
    g3: LineSegment StartX=17.3 StartY=-28.3 StartZ=0 EndX=12 EndY=-28.3 EndZ=0
    g4: LineSegment StartX=16.3 StartY=-25.15 StartZ=0 EndX=16.3 EndY=-26.3 EndZ=0
    g5: LineSegment StartX=16.3 StartY=-26.3 StartZ=0 EndX=17.3 EndY=-26.3 EndZ=0
    g6: LineSegment StartX=17.3 StartY=-26.3 StartZ=0 EndX=17.3 EndY=-25.15 EndZ=0
    g7: LineSegment StartX=17.3 StartY=-25.15 StartZ=0 EndX=16.3 EndY=-25.15 EndZ=0
    g8: LineSegment StartX=16.3 StartY=-35.55 StartZ=0 EndX=17.3 EndY=-35.55 EndZ=0
    g9: LineSegment StartX=17.3 StartY=-35.55 StartZ=0 EndX=17.3 EndY=-34.4 EndZ=0
    g10: LineSegment StartX=17.3 StartY=-34.4 StartZ=0 EndX=16.3 EndY=-34.4 EndZ=0
    g11: LineSegment StartX=16.3 StartY=-34.4 StartZ=0 EndX=16.3 EndY=-35.55 EndZ=0
  constraints (34):
    c: Coincident(g0,g1)
    c: Coincident(g1,g2)
    c: Coincident(g2,g3)
    c: Coincident(g3,g0)
    c: Vertical(g0)
    c: Vertical(g2)
    c: Horizontal(g1)
    c: Horizontal(g3)
    c: PointOnObject(g0,g-10)
    c: PointOnObject(g1,g-6)
    c: Coincident(g4,g5)
    c: Coincident(g5,g6)
    c: Coincident(g6,g7)
    c: Coincident(g7,g4)
    c: Vertical(g4)
    c: Vertical(g6)
    c: Horizontal(g5)
    c: Horizontal(g7)
    c: Coincident(g4,g-4)
    c: PointOnObject(g5,g-6)
    c: Coincident(g8,g9)
    c: Coincident(g9,g10)
    c: Coincident(g10,g11)
    c: Coincident(g11,g8)
    c: Horizontal(g8)
    c: Horizontal(g10)
    c: Vertical(g9)
    c: Vertical(g11)
    c: Coincident(g8,g-8)
    c: PointOnObject(g9,g-6)
    c: DistanceY(g11,g11) = 1.15
    c: DistanceY(g4,g4) = 1.15
    c: DistanceY(g2,g5) = 2
    c: DistanceY(g9,g1) = 2
FEATURE [PartDesign::Pad] Pad255
  BaseFeature = -> Pad245
  Direction = (0,0,-1)
  Length = 0.6
  Length2 = 10
  Profile = -> Sketch355
  ReferenceAxis = -> Sketch355 [N_Axis]
  Refine = true
  Suppressed = false
  Type = 0
FEATURE [PartDesign::Body] Body022  label="Pre_Right_Shoulder"
  AllowCompound = false
  Group = -> [Binder016,Sketch325,Pad210,Sketch326,Pocket151,Sketch327,Pad211,Sketch328,Pad212,Pad244,Pad245,Sketch355,Pad255]
  Origin = -> Origin023
  Tip = -> Pad255
FEATURE [Part::Mirroring] Part__Mirroring003  label="Right_Shoulder"
  Base = (0,0,0)
  Normal = (1,0,0)
  Placement = pos=(36,0,0) rot=(0,0,1;0rad)
  Source = -> Body022
